FCSTD DOCUMENT  (FreeCAD 0.18.4R)
Label: voron-0
License: CreativeCommons Attribution-ShareAlike
LicenseURL: http://creativecommons.org/licenses/by-sa/4.0/
objects: Part::Feature×202, App::Part×102, Sketcher::SketchObject×45, PartDesign::Pad×42, PartDesign::Body×37, Mesh::Feature×32, App::DocumentObjectGroup×5, PartDesign::ShapeBinder×4, PartDesign::Line×4, App::DocumentObjectGroupPython×1, PartDesign::Hole×1, PartDesign::Pocket×1
note: 380 computed .brp shape members not serialized (recipe doc carries the construction recipe); baked Part::Feature solids carry a one-line shape summary decoded from their .brp

FEATURE [App::DocumentObjectGroupPython] ExplodedAssembly  # scripted group (container) (typed FeaturePython)
  AnimationStep = 0
  CurrentTrajectory = 0
  InAnimation = false
  RemoveAllTrajectories = false
  ResetAnimation = false
FEATURE [Sketcher::SketchObject] Sketch
  MapMode = 5
  Support = -> [XY_Plane001]
  sketch-geometry (4):
    g0: LineSegment StartX=-115 StartY=115 StartZ=0 EndX=115 EndY=115 EndZ=0
    g1: LineSegment StartX=115 StartY=115 StartZ=0 EndX=115 EndY=-115 EndZ=0
    g2: LineSegment StartX=115 StartY=-115 StartZ=0 EndX=-115 EndY=-115 EndZ=0
    g3: LineSegment StartX=-115 StartY=-115 StartZ=0 EndX=-115 EndY=115 EndZ=0
  constraints (11):
    c: Coincident(g0,g1)
    c: Coincident(g1,g2)
    c: Coincident(g2,g3)
    c: Coincident(g3,g0)
    c: Horizontal(g0)
    c: Horizontal(g2)
    c: Vertical(g1)
    c: Vertical(g3)
    c: Symmetric(g0,g1,g-1)
    c: Equal(g3,g0)
    c: DistanceY(g3,g3) = 230
FEATURE [PartDesign::Pad] Pad
  Length = 280
  Length2 = 100
  Midplane = true
  Profile = -> Sketch
  Refine = true
  Type = 0
FEATURE [PartDesign::Body] Body
  Group = -> [Sketch,Pad]
  Origin = -> Origin001
  Tip = -> Pad
FEATURE [Sketcher::SketchObject] Sketch001
  MapMode = 5
  Placement = pos=(0,0,0) rot=(1,0,0;1.5708rad)
  Support = -> [XZ_Plane004]
  sketch-geometry (52):
    g0: LineSegment [constr] StartX=-7.5 StartY=7.5 StartZ=0 EndX=7.5 EndY=7.5 EndZ=0
    g1: LineSegment [constr] StartX=7.5 StartY=7.5 StartZ=0 EndX=7.5 EndY=-7.5 EndZ=0
    g2: LineSegment [constr] StartX=7.5 StartY=-7.5 StartZ=0 EndX=-7.5 EndY=-7.5 EndZ=0
    g3: LineSegment [constr] StartX=-7.5 StartY=-7.5 StartZ=0 EndX=-7.5 EndY=7.5 EndZ=0
    g4: LineSegment StartX=-2.09289 StartY=2.8 StartZ=0 EndX=2.09289 EndY=2.8 EndZ=0
    g5: LineSegment StartX=2.09289 StartY=2.8 StartZ=0 EndX=4.7 EndY=5.40711 EndZ=0
    g6: LineSegment StartX=4.7 StartY=5.40711 StartZ=0 EndX=4.7 EndY=6.5 EndZ=0
    g7: LineSegment StartX=4.7 StartY=6.5 StartZ=0 EndX=3.1 EndY=6.5 EndZ=0
    g8: LineSegment StartX=3.1 StartY=6.5 StartZ=0 EndX=3.1 EndY=7.5 EndZ=0
    g9: LineSegment StartX=3.1 StartY=7.5 StartZ=0 EndX=6.5 EndY=7.5 EndZ=0
    g10: LineSegment StartX=7.5 StartY=6.5 StartZ=0 EndX=7.5 EndY=3.1 EndZ=0
    g11: LineSegment StartX=7.5 StartY=3.1 StartZ=0 EndX=6.5 EndY=3.1 EndZ=0
    g12: LineSegment StartX=6.5 StartY=3.1 StartZ=0 EndX=6.5 EndY=4.7 EndZ=0
    g13: LineSegment StartX=6.5 StartY=4.7 StartZ=0 EndX=5.40711 EndY=4.7 EndZ=0
    g14: LineSegment StartX=5.40711 StartY=4.7 StartZ=0 EndX=2.8 EndY=2.09289 EndZ=0
    g15: LineSegment StartX=2.8 StartY=2.09289 StartZ=0 EndX=2.8 EndY=-2.09289 EndZ=0
    g16: LineSegment StartX=2.8 StartY=-2.09289 StartZ=0 EndX=5.40711 EndY=-4.7 EndZ=0
    g17: LineSegment StartX=5.40711 StartY=-4.7 StartZ=0 EndX=6.5 EndY=-4.7 EndZ=0
    g18: LineSegment StartX=6.5 StartY=-4.7 StartZ=0 EndX=6.5 EndY=-3.1 EndZ=0
    g19: LineSegment StartX=6.5 StartY=-3.1 StartZ=0 EndX=7.5 EndY=-3.1 EndZ=0
    g20: LineSegment StartX=7.5 StartY=-3.1 StartZ=0 EndX=7.5 EndY=-6.5 EndZ=0
    g21: LineSegment StartX=6.5 StartY=-7.5 StartZ=0 EndX=3.1 EndY=-7.5 EndZ=0
    g22: LineSegment StartX=3.1 StartY=-7.5 StartZ=0 EndX=3.1 EndY=-6.5 EndZ=0
    g23: LineSegment StartX=3.1 StartY=-6.5 StartZ=0 EndX=4.7 EndY=-6.5 EndZ=0
    g24: LineSegment StartX=4.7 StartY=-6.5 StartZ=0 EndX=4.7 EndY=-5.40711 EndZ=0
    g25: LineSegment StartX=4.7 StartY=-5.40711 StartZ=0 EndX=2.09289 EndY=-2.8 EndZ=0
    g26: LineSegment StartX=2.09289 StartY=-2.8 StartZ=0 EndX=-2.09289 EndY=-2.8 EndZ=0
    g27: LineSegment StartX=-2.09289 StartY=-2.8 StartZ=0 EndX=-4.7 EndY=-5.40711 EndZ=0
    g28: LineSegment StartX=-4.7 StartY=-5.40711 StartZ=0 EndX=-4.7 EndY=-6.5 EndZ=0
    g29: LineSegment StartX=-4.7 StartY=-6.5 StartZ=0 EndX=-3.1 EndY=-6.5 EndZ=0
    g30: LineSegment StartX=-3.1 StartY=-6.5 StartZ=0 EndX=-3.1 EndY=-7.5 EndZ=0
    g31: LineSegment StartX=-3.1 StartY=-7.5 StartZ=0 EndX=-6.5 EndY=-7.5 EndZ=0
    g32: LineSegment StartX=-7.5 StartY=-6.5 StartZ=0 EndX=-7.5 EndY=-3.1 EndZ=0
    g33: LineSegment StartX=-7.5 StartY=-3.1 StartZ=0 EndX=-6.5 EndY=-3.1 EndZ=0
    g34: LineSegment StartX=-6.5 StartY=-3.1 StartZ=0 EndX=-6.5 EndY=-4.7 EndZ=0
    g35: LineSegment StartX=-6.5 StartY=-4.7 StartZ=0 EndX=-5.40711 EndY=-4.7 EndZ=0
    g36: LineSegment StartX=-5.40711 StartY=-4.7 StartZ=0 EndX=-2.8 EndY=-2.09289 EndZ=0
    g37: LineSegment StartX=-2.8 StartY=-2.09289 StartZ=0 EndX=-2.8 EndY=2.09289 EndZ=0
    g38: LineSegment StartX=-2.8 StartY=2.09289 StartZ=0 EndX=-5.40711 EndY=4.7 EndZ=0
    g39: LineSegment StartX=-5.40711 StartY=4.7 StartZ=0 EndX=-6.5 EndY=4.7 EndZ=0
    g40: LineSegment StartX=-6.5 StartY=4.7 StartZ=0 EndX=-6.5 EndY=3.1 EndZ=0
    g41: LineSegment StartX=-6.5 StartY=3.1 StartZ=0 EndX=-7.5 EndY=3.1 EndZ=0
    g42: LineSegment StartX=-7.5 StartY=3.1 StartZ=0 EndX=-7.5 EndY=6.5 EndZ=0
    g43: LineSegment StartX=-6.5 StartY=7.5 StartZ=0 EndX=-3.1 EndY=7.5 EndZ=0
    g44: LineSegment StartX=-3.1 StartY=7.5 StartZ=0 EndX=-3.1 EndY=6.5 EndZ=0
    g45: LineSegment StartX=-3.1 StartY=6.5 StartZ=0 EndX=-4.7 EndY=6.5 EndZ=0
    g46: LineSegment StartX=-4.7 StartY=6.5 StartZ=0 EndX=-4.7 EndY=5.40711 EndZ=0
    g47: LineSegment StartX=-4.7 StartY=5.40711 StartZ=0 EndX=-2.09289 EndY=2.8 EndZ=0
    g48: ArcOfCircle CenterX=-6.5 CenterY=6.5 CenterZ=0 NormalX=0 NormalY=0 NormalZ=1 AngleXU=0 Radius=1 StartAngle=1.5708 EndAngle=3.14159
    g49: ArcOfCircle CenterX=6.5 CenterY=6.5 CenterZ=0 NormalX=0 NormalY=0 NormalZ=1 AngleXU=0 Radius=1 StartAngle=0 EndAngle=1.5708
    g50: ArcOfCircle CenterX=6.5 CenterY=-6.5 CenterZ=0 NormalX=0 NormalY=0 NormalZ=1 AngleXU=0 Radius=1 StartAngle=4.71239 EndAngle=6.28319
    g51: ArcOfCircle CenterX=-6.5 CenterY=-6.5 CenterZ=0 NormalX=0 NormalY=0 NormalZ=1 AngleXU=0 Radius=1 StartAngle=3.14159 EndAngle=4.71239
  constraints (140):
    c: Coincident(g0,g1)
    c: Coincident(g1,g2)
    c: Coincident(g2,g3)
    c: Coincident(g3,g0)
    c: Horizontal(g0)
    c: Horizontal(g2)
    c: Vertical(g1)
    c: Vertical(g3)
    c: Symmetric(g0,g1,g-1)
    c: Equal(g3,g0)
    c: DistanceY(g3,g3) = 15
    c: Coincident(g4,g5)
    c: Coincident(g5,g6)
    c: Coincident(g6,g7)
    c: Coincident(g7,g8)
    c: Vertical(g8)
    c: Coincident(g8,g9)
    c: Horizontal(g9)
    c: Vertical(g10)
    c: Coincident(g10,g11)
    c: Horizontal(g11)
    c: Coincident(g11,g12)
    c: Vertical(g12)
    c: Coincident(g12,g13)
    c: Horizontal(g13)
    c: Coincident(g13,g14)
    c: Coincident(g14,g15)
    c: Coincident(g15,g16)
    c: Coincident(g16,g17)
    c: Horizontal(g17)
    c: Coincident(g17,g18)
    c: Coincident(g18,g19)
    c: Coincident(g19,g20)
    c: Vertical(g20)
    c: Horizontal(g21)
    c: Coincident(g21,g22)
    c: Coincident(g22,g23)
    c: Horizontal(g23)
    c: Coincident(g23,g24)
    c: Coincident(g24,g25)
    c: Coincident(g25,g26)
    c: Coincident(g26,g27)
    c: Coincident(g27,g28)
    c: Vertical(g28)
    c: Coincident(g28,g29)
    c: Coincident(g29,g30)
    c: Coincident(g30,g31)
    c: Coincident(g32,g33)
    c: Coincident(g33,g34)
    c: Coincident(g34,g35)
    c: Coincident(g35,g36)
    c: Coincident(g36,g37)
    c: Coincident(g37,g38)
    c: Coincident(g38,g39)
    c: Coincident(g39,g40)
    c: Coincident(g40,g41)
    c: Coincident(g41,g42)
    c: Vertical(g42)
    c: Horizontal(g43)
    c: Coincident(g43,g44)
    c: Coincident(g44,g45)
    c: Horizontal(g45)
    c: Coincident(g45,g46)
    c: Coincident(g46,g47)
    c: Coincident(g4,g47)
    c: Tangent(g42,g48) = 1.5708
    c: Tangent(g43,g48) = 1.5708
    c: Tangent(g9,g49) = 1.5708
    c: Tangent(g10,g49) = 1.5708
    c: Tangent(g20,g50) = 1.5708
    c: Tangent(g21,g50) = 1.5708
    c: Tangent(g32,g51) = 1.5708
    c: Tangent(g31,g51) = 1.5708
    c: Horizontal(g41)
    c: Horizontal(g39)
    c: Horizontal(g19)
    c: Horizontal(g31)
    c: Horizontal(g35)
    c: Horizontal(g33)
    c: Vertical(g40)
    c: Vertical(g46)
    c: Vertical(g18)
    c: Vertical(g22)
    c: Vertical(g24)
    c: Vertical(g30)
    c: Vertical(g34)
    c: Vertical(g32)
    c: PointOnObject(g21,g2)
    c: PointOnObject(g32,g3)
    c: Vertical(g6)
    c: PointOnObject(g10,g1)
    c: Equal(g48,g49)
    c: Equal(g49,g50)
    c: Equal(g33,g41)
    c: Equal(g41,g30)
    c: Equal(g30,g22)
    c: Equal(g22,g19)
    c: Equal(g19,g11)
    c: Equal(g11,g8)
    c: Equal(g8,g44)
    c: Symmetric(g45,g6,g-2)
    c: DistanceX(g45,g6) = 9.4
    c: DistanceX(g43,g8) = 6.2
    c: Equal(g43,g42)
    c: Equal(g42,g32)
    c: DistanceY(g44,g44) = 1
    c: Equal(g31,g43)
    c: Equal(g43,g21)
    c: Equal(g21,g20)
    c: Equal(g20,g10)
    c: Radius(g49) = 1
    c: Symmetric(g37,g14,g-2)
    c: DistanceX(g37,g14) = 5.6
    c: Symmetric(g43,g8,g-2)
    c: Symmetric(g4,g26,g-1)
    c: DistanceY(g26,g4) = 5.6
    c: Symmetric(g4,g4,g-2)
    c: Equal(g45,g40)
    c: Equal(g45,g7)
    c: Equal(g7,g12)
    c: Equal(g12,g34)
    c: Equal(g34,g29)
    c: Equal(g29,g23)
    c: Equal(g23,g18)
    c: Equal(g39,g46)
    c: Equal(g46,g6)
    c: Equal(g6,g13)
    c: Equal(g13,g17)
    c: Equal(g17,g24)
    c: Equal(g24,g35)
    c: Equal(g35,g28)
    c: Parallel(g38,g47)
    c: Angle(g4,g47) = 2.35619
    c: Symmetric(g38,g35,g-1)
    c: Symmetric(g37,g36,g-1)
    c: Symmetric(g27,g46,g-1)
    c: Distance(g37,g4) = 1
    c: Symmetric(g27,g24,g-2)
    c: Symmetric(g26,g25,g-2)
    c: Symmetric(g36,g15,g-2)
FEATURE [PartDesign::Body] Body002  label="1515-extrusion"
  Group = -> [Sketch001]
  Origin = -> Origin004
FEATURE [Sketcher::SketchObject] Sketch003
  MapMode = 5
  Placement = pos=(0,0,0) rot=(1,0,0;1.5708rad)
  Support = -> [XZ_Plane005]
  sketch-geometry (52):
    g0: LineSegment [constr] StartX=-7.5 StartY=7.5 StartZ=0 EndX=7.5 EndY=7.5 EndZ=0
    g1: LineSegment [constr] StartX=7.5 StartY=7.5 StartZ=0 EndX=7.5 EndY=-7.5 EndZ=0
    g2: LineSegment [constr] StartX=7.5 StartY=-7.5 StartZ=0 EndX=-7.5 EndY=-7.5 EndZ=0
    g3: LineSegment [constr] StartX=-7.5 StartY=-7.5 StartZ=0 EndX=-7.5 EndY=7.5 EndZ=0
    g4: LineSegment StartX=-2.09289 StartY=2.8 StartZ=0 EndX=2.09289 EndY=2.8 EndZ=0
    g5: LineSegment StartX=2.09289 StartY=2.8 StartZ=0 EndX=4.7 EndY=5.40711 EndZ=0
    g6: LineSegment StartX=4.7 StartY=5.40711 StartZ=0 EndX=4.7 EndY=6.5 EndZ=0
    g7: LineSegment StartX=4.7 StartY=6.5 StartZ=0 EndX=3.1 EndY=6.5 EndZ=0
    g8: LineSegment StartX=3.1 StartY=6.5 StartZ=0 EndX=3.1 EndY=7.5 EndZ=0
    g9: LineSegment StartX=3.1 StartY=7.5 StartZ=0 EndX=6.5 EndY=7.5 EndZ=0
    g10: LineSegment StartX=7.5 StartY=6.5 StartZ=0 EndX=7.5 EndY=3.1 EndZ=0
    g11: LineSegment StartX=7.5 StartY=3.1 StartZ=0 EndX=6.5 EndY=3.1 EndZ=0
    g12: LineSegment StartX=6.5 StartY=3.1 StartZ=0 EndX=6.5 EndY=4.7 EndZ=0
    g13: LineSegment StartX=6.5 StartY=4.7 StartZ=0 EndX=5.40711 EndY=4.7 EndZ=0
    g14: LineSegment StartX=5.40711 StartY=4.7 StartZ=0 EndX=2.8 EndY=2.09289 EndZ=0
    g15: LineSegment StartX=2.8 StartY=2.09289 StartZ=0 EndX=2.8 EndY=-2.09289 EndZ=0
    g16: LineSegment StartX=2.8 StartY=-2.09289 StartZ=0 EndX=5.40711 EndY=-4.7 EndZ=0
    g17: LineSegment StartX=5.40711 StartY=-4.7 StartZ=0 EndX=6.5 EndY=-4.7 EndZ=0
    g18: LineSegment StartX=6.5 StartY=-4.7 StartZ=0 EndX=6.5 EndY=-3.1 EndZ=0
    g19: LineSegment StartX=6.5 StartY=-3.1 StartZ=0 EndX=7.5 EndY=-3.1 EndZ=0
    g20: LineSegment StartX=7.5 StartY=-3.1 StartZ=0 EndX=7.5 EndY=-6.5 EndZ=0
    g21: LineSegment StartX=6.5 StartY=-7.5 StartZ=0 EndX=3.1 EndY=-7.5 EndZ=0
    g22: LineSegment StartX=3.1 StartY=-7.5 StartZ=0 EndX=3.1 EndY=-6.5 EndZ=0
    g23: LineSegment StartX=3.1 StartY=-6.5 StartZ=0 EndX=4.7 EndY=-6.5 EndZ=0
    g24: LineSegment StartX=4.7 StartY=-6.5 StartZ=0 EndX=4.7 EndY=-5.40711 EndZ=0
    g25: LineSegment StartX=4.7 StartY=-5.40711 StartZ=0 EndX=2.09289 EndY=-2.8 EndZ=0
    g26: LineSegment StartX=2.09289 StartY=-2.8 StartZ=0 EndX=-2.09289 EndY=-2.8 EndZ=0
    g27: LineSegment StartX=-2.09289 StartY=-2.8 StartZ=0 EndX=-4.7 EndY=-5.40711 EndZ=0
    g28: LineSegment StartX=-4.7 StartY=-5.40711 StartZ=0 EndX=-4.7 EndY=-6.5 EndZ=0
    g29: LineSegment StartX=-4.7 StartY=-6.5 StartZ=0 EndX=-3.1 EndY=-6.5 EndZ=0
    g30: LineSegment StartX=-3.1 StartY=-6.5 StartZ=0 EndX=-3.1 EndY=-7.5 EndZ=0
    g31: LineSegment StartX=-3.1 StartY=-7.5 StartZ=0 EndX=-6.5 EndY=-7.5 EndZ=0
    g32: LineSegment StartX=-7.5 StartY=-6.5 StartZ=0 EndX=-7.5 EndY=-3.1 EndZ=0
    g33: LineSegment StartX=-7.5 StartY=-3.1 StartZ=0 EndX=-6.5 EndY=-3.1 EndZ=0
    g34: LineSegment StartX=-6.5 StartY=-3.1 StartZ=0 EndX=-6.5 EndY=-4.7 EndZ=0
    g35: LineSegment StartX=-6.5 StartY=-4.7 StartZ=0 EndX=-5.40711 EndY=-4.7 EndZ=0
    g36: LineSegment StartX=-5.40711 StartY=-4.7 StartZ=0 EndX=-2.8 EndY=-2.09289 EndZ=0
    g37: LineSegment StartX=-2.8 StartY=-2.09289 StartZ=0 EndX=-2.8 EndY=2.09289 EndZ=0
    g38: LineSegment StartX=-2.8 StartY=2.09289 StartZ=0 EndX=-5.40711 EndY=4.7 EndZ=0
    g39: LineSegment StartX=-5.40711 StartY=4.7 StartZ=0 EndX=-6.5 EndY=4.7 EndZ=0
    g40: LineSegment StartX=-6.5 StartY=4.7 StartZ=0 EndX=-6.5 EndY=3.1 EndZ=0
    g41: LineSegment StartX=-6.5 StartY=3.1 StartZ=0 EndX=-7.5 EndY=3.1 EndZ=0
    g42: LineSegment StartX=-7.5 StartY=3.1 StartZ=0 EndX=-7.5 EndY=6.5 EndZ=0
    g43: LineSegment StartX=-6.5 StartY=7.5 StartZ=0 EndX=-3.1 EndY=7.5 EndZ=0
    g44: LineSegment StartX=-3.1 StartY=7.5 StartZ=0 EndX=-3.1 EndY=6.5 EndZ=0
    g45: LineSegment StartX=-3.1 StartY=6.5 StartZ=0 EndX=-4.7 EndY=6.5 EndZ=0
    g46: LineSegment StartX=-4.7 StartY=6.5 StartZ=0 EndX=-4.7 EndY=5.40711 EndZ=0
    g47: LineSegment StartX=-4.7 StartY=5.40711 StartZ=0 EndX=-2.09289 EndY=2.8 EndZ=0
    g48: ArcOfCircle CenterX=-6.5 CenterY=6.5 CenterZ=0 NormalX=0 NormalY=0 NormalZ=1 AngleXU=0 Radius=1 StartAngle=1.5708 EndAngle=3.14159
    g49: ArcOfCircle CenterX=6.5 CenterY=6.5 CenterZ=0 NormalX=0 NormalY=0 NormalZ=1 AngleXU=0 Radius=1 StartAngle=0 EndAngle=1.5708
    g50: ArcOfCircle CenterX=6.5 CenterY=-6.5 CenterZ=0 NormalX=0 NormalY=0 NormalZ=1 AngleXU=0 Radius=1 StartAngle=4.71239 EndAngle=6.28319
    g51: ArcOfCircle CenterX=-6.5 CenterY=-6.5 CenterZ=0 NormalX=0 NormalY=0 NormalZ=1 AngleXU=0 Radius=1 StartAngle=3.14159 EndAngle=4.71239
  constraints (140):
    c: Coincident(g0,g1)
    c: Coincident(g1,g2)
    c: Coincident(g2,g3)
    c: Coincident(g3,g0)
    c: Horizontal(g0)
    c: Horizontal(g2)
    c: Vertical(g1)
    c: Vertical(g3)
    c: Symmetric(g0,g1,g-1)
    c: Equal(g3,g0)
    c: DistanceY(g3,g3) = 15
    c: Coincident(g4,g5)
    c: Coincident(g5,g6)
    c: Coincident(g6,g7)
    c: Coincident(g7,g8)
    c: Vertical(g8)
    c: Coincident(g8,g9)
    c: Horizontal(g9)
    c: Vertical(g10)
    c: Coincident(g10,g11)
    c: Horizontal(g11)
    c: Coincident(g11,g12)
    c: Vertical(g12)
    c: Coincident(g12,g13)
    c: Horizontal(g13)
    c: Coincident(g13,g14)
    c: Coincident(g14,g15)
    c: Coincident(g15,g16)
    c: Coincident(g16,g17)
    c: Horizontal(g17)
    c: Coincident(g17,g18)
    c: Coincident(g18,g19)
    c: Coincident(g19,g20)
    c: Vertical(g20)
    c: Horizontal(g21)
    c: Coincident(g21,g22)
    c: Coincident(g22,g23)
    c: Horizontal(g23)
    c: Coincident(g23,g24)
    c: Coincident(g24,g25)
    c: Coincident(g25,g26)
    c: Coincident(g26,g27)
    c: Coincident(g27,g28)
    c: Vertical(g28)
    c: Coincident(g28,g29)
    c: Coincident(g29,g30)
    c: Coincident(g30,g31)
    c: Coincident(g32,g33)
    c: Coincident(g33,g34)
    c: Coincident(g34,g35)
    c: Coincident(g35,g36)
    c: Coincident(g36,g37)
    c: Coincident(g37,g38)
    c: Coincident(g38,g39)
    c: Coincident(g39,g40)
    c: Coincident(g40,g41)
    c: Coincident(g41,g42)
    c: Vertical(g42)
    c: Horizontal(g43)
    c: Coincident(g43,g44)
    c: Coincident(g44,g45)
    c: Horizontal(g45)
    c: Coincident(g45,g46)
    c: Coincident(g46,g47)
    c: Coincident(g4,g47)
    c: Tangent(g42,g48) = 1.5708
    c: Tangent(g43,g48) = 1.5708
    c: Tangent(g9,g49) = 1.5708
    c: Tangent(g10,g49) = 1.5708
    c: Tangent(g20,g50) = 1.5708
    c: Tangent(g21,g50) = 1.5708
    c: Tangent(g32,g51) = 1.5708
    c: Tangent(g31,g51) = 1.5708
    c: Horizontal(g41)
    c: Horizontal(g39)
    c: Horizontal(g19)
    c: Horizontal(g31)
    c: Horizontal(g35)
    c: Horizontal(g33)
    c: Vertical(g40)
    c: Vertical(g46)
    c: Vertical(g18)
    c: Vertical(g22)
    c: Vertical(g24)
    c: Vertical(g30)
    c: Vertical(g34)
    c: Vertical(g32)
    c: PointOnObject(g21,g2)
    c: PointOnObject(g32,g3)
    c: Vertical(g6)
    c: PointOnObject(g10,g1)
    c: Equal(g48,g49)
    c: Equal(g49,g50)
    c: Equal(g33,g41)
    c: Equal(g41,g30)
    c: Equal(g30,g22)
    c: Equal(g22,g19)
    c: Equal(g19,g11)
    c: Equal(g11,g8)
    c: Equal(g8,g44)
    c: Symmetric(g45,g6,g-2)
    c: DistanceX(g45,g6) = 9.4
    c: DistanceX(g43,g8) = 6.2
    c: Equal(g43,g42)
    c: Equal(g42,g32)
    c: DistanceY(g44,g44) = 1
    c: Equal(g31,g43)
    c: Equal(g43,g21)
    c: Equal(g21,g20)
    c: Equal(g20,g10)
    c: Radius(g49) = 1
    c: Symmetric(g37,g14,g-2)
    c: DistanceX(g37,g14) = 5.6
    c: Symmetric(g43,g8,g-2)
    c: Symmetric(g4,g26,g-1)
    c: DistanceY(g26,g4) = 5.6
    c: Symmetric(g4,g4,g-2)
    c: Equal(g45,g40)
    c: Equal(g45,g7)
    c: Equal(g7,g12)
    c: Equal(g12,g34)
    c: Equal(g34,g29)
    c: Equal(g29,g23)
    c: Equal(g23,g18)
    c: Equal(g39,g46)
    c: Equal(g46,g6)
    c: Equal(g6,g13)
    c: Equal(g13,g17)
    c: Equal(g17,g24)
    c: Equal(g24,g35)
    c: Equal(g35,g28)
    c: Parallel(g38,g47)
    c: Angle(g4,g47) = 2.35619
    c: Symmetric(g38,g35,g-1)
    c: Symmetric(g37,g36,g-1)
    c: Symmetric(g27,g46,g-1)
    c: Distance(g37,g4) = 1
    c: Symmetric(g27,g24,g-2)
    c: Symmetric(g26,g25,g-2)
    c: Symmetric(g36,g15,g-2)
FEATURE [PartDesign::Pad] Pad002
  Length = 270
  Length2 = 100
  Placement = pos=(0,0,0) rot=(1,0,0;1.5708rad)
  Profile = -> Sketch003
  Refine = true
  Type = 0
FEATURE [PartDesign::Body] Body003  label="extrusion-009"
  Group = -> [Sketch003,Pad002]
  Origin = -> Origin005
  Placement = pos=(-152.5,-99.4,0) rot=(0,0,1;3.14159rad)
  Tip = -> Pad002
FEATURE [Sketcher::SketchObject] Sketch006
  MapMode = 5
  Placement = pos=(0,0,0) rot=(1,0,0;1.5708rad)
  Support = -> [XZ_Plane009]
  sketch-geometry (52):
    g0: LineSegment [constr] StartX=-7.5 StartY=7.5 StartZ=0 EndX=7.5 EndY=7.5 EndZ=0
    g1: LineSegment [constr] StartX=7.5 StartY=7.5 StartZ=0 EndX=7.5 EndY=-7.5 EndZ=0
    g2: LineSegment [constr] StartX=7.5 StartY=-7.5 StartZ=0 EndX=-7.5 EndY=-7.5 EndZ=0
    g3: LineSegment [constr] StartX=-7.5 StartY=-7.5 StartZ=0 EndX=-7.5 EndY=7.5 EndZ=0
    g4: LineSegment StartX=-2.09289 StartY=2.8 StartZ=0 EndX=2.09289 EndY=2.8 EndZ=0
    g5: LineSegment StartX=2.09289 StartY=2.8 StartZ=0 EndX=4.7 EndY=5.40711 EndZ=0
    g6: LineSegment StartX=4.7 StartY=5.40711 StartZ=0 EndX=4.7 EndY=6.5 EndZ=0
    g7: LineSegment StartX=4.7 StartY=6.5 StartZ=0 EndX=3.1 EndY=6.5 EndZ=0
    g8: LineSegment StartX=3.1 StartY=6.5 StartZ=0 EndX=3.1 EndY=7.5 EndZ=0
    g9: LineSegment StartX=3.1 StartY=7.5 StartZ=0 EndX=6.5 EndY=7.5 EndZ=0
    g10: LineSegment StartX=7.5 StartY=6.5 StartZ=0 EndX=7.5 EndY=3.1 EndZ=0
    g11: LineSegment StartX=7.5 StartY=3.1 StartZ=0 EndX=6.5 EndY=3.1 EndZ=0
    g12: LineSegment StartX=6.5 StartY=3.1 StartZ=0 EndX=6.5 EndY=4.7 EndZ=0
    g13: LineSegment StartX=6.5 StartY=4.7 StartZ=0 EndX=5.40711 EndY=4.7 EndZ=0
    g14: LineSegment StartX=5.40711 StartY=4.7 StartZ=0 EndX=2.8 EndY=2.09289 EndZ=0
    g15: LineSegment StartX=2.8 StartY=2.09289 StartZ=0 EndX=2.8 EndY=-2.09289 EndZ=0
    g16: LineSegment StartX=2.8 StartY=-2.09289 StartZ=0 EndX=5.40711 EndY=-4.7 EndZ=0
    g17: LineSegment StartX=5.40711 StartY=-4.7 StartZ=0 EndX=6.5 EndY=-4.7 EndZ=0
    g18: LineSegment StartX=6.5 StartY=-4.7 StartZ=0 EndX=6.5 EndY=-3.1 EndZ=0
    g19: LineSegment StartX=6.5 StartY=-3.1 StartZ=0 EndX=7.5 EndY=-3.1 EndZ=0
    g20: LineSegment StartX=7.5 StartY=-3.1 StartZ=0 EndX=7.5 EndY=-6.5 EndZ=0
    g21: LineSegment StartX=6.5 StartY=-7.5 StartZ=0 EndX=3.1 EndY=-7.5 EndZ=0
    g22: LineSegment StartX=3.1 StartY=-7.5 StartZ=0 EndX=3.1 EndY=-6.5 EndZ=0
    g23: LineSegment StartX=3.1 StartY=-6.5 StartZ=0 EndX=4.7 EndY=-6.5 EndZ=0
    g24: LineSegment StartX=4.7 StartY=-6.5 StartZ=0 EndX=4.7 EndY=-5.40711 EndZ=0
    g25: LineSegment StartX=4.7 StartY=-5.40711 StartZ=0 EndX=2.09289 EndY=-2.8 EndZ=0
    g26: LineSegment StartX=2.09289 StartY=-2.8 StartZ=0 EndX=-2.09289 EndY=-2.8 EndZ=0
    g27: LineSegment StartX=-2.09289 StartY=-2.8 StartZ=0 EndX=-4.7 EndY=-5.40711 EndZ=0
    g28: LineSegment StartX=-4.7 StartY=-5.40711 StartZ=0 EndX=-4.7 EndY=-6.5 EndZ=0
    g29: LineSegment StartX=-4.7 StartY=-6.5 StartZ=0 EndX=-3.1 EndY=-6.5 EndZ=0
    g30: LineSegment StartX=-3.1 StartY=-6.5 StartZ=0 EndX=-3.1 EndY=-7.5 EndZ=0
    g31: LineSegment StartX=-3.1 StartY=-7.5 StartZ=0 EndX=-6.5 EndY=-7.5 EndZ=0
    g32: LineSegment StartX=-7.5 StartY=-6.5 StartZ=0 EndX=-7.5 EndY=-3.1 EndZ=0
    g33: LineSegment StartX=-7.5 StartY=-3.1 StartZ=0 EndX=-6.5 EndY=-3.1 EndZ=0
    g34: LineSegment StartX=-6.5 StartY=-3.1 StartZ=0 EndX=-6.5 EndY=-4.7 EndZ=0
    g35: LineSegment StartX=-6.5 StartY=-4.7 StartZ=0 EndX=-5.40711 EndY=-4.7 EndZ=0
    g36: LineSegment StartX=-5.40711 StartY=-4.7 StartZ=0 EndX=-2.8 EndY=-2.09289 EndZ=0
    g37: LineSegment StartX=-2.8 StartY=-2.09289 StartZ=0 EndX=-2.8 EndY=2.09289 EndZ=0
    g38: LineSegment StartX=-2.8 StartY=2.09289 StartZ=0 EndX=-5.40711 EndY=4.7 EndZ=0
    g39: LineSegment StartX=-5.40711 StartY=4.7 StartZ=0 EndX=-6.5 EndY=4.7 EndZ=0
    g40: LineSegment StartX=-6.5 StartY=4.7 StartZ=0 EndX=-6.5 EndY=3.1 EndZ=0
    g41: LineSegment StartX=-6.5 StartY=3.1 StartZ=0 EndX=-7.5 EndY=3.1 EndZ=0
    g42: LineSegment StartX=-7.5 StartY=3.1 StartZ=0 EndX=-7.5 EndY=6.5 EndZ=0
    g43: LineSegment StartX=-6.5 StartY=7.5 StartZ=0 EndX=-3.1 EndY=7.5 EndZ=0
    g44: LineSegment StartX=-3.1 StartY=7.5 StartZ=0 EndX=-3.1 EndY=6.5 EndZ=0
    g45: LineSegment StartX=-3.1 StartY=6.5 StartZ=0 EndX=-4.7 EndY=6.5 EndZ=0
    g46: LineSegment StartX=-4.7 StartY=6.5 StartZ=0 EndX=-4.7 EndY=5.40711 EndZ=0
    g47: LineSegment StartX=-4.7 StartY=5.40711 StartZ=0 EndX=-2.09289 EndY=2.8 EndZ=0
    g48: ArcOfCircle CenterX=-6.5 CenterY=6.5 CenterZ=0 NormalX=0 NormalY=0 NormalZ=1 AngleXU=0 Radius=1 StartAngle=1.5708 EndAngle=3.14159
    g49: ArcOfCircle CenterX=6.5 CenterY=6.5 CenterZ=0 NormalX=0 NormalY=0 NormalZ=1 AngleXU=0 Radius=1 StartAngle=0 EndAngle=1.5708
    g50: ArcOfCircle CenterX=6.5 CenterY=-6.5 CenterZ=0 NormalX=0 NormalY=0 NormalZ=1 AngleXU=0 Radius=1 StartAngle=4.71239 EndAngle=6.28319
    g51: ArcOfCircle CenterX=-6.5 CenterY=-6.5 CenterZ=0 NormalX=0 NormalY=0 NormalZ=1 AngleXU=0 Radius=1 StartAngle=3.14159 EndAngle=4.71239
  constraints (140):
    c: Coincident(g0,g1)
    c: Coincident(g1,g2)
    c: Coincident(g2,g3)
    c: Coincident(g3,g0)
    c: Horizontal(g0)
    c: Horizontal(g2)
    c: Vertical(g1)
    c: Vertical(g3)
    c: Symmetric(g0,g1,g-1)
    c: Equal(g3,g0)
    c: DistanceY(g3,g3) = 15
    c: Coincident(g4,g5)
    c: Coincident(g5,g6)
    c: Coincident(g6,g7)
    c: Coincident(g7,g8)
    c: Vertical(g8)
    c: Coincident(g8,g9)
    c: Horizontal(g9)
    c: Vertical(g10)
    c: Coincident(g10,g11)
    c: Horizontal(g11)
    c: Coincident(g11,g12)
    c: Vertical(g12)
    c: Coincident(g12,g13)
    c: Horizontal(g13)
    c: Coincident(g13,g14)
    c: Coincident(g14,g15)
    c: Coincident(g15,g16)
    c: Coincident(g16,g17)
    c: Horizontal(g17)
    c: Coincident(g17,g18)
    c: Coincident(g18,g19)
    c: Coincident(g19,g20)
    c: Vertical(g20)
    c: Horizontal(g21)
    c: Coincident(g21,g22)
    c: Coincident(g22,g23)
    c: Horizontal(g23)
    c: Coincident(g23,g24)
    c: Coincident(g24,g25)
    c: Coincident(g25,g26)
    c: Coincident(g26,g27)
    c: Coincident(g27,g28)
    c: Vertical(g28)
    c: Coincident(g28,g29)
    c: Coincident(g29,g30)
    c: Coincident(g30,g31)
    c: Coincident(g32,g33)
    c: Coincident(g33,g34)
    c: Coincident(g34,g35)
    c: Coincident(g35,g36)
    c: Coincident(g36,g37)
    c: Coincident(g37,g38)
    c: Coincident(g38,g39)
    c: Coincident(g39,g40)
    c: Coincident(g40,g41)
    c: Coincident(g41,g42)
    c: Vertical(g42)
    c: Horizontal(g43)
    c: Coincident(g43,g44)
    c: Coincident(g44,g45)
    c: Horizontal(g45)
    c: Coincident(g45,g46)
    c: Coincident(g46,g47)
    c: Coincident(g4,g47)
    c: Tangent(g42,g48) = 1.5708
    c: Tangent(g43,g48) = 1.5708
    c: Tangent(g9,g49) = 1.5708
    c: Tangent(g10,g49) = 1.5708
    c: Tangent(g20,g50) = 1.5708
    c: Tangent(g21,g50) = 1.5708
    c: Tangent(g32,g51) = 1.5708
    c: Tangent(g31,g51) = 1.5708
    c: Horizontal(g41)
    c: Horizontal(g39)
    c: Horizontal(g19)
    c: Horizontal(g31)
    c: Horizontal(g35)
    c: Horizontal(g33)
    c: Vertical(g40)
    c: Vertical(g46)
    c: Vertical(g18)
    c: Vertical(g22)
    c: Vertical(g24)
    c: Vertical(g30)
    c: Vertical(g34)
    c: Vertical(g32)
    c: PointOnObject(g21,g2)
    c: PointOnObject(g32,g3)
    c: Vertical(g6)
    c: PointOnObject(g10,g1)
    c: Equal(g48,g49)
    c: Equal(g49,g50)
    c: Equal(g33,g41)
    c: Equal(g41,g30)
    c: Equal(g30,g22)
    c: Equal(g22,g19)
    c: Equal(g19,g11)
    c: Equal(g11,g8)
    c: Equal(g8,g44)
    c: Symmetric(g45,g6,g-2)
    c: DistanceX(g45,g6) = 9.4
    c: DistanceX(g43,g8) = 6.2
    c: Equal(g43,g42)
    c: Equal(g42,g32)
    c: DistanceY(g44,g44) = 1
    c: Equal(g31,g43)
    c: Equal(g43,g21)
    c: Equal(g21,g20)
    c: Equal(g20,g10)
    c: Radius(g49) = 1
    c: Symmetric(g37,g14,g-2)
    c: DistanceX(g37,g14) = 5.6
    c: Symmetric(g43,g8,g-2)
    c: Symmetric(g4,g26,g-1)
    c: DistanceY(g26,g4) = 5.6
    c: Symmetric(g4,g4,g-2)
    c: Equal(g45,g40)
    c: Equal(g45,g7)
    c: Equal(g7,g12)
    c: Equal(g12,g34)
    c: Equal(g34,g29)
    c: Equal(g29,g23)
    c: Equal(g23,g18)
    c: Equal(g39,g46)
    c: Equal(g46,g6)
    c: Equal(g6,g13)
    c: Equal(g13,g17)
    c: Equal(g17,g24)
    c: Equal(g24,g35)
    c: Equal(g35,g28)
    c: Parallel(g38,g47)
    c: Angle(g4,g47) = 2.35619
    c: Symmetric(g38,g35,g-1)
    c: Symmetric(g37,g36,g-1)
    c: Symmetric(g27,g46,g-1)
    c: Distance(g37,g4) = 1
    c: Symmetric(g27,g24,g-2)
    c: Symmetric(g26,g25,g-2)
    c: Symmetric(g36,g15,g-2)
FEATURE [PartDesign::Pad] Pad004
  Length = 270
  Length2 = 100
  Placement = pos=(0,0,0) rot=(1,0,0;1.5708rad)
  Profile = -> Sketch006
  Refine = true
  Type = 0
FEATURE [PartDesign::Body] Body005  label="extrusion-010"
  Group = -> [Sketch006,Pad004]
  Origin = -> Origin009
  Placement = pos=(152.5,-99.5,0) rot=(0,0,1;3.14159rad)
  Tip = -> Pad004
FEATURE [Sketcher::SketchObject] Sketch007
  MapMode = 5
  Placement = pos=(0,0,0) rot=(1,0,0;1.5708rad)
  Support = -> [XZ_Plane010]
  sketch-geometry (52):
    g0: LineSegment [constr] StartX=-7.5 StartY=7.5 StartZ=0 EndX=7.5 EndY=7.5 EndZ=0
    g1: LineSegment [constr] StartX=7.5 StartY=7.5 StartZ=0 EndX=7.5 EndY=-7.5 EndZ=0
    g2: LineSegment [constr] StartX=7.5 StartY=-7.5 StartZ=0 EndX=-7.5 EndY=-7.5 EndZ=0
    g3: LineSegment [constr] StartX=-7.5 StartY=-7.5 StartZ=0 EndX=-7.5 EndY=7.5 EndZ=0
    g4: LineSegment StartX=-2.09289 StartY=2.8 StartZ=0 EndX=2.09289 EndY=2.8 EndZ=0
    g5: LineSegment StartX=2.09289 StartY=2.8 StartZ=0 EndX=4.7 EndY=5.40711 EndZ=0
    g6: LineSegment StartX=4.7 StartY=5.40711 StartZ=0 EndX=4.7 EndY=6.5 EndZ=0
    g7: LineSegment StartX=4.7 StartY=6.5 StartZ=0 EndX=3.1 EndY=6.5 EndZ=0
    g8: LineSegment StartX=3.1 StartY=6.5 StartZ=0 EndX=3.1 EndY=7.5 EndZ=0
    g9: LineSegment StartX=3.1 StartY=7.5 StartZ=0 EndX=6.5 EndY=7.5 EndZ=0
    g10: LineSegment StartX=7.5 StartY=6.5 StartZ=0 EndX=7.5 EndY=3.1 EndZ=0
    g11: LineSegment StartX=7.5 StartY=3.1 StartZ=0 EndX=6.5 EndY=3.1 EndZ=0
    g12: LineSegment StartX=6.5 StartY=3.1 StartZ=0 EndX=6.5 EndY=4.7 EndZ=0
    g13: LineSegment StartX=6.5 StartY=4.7 StartZ=0 EndX=5.40711 EndY=4.7 EndZ=0
    g14: LineSegment StartX=5.40711 StartY=4.7 StartZ=0 EndX=2.8 EndY=2.09289 EndZ=0
    g15: LineSegment StartX=2.8 StartY=2.09289 StartZ=0 EndX=2.8 EndY=-2.09289 EndZ=0
    g16: LineSegment StartX=2.8 StartY=-2.09289 StartZ=0 EndX=5.40711 EndY=-4.7 EndZ=0
    g17: LineSegment StartX=5.40711 StartY=-4.7 StartZ=0 EndX=6.5 EndY=-4.7 EndZ=0
    g18: LineSegment StartX=6.5 StartY=-4.7 StartZ=0 EndX=6.5 EndY=-3.1 EndZ=0
    g19: LineSegment StartX=6.5 StartY=-3.1 StartZ=0 EndX=7.5 EndY=-3.1 EndZ=0
    g20: LineSegment StartX=7.5 StartY=-3.1 StartZ=0 EndX=7.5 EndY=-6.5 EndZ=0
    g21: LineSegment StartX=6.5 StartY=-7.5 StartZ=0 EndX=3.1 EndY=-7.5 EndZ=0
    g22: LineSegment StartX=3.1 StartY=-7.5 StartZ=0 EndX=3.1 EndY=-6.5 EndZ=0
    g23: LineSegment StartX=3.1 StartY=-6.5 StartZ=0 EndX=4.7 EndY=-6.5 EndZ=0
    g24: LineSegment StartX=4.7 StartY=-6.5 StartZ=0 EndX=4.7 EndY=-5.40711 EndZ=0
    g25: LineSegment StartX=4.7 StartY=-5.40711 StartZ=0 EndX=2.09289 EndY=-2.8 EndZ=0
    g26: LineSegment StartX=2.09289 StartY=-2.8 StartZ=0 EndX=-2.09289 EndY=-2.8 EndZ=0
    g27: LineSegment StartX=-2.09289 StartY=-2.8 StartZ=0 EndX=-4.7 EndY=-5.40711 EndZ=0
    g28: LineSegment StartX=-4.7 StartY=-5.40711 StartZ=0 EndX=-4.7 EndY=-6.5 EndZ=0
    g29: LineSegment StartX=-4.7 StartY=-6.5 StartZ=0 EndX=-3.1 EndY=-6.5 EndZ=0
    g30: LineSegment StartX=-3.1 StartY=-6.5 StartZ=0 EndX=-3.1 EndY=-7.5 EndZ=0
    g31: LineSegment StartX=-3.1 StartY=-7.5 StartZ=0 EndX=-6.5 EndY=-7.5 EndZ=0
    g32: LineSegment StartX=-7.5 StartY=-6.5 StartZ=0 EndX=-7.5 EndY=-3.1 EndZ=0
    g33: LineSegment StartX=-7.5 StartY=-3.1 StartZ=0 EndX=-6.5 EndY=-3.1 EndZ=0
    g34: LineSegment StartX=-6.5 StartY=-3.1 StartZ=0 EndX=-6.5 EndY=-4.7 EndZ=0
    g35: LineSegment StartX=-6.5 StartY=-4.7 StartZ=0 EndX=-5.40711 EndY=-4.7 EndZ=0
    g36: LineSegment StartX=-5.40711 StartY=-4.7 StartZ=0 EndX=-2.8 EndY=-2.09289 EndZ=0
    g37: LineSegment StartX=-2.8 StartY=-2.09289 StartZ=0 EndX=-2.8 EndY=2.09289 EndZ=0
    g38: LineSegment StartX=-2.8 StartY=2.09289 StartZ=0 EndX=-5.40711 EndY=4.7 EndZ=0
    g39: LineSegment StartX=-5.40711 StartY=4.7 StartZ=0 EndX=-6.5 EndY=4.7 EndZ=0
    g40: LineSegment StartX=-6.5 StartY=4.7 StartZ=0 EndX=-6.5 EndY=3.1 EndZ=0
    g41: LineSegment StartX=-6.5 StartY=3.1 StartZ=0 EndX=-7.5 EndY=3.1 EndZ=0
    g42: LineSegment StartX=-7.5 StartY=3.1 StartZ=0 EndX=-7.5 EndY=6.5 EndZ=0
    g43: LineSegment StartX=-6.5 StartY=7.5 StartZ=0 EndX=-3.1 EndY=7.5 EndZ=0
    g44: LineSegment StartX=-3.1 StartY=7.5 StartZ=0 EndX=-3.1 EndY=6.5 EndZ=0
    g45: LineSegment StartX=-3.1 StartY=6.5 StartZ=0 EndX=-4.7 EndY=6.5 EndZ=0
    g46: LineSegment StartX=-4.7 StartY=6.5 StartZ=0 EndX=-4.7 EndY=5.40711 EndZ=0
    g47: LineSegment StartX=-4.7 StartY=5.40711 StartZ=0 EndX=-2.09289 EndY=2.8 EndZ=0
    g48: ArcOfCircle CenterX=-6.5 CenterY=6.5 CenterZ=0 NormalX=0 NormalY=0 NormalZ=1 AngleXU=0 Radius=1 StartAngle=1.5708 EndAngle=3.14159
    g49: ArcOfCircle CenterX=6.5 CenterY=6.5 CenterZ=0 NormalX=0 NormalY=0 NormalZ=1 AngleXU=0 Radius=1 StartAngle=0 EndAngle=1.5708
    g50: ArcOfCircle CenterX=6.5 CenterY=-6.5 CenterZ=0 NormalX=0 NormalY=0 NormalZ=1 AngleXU=0 Radius=1 StartAngle=4.71239 EndAngle=6.28319
    g51: ArcOfCircle CenterX=-6.5 CenterY=-6.5 CenterZ=0 NormalX=0 NormalY=0 NormalZ=1 AngleXU=0 Radius=1 StartAngle=3.14159 EndAngle=4.71239
  constraints (140):
    c: Coincident(g0,g1)
    c: Coincident(g1,g2)
    c: Coincident(g2,g3)
    c: Coincident(g3,g0)
    c: Horizontal(g0)
    c: Horizontal(g2)
    c: Vertical(g1)
    c: Vertical(g3)
    c: Symmetric(g0,g1,g-1)
    c: Equal(g3,g0)
    c: DistanceY(g3,g3) = 15
    c: Coincident(g4,g5)
    c: Coincident(g5,g6)
    c: Coincident(g6,g7)
    c: Coincident(g7,g8)
    c: Vertical(g8)
    c: Coincident(g8,g9)
    c: Horizontal(g9)
    c: Vertical(g10)
    c: Coincident(g10,g11)
    c: Horizontal(g11)
    c: Coincident(g11,g12)
    c: Vertical(g12)
    c: Coincident(g12,g13)
    c: Horizontal(g13)
    c: Coincident(g13,g14)
    c: Coincident(g14,g15)
    c: Coincident(g15,g16)
    c: Coincident(g16,g17)
    c: Horizontal(g17)
    c: Coincident(g17,g18)
    c: Coincident(g18,g19)
    c: Coincident(g19,g20)
    c: Vertical(g20)
    c: Horizontal(g21)
    c: Coincident(g21,g22)
    c: Coincident(g22,g23)
    c: Horizontal(g23)
    c: Coincident(g23,g24)
    c: Coincident(g24,g25)
    c: Coincident(g25,g26)
    c: Coincident(g26,g27)
    c: Coincident(g27,g28)
    c: Vertical(g28)
    c: Coincident(g28,g29)
    c: Coincident(g29,g30)
    c: Coincident(g30,g31)
    c: Coincident(g32,g33)
    c: Coincident(g33,g34)
    c: Coincident(g34,g35)
    c: Coincident(g35,g36)
    c: Coincident(g36,g37)
    c: Coincident(g37,g38)
    c: Coincident(g38,g39)
    c: Coincident(g39,g40)
    c: Coincident(g40,g41)
    c: Coincident(g41,g42)
    c: Vertical(g42)
    c: Horizontal(g43)
    c: Coincident(g43,g44)
    c: Coincident(g44,g45)
    c: Horizontal(g45)
    c: Coincident(g45,g46)
    c: Coincident(g46,g47)
    c: Coincident(g4,g47)
    c: Tangent(g42,g48) = 1.5708
    c: Tangent(g43,g48) = 1.5708
    c: Tangent(g9,g49) = 1.5708
    c: Tangent(g10,g49) = 1.5708
    c: Tangent(g20,g50) = 1.5708
    c: Tangent(g21,g50) = 1.5708
    c: Tangent(g32,g51) = 1.5708
    c: Tangent(g31,g51) = 1.5708
    c: Horizontal(g41)
    c: Horizontal(g39)
    c: Horizontal(g19)
    c: Horizontal(g31)
    c: Horizontal(g35)
    c: Horizontal(g33)
    c: Vertical(g40)
    c: Vertical(g46)
    c: Vertical(g18)
    c: Vertical(g22)
    c: Vertical(g24)
    c: Vertical(g30)
    c: Vertical(g34)
    c: Vertical(g32)
    c: PointOnObject(g21,g2)
    c: PointOnObject(g32,g3)
    c: Vertical(g6)
    c: PointOnObject(g10,g1)
    c: Equal(g48,g49)
    c: Equal(g49,g50)
    c: Equal(g33,g41)
    c: Equal(g41,g30)
    c: Equal(g30,g22)
    c: Equal(g22,g19)
    c: Equal(g19,g11)
    c: Equal(g11,g8)
    c: Equal(g8,g44)
    c: Symmetric(g45,g6,g-2)
    c: DistanceX(g45,g6) = 9.4
    c: DistanceX(g43,g8) = 6.2
    c: Equal(g43,g42)
    c: Equal(g42,g32)
    c: DistanceY(g44,g44) = 1
    c: Equal(g31,g43)
    c: Equal(g43,g21)
    c: Equal(g21,g20)
    c: Equal(g20,g10)
    c: Radius(g49) = 1
    c: Symmetric(g37,g14,g-2)
    c: DistanceX(g37,g14) = 5.6
    c: Symmetric(g43,g8,g-2)
    c: Symmetric(g4,g26,g-1)
    c: DistanceY(g26,g4) = 5.6
    c: Symmetric(g4,g4,g-2)
    c: Equal(g45,g40)
    c: Equal(g45,g7)
    c: Equal(g7,g12)
    c: Equal(g12,g34)
    c: Equal(g34,g29)
    c: Equal(g29,g23)
    c: Equal(g23,g18)
    c: Equal(g39,g46)
    c: Equal(g46,g6)
    c: Equal(g6,g13)
    c: Equal(g13,g17)
    c: Equal(g17,g24)
    c: Equal(g24,g35)
    c: Equal(g35,g28)
    c: Parallel(g38,g47)
    c: Angle(g4,g47) = 2.35619
    c: Symmetric(g38,g35,g-1)
    c: Symmetric(g37,g36,g-1)
    c: Symmetric(g27,g46,g-1)
    c: Distance(g37,g4) = 1
    c: Symmetric(g27,g24,g-2)
    c: Symmetric(g26,g25,g-2)
    c: Symmetric(g36,g15,g-2)
FEATURE [PartDesign::Pad] Pad005
  Length = 290
  Length2 = 100
  Midplane = true
  Placement = pos=(0,0,0) rot=(1,0,0;1.5708rad)
  Profile = -> Sketch007
  Refine = true
  Type = 0
FEATURE [PartDesign::Body] Body006  label="extrusion-011"
  Group = -> [Sketch007,Pad005]
  Origin = -> Origin010
  Placement = pos=(0,-107,0) rot=(0,0,1;1.5708rad)
  Tip = -> Pad005
FEATURE [Sketcher::SketchObject] Sketch008
  MapMode = 5
  Placement = pos=(0,0,0) rot=(1,0,0;1.5708rad)
  Support = -> [XZ_Plane011]
  sketch-geometry (52):
    g0: LineSegment [constr] StartX=-7.5 StartY=7.5 StartZ=0 EndX=7.5 EndY=7.5 EndZ=0
    g1: LineSegment [constr] StartX=7.5 StartY=7.5 StartZ=0 EndX=7.5 EndY=-7.5 EndZ=0
    g2: LineSegment [constr] StartX=7.5 StartY=-7.5 StartZ=0 EndX=-7.5 EndY=-7.5 EndZ=0
    g3: LineSegment [constr] StartX=-7.5 StartY=-7.5 StartZ=0 EndX=-7.5 EndY=7.5 EndZ=0
    g4: LineSegment StartX=-2.09289 StartY=2.8 StartZ=0 EndX=2.09289 EndY=2.8 EndZ=0
    g5: LineSegment StartX=2.09289 StartY=2.8 StartZ=0 EndX=4.7 EndY=5.40711 EndZ=0
    g6: LineSegment StartX=4.7 StartY=5.40711 StartZ=0 EndX=4.7 EndY=6.5 EndZ=0
    g7: LineSegment StartX=4.7 StartY=6.5 StartZ=0 EndX=3.1 EndY=6.5 EndZ=0
    g8: LineSegment StartX=3.1 StartY=6.5 StartZ=0 EndX=3.1 EndY=7.5 EndZ=0
    g9: LineSegment StartX=3.1 StartY=7.5 StartZ=0 EndX=6.5 EndY=7.5 EndZ=0
    g10: LineSegment StartX=7.5 StartY=6.5 StartZ=0 EndX=7.5 EndY=3.1 EndZ=0
    g11: LineSegment StartX=7.5 StartY=3.1 StartZ=0 EndX=6.5 EndY=3.1 EndZ=0
    g12: LineSegment StartX=6.5 StartY=3.1 StartZ=0 EndX=6.5 EndY=4.7 EndZ=0
    g13: LineSegment StartX=6.5 StartY=4.7 StartZ=0 EndX=5.40711 EndY=4.7 EndZ=0
    g14: LineSegment StartX=5.40711 StartY=4.7 StartZ=0 EndX=2.8 EndY=2.09289 EndZ=0
    g15: LineSegment StartX=2.8 StartY=2.09289 StartZ=0 EndX=2.8 EndY=-2.09289 EndZ=0
    g16: LineSegment StartX=2.8 StartY=-2.09289 StartZ=0 EndX=5.40711 EndY=-4.7 EndZ=0
    g17: LineSegment StartX=5.40711 StartY=-4.7 StartZ=0 EndX=6.5 EndY=-4.7 EndZ=0
    g18: LineSegment StartX=6.5 StartY=-4.7 StartZ=0 EndX=6.5 EndY=-3.1 EndZ=0
    g19: LineSegment StartX=6.5 StartY=-3.1 StartZ=0 EndX=7.5 EndY=-3.1 EndZ=0
    g20: LineSegment StartX=7.5 StartY=-3.1 StartZ=0 EndX=7.5 EndY=-6.5 EndZ=0
    g21: LineSegment StartX=6.5 StartY=-7.5 StartZ=0 EndX=3.1 EndY=-7.5 EndZ=0
    g22: LineSegment StartX=3.1 StartY=-7.5 StartZ=0 EndX=3.1 EndY=-6.5 EndZ=0
    g23: LineSegment StartX=3.1 StartY=-6.5 StartZ=0 EndX=4.7 EndY=-6.5 EndZ=0
    g24: LineSegment StartX=4.7 StartY=-6.5 StartZ=0 EndX=4.7 EndY=-5.40711 EndZ=0
    g25: LineSegment StartX=4.7 StartY=-5.40711 StartZ=0 EndX=2.09289 EndY=-2.8 EndZ=0
    g26: LineSegment StartX=2.09289 StartY=-2.8 StartZ=0 EndX=-2.09289 EndY=-2.8 EndZ=0
    g27: LineSegment StartX=-2.09289 StartY=-2.8 StartZ=0 EndX=-4.7 EndY=-5.40711 EndZ=0
    g28: LineSegment StartX=-4.7 StartY=-5.40711 StartZ=0 EndX=-4.7 EndY=-6.5 EndZ=0
    g29: LineSegment StartX=-4.7 StartY=-6.5 StartZ=0 EndX=-3.1 EndY=-6.5 EndZ=0
    g30: LineSegment StartX=-3.1 StartY=-6.5 StartZ=0 EndX=-3.1 EndY=-7.5 EndZ=0
    g31: LineSegment StartX=-3.1 StartY=-7.5 StartZ=0 EndX=-6.5 EndY=-7.5 EndZ=0
    g32: LineSegment StartX=-7.5 StartY=-6.5 StartZ=0 EndX=-7.5 EndY=-3.1 EndZ=0
    g33: LineSegment StartX=-7.5 StartY=-3.1 StartZ=0 EndX=-6.5 EndY=-3.1 EndZ=0
    g34: LineSegment StartX=-6.5 StartY=-3.1 StartZ=0 EndX=-6.5 EndY=-4.7 EndZ=0
    g35: LineSegment StartX=-6.5 StartY=-4.7 StartZ=0 EndX=-5.40711 EndY=-4.7 EndZ=0
    g36: LineSegment StartX=-5.40711 StartY=-4.7 StartZ=0 EndX=-2.8 EndY=-2.09289 EndZ=0
    g37: LineSegment StartX=-2.8 StartY=-2.09289 StartZ=0 EndX=-2.8 EndY=2.09289 EndZ=0
    g38: LineSegment StartX=-2.8 StartY=2.09289 StartZ=0 EndX=-5.40711 EndY=4.7 EndZ=0
    g39: LineSegment StartX=-5.40711 StartY=4.7 StartZ=0 EndX=-6.5 EndY=4.7 EndZ=0
    g40: LineSegment StartX=-6.5 StartY=4.7 StartZ=0 EndX=-6.5 EndY=3.1 EndZ=0
    g41: LineSegment StartX=-6.5 StartY=3.1 StartZ=0 EndX=-7.5 EndY=3.1 EndZ=0
    g42: LineSegment StartX=-7.5 StartY=3.1 StartZ=0 EndX=-7.5 EndY=6.5 EndZ=0
    g43: LineSegment StartX=-6.5 StartY=7.5 StartZ=0 EndX=-3.1 EndY=7.5 EndZ=0
    g44: LineSegment StartX=-3.1 StartY=7.5 StartZ=0 EndX=-3.1 EndY=6.5 EndZ=0
    g45: LineSegment StartX=-3.1 StartY=6.5 StartZ=0 EndX=-4.7 EndY=6.5 EndZ=0
    g46: LineSegment StartX=-4.7 StartY=6.5 StartZ=0 EndX=-4.7 EndY=5.40711 EndZ=0
    g47: LineSegment StartX=-4.7 StartY=5.40711 StartZ=0 EndX=-2.09289 EndY=2.8 EndZ=0
    g48: ArcOfCircle CenterX=-6.5 CenterY=6.5 CenterZ=0 NormalX=0 NormalY=0 NormalZ=1 AngleXU=0 Radius=1 StartAngle=1.5708 EndAngle=3.14159
    g49: ArcOfCircle CenterX=6.5 CenterY=6.5 CenterZ=0 NormalX=0 NormalY=0 NormalZ=1 AngleXU=0 Radius=1 StartAngle=0 EndAngle=1.5708
    g50: ArcOfCircle CenterX=6.5 CenterY=-6.5 CenterZ=0 NormalX=0 NormalY=0 NormalZ=1 AngleXU=0 Radius=1 StartAngle=4.71239 EndAngle=6.28319
    g51: ArcOfCircle CenterX=-6.5 CenterY=-6.5 CenterZ=0 NormalX=0 NormalY=0 NormalZ=1 AngleXU=0 Radius=1 StartAngle=3.14159 EndAngle=4.71239
  constraints (140):
    c: Coincident(g0,g1)
    c: Coincident(g1,g2)
    c: Coincident(g2,g3)
    c: Coincident(g3,g0)
    c: Horizontal(g0)
    c: Horizontal(g2)
    c: Vertical(g1)
    c: Vertical(g3)
    c: Symmetric(g0,g1,g-1)
    c: Equal(g3,g0)
    c: DistanceY(g3,g3) = 15
    c: Coincident(g4,g5)
    c: Coincident(g5,g6)
    c: Coincident(g6,g7)
    c: Coincident(g7,g8)
    c: Vertical(g8)
    c: Coincident(g8,g9)
    c: Horizontal(g9)
    c: Vertical(g10)
    c: Coincident(g10,g11)
    c: Horizontal(g11)
    c: Coincident(g11,g12)
    c: Vertical(g12)
    c: Coincident(g12,g13)
    c: Horizontal(g13)
    c: Coincident(g13,g14)
    c: Coincident(g14,g15)
    c: Coincident(g15,g16)
    c: Coincident(g16,g17)
    c: Horizontal(g17)
    c: Coincident(g17,g18)
    c: Coincident(g18,g19)
    c: Coincident(g19,g20)
    c: Vertical(g20)
    c: Horizontal(g21)
    c: Coincident(g21,g22)
    c: Coincident(g22,g23)
    c: Horizontal(g23)
    c: Coincident(g23,g24)
    c: Coincident(g24,g25)
    c: Coincident(g25,g26)
    c: Coincident(g26,g27)
    c: Coincident(g27,g28)
    c: Vertical(g28)
    c: Coincident(g28,g29)
    c: Coincident(g29,g30)
    c: Coincident(g30,g31)
    c: Coincident(g32,g33)
    c: Coincident(g33,g34)
    c: Coincident(g34,g35)
    c: Coincident(g35,g36)
    c: Coincident(g36,g37)
    c: Coincident(g37,g38)
    c: Coincident(g38,g39)
    c: Coincident(g39,g40)
    c: Coincident(g40,g41)
    c: Coincident(g41,g42)
    c: Vertical(g42)
    c: Horizontal(g43)
    c: Coincident(g43,g44)
    c: Coincident(g44,g45)
    c: Horizontal(g45)
    c: Coincident(g45,g46)
    c: Coincident(g46,g47)
    c: Coincident(g4,g47)
    c: Tangent(g42,g48) = 1.5708
    c: Tangent(g43,g48) = 1.5708
    c: Tangent(g9,g49) = 1.5708
    c: Tangent(g10,g49) = 1.5708
    c: Tangent(g20,g50) = 1.5708
    c: Tangent(g21,g50) = 1.5708
    c: Tangent(g32,g51) = 1.5708
    c: Tangent(g31,g51) = 1.5708
    c: Horizontal(g41)
    c: Horizontal(g39)
    c: Horizontal(g19)
    c: Horizontal(g31)
    c: Horizontal(g35)
    c: Horizontal(g33)
    c: Vertical(g40)
    c: Vertical(g46)
    c: Vertical(g18)
    c: Vertical(g22)
    c: Vertical(g24)
    c: Vertical(g30)
    c: Vertical(g34)
    c: Vertical(g32)
    c: PointOnObject(g21,g2)
    c: PointOnObject(g32,g3)
    c: Vertical(g6)
    c: PointOnObject(g10,g1)
    c: Equal(g48,g49)
    c: Equal(g49,g50)
    c: Equal(g33,g41)
    c: Equal(g41,g30)
    c: Equal(g30,g22)
    c: Equal(g22,g19)
    c: Equal(g19,g11)
    c: Equal(g11,g8)
    c: Equal(g8,g44)
    c: Symmetric(g45,g6,g-2)
    c: DistanceX(g45,g6) = 9.4
    c: DistanceX(g43,g8) = 6.2
    c: Equal(g43,g42)
    c: Equal(g42,g32)
    c: DistanceY(g44,g44) = 1
    c: Equal(g31,g43)
    c: Equal(g43,g21)
    c: Equal(g21,g20)
    c: Equal(g20,g10)
    c: Radius(g49) = 1
    c: Symmetric(g37,g14,g-2)
    c: DistanceX(g37,g14) = 5.6
    c: Symmetric(g43,g8,g-2)
    c: Symmetric(g4,g26,g-1)
    c: DistanceY(g26,g4) = 5.6
    c: Symmetric(g4,g4,g-2)
    c: Equal(g45,g40)
    c: Equal(g45,g7)
    c: Equal(g7,g12)
    c: Equal(g12,g34)
    c: Equal(g34,g29)
    c: Equal(g29,g23)
    c: Equal(g23,g18)
    c: Equal(g39,g46)
    c: Equal(g46,g6)
    c: Equal(g6,g13)
    c: Equal(g13,g17)
    c: Equal(g17,g24)
    c: Equal(g24,g35)
    c: Equal(g35,g28)
    c: Parallel(g38,g47)
    c: Angle(g4,g47) = 2.35619
    c: Symmetric(g38,g35,g-1)
    c: Symmetric(g37,g36,g-1)
    c: Symmetric(g27,g46,g-1)
    c: Distance(g37,g4) = 1
    c: Symmetric(g27,g24,g-2)
    c: Symmetric(g26,g25,g-2)
    c: Symmetric(g36,g15,g-2)
FEATURE [PartDesign::Pad] Pad006
  Length = 260
  Length2 = 100
  Placement = pos=(0,0,0) rot=(1,0,0;1.5708rad)
  Profile = -> Sketch008
  Refine = true
  Type = 0
FEATURE [PartDesign::Body] Body007  label="extrusion-005"
  Group = -> [Sketch008,Pad006]
  Origin = -> Origin011
  Placement = pos=(-152.5,-107.1,130) rot=(1,0,0;1.5708rad)
  Tip = -> Pad006
FEATURE [Sketcher::SketchObject] Sketch009
  MapMode = 5
  Placement = pos=(0,0,0) rot=(1,0,0;1.5708rad)
  Support = -> [XZ_Plane012]
  sketch-geometry (52):
    g0: LineSegment [constr] StartX=-7.5 StartY=7.5 StartZ=0 EndX=7.5 EndY=7.5 EndZ=0
    g1: LineSegment [constr] StartX=7.5 StartY=7.5 StartZ=0 EndX=7.5 EndY=-7.5 EndZ=0
    g2: LineSegment [constr] StartX=7.5 StartY=-7.5 StartZ=0 EndX=-7.5 EndY=-7.5 EndZ=0
    g3: LineSegment [constr] StartX=-7.5 StartY=-7.5 StartZ=0 EndX=-7.5 EndY=7.5 EndZ=0
    g4: LineSegment StartX=-2.09289 StartY=2.8 StartZ=0 EndX=2.09289 EndY=2.8 EndZ=0
    g5: LineSegment StartX=2.09289 StartY=2.8 StartZ=0 EndX=4.7 EndY=5.40711 EndZ=0
    g6: LineSegment StartX=4.7 StartY=5.40711 StartZ=0 EndX=4.7 EndY=6.5 EndZ=0
    g7: LineSegment StartX=4.7 StartY=6.5 StartZ=0 EndX=3.1 EndY=6.5 EndZ=0
    g8: LineSegment StartX=3.1 StartY=6.5 StartZ=0 EndX=3.1 EndY=7.5 EndZ=0
    g9: LineSegment StartX=3.1 StartY=7.5 StartZ=0 EndX=6.5 EndY=7.5 EndZ=0
    g10: LineSegment StartX=7.5 StartY=6.5 StartZ=0 EndX=7.5 EndY=3.1 EndZ=0
    g11: LineSegment StartX=7.5 StartY=3.1 StartZ=0 EndX=6.5 EndY=3.1 EndZ=0
    g12: LineSegment StartX=6.5 StartY=3.1 StartZ=0 EndX=6.5 EndY=4.7 EndZ=0
    g13: LineSegment StartX=6.5 StartY=4.7 StartZ=0 EndX=5.40711 EndY=4.7 EndZ=0
    g14: LineSegment StartX=5.40711 StartY=4.7 StartZ=0 EndX=2.8 EndY=2.09289 EndZ=0
    g15: LineSegment StartX=2.8 StartY=2.09289 StartZ=0 EndX=2.8 EndY=-2.09289 EndZ=0
    g16: LineSegment StartX=2.8 StartY=-2.09289 StartZ=0 EndX=5.40711 EndY=-4.7 EndZ=0
    g17: LineSegment StartX=5.40711 StartY=-4.7 StartZ=0 EndX=6.5 EndY=-4.7 EndZ=0
    g18: LineSegment StartX=6.5 StartY=-4.7 StartZ=0 EndX=6.5 EndY=-3.1 EndZ=0
    g19: LineSegment StartX=6.5 StartY=-3.1 StartZ=0 EndX=7.5 EndY=-3.1 EndZ=0
    g20: LineSegment StartX=7.5 StartY=-3.1 StartZ=0 EndX=7.5 EndY=-6.5 EndZ=0
    g21: LineSegment StartX=6.5 StartY=-7.5 StartZ=0 EndX=3.1 EndY=-7.5 EndZ=0
    g22: LineSegment StartX=3.1 StartY=-7.5 StartZ=0 EndX=3.1 EndY=-6.5 EndZ=0
    g23: LineSegment StartX=3.1 StartY=-6.5 StartZ=0 EndX=4.7 EndY=-6.5 EndZ=0
    g24: LineSegment StartX=4.7 StartY=-6.5 StartZ=0 EndX=4.7 EndY=-5.40711 EndZ=0
    g25: LineSegment StartX=4.7 StartY=-5.40711 StartZ=0 EndX=2.09289 EndY=-2.8 EndZ=0
    g26: LineSegment StartX=2.09289 StartY=-2.8 StartZ=0 EndX=-2.09289 EndY=-2.8 EndZ=0
    g27: LineSegment StartX=-2.09289 StartY=-2.8 StartZ=0 EndX=-4.7 EndY=-5.40711 EndZ=0
    g28: LineSegment StartX=-4.7 StartY=-5.40711 StartZ=0 EndX=-4.7 EndY=-6.5 EndZ=0
    g29: LineSegment StartX=-4.7 StartY=-6.5 StartZ=0 EndX=-3.1 EndY=-6.5 EndZ=0
    g30: LineSegment StartX=-3.1 StartY=-6.5 StartZ=0 EndX=-3.1 EndY=-7.5 EndZ=0
    g31: LineSegment StartX=-3.1 StartY=-7.5 StartZ=0 EndX=-6.5 EndY=-7.5 EndZ=0
    g32: LineSegment StartX=-7.5 StartY=-6.5 StartZ=0 EndX=-7.5 EndY=-3.1 EndZ=0
    g33: LineSegment StartX=-7.5 StartY=-3.1 StartZ=0 EndX=-6.5 EndY=-3.1 EndZ=0
    g34: LineSegment StartX=-6.5 StartY=-3.1 StartZ=0 EndX=-6.5 EndY=-4.7 EndZ=0
    g35: LineSegment StartX=-6.5 StartY=-4.7 StartZ=0 EndX=-5.40711 EndY=-4.7 EndZ=0
    g36: LineSegment StartX=-5.40711 StartY=-4.7 StartZ=0 EndX=-2.8 EndY=-2.09289 EndZ=0
    g37: LineSegment StartX=-2.8 StartY=-2.09289 StartZ=0 EndX=-2.8 EndY=2.09289 EndZ=0
    g38: LineSegment StartX=-2.8 StartY=2.09289 StartZ=0 EndX=-5.40711 EndY=4.7 EndZ=0
    g39: LineSegment StartX=-5.40711 StartY=4.7 StartZ=0 EndX=-6.5 EndY=4.7 EndZ=0
    g40: LineSegment StartX=-6.5 StartY=4.7 StartZ=0 EndX=-6.5 EndY=3.1 EndZ=0
    g41: LineSegment StartX=-6.5 StartY=3.1 StartZ=0 EndX=-7.5 EndY=3.1 EndZ=0
    g42: LineSegment StartX=-7.5 StartY=3.1 StartZ=0 EndX=-7.5 EndY=6.5 EndZ=0
    g43: LineSegment StartX=-6.5 StartY=7.5 StartZ=0 EndX=-3.1 EndY=7.5 EndZ=0
    g44: LineSegment StartX=-3.1 StartY=7.5 StartZ=0 EndX=-3.1 EndY=6.5 EndZ=0
    g45: LineSegment StartX=-3.1 StartY=6.5 StartZ=0 EndX=-4.7 EndY=6.5 EndZ=0
    g46: LineSegment StartX=-4.7 StartY=6.5 StartZ=0 EndX=-4.7 EndY=5.40711 EndZ=0
    g47: LineSegment StartX=-4.7 StartY=5.40711 StartZ=0 EndX=-2.09289 EndY=2.8 EndZ=0
    g48: ArcOfCircle CenterX=-6.5 CenterY=6.5 CenterZ=0 NormalX=0 NormalY=0 NormalZ=1 AngleXU=0 Radius=1 StartAngle=1.5708 EndAngle=3.14159
    g49: ArcOfCircle CenterX=6.5 CenterY=6.5 CenterZ=0 NormalX=0 NormalY=0 NormalZ=1 AngleXU=0 Radius=1 StartAngle=0 EndAngle=1.5708
    g50: ArcOfCircle CenterX=6.5 CenterY=-6.5 CenterZ=0 NormalX=0 NormalY=0 NormalZ=1 AngleXU=0 Radius=1 StartAngle=4.71239 EndAngle=6.28319
    g51: ArcOfCircle CenterX=-6.5 CenterY=-6.5 CenterZ=0 NormalX=0 NormalY=0 NormalZ=1 AngleXU=0 Radius=1 StartAngle=3.14159 EndAngle=4.71239
  constraints (140):
    c: Coincident(g0,g1)
    c: Coincident(g1,g2)
    c: Coincident(g2,g3)
    c: Coincident(g3,g0)
    c: Horizontal(g0)
    c: Horizontal(g2)
    c: Vertical(g1)
    c: Vertical(g3)
    c: Symmetric(g0,g1,g-1)
    c: Equal(g3,g0)
    c: DistanceY(g3,g3) = 15
    c: Coincident(g4,g5)
    c: Coincident(g5,g6)
    c: Coincident(g6,g7)
    c: Coincident(g7,g8)
    c: Vertical(g8)
    c: Coincident(g8,g9)
    c: Horizontal(g9)
    c: Vertical(g10)
    c: Coincident(g10,g11)
    c: Horizontal(g11)
    c: Coincident(g11,g12)
    c: Vertical(g12)
    c: Coincident(g12,g13)
    c: Horizontal(g13)
    c: Coincident(g13,g14)
    c: Coincident(g14,g15)
    c: Coincident(g15,g16)
    c: Coincident(g16,g17)
    c: Horizontal(g17)
    c: Coincident(g17,g18)
    c: Coincident(g18,g19)
    c: Coincident(g19,g20)
    c: Vertical(g20)
    c: Horizontal(g21)
    c: Coincident(g21,g22)
    c: Coincident(g22,g23)
    c: Horizontal(g23)
    c: Coincident(g23,g24)
    c: Coincident(g24,g25)
    c: Coincident(g25,g26)
    c: Coincident(g26,g27)
    c: Coincident(g27,g28)
    c: Vertical(g28)
    c: Coincident(g28,g29)
    c: Coincident(g29,g30)
    c: Coincident(g30,g31)
    c: Coincident(g32,g33)
    c: Coincident(g33,g34)
    c: Coincident(g34,g35)
    c: Coincident(g35,g36)
    c: Coincident(g36,g37)
    c: Coincident(g37,g38)
    c: Coincident(g38,g39)
    c: Coincident(g39,g40)
    c: Coincident(g40,g41)
    c: Coincident(g41,g42)
    c: Vertical(g42)
    c: Horizontal(g43)
    c: Coincident(g43,g44)
    c: Coincident(g44,g45)
    c: Horizontal(g45)
    c: Coincident(g45,g46)
    c: Coincident(g46,g47)
    c: Coincident(g4,g47)
    c: Tangent(g42,g48) = 1.5708
    c: Tangent(g43,g48) = 1.5708
    c: Tangent(g9,g49) = 1.5708
    c: Tangent(g10,g49) = 1.5708
    c: Tangent(g20,g50) = 1.5708
    c: Tangent(g21,g50) = 1.5708
    c: Tangent(g32,g51) = 1.5708
    c: Tangent(g31,g51) = 1.5708
    c: Horizontal(g41)
    c: Horizontal(g39)
    c: Horizontal(g19)
    c: Horizontal(g31)
    c: Horizontal(g35)
    c: Horizontal(g33)
    c: Vertical(g40)
    c: Vertical(g46)
    c: Vertical(g18)
    c: Vertical(g22)
    c: Vertical(g24)
    c: Vertical(g30)
    c: Vertical(g34)
    c: Vertical(g32)
    c: PointOnObject(g21,g2)
    c: PointOnObject(g32,g3)
    c: Vertical(g6)
    c: PointOnObject(g10,g1)
    c: Equal(g48,g49)
    c: Equal(g49,g50)
    c: Equal(g33,g41)
    c: Equal(g41,g30)
    c: Equal(g30,g22)
    c: Equal(g22,g19)
    c: Equal(g19,g11)
    c: Equal(g11,g8)
    c: Equal(g8,g44)
    c: Symmetric(g45,g6,g-2)
    c: DistanceX(g45,g6) = 9.4
    c: DistanceX(g43,g8) = 6.2
    c: Equal(g43,g42)
    c: Equal(g42,g32)
    c: DistanceY(g44,g44) = 1
    c: Equal(g31,g43)
    c: Equal(g43,g21)
    c: Equal(g21,g20)
    c: Equal(g20,g10)
    c: Radius(g49) = 1
    c: Symmetric(g37,g14,g-2)
    c: DistanceX(g37,g14) = 5.6
    c: Symmetric(g43,g8,g-2)
    c: Symmetric(g4,g26,g-1)
    c: DistanceY(g26,g4) = 5.6
    c: Symmetric(g4,g4,g-2)
    c: Equal(g45,g40)
    c: Equal(g45,g7)
    c: Equal(g7,g12)
    c: Equal(g12,g34)
    c: Equal(g34,g29)
    c: Equal(g29,g23)
    c: Equal(g23,g18)
    c: Equal(g39,g46)
    c: Equal(g46,g6)
    c: Equal(g6,g13)
    c: Equal(g13,g17)
    c: Equal(g17,g24)
    c: Equal(g24,g35)
    c: Equal(g35,g28)
    c: Parallel(g38,g47)
    c: Angle(g4,g47) = 2.35619
    c: Symmetric(g38,g35,g-1)
    c: Symmetric(g37,g36,g-1)
    c: Symmetric(g27,g46,g-1)
    c: Distance(g37,g4) = 1
    c: Symmetric(g27,g24,g-2)
    c: Symmetric(g26,g25,g-2)
    c: Symmetric(g36,g15,g-2)
FEATURE [PartDesign::Pad] Pad007
  Length = 260
  Length2 = 100
  Placement = pos=(0,0,0) rot=(1,0,0;1.5708rad)
  Profile = -> Sketch009
  Refine = true
  Type = 0
FEATURE [PartDesign::Body] Body008  label="extrusion-006"
  Group = -> [Sketch009,Pad007]
  Origin = -> Origin012
  Placement = pos=(152.5,177.9,130) rot=(1,0,0;1.5708rad)
  Tip = -> Pad007
FEATURE [Sketcher::SketchObject] Sketch010
  MapMode = 5
  Placement = pos=(0,0,0) rot=(1,0,0;1.5708rad)
  Support = -> [XZ_Plane013]
  sketch-geometry (52):
    g0: LineSegment [constr] StartX=-7.5 StartY=7.5 StartZ=0 EndX=7.5 EndY=7.5 EndZ=0
    g1: LineSegment [constr] StartX=7.5 StartY=7.5 StartZ=0 EndX=7.5 EndY=-7.5 EndZ=0
    g2: LineSegment [constr] StartX=7.5 StartY=-7.5 StartZ=0 EndX=-7.5 EndY=-7.5 EndZ=0
    g3: LineSegment [constr] StartX=-7.5 StartY=-7.5 StartZ=0 EndX=-7.5 EndY=7.5 EndZ=0
    g4: LineSegment StartX=-2.09289 StartY=2.8 StartZ=0 EndX=2.09289 EndY=2.8 EndZ=0
    g5: LineSegment StartX=2.09289 StartY=2.8 StartZ=0 EndX=4.7 EndY=5.40711 EndZ=0
    g6: LineSegment StartX=4.7 StartY=5.40711 StartZ=0 EndX=4.7 EndY=6.5 EndZ=0
    g7: LineSegment StartX=4.7 StartY=6.5 StartZ=0 EndX=3.1 EndY=6.5 EndZ=0
    g8: LineSegment StartX=3.1 StartY=6.5 StartZ=0 EndX=3.1 EndY=7.5 EndZ=0
    g9: LineSegment StartX=3.1 StartY=7.5 StartZ=0 EndX=6.5 EndY=7.5 EndZ=0
    g10: LineSegment StartX=7.5 StartY=6.5 StartZ=0 EndX=7.5 EndY=3.1 EndZ=0
    g11: LineSegment StartX=7.5 StartY=3.1 StartZ=0 EndX=6.5 EndY=3.1 EndZ=0
    g12: LineSegment StartX=6.5 StartY=3.1 StartZ=0 EndX=6.5 EndY=4.7 EndZ=0
    g13: LineSegment StartX=6.5 StartY=4.7 StartZ=0 EndX=5.40711 EndY=4.7 EndZ=0
    g14: LineSegment StartX=5.40711 StartY=4.7 StartZ=0 EndX=2.8 EndY=2.09289 EndZ=0
    g15: LineSegment StartX=2.8 StartY=2.09289 StartZ=0 EndX=2.8 EndY=-2.09289 EndZ=0
    g16: LineSegment StartX=2.8 StartY=-2.09289 StartZ=0 EndX=5.40711 EndY=-4.7 EndZ=0
    g17: LineSegment StartX=5.40711 StartY=-4.7 StartZ=0 EndX=6.5 EndY=-4.7 EndZ=0
    g18: LineSegment StartX=6.5 StartY=-4.7 StartZ=0 EndX=6.5 EndY=-3.1 EndZ=0
    g19: LineSegment StartX=6.5 StartY=-3.1 StartZ=0 EndX=7.5 EndY=-3.1 EndZ=0
    g20: LineSegment StartX=7.5 StartY=-3.1 StartZ=0 EndX=7.5 EndY=-6.5 EndZ=0
    g21: LineSegment StartX=6.5 StartY=-7.5 StartZ=0 EndX=3.1 EndY=-7.5 EndZ=0
    g22: LineSegment StartX=3.1 StartY=-7.5 StartZ=0 EndX=3.1 EndY=-6.5 EndZ=0
    g23: LineSegment StartX=3.1 StartY=-6.5 StartZ=0 EndX=4.7 EndY=-6.5 EndZ=0
    g24: LineSegment StartX=4.7 StartY=-6.5 StartZ=0 EndX=4.7 EndY=-5.40711 EndZ=0
    g25: LineSegment StartX=4.7 StartY=-5.40711 StartZ=0 EndX=2.09289 EndY=-2.8 EndZ=0
    g26: LineSegment StartX=2.09289 StartY=-2.8 StartZ=0 EndX=-2.09289 EndY=-2.8 EndZ=0
    g27: LineSegment StartX=-2.09289 StartY=-2.8 StartZ=0 EndX=-4.7 EndY=-5.40711 EndZ=0
    g28: LineSegment StartX=-4.7 StartY=-5.40711 StartZ=0 EndX=-4.7 EndY=-6.5 EndZ=0
    g29: LineSegment StartX=-4.7 StartY=-6.5 StartZ=0 EndX=-3.1 EndY=-6.5 EndZ=0
    g30: LineSegment StartX=-3.1 StartY=-6.5 StartZ=0 EndX=-3.1 EndY=-7.5 EndZ=0
    g31: LineSegment StartX=-3.1 StartY=-7.5 StartZ=0 EndX=-6.5 EndY=-7.5 EndZ=0
    g32: LineSegment StartX=-7.5 StartY=-6.5 StartZ=0 EndX=-7.5 EndY=-3.1 EndZ=0
    g33: LineSegment StartX=-7.5 StartY=-3.1 StartZ=0 EndX=-6.5 EndY=-3.1 EndZ=0
    g34: LineSegment StartX=-6.5 StartY=-3.1 StartZ=0 EndX=-6.5 EndY=-4.7 EndZ=0
    g35: LineSegment StartX=-6.5 StartY=-4.7 StartZ=0 EndX=-5.40711 EndY=-4.7 EndZ=0
    g36: LineSegment StartX=-5.40711 StartY=-4.7 StartZ=0 EndX=-2.8 EndY=-2.09289 EndZ=0
    g37: LineSegment StartX=-2.8 StartY=-2.09289 StartZ=0 EndX=-2.8 EndY=2.09289 EndZ=0
    g38: LineSegment StartX=-2.8 StartY=2.09289 StartZ=0 EndX=-5.40711 EndY=4.7 EndZ=0
    g39: LineSegment StartX=-5.40711 StartY=4.7 StartZ=0 EndX=-6.5 EndY=4.7 EndZ=0
    g40: LineSegment StartX=-6.5 StartY=4.7 StartZ=0 EndX=-6.5 EndY=3.1 EndZ=0
    g41: LineSegment StartX=-6.5 StartY=3.1 StartZ=0 EndX=-7.5 EndY=3.1 EndZ=0
    g42: LineSegment StartX=-7.5 StartY=3.1 StartZ=0 EndX=-7.5 EndY=6.5 EndZ=0
    g43: LineSegment StartX=-6.5 StartY=7.5 StartZ=0 EndX=-3.1 EndY=7.5 EndZ=0
    g44: LineSegment StartX=-3.1 StartY=7.5 StartZ=0 EndX=-3.1 EndY=6.5 EndZ=0
    g45: LineSegment StartX=-3.1 StartY=6.5 StartZ=0 EndX=-4.7 EndY=6.5 EndZ=0
    g46: LineSegment StartX=-4.7 StartY=6.5 StartZ=0 EndX=-4.7 EndY=5.40711 EndZ=0
    g47: LineSegment StartX=-4.7 StartY=5.40711 StartZ=0 EndX=-2.09289 EndY=2.8 EndZ=0
    g48: ArcOfCircle CenterX=-6.5 CenterY=6.5 CenterZ=0 NormalX=0 NormalY=0 NormalZ=1 AngleXU=0 Radius=1 StartAngle=1.5708 EndAngle=3.14159
    g49: ArcOfCircle CenterX=6.5 CenterY=6.5 CenterZ=0 NormalX=0 NormalY=0 NormalZ=1 AngleXU=0 Radius=1 StartAngle=0 EndAngle=1.5708
    g50: ArcOfCircle CenterX=6.5 CenterY=-6.5 CenterZ=0 NormalX=0 NormalY=0 NormalZ=1 AngleXU=0 Radius=1 StartAngle=4.71239 EndAngle=6.28319
    g51: ArcOfCircle CenterX=-6.5 CenterY=-6.5 CenterZ=0 NormalX=0 NormalY=0 NormalZ=1 AngleXU=0 Radius=1 StartAngle=3.14159 EndAngle=4.71239
  constraints (140):
    c: Coincident(g0,g1)
    c: Coincident(g1,g2)
    c: Coincident(g2,g3)
    c: Coincident(g3,g0)
    c: Horizontal(g0)
    c: Horizontal(g2)
    c: Vertical(g1)
    c: Vertical(g3)
    c: Symmetric(g0,g1,g-1)
    c: Equal(g3,g0)
    c: DistanceY(g3,g3) = 15
    c: Coincident(g4,g5)
    c: Coincident(g5,g6)
    c: Coincident(g6,g7)
    c: Coincident(g7,g8)
    c: Vertical(g8)
    c: Coincident(g8,g9)
    c: Horizontal(g9)
    c: Vertical(g10)
    c: Coincident(g10,g11)
    c: Horizontal(g11)
    c: Coincident(g11,g12)
    c: Vertical(g12)
    c: Coincident(g12,g13)
    c: Horizontal(g13)
    c: Coincident(g13,g14)
    c: Coincident(g14,g15)
    c: Coincident(g15,g16)
    c: Coincident(g16,g17)
    c: Horizontal(g17)
    c: Coincident(g17,g18)
    c: Coincident(g18,g19)
    c: Coincident(g19,g20)
    c: Vertical(g20)
    c: Horizontal(g21)
    c: Coincident(g21,g22)
    c: Coincident(g22,g23)
    c: Horizontal(g23)
    c: Coincident(g23,g24)
    c: Coincident(g24,g25)
    c: Coincident(g25,g26)
    c: Coincident(g26,g27)
    c: Coincident(g27,g28)
    c: Vertical(g28)
    c: Coincident(g28,g29)
    c: Coincident(g29,g30)
    c: Coincident(g30,g31)
    c: Coincident(g32,g33)
    c: Coincident(g33,g34)
    c: Coincident(g34,g35)
    c: Coincident(g35,g36)
    c: Coincident(g36,g37)
    c: Coincident(g37,g38)
    c: Coincident(g38,g39)
    c: Coincident(g39,g40)
    c: Coincident(g40,g41)
    c: Coincident(g41,g42)
    c: Vertical(g42)
    c: Horizontal(g43)
    c: Coincident(g43,g44)
    c: Coincident(g44,g45)
    c: Horizontal(g45)
    c: Coincident(g45,g46)
    c: Coincident(g46,g47)
    c: Coincident(g4,g47)
    c: Tangent(g42,g48) = 1.5708
    c: Tangent(g43,g48) = 1.5708
    c: Tangent(g9,g49) = 1.5708
    c: Tangent(g10,g49) = 1.5708
    c: Tangent(g20,g50) = 1.5708
    c: Tangent(g21,g50) = 1.5708
    c: Tangent(g32,g51) = 1.5708
    c: Tangent(g31,g51) = 1.5708
    c: Horizontal(g41)
    c: Horizontal(g39)
    c: Horizontal(g19)
    c: Horizontal(g31)
    c: Horizontal(g35)
    c: Horizontal(g33)
    c: Vertical(g40)
    c: Vertical(g46)
    c: Vertical(g18)
    c: Vertical(g22)
    c: Vertical(g24)
    c: Vertical(g30)
    c: Vertical(g34)
    c: Vertical(g32)
    c: PointOnObject(g21,g2)
    c: PointOnObject(g32,g3)
    c: Vertical(g6)
    c: PointOnObject(g10,g1)
    c: Equal(g48,g49)
    c: Equal(g49,g50)
    c: Equal(g33,g41)
    c: Equal(g41,g30)
    c: Equal(g30,g22)
    c: Equal(g22,g19)
    c: Equal(g19,g11)
    c: Equal(g11,g8)
    c: Equal(g8,g44)
    c: Symmetric(g45,g6,g-2)
    c: DistanceX(g45,g6) = 9.4
    c: DistanceX(g43,g8) = 6.2
    c: Equal(g43,g42)
    c: Equal(g42,g32)
    c: DistanceY(g44,g44) = 1
    c: Equal(g31,g43)
    c: Equal(g43,g21)
    c: Equal(g21,g20)
    c: Equal(g20,g10)
    c: Radius(g49) = 1
    c: Symmetric(g37,g14,g-2)
    c: DistanceX(g37,g14) = 5.6
    c: Symmetric(g43,g8,g-2)
    c: Symmetric(g4,g26,g-1)
    c: DistanceY(g26,g4) = 5.6
    c: Symmetric(g4,g4,g-2)
    c: Equal(g45,g40)
    c: Equal(g45,g7)
    c: Equal(g7,g12)
    c: Equal(g12,g34)
    c: Equal(g34,g29)
    c: Equal(g29,g23)
    c: Equal(g23,g18)
    c: Equal(g39,g46)
    c: Equal(g46,g6)
    c: Equal(g6,g13)
    c: Equal(g13,g17)
    c: Equal(g17,g24)
    c: Equal(g24,g35)
    c: Equal(g35,g28)
    c: Parallel(g38,g47)
    c: Angle(g4,g47) = 2.35619
    c: Symmetric(g38,g35,g-1)
    c: Symmetric(g37,g36,g-1)
    c: Symmetric(g27,g46,g-1)
    c: Distance(g37,g4) = 1
    c: Symmetric(g27,g24,g-2)
    c: Symmetric(g26,g25,g-2)
    c: Symmetric(g36,g15,g-2)
FEATURE [PartDesign::Pad] Pad008
  Length = 260
  Length2 = 100
  Placement = pos=(0,0,0) rot=(1,0,0;1.5708rad)
  Profile = -> Sketch010
  Refine = true
  Type = 0
FEATURE [PartDesign::Body] Body009  label="extrusion-007"
  Group = -> [Sketch010,Pad008]
  Origin = -> Origin013
  Placement = pos=(-152.5,177.9,130) rot=(1,0,0;1.5708rad)
  Tip = -> Pad008
FEATURE [Sketcher::SketchObject] Sketch011
  MapMode = 5
  Placement = pos=(0,0,0) rot=(1,0,0;1.5708rad)
  Support = -> [XZ_Plane014]
  sketch-geometry (52):
    g0: LineSegment [constr] StartX=-7.5 StartY=7.5 StartZ=0 EndX=7.5 EndY=7.5 EndZ=0
    g1: LineSegment [constr] StartX=7.5 StartY=7.5 StartZ=0 EndX=7.5 EndY=-7.5 EndZ=0
    g2: LineSegment [constr] StartX=7.5 StartY=-7.5 StartZ=0 EndX=-7.5 EndY=-7.5 EndZ=0
    g3: LineSegment [constr] StartX=-7.5 StartY=-7.5 StartZ=0 EndX=-7.5 EndY=7.5 EndZ=0
    g4: LineSegment StartX=-2.09289 StartY=2.8 StartZ=0 EndX=2.09289 EndY=2.8 EndZ=0
    g5: LineSegment StartX=2.09289 StartY=2.8 StartZ=0 EndX=4.7 EndY=5.40711 EndZ=0
    g6: LineSegment StartX=4.7 StartY=5.40711 StartZ=0 EndX=4.7 EndY=6.5 EndZ=0
    g7: LineSegment StartX=4.7 StartY=6.5 StartZ=0 EndX=3.1 EndY=6.5 EndZ=0
    g8: LineSegment StartX=3.1 StartY=6.5 StartZ=0 EndX=3.1 EndY=7.5 EndZ=0
    g9: LineSegment StartX=3.1 StartY=7.5 StartZ=0 EndX=6.5 EndY=7.5 EndZ=0
    g10: LineSegment StartX=7.5 StartY=6.5 StartZ=0 EndX=7.5 EndY=3.1 EndZ=0
    g11: LineSegment StartX=7.5 StartY=3.1 StartZ=0 EndX=6.5 EndY=3.1 EndZ=0
    g12: LineSegment StartX=6.5 StartY=3.1 StartZ=0 EndX=6.5 EndY=4.7 EndZ=0
    g13: LineSegment StartX=6.5 StartY=4.7 StartZ=0 EndX=5.40711 EndY=4.7 EndZ=0
    g14: LineSegment StartX=5.40711 StartY=4.7 StartZ=0 EndX=2.8 EndY=2.09289 EndZ=0
    g15: LineSegment StartX=2.8 StartY=2.09289 StartZ=0 EndX=2.8 EndY=-2.09289 EndZ=0
    g16: LineSegment StartX=2.8 StartY=-2.09289 StartZ=0 EndX=5.40711 EndY=-4.7 EndZ=0
    g17: LineSegment StartX=5.40711 StartY=-4.7 StartZ=0 EndX=6.5 EndY=-4.7 EndZ=0
    g18: LineSegment StartX=6.5 StartY=-4.7 StartZ=0 EndX=6.5 EndY=-3.1 EndZ=0
    g19: LineSegment StartX=6.5 StartY=-3.1 StartZ=0 EndX=7.5 EndY=-3.1 EndZ=0
    g20: LineSegment StartX=7.5 StartY=-3.1 StartZ=0 EndX=7.5 EndY=-6.5 EndZ=0
    g21: LineSegment StartX=6.5 StartY=-7.5 StartZ=0 EndX=3.1 EndY=-7.5 EndZ=0
    g22: LineSegment StartX=3.1 StartY=-7.5 StartZ=0 EndX=3.1 EndY=-6.5 EndZ=0
    g23: LineSegment StartX=3.1 StartY=-6.5 StartZ=0 EndX=4.7 EndY=-6.5 EndZ=0
    g24: LineSegment StartX=4.7 StartY=-6.5 StartZ=0 EndX=4.7 EndY=-5.40711 EndZ=0
    g25: LineSegment StartX=4.7 StartY=-5.40711 StartZ=0 EndX=2.09289 EndY=-2.8 EndZ=0
    g26: LineSegment StartX=2.09289 StartY=-2.8 StartZ=0 EndX=-2.09289 EndY=-2.8 EndZ=0
    g27: LineSegment StartX=-2.09289 StartY=-2.8 StartZ=0 EndX=-4.7 EndY=-5.40711 EndZ=0
    g28: LineSegment StartX=-4.7 StartY=-5.40711 StartZ=0 EndX=-4.7 EndY=-6.5 EndZ=0
    g29: LineSegment StartX=-4.7 StartY=-6.5 StartZ=0 EndX=-3.1 EndY=-6.5 EndZ=0
    g30: LineSegment StartX=-3.1 StartY=-6.5 StartZ=0 EndX=-3.1 EndY=-7.5 EndZ=0
    g31: LineSegment StartX=-3.1 StartY=-7.5 StartZ=0 EndX=-6.5 EndY=-7.5 EndZ=0
    g32: LineSegment StartX=-7.5 StartY=-6.5 StartZ=0 EndX=-7.5 EndY=-3.1 EndZ=0
    g33: LineSegment StartX=-7.5 StartY=-3.1 StartZ=0 EndX=-6.5 EndY=-3.1 EndZ=0
    g34: LineSegment StartX=-6.5 StartY=-3.1 StartZ=0 EndX=-6.5 EndY=-4.7 EndZ=0
    g35: LineSegment StartX=-6.5 StartY=-4.7 StartZ=0 EndX=-5.40711 EndY=-4.7 EndZ=0
    g36: LineSegment StartX=-5.40711 StartY=-4.7 StartZ=0 EndX=-2.8 EndY=-2.09289 EndZ=0
    g37: LineSegment StartX=-2.8 StartY=-2.09289 StartZ=0 EndX=-2.8 EndY=2.09289 EndZ=0
    g38: LineSegment StartX=-2.8 StartY=2.09289 StartZ=0 EndX=-5.40711 EndY=4.7 EndZ=0
    g39: LineSegment StartX=-5.40711 StartY=4.7 StartZ=0 EndX=-6.5 EndY=4.7 EndZ=0
    g40: LineSegment StartX=-6.5 StartY=4.7 StartZ=0 EndX=-6.5 EndY=3.1 EndZ=0
    g41: LineSegment StartX=-6.5 StartY=3.1 StartZ=0 EndX=-7.5 EndY=3.1 EndZ=0
    g42: LineSegment StartX=-7.5 StartY=3.1 StartZ=0 EndX=-7.5 EndY=6.5 EndZ=0
    g43: LineSegment StartX=-6.5 StartY=7.5 StartZ=0 EndX=-3.1 EndY=7.5 EndZ=0
    g44: LineSegment StartX=-3.1 StartY=7.5 StartZ=0 EndX=-3.1 EndY=6.5 EndZ=0
    g45: LineSegment StartX=-3.1 StartY=6.5 StartZ=0 EndX=-4.7 EndY=6.5 EndZ=0
    g46: LineSegment StartX=-4.7 StartY=6.5 StartZ=0 EndX=-4.7 EndY=5.40711 EndZ=0
    g47: LineSegment StartX=-4.7 StartY=5.40711 StartZ=0 EndX=-2.09289 EndY=2.8 EndZ=0
    g48: ArcOfCircle CenterX=-6.5 CenterY=6.5 CenterZ=0 NormalX=0 NormalY=0 NormalZ=1 AngleXU=0 Radius=1 StartAngle=1.5708 EndAngle=3.14159
    g49: ArcOfCircle CenterX=6.5 CenterY=6.5 CenterZ=0 NormalX=0 NormalY=0 NormalZ=1 AngleXU=0 Radius=1 StartAngle=0 EndAngle=1.5708
    g50: ArcOfCircle CenterX=6.5 CenterY=-6.5 CenterZ=0 NormalX=0 NormalY=0 NormalZ=1 AngleXU=0 Radius=1 StartAngle=4.71239 EndAngle=6.28319
    g51: ArcOfCircle CenterX=-6.5 CenterY=-6.5 CenterZ=0 NormalX=0 NormalY=0 NormalZ=1 AngleXU=0 Radius=1 StartAngle=3.14159 EndAngle=4.71239
  constraints (140):
    c: Coincident(g0,g1)
    c: Coincident(g1,g2)
    c: Coincident(g2,g3)
    c: Coincident(g3,g0)
    c: Horizontal(g0)
    c: Horizontal(g2)
    c: Vertical(g1)
    c: Vertical(g3)
    c: Symmetric(g0,g1,g-1)
    c: Equal(g3,g0)
    c: DistanceY(g3,g3) = 15
    c: Coincident(g4,g5)
    c: Coincident(g5,g6)
    c: Coincident(g6,g7)
    c: Coincident(g7,g8)
    c: Vertical(g8)
    c: Coincident(g8,g9)
    c: Horizontal(g9)
    c: Vertical(g10)
    c: Coincident(g10,g11)
    c: Horizontal(g11)
    c: Coincident(g11,g12)
    c: Vertical(g12)
    c: Coincident(g12,g13)
    c: Horizontal(g13)
    c: Coincident(g13,g14)
    c: Coincident(g14,g15)
    c: Coincident(g15,g16)
    c: Coincident(g16,g17)
    c: Horizontal(g17)
    c: Coincident(g17,g18)
    c: Coincident(g18,g19)
    c: Coincident(g19,g20)
    c: Vertical(g20)
    c: Horizontal(g21)
    c: Coincident(g21,g22)
    c: Coincident(g22,g23)
    c: Horizontal(g23)
    c: Coincident(g23,g24)
    c: Coincident(g24,g25)
    c: Coincident(g25,g26)
    c: Coincident(g26,g27)
    c: Coincident(g27,g28)
    c: Vertical(g28)
    c: Coincident(g28,g29)
    c: Coincident(g29,g30)
    c: Coincident(g30,g31)
    c: Coincident(g32,g33)
    c: Coincident(g33,g34)
    c: Coincident(g34,g35)
    c: Coincident(g35,g36)
    c: Coincident(g36,g37)
    c: Coincident(g37,g38)
    c: Coincident(g38,g39)
    c: Coincident(g39,g40)
    c: Coincident(g40,g41)
    c: Coincident(g41,g42)
    c: Vertical(g42)
    c: Horizontal(g43)
    c: Coincident(g43,g44)
    c: Coincident(g44,g45)
    c: Horizontal(g45)
    c: Coincident(g45,g46)
    c: Coincident(g46,g47)
    c: Coincident(g4,g47)
    c: Tangent(g42,g48) = 1.5708
    c: Tangent(g43,g48) = 1.5708
    c: Tangent(g9,g49) = 1.5708
    c: Tangent(g10,g49) = 1.5708
    c: Tangent(g20,g50) = 1.5708
    c: Tangent(g21,g50) = 1.5708
    c: Tangent(g32,g51) = 1.5708
    c: Tangent(g31,g51) = 1.5708
    c: Horizontal(g41)
    c: Horizontal(g39)
    c: Horizontal(g19)
    c: Horizontal(g31)
    c: Horizontal(g35)
    c: Horizontal(g33)
    c: Vertical(g40)
    c: Vertical(g46)
    c: Vertical(g18)
    c: Vertical(g22)
    c: Vertical(g24)
    c: Vertical(g30)
    c: Vertical(g34)
    c: Vertical(g32)
    c: PointOnObject(g21,g2)
    c: PointOnObject(g32,g3)
    c: Vertical(g6)
    c: PointOnObject(g10,g1)
    c: Equal(g48,g49)
    c: Equal(g49,g50)
    c: Equal(g33,g41)
    c: Equal(g41,g30)
    c: Equal(g30,g22)
    c: Equal(g22,g19)
    c: Equal(g19,g11)
    c: Equal(g11,g8)
    c: Equal(g8,g44)
    c: Symmetric(g45,g6,g-2)
    c: DistanceX(g45,g6) = 9.4
    c: DistanceX(g43,g8) = 6.2
    c: Equal(g43,g42)
    c: Equal(g42,g32)
    c: DistanceY(g44,g44) = 1
    c: Equal(g31,g43)
    c: Equal(g43,g21)
    c: Equal(g21,g20)
    c: Equal(g20,g10)
    c: Radius(g49) = 1
    c: Symmetric(g37,g14,g-2)
    c: DistanceX(g37,g14) = 5.6
    c: Symmetric(g43,g8,g-2)
    c: Symmetric(g4,g26,g-1)
    c: DistanceY(g26,g4) = 5.6
    c: Symmetric(g4,g4,g-2)
    c: Equal(g45,g40)
    c: Equal(g45,g7)
    c: Equal(g7,g12)
    c: Equal(g12,g34)
    c: Equal(g34,g29)
    c: Equal(g29,g23)
    c: Equal(g23,g18)
    c: Equal(g39,g46)
    c: Equal(g46,g6)
    c: Equal(g6,g13)
    c: Equal(g13,g17)
    c: Equal(g17,g24)
    c: Equal(g24,g35)
    c: Equal(g35,g28)
    c: Parallel(g38,g47)
    c: Angle(g4,g47) = 2.35619
    c: Symmetric(g38,g35,g-1)
    c: Symmetric(g37,g36,g-1)
    c: Symmetric(g27,g46,g-1)
    c: Distance(g37,g4) = 1
    c: Symmetric(g27,g24,g-2)
    c: Symmetric(g26,g25,g-2)
    c: Symmetric(g36,g15,g-2)
FEATURE [PartDesign::Pad] Pad009
  Length = 260
  Length2 = 100
  Midplane = true
  Placement = pos=(0,0,0) rot=(1,0,0;1.5708rad)
  Profile = -> Sketch011
  Refine = true
  Type = 0
FEATURE [PartDesign::Body] Body010  label="extrusion-008"
  Group = -> [Sketch011,Pad009]
  Origin = -> Origin014
  Placement = pos=(152.5,-107,2.42e-14) rot=(1,0,0;1.5708rad)
  Tip = -> Pad009
FEATURE [App::Part] Part003  label="frame-middle"
  Group = -> [Body007,Body008,Body009,Body010]
  Origin = -> Origin008
FEATURE [Sketcher::SketchObject] Sketch012
  MapMode = 5
  Placement = pos=(0,0,0) rot=(1,0,0;1.5708rad)
  Support = -> [XZ_Plane015]
  sketch-geometry (52):
    g0: LineSegment [constr] StartX=-7.5 StartY=7.5 StartZ=0 EndX=7.5 EndY=7.5 EndZ=0
    g1: LineSegment [constr] StartX=7.5 StartY=7.5 StartZ=0 EndX=7.5 EndY=-7.5 EndZ=0
    g2: LineSegment [constr] StartX=7.5 StartY=-7.5 StartZ=0 EndX=-7.5 EndY=-7.5 EndZ=0
    g3: LineSegment [constr] StartX=-7.5 StartY=-7.5 StartZ=0 EndX=-7.5 EndY=7.5 EndZ=0
    g4: LineSegment StartX=-2.09289 StartY=2.8 StartZ=0 EndX=2.09289 EndY=2.8 EndZ=0
    g5: LineSegment StartX=2.09289 StartY=2.8 StartZ=0 EndX=4.7 EndY=5.40711 EndZ=0
    g6: LineSegment StartX=4.7 StartY=5.40711 StartZ=0 EndX=4.7 EndY=6.5 EndZ=0
    g7: LineSegment StartX=4.7 StartY=6.5 StartZ=0 EndX=3.1 EndY=6.5 EndZ=0
    g8: LineSegment StartX=3.1 StartY=6.5 StartZ=0 EndX=3.1 EndY=7.5 EndZ=0
    g9: LineSegment StartX=3.1 StartY=7.5 StartZ=0 EndX=6.5 EndY=7.5 EndZ=0
    g10: LineSegment StartX=7.5 StartY=6.5 StartZ=0 EndX=7.5 EndY=3.1 EndZ=0
    g11: LineSegment StartX=7.5 StartY=3.1 StartZ=0 EndX=6.5 EndY=3.1 EndZ=0
    g12: LineSegment StartX=6.5 StartY=3.1 StartZ=0 EndX=6.5 EndY=4.7 EndZ=0
    g13: LineSegment StartX=6.5 StartY=4.7 StartZ=0 EndX=5.40711 EndY=4.7 EndZ=0
    g14: LineSegment StartX=5.40711 StartY=4.7 StartZ=0 EndX=2.8 EndY=2.09289 EndZ=0
    g15: LineSegment StartX=2.8 StartY=2.09289 StartZ=0 EndX=2.8 EndY=-2.09289 EndZ=0
    g16: LineSegment StartX=2.8 StartY=-2.09289 StartZ=0 EndX=5.40711 EndY=-4.7 EndZ=0
    g17: LineSegment StartX=5.40711 StartY=-4.7 StartZ=0 EndX=6.5 EndY=-4.7 EndZ=0
    g18: LineSegment StartX=6.5 StartY=-4.7 StartZ=0 EndX=6.5 EndY=-3.1 EndZ=0
    g19: LineSegment StartX=6.5 StartY=-3.1 StartZ=0 EndX=7.5 EndY=-3.1 EndZ=0
    g20: LineSegment StartX=7.5 StartY=-3.1 StartZ=0 EndX=7.5 EndY=-6.5 EndZ=0
    g21: LineSegment StartX=6.5 StartY=-7.5 StartZ=0 EndX=3.1 EndY=-7.5 EndZ=0
    g22: LineSegment StartX=3.1 StartY=-7.5 StartZ=0 EndX=3.1 EndY=-6.5 EndZ=0
    g23: LineSegment StartX=3.1 StartY=-6.5 StartZ=0 EndX=4.7 EndY=-6.5 EndZ=0
    g24: LineSegment StartX=4.7 StartY=-6.5 StartZ=0 EndX=4.7 EndY=-5.40711 EndZ=0
    g25: LineSegment StartX=4.7 StartY=-5.40711 StartZ=0 EndX=2.09289 EndY=-2.8 EndZ=0
    g26: LineSegment StartX=2.09289 StartY=-2.8 StartZ=0 EndX=-2.09289 EndY=-2.8 EndZ=0
    g27: LineSegment StartX=-2.09289 StartY=-2.8 StartZ=0 EndX=-4.7 EndY=-5.40711 EndZ=0
    g28: LineSegment StartX=-4.7 StartY=-5.40711 StartZ=0 EndX=-4.7 EndY=-6.5 EndZ=0
    g29: LineSegment StartX=-4.7 StartY=-6.5 StartZ=0 EndX=-3.1 EndY=-6.5 EndZ=0
    g30: LineSegment StartX=-3.1 StartY=-6.5 StartZ=0 EndX=-3.1 EndY=-7.5 EndZ=0
    g31: LineSegment StartX=-3.1 StartY=-7.5 StartZ=0 EndX=-6.5 EndY=-7.5 EndZ=0
    g32: LineSegment StartX=-7.5 StartY=-6.5 StartZ=0 EndX=-7.5 EndY=-3.1 EndZ=0
    g33: LineSegment StartX=-7.5 StartY=-3.1 StartZ=0 EndX=-6.5 EndY=-3.1 EndZ=0
    g34: LineSegment StartX=-6.5 StartY=-3.1 StartZ=0 EndX=-6.5 EndY=-4.7 EndZ=0
    g35: LineSegment StartX=-6.5 StartY=-4.7 StartZ=0 EndX=-5.40711 EndY=-4.7 EndZ=0
    g36: LineSegment StartX=-5.40711 StartY=-4.7 StartZ=0 EndX=-2.8 EndY=-2.09289 EndZ=0
    g37: LineSegment StartX=-2.8 StartY=-2.09289 StartZ=0 EndX=-2.8 EndY=2.09289 EndZ=0
    g38: LineSegment StartX=-2.8 StartY=2.09289 StartZ=0 EndX=-5.40711 EndY=4.7 EndZ=0
    g39: LineSegment StartX=-5.40711 StartY=4.7 StartZ=0 EndX=-6.5 EndY=4.7 EndZ=0
    g40: LineSegment StartX=-6.5 StartY=4.7 StartZ=0 EndX=-6.5 EndY=3.1 EndZ=0
    g41: LineSegment StartX=-6.5 StartY=3.1 StartZ=0 EndX=-7.5 EndY=3.1 EndZ=0
    g42: LineSegment StartX=-7.5 StartY=3.1 StartZ=0 EndX=-7.5 EndY=6.5 EndZ=0
    g43: LineSegment StartX=-6.5 StartY=7.5 StartZ=0 EndX=-3.1 EndY=7.5 EndZ=0
    g44: LineSegment StartX=-3.1 StartY=7.5 StartZ=0 EndX=-3.1 EndY=6.5 EndZ=0
    g45: LineSegment StartX=-3.1 StartY=6.5 StartZ=0 EndX=-4.7 EndY=6.5 EndZ=0
    g46: LineSegment StartX=-4.7 StartY=6.5 StartZ=0 EndX=-4.7 EndY=5.40711 EndZ=0
    g47: LineSegment StartX=-4.7 StartY=5.40711 StartZ=0 EndX=-2.09289 EndY=2.8 EndZ=0
    g48: ArcOfCircle CenterX=-6.5 CenterY=6.5 CenterZ=0 NormalX=0 NormalY=0 NormalZ=1 AngleXU=0 Radius=1 StartAngle=1.5708 EndAngle=3.14159
    g49: ArcOfCircle CenterX=6.5 CenterY=6.5 CenterZ=0 NormalX=0 NormalY=0 NormalZ=1 AngleXU=0 Radius=1 StartAngle=0 EndAngle=1.5708
    g50: ArcOfCircle CenterX=6.5 CenterY=-6.5 CenterZ=0 NormalX=0 NormalY=0 NormalZ=1 AngleXU=0 Radius=1 StartAngle=4.71239 EndAngle=6.28319
    g51: ArcOfCircle CenterX=-6.5 CenterY=-6.5 CenterZ=0 NormalX=0 NormalY=0 NormalZ=1 AngleXU=0 Radius=1 StartAngle=3.14159 EndAngle=4.71239
  constraints (140):
    c: Coincident(g0,g1)
    c: Coincident(g1,g2)
    c: Coincident(g2,g3)
    c: Coincident(g3,g0)
    c: Horizontal(g0)
    c: Horizontal(g2)
    c: Vertical(g1)
    c: Vertical(g3)
    c: Symmetric(g0,g1,g-1)
    c: Equal(g3,g0)
    c: DistanceY(g3,g3) = 15
    c: Coincident(g4,g5)
    c: Coincident(g5,g6)
    c: Coincident(g6,g7)
    c: Coincident(g7,g8)
    c: Vertical(g8)
    c: Coincident(g8,g9)
    c: Horizontal(g9)
    c: Vertical(g10)
    c: Coincident(g10,g11)
    c: Horizontal(g11)
    c: Coincident(g11,g12)
    c: Vertical(g12)
    c: Coincident(g12,g13)
    c: Horizontal(g13)
    c: Coincident(g13,g14)
    c: Coincident(g14,g15)
    c: Coincident(g15,g16)
    c: Coincident(g16,g17)
    c: Horizontal(g17)
    c: Coincident(g17,g18)
    c: Coincident(g18,g19)
    c: Coincident(g19,g20)
    c: Vertical(g20)
    c: Horizontal(g21)
    c: Coincident(g21,g22)
    c: Coincident(g22,g23)
    c: Horizontal(g23)
    c: Coincident(g23,g24)
    c: Coincident(g24,g25)
    c: Coincident(g25,g26)
    c: Coincident(g26,g27)
    c: Coincident(g27,g28)
    c: Vertical(g28)
    c: Coincident(g28,g29)
    c: Coincident(g29,g30)
    c: Coincident(g30,g31)
    c: Coincident(g32,g33)
    c: Coincident(g33,g34)
    c: Coincident(g34,g35)
    c: Coincident(g35,g36)
    c: Coincident(g36,g37)
    c: Coincident(g37,g38)
    c: Coincident(g38,g39)
    c: Coincident(g39,g40)
    c: Coincident(g40,g41)
    c: Coincident(g41,g42)
    c: Vertical(g42)
    c: Horizontal(g43)
    c: Coincident(g43,g44)
    c: Coincident(g44,g45)
    c: Horizontal(g45)
    c: Coincident(g45,g46)
    c: Coincident(g46,g47)
    c: Coincident(g4,g47)
    c: Tangent(g42,g48) = 1.5708
    c: Tangent(g43,g48) = 1.5708
    c: Tangent(g9,g49) = 1.5708
    c: Tangent(g10,g49) = 1.5708
    c: Tangent(g20,g50) = 1.5708
    c: Tangent(g21,g50) = 1.5708
    c: Tangent(g32,g51) = 1.5708
    c: Tangent(g31,g51) = 1.5708
    c: Horizontal(g41)
    c: Horizontal(g39)
    c: Horizontal(g19)
    c: Horizontal(g31)
    c: Horizontal(g35)
    c: Horizontal(g33)
    c: Vertical(g40)
    c: Vertical(g46)
    c: Vertical(g18)
    c: Vertical(g22)
    c: Vertical(g24)
    c: Vertical(g30)
    c: Vertical(g34)
    c: Vertical(g32)
    c: PointOnObject(g21,g2)
    c: PointOnObject(g32,g3)
    c: Vertical(g6)
    c: PointOnObject(g10,g1)
    c: Equal(g48,g49)
    c: Equal(g49,g50)
    c: Equal(g33,g41)
    c: Equal(g41,g30)
    c: Equal(g30,g22)
    c: Equal(g22,g19)
    c: Equal(g19,g11)
    c: Equal(g11,g8)
    c: Equal(g8,g44)
    c: Symmetric(g45,g6,g-2)
    c: DistanceX(g45,g6) = 9.4
    c: DistanceX(g43,g8) = 6.2
    c: Equal(g43,g42)
    c: Equal(g42,g32)
    c: DistanceY(g44,g44) = 1
    c: Equal(g31,g43)
    c: Equal(g43,g21)
    c: Equal(g21,g20)
    c: Equal(g20,g10)
    c: Radius(g49) = 1
    c: Symmetric(g37,g14,g-2)
    c: DistanceX(g37,g14) = 5.6
    c: Symmetric(g43,g8,g-2)
    c: Symmetric(g4,g26,g-1)
    c: DistanceY(g26,g4) = 5.6
    c: Symmetric(g4,g4,g-2)
    c: Equal(g45,g40)
    c: Equal(g45,g7)
    c: Equal(g7,g12)
    c: Equal(g12,g34)
    c: Equal(g34,g29)
    c: Equal(g29,g23)
    c: Equal(g23,g18)
    c: Equal(g39,g46)
    c: Equal(g46,g6)
    c: Equal(g6,g13)
    c: Equal(g13,g17)
    c: Equal(g17,g24)
    c: Equal(g24,g35)
    c: Equal(g35,g28)
    c: Parallel(g38,g47)
    c: Angle(g4,g47) = 2.35619
    c: Symmetric(g38,g35,g-1)
    c: Symmetric(g37,g36,g-1)
    c: Symmetric(g27,g46,g-1)
    c: Distance(g37,g4) = 1
    c: Symmetric(g27,g24,g-2)
    c: Symmetric(g26,g25,g-2)
    c: Symmetric(g36,g15,g-2)
FEATURE [PartDesign::Pad] Pad010
  Length = 270
  Length2 = 100
  Placement = pos=(0,0,0) rot=(1,0,0;1.5708rad)
  Profile = -> Sketch012
  Refine = true
  Type = 0
FEATURE [PartDesign::Body] Body011  label="extrusion-001"
  Group = -> [Sketch012,Pad010]
  Origin = -> Origin016
  Placement = pos=(-152.4,-99.4,-0.6) rot=(0,0,1;3.14159rad)
  Tip = -> Pad010
FEATURE [Sketcher::SketchObject] Sketch013
  MapMode = 5
  Placement = pos=(0,0,0) rot=(1,0,0;1.5708rad)
  Support = -> [XZ_Plane017]
  sketch-geometry (52):
    g0: LineSegment [constr] StartX=-7.5 StartY=7.5 StartZ=0 EndX=7.5 EndY=7.5 EndZ=0
    g1: LineSegment [constr] StartX=7.5 StartY=7.5 StartZ=0 EndX=7.5 EndY=-7.5 EndZ=0
    g2: LineSegment [constr] StartX=7.5 StartY=-7.5 StartZ=0 EndX=-7.5 EndY=-7.5 EndZ=0
    g3: LineSegment [constr] StartX=-7.5 StartY=-7.5 StartZ=0 EndX=-7.5 EndY=7.5 EndZ=0
    g4: LineSegment StartX=-2.09289 StartY=2.8 StartZ=0 EndX=2.09289 EndY=2.8 EndZ=0
    g5: LineSegment StartX=2.09289 StartY=2.8 StartZ=0 EndX=4.7 EndY=5.40711 EndZ=0
    g6: LineSegment StartX=4.7 StartY=5.40711 StartZ=0 EndX=4.7 EndY=6.5 EndZ=0
    g7: LineSegment StartX=4.7 StartY=6.5 StartZ=0 EndX=3.1 EndY=6.5 EndZ=0
    g8: LineSegment StartX=3.1 StartY=6.5 StartZ=0 EndX=3.1 EndY=7.5 EndZ=0
    g9: LineSegment StartX=3.1 StartY=7.5 StartZ=0 EndX=6.5 EndY=7.5 EndZ=0
    g10: LineSegment StartX=7.5 StartY=6.5 StartZ=0 EndX=7.5 EndY=3.1 EndZ=0
    g11: LineSegment StartX=7.5 StartY=3.1 StartZ=0 EndX=6.5 EndY=3.1 EndZ=0
    g12: LineSegment StartX=6.5 StartY=3.1 StartZ=0 EndX=6.5 EndY=4.7 EndZ=0
    g13: LineSegment StartX=6.5 StartY=4.7 StartZ=0 EndX=5.40711 EndY=4.7 EndZ=0
    g14: LineSegment StartX=5.40711 StartY=4.7 StartZ=0 EndX=2.8 EndY=2.09289 EndZ=0
    g15: LineSegment StartX=2.8 StartY=2.09289 StartZ=0 EndX=2.8 EndY=-2.09289 EndZ=0
    g16: LineSegment StartX=2.8 StartY=-2.09289 StartZ=0 EndX=5.40711 EndY=-4.7 EndZ=0
    g17: LineSegment StartX=5.40711 StartY=-4.7 StartZ=0 EndX=6.5 EndY=-4.7 EndZ=0
    g18: LineSegment StartX=6.5 StartY=-4.7 StartZ=0 EndX=6.5 EndY=-3.1 EndZ=0
    g19: LineSegment StartX=6.5 StartY=-3.1 StartZ=0 EndX=7.5 EndY=-3.1 EndZ=0
    g20: LineSegment StartX=7.5 StartY=-3.1 StartZ=0 EndX=7.5 EndY=-6.5 EndZ=0
    g21: LineSegment StartX=6.5 StartY=-7.5 StartZ=0 EndX=3.1 EndY=-7.5 EndZ=0
    g22: LineSegment StartX=3.1 StartY=-7.5 StartZ=0 EndX=3.1 EndY=-6.5 EndZ=0
    g23: LineSegment StartX=3.1 StartY=-6.5 StartZ=0 EndX=4.7 EndY=-6.5 EndZ=0
    g24: LineSegment StartX=4.7 StartY=-6.5 StartZ=0 EndX=4.7 EndY=-5.40711 EndZ=0
    g25: LineSegment StartX=4.7 StartY=-5.40711 StartZ=0 EndX=2.09289 EndY=-2.8 EndZ=0
    g26: LineSegment StartX=2.09289 StartY=-2.8 StartZ=0 EndX=-2.09289 EndY=-2.8 EndZ=0
    g27: LineSegment StartX=-2.09289 StartY=-2.8 StartZ=0 EndX=-4.7 EndY=-5.40711 EndZ=0
    g28: LineSegment StartX=-4.7 StartY=-5.40711 StartZ=0 EndX=-4.7 EndY=-6.5 EndZ=0
    g29: LineSegment StartX=-4.7 StartY=-6.5 StartZ=0 EndX=-3.1 EndY=-6.5 EndZ=0
    g30: LineSegment StartX=-3.1 StartY=-6.5 StartZ=0 EndX=-3.1 EndY=-7.5 EndZ=0
    g31: LineSegment StartX=-3.1 StartY=-7.5 StartZ=0 EndX=-6.5 EndY=-7.5 EndZ=0
    g32: LineSegment StartX=-7.5 StartY=-6.5 StartZ=0 EndX=-7.5 EndY=-3.1 EndZ=0
    g33: LineSegment StartX=-7.5 StartY=-3.1 StartZ=0 EndX=-6.5 EndY=-3.1 EndZ=0
    g34: LineSegment StartX=-6.5 StartY=-3.1 StartZ=0 EndX=-6.5 EndY=-4.7 EndZ=0
    g35: LineSegment StartX=-6.5 StartY=-4.7 StartZ=0 EndX=-5.40711 EndY=-4.7 EndZ=0
    g36: LineSegment StartX=-5.40711 StartY=-4.7 StartZ=0 EndX=-2.8 EndY=-2.09289 EndZ=0
    g37: LineSegment StartX=-2.8 StartY=-2.09289 StartZ=0 EndX=-2.8 EndY=2.09289 EndZ=0
    g38: LineSegment StartX=-2.8 StartY=2.09289 StartZ=0 EndX=-5.40711 EndY=4.7 EndZ=0
    g39: LineSegment StartX=-5.40711 StartY=4.7 StartZ=0 EndX=-6.5 EndY=4.7 EndZ=0
    g40: LineSegment StartX=-6.5 StartY=4.7 StartZ=0 EndX=-6.5 EndY=3.1 EndZ=0
    g41: LineSegment StartX=-6.5 StartY=3.1 StartZ=0 EndX=-7.5 EndY=3.1 EndZ=0
    g42: LineSegment StartX=-7.5 StartY=3.1 StartZ=0 EndX=-7.5 EndY=6.5 EndZ=0
    g43: LineSegment StartX=-6.5 StartY=7.5 StartZ=0 EndX=-3.1 EndY=7.5 EndZ=0
    g44: LineSegment StartX=-3.1 StartY=7.5 StartZ=0 EndX=-3.1 EndY=6.5 EndZ=0
    g45: LineSegment StartX=-3.1 StartY=6.5 StartZ=0 EndX=-4.7 EndY=6.5 EndZ=0
    g46: LineSegment StartX=-4.7 StartY=6.5 StartZ=0 EndX=-4.7 EndY=5.40711 EndZ=0
    g47: LineSegment StartX=-4.7 StartY=5.40711 StartZ=0 EndX=-2.09289 EndY=2.8 EndZ=0
    g48: ArcOfCircle CenterX=-6.5 CenterY=6.5 CenterZ=0 NormalX=0 NormalY=0 NormalZ=1 AngleXU=0 Radius=1 StartAngle=1.5708 EndAngle=3.14159
    g49: ArcOfCircle CenterX=6.5 CenterY=6.5 CenterZ=0 NormalX=0 NormalY=0 NormalZ=1 AngleXU=0 Radius=1 StartAngle=0 EndAngle=1.5708
    g50: ArcOfCircle CenterX=6.5 CenterY=-6.5 CenterZ=0 NormalX=0 NormalY=0 NormalZ=1 AngleXU=0 Radius=1 StartAngle=4.71239 EndAngle=6.28319
    g51: ArcOfCircle CenterX=-6.5 CenterY=-6.5 CenterZ=0 NormalX=0 NormalY=0 NormalZ=1 AngleXU=0 Radius=1 StartAngle=3.14159 EndAngle=4.71239
  constraints (140):
    c: Coincident(g0,g1)
    c: Coincident(g1,g2)
    c: Coincident(g2,g3)
    c: Coincident(g3,g0)
    c: Horizontal(g0)
    c: Horizontal(g2)
    c: Vertical(g1)
    c: Vertical(g3)
    c: Symmetric(g0,g1,g-1)
    c: Equal(g3,g0)
    c: DistanceY(g3,g3) = 15
    c: Coincident(g4,g5)
    c: Coincident(g5,g6)
    c: Coincident(g6,g7)
    c: Coincident(g7,g8)
    c: Vertical(g8)
    c: Coincident(g8,g9)
    c: Horizontal(g9)
    c: Vertical(g10)
    c: Coincident(g10,g11)
    c: Horizontal(g11)
    c: Coincident(g11,g12)
    c: Vertical(g12)
    c: Coincident(g12,g13)
    c: Horizontal(g13)
    c: Coincident(g13,g14)
    c: Coincident(g14,g15)
    c: Coincident(g15,g16)
    c: Coincident(g16,g17)
    c: Horizontal(g17)
    c: Coincident(g17,g18)
    c: Coincident(g18,g19)
    c: Coincident(g19,g20)
    c: Vertical(g20)
    c: Horizontal(g21)
    c: Coincident(g21,g22)
    c: Coincident(g22,g23)
    c: Horizontal(g23)
    c: Coincident(g23,g24)
    c: Coincident(g24,g25)
    c: Coincident(g25,g26)
    c: Coincident(g26,g27)
    c: Coincident(g27,g28)
    c: Vertical(g28)
    c: Coincident(g28,g29)
    c: Coincident(g29,g30)
    c: Coincident(g30,g31)
    c: Coincident(g32,g33)
    c: Coincident(g33,g34)
    c: Coincident(g34,g35)
    c: Coincident(g35,g36)
    c: Coincident(g36,g37)
    c: Coincident(g37,g38)
    c: Coincident(g38,g39)
    c: Coincident(g39,g40)
    c: Coincident(g40,g41)
    c: Coincident(g41,g42)
    c: Vertical(g42)
    c: Horizontal(g43)
    c: Coincident(g43,g44)
    c: Coincident(g44,g45)
    c: Horizontal(g45)
    c: Coincident(g45,g46)
    c: Coincident(g46,g47)
    c: Coincident(g4,g47)
    c: Tangent(g42,g48) = 1.5708
    c: Tangent(g43,g48) = 1.5708
    c: Tangent(g9,g49) = 1.5708
    c: Tangent(g10,g49) = 1.5708
    c: Tangent(g20,g50) = 1.5708
    c: Tangent(g21,g50) = 1.5708
    c: Tangent(g32,g51) = 1.5708
    c: Tangent(g31,g51) = 1.5708
    c: Horizontal(g41)
    c: Horizontal(g39)
    c: Horizontal(g19)
    c: Horizontal(g31)
    c: Horizontal(g35)
    c: Horizontal(g33)
    c: Vertical(g40)
    c: Vertical(g46)
    c: Vertical(g18)
    c: Vertical(g22)
    c: Vertical(g24)
    c: Vertical(g30)
    c: Vertical(g34)
    c: Vertical(g32)
    c: PointOnObject(g21,g2)
    c: PointOnObject(g32,g3)
    c: Vertical(g6)
    c: PointOnObject(g10,g1)
    c: Equal(g48,g49)
    c: Equal(g49,g50)
    c: Equal(g33,g41)
    c: Equal(g41,g30)
    c: Equal(g30,g22)
    c: Equal(g22,g19)
    c: Equal(g19,g11)
    c: Equal(g11,g8)
    c: Equal(g8,g44)
    c: Symmetric(g45,g6,g-2)
    c: DistanceX(g45,g6) = 9.4
    c: DistanceX(g43,g8) = 6.2
    c: Equal(g43,g42)
    c: Equal(g42,g32)
    c: DistanceY(g44,g44) = 1
    c: Equal(g31,g43)
    c: Equal(g43,g21)
    c: Equal(g21,g20)
    c: Equal(g20,g10)
    c: Radius(g49) = 1
    c: Symmetric(g37,g14,g-2)
    c: DistanceX(g37,g14) = 5.6
    c: Symmetric(g43,g8,g-2)
    c: Symmetric(g4,g26,g-1)
    c: DistanceY(g26,g4) = 5.6
    c: Symmetric(g4,g4,g-2)
    c: Equal(g45,g40)
    c: Equal(g45,g7)
    c: Equal(g7,g12)
    c: Equal(g12,g34)
    c: Equal(g34,g29)
    c: Equal(g29,g23)
    c: Equal(g23,g18)
    c: Equal(g39,g46)
    c: Equal(g46,g6)
    c: Equal(g6,g13)
    c: Equal(g13,g17)
    c: Equal(g17,g24)
    c: Equal(g24,g35)
    c: Equal(g35,g28)
    c: Parallel(g38,g47)
    c: Angle(g4,g47) = 2.35619
    c: Symmetric(g38,g35,g-1)
    c: Symmetric(g37,g36,g-1)
    c: Symmetric(g27,g46,g-1)
    c: Distance(g37,g4) = 1
    c: Symmetric(g27,g24,g-2)
    c: Symmetric(g26,g25,g-2)
    c: Symmetric(g36,g15,g-2)
FEATURE [PartDesign::Pad] Pad011
  Length = 290
  Length2 = 100
  Placement = pos=(0,0,0) rot=(1,0,0;1.5708rad)
  Profile = -> Sketch013
  Refine = true
  Type = 0
FEATURE [PartDesign::Body] Body012  label="extrusion-002"
  Group = -> [Sketch013,Pad011]
  Origin = -> Origin018
  Placement = pos=(146.4,140.2,-0.4) rot=(0,0,1;4.71239rad)
  Tip = -> Pad011
FEATURE [Sketcher::SketchObject] Sketch014
  MapMode = 5
  Placement = pos=(0,0,0) rot=(1,0,0;1.5708rad)
  Support = -> [XZ_Plane019]
  sketch-geometry (52):
    g0: LineSegment [constr] StartX=-7.5 StartY=7.5 StartZ=0 EndX=7.5 EndY=7.5 EndZ=0
    g1: LineSegment [constr] StartX=7.5 StartY=7.5 StartZ=0 EndX=7.5 EndY=-7.5 EndZ=0
    g2: LineSegment [constr] StartX=7.5 StartY=-7.5 StartZ=0 EndX=-7.5 EndY=-7.5 EndZ=0
    g3: LineSegment [constr] StartX=-7.5 StartY=-7.5 StartZ=0 EndX=-7.5 EndY=7.5 EndZ=0
    g4: LineSegment StartX=-2.09289 StartY=2.8 StartZ=0 EndX=2.09289 EndY=2.8 EndZ=0
    g5: LineSegment StartX=2.09289 StartY=2.8 StartZ=0 EndX=4.7 EndY=5.40711 EndZ=0
    g6: LineSegment StartX=4.7 StartY=5.40711 StartZ=0 EndX=4.7 EndY=6.5 EndZ=0
    g7: LineSegment StartX=4.7 StartY=6.5 StartZ=0 EndX=3.1 EndY=6.5 EndZ=0
    g8: LineSegment StartX=3.1 StartY=6.5 StartZ=0 EndX=3.1 EndY=7.5 EndZ=0
    g9: LineSegment StartX=3.1 StartY=7.5 StartZ=0 EndX=6.5 EndY=7.5 EndZ=0
    g10: LineSegment StartX=7.5 StartY=6.5 StartZ=0 EndX=7.5 EndY=3.1 EndZ=0
    g11: LineSegment StartX=7.5 StartY=3.1 StartZ=0 EndX=6.5 EndY=3.1 EndZ=0
    g12: LineSegment StartX=6.5 StartY=3.1 StartZ=0 EndX=6.5 EndY=4.7 EndZ=0
    g13: LineSegment StartX=6.5 StartY=4.7 StartZ=0 EndX=5.40711 EndY=4.7 EndZ=0
    g14: LineSegment StartX=5.40711 StartY=4.7 StartZ=0 EndX=2.8 EndY=2.09289 EndZ=0
    g15: LineSegment StartX=2.8 StartY=2.09289 StartZ=0 EndX=2.8 EndY=-2.09289 EndZ=0
    g16: LineSegment StartX=2.8 StartY=-2.09289 StartZ=0 EndX=5.40711 EndY=-4.7 EndZ=0
    g17: LineSegment StartX=5.40711 StartY=-4.7 StartZ=0 EndX=6.5 EndY=-4.7 EndZ=0
    g18: LineSegment StartX=6.5 StartY=-4.7 StartZ=0 EndX=6.5 EndY=-3.1 EndZ=0
    g19: LineSegment StartX=6.5 StartY=-3.1 StartZ=0 EndX=7.5 EndY=-3.1 EndZ=0
    g20: LineSegment StartX=7.5 StartY=-3.1 StartZ=0 EndX=7.5 EndY=-6.5 EndZ=0
    g21: LineSegment StartX=6.5 StartY=-7.5 StartZ=0 EndX=3.1 EndY=-7.5 EndZ=0
    g22: LineSegment StartX=3.1 StartY=-7.5 StartZ=0 EndX=3.1 EndY=-6.5 EndZ=0
    g23: LineSegment StartX=3.1 StartY=-6.5 StartZ=0 EndX=4.7 EndY=-6.5 EndZ=0
    g24: LineSegment StartX=4.7 StartY=-6.5 StartZ=0 EndX=4.7 EndY=-5.40711 EndZ=0
    g25: LineSegment StartX=4.7 StartY=-5.40711 StartZ=0 EndX=2.09289 EndY=-2.8 EndZ=0
    g26: LineSegment StartX=2.09289 StartY=-2.8 StartZ=0 EndX=-2.09289 EndY=-2.8 EndZ=0
    g27: LineSegment StartX=-2.09289 StartY=-2.8 StartZ=0 EndX=-4.7 EndY=-5.40711 EndZ=0
    g28: LineSegment StartX=-4.7 StartY=-5.40711 StartZ=0 EndX=-4.7 EndY=-6.5 EndZ=0
    g29: LineSegment StartX=-4.7 StartY=-6.5 StartZ=0 EndX=-3.1 EndY=-6.5 EndZ=0
    g30: LineSegment StartX=-3.1 StartY=-6.5 StartZ=0 EndX=-3.1 EndY=-7.5 EndZ=0
    g31: LineSegment StartX=-3.1 StartY=-7.5 StartZ=0 EndX=-6.5 EndY=-7.5 EndZ=0
    g32: LineSegment StartX=-7.5 StartY=-6.5 StartZ=0 EndX=-7.5 EndY=-3.1 EndZ=0
    g33: LineSegment StartX=-7.5 StartY=-3.1 StartZ=0 EndX=-6.5 EndY=-3.1 EndZ=0
    g34: LineSegment StartX=-6.5 StartY=-3.1 StartZ=0 EndX=-6.5 EndY=-4.7 EndZ=0
    g35: LineSegment StartX=-6.5 StartY=-4.7 StartZ=0 EndX=-5.40711 EndY=-4.7 EndZ=0
    g36: LineSegment StartX=-5.40711 StartY=-4.7 StartZ=0 EndX=-2.8 EndY=-2.09289 EndZ=0
    g37: LineSegment StartX=-2.8 StartY=-2.09289 StartZ=0 EndX=-2.8 EndY=2.09289 EndZ=0
    g38: LineSegment StartX=-2.8 StartY=2.09289 StartZ=0 EndX=-5.40711 EndY=4.7 EndZ=0
    g39: LineSegment StartX=-5.40711 StartY=4.7 StartZ=0 EndX=-6.5 EndY=4.7 EndZ=0
    g40: LineSegment StartX=-6.5 StartY=4.7 StartZ=0 EndX=-6.5 EndY=3.1 EndZ=0
    g41: LineSegment StartX=-6.5 StartY=3.1 StartZ=0 EndX=-7.5 EndY=3.1 EndZ=0
    g42: LineSegment StartX=-7.5 StartY=3.1 StartZ=0 EndX=-7.5 EndY=6.5 EndZ=0
    g43: LineSegment StartX=-6.5 StartY=7.5 StartZ=0 EndX=-3.1 EndY=7.5 EndZ=0
    g44: LineSegment StartX=-3.1 StartY=7.5 StartZ=0 EndX=-3.1 EndY=6.5 EndZ=0
    g45: LineSegment StartX=-3.1 StartY=6.5 StartZ=0 EndX=-4.7 EndY=6.5 EndZ=0
    g46: LineSegment StartX=-4.7 StartY=6.5 StartZ=0 EndX=-4.7 EndY=5.40711 EndZ=0
    g47: LineSegment StartX=-4.7 StartY=5.40711 StartZ=0 EndX=-2.09289 EndY=2.8 EndZ=0
    g48: ArcOfCircle CenterX=-6.5 CenterY=6.5 CenterZ=0 NormalX=0 NormalY=0 NormalZ=1 AngleXU=0 Radius=1 StartAngle=1.5708 EndAngle=3.14159
    g49: ArcOfCircle CenterX=6.5 CenterY=6.5 CenterZ=0 NormalX=0 NormalY=0 NormalZ=1 AngleXU=0 Radius=1 StartAngle=0 EndAngle=1.5708
    g50: ArcOfCircle CenterX=6.5 CenterY=-6.5 CenterZ=0 NormalX=0 NormalY=0 NormalZ=1 AngleXU=0 Radius=1 StartAngle=4.71239 EndAngle=6.28319
    g51: ArcOfCircle CenterX=-6.5 CenterY=-6.5 CenterZ=0 NormalX=0 NormalY=0 NormalZ=1 AngleXU=0 Radius=1 StartAngle=3.14159 EndAngle=4.71239
  constraints (140):
    c: Coincident(g0,g1)
    c: Coincident(g1,g2)
    c: Coincident(g2,g3)
    c: Coincident(g3,g0)
    c: Horizontal(g0)
    c: Horizontal(g2)
    c: Vertical(g1)
    c: Vertical(g3)
    c: Symmetric(g0,g1,g-1)
    c: Equal(g3,g0)
    c: DistanceY(g3,g3) = 15
    c: Coincident(g4,g5)
    c: Coincident(g5,g6)
    c: Coincident(g6,g7)
    c: Coincident(g7,g8)
    c: Vertical(g8)
    c: Coincident(g8,g9)
    c: Horizontal(g9)
    c: Vertical(g10)
    c: Coincident(g10,g11)
    c: Horizontal(g11)
    c: Coincident(g11,g12)
    c: Vertical(g12)
    c: Coincident(g12,g13)
    c: Horizontal(g13)
    c: Coincident(g13,g14)
    c: Coincident(g14,g15)
    c: Coincident(g15,g16)
    c: Coincident(g16,g17)
    c: Horizontal(g17)
    c: Coincident(g17,g18)
    c: Coincident(g18,g19)
    c: Coincident(g19,g20)
    c: Vertical(g20)
    c: Horizontal(g21)
    c: Coincident(g21,g22)
    c: Coincident(g22,g23)
    c: Horizontal(g23)
    c: Coincident(g23,g24)
    c: Coincident(g24,g25)
    c: Coincident(g25,g26)
    c: Coincident(g26,g27)
    c: Coincident(g27,g28)
    c: Vertical(g28)
    c: Coincident(g28,g29)
    c: Coincident(g29,g30)
    c: Coincident(g30,g31)
    c: Coincident(g32,g33)
    c: Coincident(g33,g34)
    c: Coincident(g34,g35)
    c: Coincident(g35,g36)
    c: Coincident(g36,g37)
    c: Coincident(g37,g38)
    c: Coincident(g38,g39)
    c: Coincident(g39,g40)
    c: Coincident(g40,g41)
    c: Coincident(g41,g42)
    c: Vertical(g42)
    c: Horizontal(g43)
    c: Coincident(g43,g44)
    c: Coincident(g44,g45)
    c: Horizontal(g45)
    c: Coincident(g45,g46)
    c: Coincident(g46,g47)
    c: Coincident(g4,g47)
    c: Tangent(g42,g48) = 1.5708
    c: Tangent(g43,g48) = 1.5708
    c: Tangent(g9,g49) = 1.5708
    c: Tangent(g10,g49) = 1.5708
    c: Tangent(g20,g50) = 1.5708
    c: Tangent(g21,g50) = 1.5708
    c: Tangent(g32,g51) = 1.5708
    c: Tangent(g31,g51) = 1.5708
    c: Horizontal(g41)
    c: Horizontal(g39)
    c: Horizontal(g19)
    c: Horizontal(g31)
    c: Horizontal(g35)
    c: Horizontal(g33)
    c: Vertical(g40)
    c: Vertical(g46)
    c: Vertical(g18)
    c: Vertical(g22)
    c: Vertical(g24)
    c: Vertical(g30)
    c: Vertical(g34)
    c: Vertical(g32)
    c: PointOnObject(g21,g2)
    c: PointOnObject(g32,g3)
    c: Vertical(g6)
    c: PointOnObject(g10,g1)
    c: Equal(g48,g49)
    c: Equal(g49,g50)
    c: Equal(g33,g41)
    c: Equal(g41,g30)
    c: Equal(g30,g22)
    c: Equal(g22,g19)
    c: Equal(g19,g11)
    c: Equal(g11,g8)
    c: Equal(g8,g44)
    c: Symmetric(g45,g6,g-2)
    c: DistanceX(g45,g6) = 9.4
    c: DistanceX(g43,g8) = 6.2
    c: Equal(g43,g42)
    c: Equal(g42,g32)
    c: DistanceY(g44,g44) = 1
    c: Equal(g31,g43)
    c: Equal(g43,g21)
    c: Equal(g21,g20)
    c: Equal(g20,g10)
    c: Radius(g49) = 1
    c: Symmetric(g37,g14,g-2)
    c: DistanceX(g37,g14) = 5.6
    c: Symmetric(g43,g8,g-2)
    c: Symmetric(g4,g26,g-1)
    c: DistanceY(g26,g4) = 5.6
    c: Symmetric(g4,g4,g-2)
    c: Equal(g45,g40)
    c: Equal(g45,g7)
    c: Equal(g7,g12)
    c: Equal(g12,g34)
    c: Equal(g34,g29)
    c: Equal(g29,g23)
    c: Equal(g23,g18)
    c: Equal(g39,g46)
    c: Equal(g46,g6)
    c: Equal(g6,g13)
    c: Equal(g13,g17)
    c: Equal(g17,g24)
    c: Equal(g24,g35)
    c: Equal(g35,g28)
    c: Parallel(g38,g47)
    c: Angle(g4,g47) = 2.35619
    c: Symmetric(g38,g35,g-1)
    c: Symmetric(g37,g36,g-1)
    c: Symmetric(g27,g46,g-1)
    c: Distance(g37,g4) = 1
    c: Symmetric(g27,g24,g-2)
    c: Symmetric(g26,g25,g-2)
    c: Symmetric(g36,g15,g-2)
FEATURE [Sketcher::SketchObject] Sketch015
  MapMode = 5
  Placement = pos=(0,0,0) rot=(1,0,0;1.5708rad)
  Support = -> [XZ_Plane018]
  sketch-geometry (52):
    g0: LineSegment [constr] StartX=-7.5 StartY=7.5 StartZ=0 EndX=7.5 EndY=7.5 EndZ=0
    g1: LineSegment [constr] StartX=7.5 StartY=7.5 StartZ=0 EndX=7.5 EndY=-7.5 EndZ=0
    g2: LineSegment [constr] StartX=7.5 StartY=-7.5 StartZ=0 EndX=-7.5 EndY=-7.5 EndZ=0
    g3: LineSegment [constr] StartX=-7.5 StartY=-7.5 StartZ=0 EndX=-7.5 EndY=7.5 EndZ=0
    g4: LineSegment StartX=-2.09289 StartY=2.8 StartZ=0 EndX=2.09289 EndY=2.8 EndZ=0
    g5: LineSegment StartX=2.09289 StartY=2.8 StartZ=0 EndX=4.7 EndY=5.40711 EndZ=0
    g6: LineSegment StartX=4.7 StartY=5.40711 StartZ=0 EndX=4.7 EndY=6.5 EndZ=0
    g7: LineSegment StartX=4.7 StartY=6.5 StartZ=0 EndX=3.1 EndY=6.5 EndZ=0
    g8: LineSegment StartX=3.1 StartY=6.5 StartZ=0 EndX=3.1 EndY=7.5 EndZ=0
    g9: LineSegment StartX=3.1 StartY=7.5 StartZ=0 EndX=6.5 EndY=7.5 EndZ=0
    g10: LineSegment StartX=7.5 StartY=6.5 StartZ=0 EndX=7.5 EndY=3.1 EndZ=0
    g11: LineSegment StartX=7.5 StartY=3.1 StartZ=0 EndX=6.5 EndY=3.1 EndZ=0
    g12: LineSegment StartX=6.5 StartY=3.1 StartZ=0 EndX=6.5 EndY=4.7 EndZ=0
    g13: LineSegment StartX=6.5 StartY=4.7 StartZ=0 EndX=5.40711 EndY=4.7 EndZ=0
    g14: LineSegment StartX=5.40711 StartY=4.7 StartZ=0 EndX=2.8 EndY=2.09289 EndZ=0
    g15: LineSegment StartX=2.8 StartY=2.09289 StartZ=0 EndX=2.8 EndY=-2.09289 EndZ=0
    g16: LineSegment StartX=2.8 StartY=-2.09289 StartZ=0 EndX=5.40711 EndY=-4.7 EndZ=0
    g17: LineSegment StartX=5.40711 StartY=-4.7 StartZ=0 EndX=6.5 EndY=-4.7 EndZ=0
    g18: LineSegment StartX=6.5 StartY=-4.7 StartZ=0 EndX=6.5 EndY=-3.1 EndZ=0
    g19: LineSegment StartX=6.5 StartY=-3.1 StartZ=0 EndX=7.5 EndY=-3.1 EndZ=0
    g20: LineSegment StartX=7.5 StartY=-3.1 StartZ=0 EndX=7.5 EndY=-6.5 EndZ=0
    g21: LineSegment StartX=6.5 StartY=-7.5 StartZ=0 EndX=3.1 EndY=-7.5 EndZ=0
    g22: LineSegment StartX=3.1 StartY=-7.5 StartZ=0 EndX=3.1 EndY=-6.5 EndZ=0
    g23: LineSegment StartX=3.1 StartY=-6.5 StartZ=0 EndX=4.7 EndY=-6.5 EndZ=0
    g24: LineSegment StartX=4.7 StartY=-6.5 StartZ=0 EndX=4.7 EndY=-5.40711 EndZ=0
    g25: LineSegment StartX=4.7 StartY=-5.40711 StartZ=0 EndX=2.09289 EndY=-2.8 EndZ=0
    g26: LineSegment StartX=2.09289 StartY=-2.8 StartZ=0 EndX=-2.09289 EndY=-2.8 EndZ=0
    g27: LineSegment StartX=-2.09289 StartY=-2.8 StartZ=0 EndX=-4.7 EndY=-5.40711 EndZ=0
    g28: LineSegment StartX=-4.7 StartY=-5.40711 StartZ=0 EndX=-4.7 EndY=-6.5 EndZ=0
    g29: LineSegment StartX=-4.7 StartY=-6.5 StartZ=0 EndX=-3.1 EndY=-6.5 EndZ=0
    g30: LineSegment StartX=-3.1 StartY=-6.5 StartZ=0 EndX=-3.1 EndY=-7.5 EndZ=0
    g31: LineSegment StartX=-3.1 StartY=-7.5 StartZ=0 EndX=-6.5 EndY=-7.5 EndZ=0
    g32: LineSegment StartX=-7.5 StartY=-6.5 StartZ=0 EndX=-7.5 EndY=-3.1 EndZ=0
    g33: LineSegment StartX=-7.5 StartY=-3.1 StartZ=0 EndX=-6.5 EndY=-3.1 EndZ=0
    g34: LineSegment StartX=-6.5 StartY=-3.1 StartZ=0 EndX=-6.5 EndY=-4.7 EndZ=0
    g35: LineSegment StartX=-6.5 StartY=-4.7 StartZ=0 EndX=-5.40711 EndY=-4.7 EndZ=0
    g36: LineSegment StartX=-5.40711 StartY=-4.7 StartZ=0 EndX=-2.8 EndY=-2.09289 EndZ=0
    g37: LineSegment StartX=-2.8 StartY=-2.09289 StartZ=0 EndX=-2.8 EndY=2.09289 EndZ=0
    g38: LineSegment StartX=-2.8 StartY=2.09289 StartZ=0 EndX=-5.40711 EndY=4.7 EndZ=0
    g39: LineSegment StartX=-5.40711 StartY=4.7 StartZ=0 EndX=-6.5 EndY=4.7 EndZ=0
    g40: LineSegment StartX=-6.5 StartY=4.7 StartZ=0 EndX=-6.5 EndY=3.1 EndZ=0
    g41: LineSegment StartX=-6.5 StartY=3.1 StartZ=0 EndX=-7.5 EndY=3.1 EndZ=0
    g42: LineSegment StartX=-7.5 StartY=3.1 StartZ=0 EndX=-7.5 EndY=6.5 EndZ=0
    g43: LineSegment StartX=-6.5 StartY=7.5 StartZ=0 EndX=-3.1 EndY=7.5 EndZ=0
    g44: LineSegment StartX=-3.1 StartY=7.5 StartZ=0 EndX=-3.1 EndY=6.5 EndZ=0
    g45: LineSegment StartX=-3.1 StartY=6.5 StartZ=0 EndX=-4.7 EndY=6.5 EndZ=0
    g46: LineSegment StartX=-4.7 StartY=6.5 StartZ=0 EndX=-4.7 EndY=5.40711 EndZ=0
    g47: LineSegment StartX=-4.7 StartY=5.40711 StartZ=0 EndX=-2.09289 EndY=2.8 EndZ=0
    g48: ArcOfCircle CenterX=-6.5 CenterY=6.5 CenterZ=0 NormalX=0 NormalY=0 NormalZ=1 AngleXU=0 Radius=1 StartAngle=1.5708 EndAngle=3.14159
    g49: ArcOfCircle CenterX=6.5 CenterY=6.5 CenterZ=0 NormalX=0 NormalY=0 NormalZ=1 AngleXU=0 Radius=1 StartAngle=0 EndAngle=1.5708
    g50: ArcOfCircle CenterX=6.5 CenterY=-6.5 CenterZ=0 NormalX=0 NormalY=0 NormalZ=1 AngleXU=0 Radius=1 StartAngle=4.71239 EndAngle=6.28319
    g51: ArcOfCircle CenterX=-6.5 CenterY=-6.5 CenterZ=0 NormalX=0 NormalY=0 NormalZ=1 AngleXU=0 Radius=1 StartAngle=3.14159 EndAngle=4.71239
  constraints (140):
    c: Coincident(g0,g1)
    c: Coincident(g1,g2)
    c: Coincident(g2,g3)
    c: Coincident(g3,g0)
    c: Horizontal(g0)
    c: Horizontal(g2)
    c: Vertical(g1)
    c: Vertical(g3)
    c: Symmetric(g0,g1,g-1)
    c: Equal(g3,g0)
    c: DistanceY(g3,g3) = 15
    c: Coincident(g4,g5)
    c: Coincident(g5,g6)
    c: Coincident(g6,g7)
    c: Coincident(g7,g8)
    c: Vertical(g8)
    c: Coincident(g8,g9)
    c: Horizontal(g9)
    c: Vertical(g10)
    c: Coincident(g10,g11)
    c: Horizontal(g11)
    c: Coincident(g11,g12)
    c: Vertical(g12)
    c: Coincident(g12,g13)
    c: Horizontal(g13)
    c: Coincident(g13,g14)
    c: Coincident(g14,g15)
    c: Coincident(g15,g16)
    c: Coincident(g16,g17)
    c: Horizontal(g17)
    c: Coincident(g17,g18)
    c: Coincident(g18,g19)
    c: Coincident(g19,g20)
    c: Vertical(g20)
    c: Horizontal(g21)
    c: Coincident(g21,g22)
    c: Coincident(g22,g23)
    c: Horizontal(g23)
    c: Coincident(g23,g24)
    c: Coincident(g24,g25)
    c: Coincident(g25,g26)
    c: Coincident(g26,g27)
    c: Coincident(g27,g28)
    c: Vertical(g28)
    c: Coincident(g28,g29)
    c: Coincident(g29,g30)
    c: Coincident(g30,g31)
    c: Coincident(g32,g33)
    c: Coincident(g33,g34)
    c: Coincident(g34,g35)
    c: Coincident(g35,g36)
    c: Coincident(g36,g37)
    c: Coincident(g37,g38)
    c: Coincident(g38,g39)
    c: Coincident(g39,g40)
    c: Coincident(g40,g41)
    c: Coincident(g41,g42)
    c: Vertical(g42)
    c: Horizontal(g43)
    c: Coincident(g43,g44)
    c: Coincident(g44,g45)
    c: Horizontal(g45)
    c: Coincident(g45,g46)
    c: Coincident(g46,g47)
    c: Coincident(g4,g47)
    c: Tangent(g42,g48) = 1.5708
    c: Tangent(g43,g48) = 1.5708
    c: Tangent(g9,g49) = 1.5708
    c: Tangent(g10,g49) = 1.5708
    c: Tangent(g20,g50) = 1.5708
    c: Tangent(g21,g50) = 1.5708
    c: Tangent(g32,g51) = 1.5708
    c: Tangent(g31,g51) = 1.5708
    c: Horizontal(g41)
    c: Horizontal(g39)
    c: Horizontal(g19)
    c: Horizontal(g31)
    c: Horizontal(g35)
    c: Horizontal(g33)
    c: Vertical(g40)
    c: Vertical(g46)
    c: Vertical(g18)
    c: Vertical(g22)
    c: Vertical(g24)
    c: Vertical(g30)
    c: Vertical(g34)
    c: Vertical(g32)
    c: PointOnObject(g21,g2)
    c: PointOnObject(g32,g3)
    c: Vertical(g6)
    c: PointOnObject(g10,g1)
    c: Equal(g48,g49)
    c: Equal(g49,g50)
    c: Equal(g33,g41)
    c: Equal(g41,g30)
    c: Equal(g30,g22)
    c: Equal(g22,g19)
    c: Equal(g19,g11)
    c: Equal(g11,g8)
    c: Equal(g8,g44)
    c: Symmetric(g45,g6,g-2)
    c: DistanceX(g45,g6) = 9.4
    c: DistanceX(g43,g8) = 6.2
    c: Equal(g43,g42)
    c: Equal(g42,g32)
    c: DistanceY(g44,g44) = 1
    c: Equal(g31,g43)
    c: Equal(g43,g21)
    c: Equal(g21,g20)
    c: Equal(g20,g10)
    c: Radius(g49) = 1
    c: Symmetric(g37,g14,g-2)
    c: DistanceX(g37,g14) = 5.6
    c: Symmetric(g43,g8,g-2)
    c: Symmetric(g4,g26,g-1)
    c: DistanceY(g26,g4) = 5.6
    c: Symmetric(g4,g4,g-2)
    c: Equal(g45,g40)
    c: Equal(g45,g7)
    c: Equal(g7,g12)
    c: Equal(g12,g34)
    c: Equal(g34,g29)
    c: Equal(g29,g23)
    c: Equal(g23,g18)
    c: Equal(g39,g46)
    c: Equal(g46,g6)
    c: Equal(g6,g13)
    c: Equal(g13,g17)
    c: Equal(g17,g24)
    c: Equal(g24,g35)
    c: Equal(g35,g28)
    c: Parallel(g38,g47)
    c: Angle(g4,g47) = 2.35619
    c: Symmetric(g38,g35,g-1)
    c: Symmetric(g37,g36,g-1)
    c: Symmetric(g27,g46,g-1)
    c: Distance(g37,g4) = 1
    c: Symmetric(g27,g24,g-2)
    c: Symmetric(g26,g25,g-2)
    c: Symmetric(g36,g15,g-2)
FEATURE [PartDesign::Pad] Pad012
  Length = 230
  Length2 = 100
  Midplane = true
  Placement = pos=(0,0,0) rot=(1,0,0;1.5708rad)
  Profile = -> Sketch014
  Refine = true
  Type = 0
FEATURE [PartDesign::Body] Body013  label="extrusion-004-unused"
  Group = -> [Sketch014,Pad012]
  Origin = -> Origin019
  Placement = pos=(1,-107,0) rot=(0,0,1;1.5708rad)
  Tip = -> Pad012
FEATURE [PartDesign::Pad] Pad013
  Length = 270
  Length2 = 100
  Placement = pos=(0,0,0) rot=(1,0,0;1.5708rad)
  Profile = -> Sketch015
  Refine = true
  Type = 0
FEATURE [PartDesign::Body] Body014  label="extrusion-003"
  Group = -> [Sketch015,Pad013]
  Origin = -> Origin017
  Placement = pos=(152.5,-99.6,-0.5) rot=(0,0,1;3.14159rad)
  Tip = -> Pad013
FEATURE [App::Part] Part004  label="frame-top"
  Group = -> [Body011,Body012,Body014,Body013]
  Origin = -> Origin015
  Placement = pos=(0,0,122) rot=(0,0,1;0rad)
FEATURE [Sketcher::SketchObject] Sketch017
  MapMode = 5
  Placement = pos=(0,0,0) rot=(1,0,0;1.5708rad)
  Support = -> [XZ_Plane023]
  sketch-geometry (52):
    g0: LineSegment [constr] StartX=-7.5 StartY=7.5 StartZ=0 EndX=7.5 EndY=7.5 EndZ=0
    g1: LineSegment [constr] StartX=7.5 StartY=7.5 StartZ=0 EndX=7.5 EndY=-7.5 EndZ=0
    g2: LineSegment [constr] StartX=7.5 StartY=-7.5 StartZ=0 EndX=-7.5 EndY=-7.5 EndZ=0
    g3: LineSegment [constr] StartX=-7.5 StartY=-7.5 StartZ=0 EndX=-7.5 EndY=7.5 EndZ=0
    g4: LineSegment StartX=-2.09289 StartY=2.8 StartZ=0 EndX=2.09289 EndY=2.8 EndZ=0
    g5: LineSegment StartX=2.09289 StartY=2.8 StartZ=0 EndX=4.7 EndY=5.40711 EndZ=0
    g6: LineSegment StartX=4.7 StartY=5.40711 StartZ=0 EndX=4.7 EndY=6.5 EndZ=0
    g7: LineSegment StartX=4.7 StartY=6.5 StartZ=0 EndX=3.1 EndY=6.5 EndZ=0
    g8: LineSegment StartX=3.1 StartY=6.5 StartZ=0 EndX=3.1 EndY=7.5 EndZ=0
    g9: LineSegment StartX=3.1 StartY=7.5 StartZ=0 EndX=6.5 EndY=7.5 EndZ=0
    g10: LineSegment StartX=7.5 StartY=6.5 StartZ=0 EndX=7.5 EndY=3.1 EndZ=0
    g11: LineSegment StartX=7.5 StartY=3.1 StartZ=0 EndX=6.5 EndY=3.1 EndZ=0
    g12: LineSegment StartX=6.5 StartY=3.1 StartZ=0 EndX=6.5 EndY=4.7 EndZ=0
    g13: LineSegment StartX=6.5 StartY=4.7 StartZ=0 EndX=5.40711 EndY=4.7 EndZ=0
    g14: LineSegment StartX=5.40711 StartY=4.7 StartZ=0 EndX=2.8 EndY=2.09289 EndZ=0
    g15: LineSegment StartX=2.8 StartY=2.09289 StartZ=0 EndX=2.8 EndY=-2.09289 EndZ=0
    g16: LineSegment StartX=2.8 StartY=-2.09289 StartZ=0 EndX=5.40711 EndY=-4.7 EndZ=0
    g17: LineSegment StartX=5.40711 StartY=-4.7 StartZ=0 EndX=6.5 EndY=-4.7 EndZ=0
    g18: LineSegment StartX=6.5 StartY=-4.7 StartZ=0 EndX=6.5 EndY=-3.1 EndZ=0
    g19: LineSegment StartX=6.5 StartY=-3.1 StartZ=0 EndX=7.5 EndY=-3.1 EndZ=0
    g20: LineSegment StartX=7.5 StartY=-3.1 StartZ=0 EndX=7.5 EndY=-6.5 EndZ=0
    g21: LineSegment StartX=6.5 StartY=-7.5 StartZ=0 EndX=3.1 EndY=-7.5 EndZ=0
    g22: LineSegment StartX=3.1 StartY=-7.5 StartZ=0 EndX=3.1 EndY=-6.5 EndZ=0
    g23: LineSegment StartX=3.1 StartY=-6.5 StartZ=0 EndX=4.7 EndY=-6.5 EndZ=0
    g24: LineSegment StartX=4.7 StartY=-6.5 StartZ=0 EndX=4.7 EndY=-5.40711 EndZ=0
    g25: LineSegment StartX=4.7 StartY=-5.40711 StartZ=0 EndX=2.09289 EndY=-2.8 EndZ=0
    g26: LineSegment StartX=2.09289 StartY=-2.8 StartZ=0 EndX=-2.09289 EndY=-2.8 EndZ=0
    g27: LineSegment StartX=-2.09289 StartY=-2.8 StartZ=0 EndX=-4.7 EndY=-5.40711 EndZ=0
    g28: LineSegment StartX=-4.7 StartY=-5.40711 StartZ=0 EndX=-4.7 EndY=-6.5 EndZ=0
    g29: LineSegment StartX=-4.7 StartY=-6.5 StartZ=0 EndX=-3.1 EndY=-6.5 EndZ=0
    g30: LineSegment StartX=-3.1 StartY=-6.5 StartZ=0 EndX=-3.1 EndY=-7.5 EndZ=0
    g31: LineSegment StartX=-3.1 StartY=-7.5 StartZ=0 EndX=-6.5 EndY=-7.5 EndZ=0
    g32: LineSegment StartX=-7.5 StartY=-6.5 StartZ=0 EndX=-7.5 EndY=-3.1 EndZ=0
    g33: LineSegment StartX=-7.5 StartY=-3.1 StartZ=0 EndX=-6.5 EndY=-3.1 EndZ=0
    g34: LineSegment StartX=-6.5 StartY=-3.1 StartZ=0 EndX=-6.5 EndY=-4.7 EndZ=0
    g35: LineSegment StartX=-6.5 StartY=-4.7 StartZ=0 EndX=-5.40711 EndY=-4.7 EndZ=0
    g36: LineSegment StartX=-5.40711 StartY=-4.7 StartZ=0 EndX=-2.8 EndY=-2.09289 EndZ=0
    g37: LineSegment StartX=-2.8 StartY=-2.09289 StartZ=0 EndX=-2.8 EndY=2.09289 EndZ=0
    g38: LineSegment StartX=-2.8 StartY=2.09289 StartZ=0 EndX=-5.40711 EndY=4.7 EndZ=0
    g39: LineSegment StartX=-5.40711 StartY=4.7 StartZ=0 EndX=-6.5 EndY=4.7 EndZ=0
    g40: LineSegment StartX=-6.5 StartY=4.7 StartZ=0 EndX=-6.5 EndY=3.1 EndZ=0
    g41: LineSegment StartX=-6.5 StartY=3.1 StartZ=0 EndX=-7.5 EndY=3.1 EndZ=0
    g42: LineSegment StartX=-7.5 StartY=3.1 StartZ=0 EndX=-7.5 EndY=6.5 EndZ=0
    g43: LineSegment StartX=-6.5 StartY=7.5 StartZ=0 EndX=-3.1 EndY=7.5 EndZ=0
    g44: LineSegment StartX=-3.1 StartY=7.5 StartZ=0 EndX=-3.1 EndY=6.5 EndZ=0
    g45: LineSegment StartX=-3.1 StartY=6.5 StartZ=0 EndX=-4.7 EndY=6.5 EndZ=0
    g46: LineSegment StartX=-4.7 StartY=6.5 StartZ=0 EndX=-4.7 EndY=5.40711 EndZ=0
    g47: LineSegment StartX=-4.7 StartY=5.40711 StartZ=0 EndX=-2.09289 EndY=2.8 EndZ=0
    g48: ArcOfCircle CenterX=-6.5 CenterY=6.5 CenterZ=0 NormalX=0 NormalY=0 NormalZ=1 AngleXU=0 Radius=1 StartAngle=1.5708 EndAngle=3.14159
    g49: ArcOfCircle CenterX=6.5 CenterY=6.5 CenterZ=0 NormalX=0 NormalY=0 NormalZ=1 AngleXU=0 Radius=1 StartAngle=0 EndAngle=1.5708
    g50: ArcOfCircle CenterX=6.5 CenterY=-6.5 CenterZ=0 NormalX=0 NormalY=0 NormalZ=1 AngleXU=0 Radius=1 StartAngle=4.71239 EndAngle=6.28319
    g51: ArcOfCircle CenterX=-6.5 CenterY=-6.5 CenterZ=0 NormalX=0 NormalY=0 NormalZ=1 AngleXU=0 Radius=1 StartAngle=3.14159 EndAngle=4.71239
  constraints (140):
    c: Coincident(g0,g1)
    c: Coincident(g1,g2)
    c: Coincident(g2,g3)
    c: Coincident(g3,g0)
    c: Horizontal(g0)
    c: Horizontal(g2)
    c: Vertical(g1)
    c: Vertical(g3)
    c: Symmetric(g0,g1,g-1)
    c: Equal(g3,g0)
    c: DistanceY(g3,g3) = 15
    c: Coincident(g4,g5)
    c: Coincident(g5,g6)
    c: Coincident(g6,g7)
    c: Coincident(g7,g8)
    c: Vertical(g8)
    c: Coincident(g8,g9)
    c: Horizontal(g9)
    c: Vertical(g10)
    c: Coincident(g10,g11)
    c: Horizontal(g11)
    c: Coincident(g11,g12)
    c: Vertical(g12)
    c: Coincident(g12,g13)
    c: Horizontal(g13)
    c: Coincident(g13,g14)
    c: Coincident(g14,g15)
    c: Coincident(g15,g16)
    c: Coincident(g16,g17)
    c: Horizontal(g17)
    c: Coincident(g17,g18)
    c: Coincident(g18,g19)
    c: Coincident(g19,g20)
    c: Vertical(g20)
    c: Horizontal(g21)
    c: Coincident(g21,g22)
    c: Coincident(g22,g23)
    c: Horizontal(g23)
    c: Coincident(g23,g24)
    c: Coincident(g24,g25)
    c: Coincident(g25,g26)
    c: Coincident(g26,g27)
    c: Coincident(g27,g28)
    c: Vertical(g28)
    c: Coincident(g28,g29)
    c: Coincident(g29,g30)
    c: Coincident(g30,g31)
    c: Coincident(g32,g33)
    c: Coincident(g33,g34)
    c: Coincident(g34,g35)
    c: Coincident(g35,g36)
    c: Coincident(g36,g37)
    c: Coincident(g37,g38)
    c: Coincident(g38,g39)
    c: Coincident(g39,g40)
    c: Coincident(g40,g41)
    c: Coincident(g41,g42)
    c: Vertical(g42)
    c: Horizontal(g43)
    c: Coincident(g43,g44)
    c: Coincident(g44,g45)
    c: Horizontal(g45)
    c: Coincident(g45,g46)
    c: Coincident(g46,g47)
    c: Coincident(g4,g47)
    c: Tangent(g42,g48) = 1.5708
    c: Tangent(g43,g48) = 1.5708
    c: Tangent(g9,g49) = 1.5708
    c: Tangent(g10,g49) = 1.5708
    c: Tangent(g20,g50) = 1.5708
    c: Tangent(g21,g50) = 1.5708
    c: Tangent(g32,g51) = 1.5708
    c: Tangent(g31,g51) = 1.5708
    c: Horizontal(g41)
    c: Horizontal(g39)
    c: Horizontal(g19)
    c: Horizontal(g31)
    c: Horizontal(g35)
    c: Horizontal(g33)
    c: Vertical(g40)
    c: Vertical(g46)
    c: Vertical(g18)
    c: Vertical(g22)
    c: Vertical(g24)
    c: Vertical(g30)
    c: Vertical(g34)
    c: Vertical(g32)
    c: PointOnObject(g21,g2)
    c: PointOnObject(g32,g3)
    c: Vertical(g6)
    c: PointOnObject(g10,g1)
    c: Equal(g48,g49)
    c: Equal(g49,g50)
    c: Equal(g33,g41)
    c: Equal(g41,g30)
    c: Equal(g30,g22)
    c: Equal(g22,g19)
    c: Equal(g19,g11)
    c: Equal(g11,g8)
    c: Equal(g8,g44)
    c: Symmetric(g45,g6,g-2)
    c: DistanceX(g45,g6) = 9.4
    c: DistanceX(g43,g8) = 6.2
    c: Equal(g43,g42)
    c: Equal(g42,g32)
    c: DistanceY(g44,g44) = 1
    c: Equal(g31,g43)
    c: Equal(g43,g21)
    c: Equal(g21,g20)
    c: Equal(g20,g10)
    c: Radius(g49) = 1
    c: Symmetric(g37,g14,g-2)
    c: DistanceX(g37,g14) = 5.6
    c: Symmetric(g43,g8,g-2)
    c: Symmetric(g4,g26,g-1)
    c: DistanceY(g26,g4) = 5.6
    c: Symmetric(g4,g4,g-2)
    c: Equal(g45,g40)
    c: Equal(g45,g7)
    c: Equal(g7,g12)
    c: Equal(g12,g34)
    c: Equal(g34,g29)
    c: Equal(g29,g23)
    c: Equal(g23,g18)
    c: Equal(g39,g46)
    c: Equal(g46,g6)
    c: Equal(g6,g13)
    c: Equal(g13,g17)
    c: Equal(g17,g24)
    c: Equal(g24,g35)
    c: Equal(g35,g28)
    c: Parallel(g38,g47)
    c: Angle(g4,g47) = 2.35619
    c: Symmetric(g38,g35,g-1)
    c: Symmetric(g37,g36,g-1)
    c: Symmetric(g27,g46,g-1)
    c: Distance(g37,g4) = 1
    c: Symmetric(g27,g24,g-2)
    c: Symmetric(g26,g25,g-2)
    c: Symmetric(g36,g15,g-2)
FEATURE [PartDesign::Pad] Pad015
  Length = 270
  Length2 = 100
  Placement = pos=(0,0,0) rot=(1,0,0;1.5708rad)
  Profile = -> Sketch017
  Refine = true
  Type = 0
FEATURE [PartDesign::Body] Body015  label="extrusion-012"
  Group = -> [Sketch017,Pad015]
  Origin = -> Origin021
  Placement = pos=(-152.5,-100.2,0) rot=(0,0,1;3.14159rad)
  Tip = -> Pad015
FEATURE [Sketcher::SketchObject] Sketch019
  MapMode = 5
  Placement = pos=(0,0,0) rot=(1,0,0;1.5708rad)
  Support = -> [XZ_Plane024]
  sketch-geometry (52):
    g0: LineSegment [constr] StartX=-7.5 StartY=7.5 StartZ=0 EndX=7.5 EndY=7.5 EndZ=0
    g1: LineSegment [constr] StartX=7.5 StartY=7.5 StartZ=0 EndX=7.5 EndY=-7.5 EndZ=0
    g2: LineSegment [constr] StartX=7.5 StartY=-7.5 StartZ=0 EndX=-7.5 EndY=-7.5 EndZ=0
    g3: LineSegment [constr] StartX=-7.5 StartY=-7.5 StartZ=0 EndX=-7.5 EndY=7.5 EndZ=0
    g4: LineSegment StartX=-2.09289 StartY=2.8 StartZ=0 EndX=2.09289 EndY=2.8 EndZ=0
    g5: LineSegment StartX=2.09289 StartY=2.8 StartZ=0 EndX=4.7 EndY=5.40711 EndZ=0
    g6: LineSegment StartX=4.7 StartY=5.40711 StartZ=0 EndX=4.7 EndY=6.5 EndZ=0
    g7: LineSegment StartX=4.7 StartY=6.5 StartZ=0 EndX=3.1 EndY=6.5 EndZ=0
    g8: LineSegment StartX=3.1 StartY=6.5 StartZ=0 EndX=3.1 EndY=7.5 EndZ=0
    g9: LineSegment StartX=3.1 StartY=7.5 StartZ=0 EndX=6.5 EndY=7.5 EndZ=0
    g10: LineSegment StartX=7.5 StartY=6.5 StartZ=0 EndX=7.5 EndY=3.1 EndZ=0
    g11: LineSegment StartX=7.5 StartY=3.1 StartZ=0 EndX=6.5 EndY=3.1 EndZ=0
    g12: LineSegment StartX=6.5 StartY=3.1 StartZ=0 EndX=6.5 EndY=4.7 EndZ=0
    g13: LineSegment StartX=6.5 StartY=4.7 StartZ=0 EndX=5.40711 EndY=4.7 EndZ=0
    g14: LineSegment StartX=5.40711 StartY=4.7 StartZ=0 EndX=2.8 EndY=2.09289 EndZ=0
    g15: LineSegment StartX=2.8 StartY=2.09289 StartZ=0 EndX=2.8 EndY=-2.09289 EndZ=0
    g16: LineSegment StartX=2.8 StartY=-2.09289 StartZ=0 EndX=5.40711 EndY=-4.7 EndZ=0
    g17: LineSegment StartX=5.40711 StartY=-4.7 StartZ=0 EndX=6.5 EndY=-4.7 EndZ=0
    g18: LineSegment StartX=6.5 StartY=-4.7 StartZ=0 EndX=6.5 EndY=-3.1 EndZ=0
    g19: LineSegment StartX=6.5 StartY=-3.1 StartZ=0 EndX=7.5 EndY=-3.1 EndZ=0
    g20: LineSegment StartX=7.5 StartY=-3.1 StartZ=0 EndX=7.5 EndY=-6.5 EndZ=0
    g21: LineSegment StartX=6.5 StartY=-7.5 StartZ=0 EndX=3.1 EndY=-7.5 EndZ=0
    g22: LineSegment StartX=3.1 StartY=-7.5 StartZ=0 EndX=3.1 EndY=-6.5 EndZ=0
    g23: LineSegment StartX=3.1 StartY=-6.5 StartZ=0 EndX=4.7 EndY=-6.5 EndZ=0
    g24: LineSegment StartX=4.7 StartY=-6.5 StartZ=0 EndX=4.7 EndY=-5.40711 EndZ=0
    g25: LineSegment StartX=4.7 StartY=-5.40711 StartZ=0 EndX=2.09289 EndY=-2.8 EndZ=0
    g26: LineSegment StartX=2.09289 StartY=-2.8 StartZ=0 EndX=-2.09289 EndY=-2.8 EndZ=0
    g27: LineSegment StartX=-2.09289 StartY=-2.8 StartZ=0 EndX=-4.7 EndY=-5.40711 EndZ=0
    g28: LineSegment StartX=-4.7 StartY=-5.40711 StartZ=0 EndX=-4.7 EndY=-6.5 EndZ=0
    g29: LineSegment StartX=-4.7 StartY=-6.5 StartZ=0 EndX=-3.1 EndY=-6.5 EndZ=0
    g30: LineSegment StartX=-3.1 StartY=-6.5 StartZ=0 EndX=-3.1 EndY=-7.5 EndZ=0
    g31: LineSegment StartX=-3.1 StartY=-7.5 StartZ=0 EndX=-6.5 EndY=-7.5 EndZ=0
    g32: LineSegment StartX=-7.5 StartY=-6.5 StartZ=0 EndX=-7.5 EndY=-3.1 EndZ=0
    g33: LineSegment StartX=-7.5 StartY=-3.1 StartZ=0 EndX=-6.5 EndY=-3.1 EndZ=0
    g34: LineSegment StartX=-6.5 StartY=-3.1 StartZ=0 EndX=-6.5 EndY=-4.7 EndZ=0
    g35: LineSegment StartX=-6.5 StartY=-4.7 StartZ=0 EndX=-5.40711 EndY=-4.7 EndZ=0
    g36: LineSegment StartX=-5.40711 StartY=-4.7 StartZ=0 EndX=-2.8 EndY=-2.09289 EndZ=0
    g37: LineSegment StartX=-2.8 StartY=-2.09289 StartZ=0 EndX=-2.8 EndY=2.09289 EndZ=0
    g38: LineSegment StartX=-2.8 StartY=2.09289 StartZ=0 EndX=-5.40711 EndY=4.7 EndZ=0
    g39: LineSegment StartX=-5.40711 StartY=4.7 StartZ=0 EndX=-6.5 EndY=4.7 EndZ=0
    g40: LineSegment StartX=-6.5 StartY=4.7 StartZ=0 EndX=-6.5 EndY=3.1 EndZ=0
    g41: LineSegment StartX=-6.5 StartY=3.1 StartZ=0 EndX=-7.5 EndY=3.1 EndZ=0
    g42: LineSegment StartX=-7.5 StartY=3.1 StartZ=0 EndX=-7.5 EndY=6.5 EndZ=0
    g43: LineSegment StartX=-6.5 StartY=7.5 StartZ=0 EndX=-3.1 EndY=7.5 EndZ=0
    g44: LineSegment StartX=-3.1 StartY=7.5 StartZ=0 EndX=-3.1 EndY=6.5 EndZ=0
    g45: LineSegment StartX=-3.1 StartY=6.5 StartZ=0 EndX=-4.7 EndY=6.5 EndZ=0
    g46: LineSegment StartX=-4.7 StartY=6.5 StartZ=0 EndX=-4.7 EndY=5.40711 EndZ=0
    g47: LineSegment StartX=-4.7 StartY=5.40711 StartZ=0 EndX=-2.09289 EndY=2.8 EndZ=0
    g48: ArcOfCircle CenterX=-6.5 CenterY=6.5 CenterZ=0 NormalX=0 NormalY=0 NormalZ=1 AngleXU=0 Radius=1 StartAngle=1.5708 EndAngle=3.14159
    g49: ArcOfCircle CenterX=6.5 CenterY=6.5 CenterZ=0 NormalX=0 NormalY=0 NormalZ=1 AngleXU=0 Radius=1 StartAngle=0 EndAngle=1.5708
    g50: ArcOfCircle CenterX=6.5 CenterY=-6.5 CenterZ=0 NormalX=0 NormalY=0 NormalZ=1 AngleXU=0 Radius=1 StartAngle=4.71239 EndAngle=6.28319
    g51: ArcOfCircle CenterX=-6.5 CenterY=-6.5 CenterZ=0 NormalX=0 NormalY=0 NormalZ=1 AngleXU=0 Radius=1 StartAngle=3.14159 EndAngle=4.71239
  constraints (140):
    c: Coincident(g0,g1)
    c: Coincident(g1,g2)
    c: Coincident(g2,g3)
    c: Coincident(g3,g0)
    c: Horizontal(g0)
    c: Horizontal(g2)
    c: Vertical(g1)
    c: Vertical(g3)
    c: Symmetric(g0,g1,g-1)
    c: Equal(g3,g0)
    c: DistanceY(g3,g3) = 15
    c: Coincident(g4,g5)
    c: Coincident(g5,g6)
    c: Coincident(g6,g7)
    c: Coincident(g7,g8)
    c: Vertical(g8)
    c: Coincident(g8,g9)
    c: Horizontal(g9)
    c: Vertical(g10)
    c: Coincident(g10,g11)
    c: Horizontal(g11)
    c: Coincident(g11,g12)
    c: Vertical(g12)
    c: Coincident(g12,g13)
    c: Horizontal(g13)
    c: Coincident(g13,g14)
    c: Coincident(g14,g15)
    c: Coincident(g15,g16)
    c: Coincident(g16,g17)
    c: Horizontal(g17)
    c: Coincident(g17,g18)
    c: Coincident(g18,g19)
    c: Coincident(g19,g20)
    c: Vertical(g20)
    c: Horizontal(g21)
    c: Coincident(g21,g22)
    c: Coincident(g22,g23)
    c: Horizontal(g23)
    c: Coincident(g23,g24)
    c: Coincident(g24,g25)
    c: Coincident(g25,g26)
    c: Coincident(g26,g27)
    c: Coincident(g27,g28)
    c: Vertical(g28)
    c: Coincident(g28,g29)
    c: Coincident(g29,g30)
    c: Coincident(g30,g31)
    c: Coincident(g32,g33)
    c: Coincident(g33,g34)
    c: Coincident(g34,g35)
    c: Coincident(g35,g36)
    c: Coincident(g36,g37)
    c: Coincident(g37,g38)
    c: Coincident(g38,g39)
    c: Coincident(g39,g40)
    c: Coincident(g40,g41)
    c: Coincident(g41,g42)
    c: Vertical(g42)
    c: Horizontal(g43)
    c: Coincident(g43,g44)
    c: Coincident(g44,g45)
    c: Horizontal(g45)
    c: Coincident(g45,g46)
    c: Coincident(g46,g47)
    c: Coincident(g4,g47)
    c: Tangent(g42,g48) = 1.5708
    c: Tangent(g43,g48) = 1.5708
    c: Tangent(g9,g49) = 1.5708
    c: Tangent(g10,g49) = 1.5708
    c: Tangent(g20,g50) = 1.5708
    c: Tangent(g21,g50) = 1.5708
    c: Tangent(g32,g51) = 1.5708
    c: Tangent(g31,g51) = 1.5708
    c: Horizontal(g41)
    c: Horizontal(g39)
    c: Horizontal(g19)
    c: Horizontal(g31)
    c: Horizontal(g35)
    c: Horizontal(g33)
    c: Vertical(g40)
    c: Vertical(g46)
    c: Vertical(g18)
    c: Vertical(g22)
    c: Vertical(g24)
    c: Vertical(g30)
    c: Vertical(g34)
    c: Vertical(g32)
    c: PointOnObject(g21,g2)
    c: PointOnObject(g32,g3)
    c: Vertical(g6)
    c: PointOnObject(g10,g1)
    c: Equal(g48,g49)
    c: Equal(g49,g50)
    c: Equal(g33,g41)
    c: Equal(g41,g30)
    c: Equal(g30,g22)
    c: Equal(g22,g19)
    c: Equal(g19,g11)
    c: Equal(g11,g8)
    c: Equal(g8,g44)
    c: Symmetric(g45,g6,g-2)
    c: DistanceX(g45,g6) = 9.4
    c: DistanceX(g43,g8) = 6.2
    c: Equal(g43,g42)
    c: Equal(g42,g32)
    c: DistanceY(g44,g44) = 1
    c: Equal(g31,g43)
    c: Equal(g43,g21)
    c: Equal(g21,g20)
    c: Equal(g20,g10)
    c: Radius(g49) = 1
    c: Symmetric(g37,g14,g-2)
    c: DistanceX(g37,g14) = 5.6
    c: Symmetric(g43,g8,g-2)
    c: Symmetric(g4,g26,g-1)
    c: DistanceY(g26,g4) = 5.6
    c: Symmetric(g4,g4,g-2)
    c: Equal(g45,g40)
    c: Equal(g45,g7)
    c: Equal(g7,g12)
    c: Equal(g12,g34)
    c: Equal(g34,g29)
    c: Equal(g29,g23)
    c: Equal(g23,g18)
    c: Equal(g39,g46)
    c: Equal(g46,g6)
    c: Equal(g6,g13)
    c: Equal(g13,g17)
    c: Equal(g17,g24)
    c: Equal(g24,g35)
    c: Equal(g35,g28)
    c: Parallel(g38,g47)
    c: Angle(g4,g47) = 2.35619
    c: Symmetric(g38,g35,g-1)
    c: Symmetric(g37,g36,g-1)
    c: Symmetric(g27,g46,g-1)
    c: Distance(g37,g4) = 1
    c: Symmetric(g27,g24,g-2)
    c: Symmetric(g26,g25,g-2)
    c: Symmetric(g36,g15,g-2)
FEATURE [PartDesign::Pad] Pad017
  Length = 270
  Length2 = 100
  Placement = pos=(0,0,0) rot=(1,0,0;1.5708rad)
  Profile = -> Sketch019
  Refine = true
  Type = 0
FEATURE [PartDesign::Body] Body018  label="extrusion-013"
  Group = -> [Sketch019,Pad017]
  Origin = -> Origin024
  Placement = pos=(152.5,-100,-0.3) rot=(0,0,1;3.14159rad)
  Tip = -> Pad017
FEATURE [App::Part] Part006  label="frame-top001"
  Group = -> [Body015,Body018]
  Origin = -> Origin025
  Placement = pos=(0,0,170) rot=(0,0,1;0rad)
FEATURE [Mesh::Feature] Z_Motor_Mount_x1
  Placement = pos=(-40,33,-111.4) rot=(1,0,0;3.14159rad)
FEATURE [Mesh::Feature] Rear_Bed_Mount_Left_x1
  Placement = pos=(-45,34,-3.5) rot=(0,0,-1;3.14159rad)
FEATURE [Mesh::Feature] Rear_Bed_Mount_Right_x1
  Placement = pos=(16.8,34.2,-3.5) rot=(0,0,1;3.14159rad)
FEATURE [Mesh::Feature] _a__Foot_Front_x2  label="[a]_Foot_Front_x2"
  Placement = pos=(-43,-260,-142) rot=(-0.707107,-0.707107,0;3.14159rad)
FEATURE [Mesh::Feature] _a__Foot_Front_x2001  label="[a]_Foot_Front_x003"
  Placement = pos=(-247,37,-153) rot=(-1,0,0;3.14159rad)
FEATURE [Mesh::Feature] _a__Foot_Rear_x2  label="[a]_Foot_Rear_x2"
  Placement = pos=(41,-41,-144) rot=(0,-1,0;3.14159rad)
FEATURE [Mesh::Feature] _a__Foot_Rear_x2001  label="[a]_Foot_Rear_x003"
  Placement = pos=(257,-44,-145) rot=(0,1,0;3.14159rad)
FEATURE [App::Part] Part014  label="foot"
  Group = -> [_a__Foot_Front_x2,_a__Foot_Front_x2001,_a__Foot_Rear_x2,_a__Foot_Rear_x2001]
  Origin = -> Origin033
FEATURE [Mesh::Feature] _a__Z_Endstop_Mount_x1  label="[a]_Z_Endstop_Mount_x1"
  Placement = pos=(-149.8,-5,150.8) rot=(-1,0,0;1.5708rad)
FEATURE [Sketcher::SketchObject] Sketch020
  MapMode = 5
  Placement = pos=(0,0,0) rot=(1,0,0;1.5708rad)
  Support = -> [XZ_Plane035]
  sketch-geometry (52):
    g0: LineSegment [constr] StartX=-7.5 StartY=7.5 StartZ=0 EndX=7.5 EndY=7.5 EndZ=0
    g1: LineSegment [constr] StartX=7.5 StartY=7.5 StartZ=0 EndX=7.5 EndY=-7.5 EndZ=0
    g2: LineSegment [constr] StartX=7.5 StartY=-7.5 StartZ=0 EndX=-7.5 EndY=-7.5 EndZ=0
    g3: LineSegment [constr] StartX=-7.5 StartY=-7.5 StartZ=0 EndX=-7.5 EndY=7.5 EndZ=0
    g4: LineSegment StartX=-2.09289 StartY=2.8 StartZ=0 EndX=2.09289 EndY=2.8 EndZ=0
    g5: LineSegment StartX=2.09289 StartY=2.8 StartZ=0 EndX=4.7 EndY=5.40711 EndZ=0
    g6: LineSegment StartX=4.7 StartY=5.40711 StartZ=0 EndX=4.7 EndY=6.5 EndZ=0
    g7: LineSegment StartX=4.7 StartY=6.5 StartZ=0 EndX=3.1 EndY=6.5 EndZ=0
    g8: LineSegment StartX=3.1 StartY=6.5 StartZ=0 EndX=3.1 EndY=7.5 EndZ=0
    g9: LineSegment StartX=3.1 StartY=7.5 StartZ=0 EndX=6.5 EndY=7.5 EndZ=0
    g10: LineSegment StartX=7.5 StartY=6.5 StartZ=0 EndX=7.5 EndY=3.1 EndZ=0
    g11: LineSegment StartX=7.5 StartY=3.1 StartZ=0 EndX=6.5 EndY=3.1 EndZ=0
    g12: LineSegment StartX=6.5 StartY=3.1 StartZ=0 EndX=6.5 EndY=4.7 EndZ=0
    g13: LineSegment StartX=6.5 StartY=4.7 StartZ=0 EndX=5.40711 EndY=4.7 EndZ=0
    g14: LineSegment StartX=5.40711 StartY=4.7 StartZ=0 EndX=2.8 EndY=2.09289 EndZ=0
    g15: LineSegment StartX=2.8 StartY=2.09289 StartZ=0 EndX=2.8 EndY=-2.09289 EndZ=0
    g16: LineSegment StartX=2.8 StartY=-2.09289 StartZ=0 EndX=5.40711 EndY=-4.7 EndZ=0
    g17: LineSegment StartX=5.40711 StartY=-4.7 StartZ=0 EndX=6.5 EndY=-4.7 EndZ=0
    g18: LineSegment StartX=6.5 StartY=-4.7 StartZ=0 EndX=6.5 EndY=-3.1 EndZ=0
    g19: LineSegment StartX=6.5 StartY=-3.1 StartZ=0 EndX=7.5 EndY=-3.1 EndZ=0
    g20: LineSegment StartX=7.5 StartY=-3.1 StartZ=0 EndX=7.5 EndY=-6.5 EndZ=0
    g21: LineSegment StartX=6.5 StartY=-7.5 StartZ=0 EndX=3.1 EndY=-7.5 EndZ=0
    g22: LineSegment StartX=3.1 StartY=-7.5 StartZ=0 EndX=3.1 EndY=-6.5 EndZ=0
    g23: LineSegment StartX=3.1 StartY=-6.5 StartZ=0 EndX=4.7 EndY=-6.5 EndZ=0
    g24: LineSegment StartX=4.7 StartY=-6.5 StartZ=0 EndX=4.7 EndY=-5.40711 EndZ=0
    g25: LineSegment StartX=4.7 StartY=-5.40711 StartZ=0 EndX=2.09289 EndY=-2.8 EndZ=0
    g26: LineSegment StartX=2.09289 StartY=-2.8 StartZ=0 EndX=-2.09289 EndY=-2.8 EndZ=0
    g27: LineSegment StartX=-2.09289 StartY=-2.8 StartZ=0 EndX=-4.7 EndY=-5.40711 EndZ=0
    g28: LineSegment StartX=-4.7 StartY=-5.40711 StartZ=0 EndX=-4.7 EndY=-6.5 EndZ=0
    g29: LineSegment StartX=-4.7 StartY=-6.5 StartZ=0 EndX=-3.1 EndY=-6.5 EndZ=0
    g30: LineSegment StartX=-3.1 StartY=-6.5 StartZ=0 EndX=-3.1 EndY=-7.5 EndZ=0
    g31: LineSegment StartX=-3.1 StartY=-7.5 StartZ=0 EndX=-6.5 EndY=-7.5 EndZ=0
    g32: LineSegment StartX=-7.5 StartY=-6.5 StartZ=0 EndX=-7.5 EndY=-3.1 EndZ=0
    g33: LineSegment StartX=-7.5 StartY=-3.1 StartZ=0 EndX=-6.5 EndY=-3.1 EndZ=0
    g34: LineSegment StartX=-6.5 StartY=-3.1 StartZ=0 EndX=-6.5 EndY=-4.7 EndZ=0
    g35: LineSegment StartX=-6.5 StartY=-4.7 StartZ=0 EndX=-5.40711 EndY=-4.7 EndZ=0
    g36: LineSegment StartX=-5.40711 StartY=-4.7 StartZ=0 EndX=-2.8 EndY=-2.09289 EndZ=0
    g37: LineSegment StartX=-2.8 StartY=-2.09289 StartZ=0 EndX=-2.8 EndY=2.09289 EndZ=0
    g38: LineSegment StartX=-2.8 StartY=2.09289 StartZ=0 EndX=-5.40711 EndY=4.7 EndZ=0
    g39: LineSegment StartX=-5.40711 StartY=4.7 StartZ=0 EndX=-6.5 EndY=4.7 EndZ=0
    g40: LineSegment StartX=-6.5 StartY=4.7 StartZ=0 EndX=-6.5 EndY=3.1 EndZ=0
    g41: LineSegment StartX=-6.5 StartY=3.1 StartZ=0 EndX=-7.5 EndY=3.1 EndZ=0
    g42: LineSegment StartX=-7.5 StartY=3.1 StartZ=0 EndX=-7.5 EndY=6.5 EndZ=0
    g43: LineSegment StartX=-6.5 StartY=7.5 StartZ=0 EndX=-3.1 EndY=7.5 EndZ=0
    g44: LineSegment StartX=-3.1 StartY=7.5 StartZ=0 EndX=-3.1 EndY=6.5 EndZ=0
    g45: LineSegment StartX=-3.1 StartY=6.5 StartZ=0 EndX=-4.7 EndY=6.5 EndZ=0
    g46: LineSegment StartX=-4.7 StartY=6.5 StartZ=0 EndX=-4.7 EndY=5.40711 EndZ=0
    g47: LineSegment StartX=-4.7 StartY=5.40711 StartZ=0 EndX=-2.09289 EndY=2.8 EndZ=0
    g48: ArcOfCircle CenterX=-6.5 CenterY=6.5 CenterZ=0 NormalX=0 NormalY=0 NormalZ=1 AngleXU=0 Radius=1 StartAngle=1.5708 EndAngle=3.14159
    g49: ArcOfCircle CenterX=6.5 CenterY=6.5 CenterZ=0 NormalX=0 NormalY=0 NormalZ=1 AngleXU=0 Radius=1 StartAngle=0 EndAngle=1.5708
    g50: ArcOfCircle CenterX=6.5 CenterY=-6.5 CenterZ=0 NormalX=0 NormalY=0 NormalZ=1 AngleXU=0 Radius=1 StartAngle=4.71239 EndAngle=6.28319
    g51: ArcOfCircle CenterX=-6.5 CenterY=-6.5 CenterZ=0 NormalX=0 NormalY=0 NormalZ=1 AngleXU=0 Radius=1 StartAngle=3.14159 EndAngle=4.71239
  constraints (140):
    c: Coincident(g0,g1)
    c: Coincident(g1,g2)
    c: Coincident(g2,g3)
    c: Coincident(g3,g0)
    c: Horizontal(g0)
    c: Horizontal(g2)
    c: Vertical(g1)
    c: Vertical(g3)
    c: Symmetric(g0,g1,g-1)
    c: Equal(g3,g0)
    c: DistanceY(g3,g3) = 15
    c: Coincident(g4,g5)
    c: Coincident(g5,g6)
    c: Coincident(g6,g7)
    c: Coincident(g7,g8)
    c: Vertical(g8)
    c: Coincident(g8,g9)
    c: Horizontal(g9)
    c: Vertical(g10)
    c: Coincident(g10,g11)
    c: Horizontal(g11)
    c: Coincident(g11,g12)
    c: Vertical(g12)
    c: Coincident(g12,g13)
    c: Horizontal(g13)
    c: Coincident(g13,g14)
    c: Coincident(g14,g15)
    c: Coincident(g15,g16)
    c: Coincident(g16,g17)
    c: Horizontal(g17)
    c: Coincident(g17,g18)
    c: Coincident(g18,g19)
    c: Coincident(g19,g20)
    c: Vertical(g20)
    c: Horizontal(g21)
    c: Coincident(g21,g22)
    c: Coincident(g22,g23)
    c: Horizontal(g23)
    c: Coincident(g23,g24)
    c: Coincident(g24,g25)
    c: Coincident(g25,g26)
    c: Coincident(g26,g27)
    c: Coincident(g27,g28)
    c: Vertical(g28)
    c: Coincident(g28,g29)
    c: Coincident(g29,g30)
    c: Coincident(g30,g31)
    c: Coincident(g32,g33)
    c: Coincident(g33,g34)
    c: Coincident(g34,g35)
    c: Coincident(g35,g36)
    c: Coincident(g36,g37)
    c: Coincident(g37,g38)
    c: Coincident(g38,g39)
    c: Coincident(g39,g40)
    c: Coincident(g40,g41)
    c: Coincident(g41,g42)
    c: Vertical(g42)
    c: Horizontal(g43)
    c: Coincident(g43,g44)
    c: Coincident(g44,g45)
    c: Horizontal(g45)
    c: Coincident(g45,g46)
    c: Coincident(g46,g47)
    c: Coincident(g4,g47)
    c: Tangent(g42,g48) = 1.5708
    c: Tangent(g43,g48) = 1.5708
    c: Tangent(g9,g49) = 1.5708
    c: Tangent(g10,g49) = 1.5708
    c: Tangent(g20,g50) = 1.5708
    c: Tangent(g21,g50) = 1.5708
    c: Tangent(g32,g51) = 1.5708
    c: Tangent(g31,g51) = 1.5708
    c: Horizontal(g41)
    c: Horizontal(g39)
    c: Horizontal(g19)
    c: Horizontal(g31)
    c: Horizontal(g35)
    c: Horizontal(g33)
    c: Vertical(g40)
    c: Vertical(g46)
    c: Vertical(g18)
    c: Vertical(g22)
    c: Vertical(g24)
    c: Vertical(g30)
    c: Vertical(g34)
    c: Vertical(g32)
    c: PointOnObject(g21,g2)
    c: PointOnObject(g32,g3)
    c: Vertical(g6)
    c: PointOnObject(g10,g1)
    c: Equal(g48,g49)
    c: Equal(g49,g50)
    c: Equal(g33,g41)
    c: Equal(g41,g30)
    c: Equal(g30,g22)
    c: Equal(g22,g19)
    c: Equal(g19,g11)
    c: Equal(g11,g8)
    c: Equal(g8,g44)
    c: Symmetric(g45,g6,g-2)
    c: DistanceX(g45,g6) = 9.4
    c: DistanceX(g43,g8) = 6.2
    c: Equal(g43,g42)
    c: Equal(g42,g32)
    c: DistanceY(g44,g44) = 1
    c: Equal(g31,g43)
    c: Equal(g43,g21)
    c: Equal(g21,g20)
    c: Equal(g20,g10)
    c: Radius(g49) = 1
    c: Symmetric(g37,g14,g-2)
    c: DistanceX(g37,g14) = 5.6
    c: Symmetric(g43,g8,g-2)
    c: Symmetric(g4,g26,g-1)
    c: DistanceY(g26,g4) = 5.6
    c: Symmetric(g4,g4,g-2)
    c: Equal(g45,g40)
    c: Equal(g45,g7)
    c: Equal(g7,g12)
    c: Equal(g12,g34)
    c: Equal(g34,g29)
    c: Equal(g29,g23)
    c: Equal(g23,g18)
    c: Equal(g39,g46)
    c: Equal(g46,g6)
    c: Equal(g6,g13)
    c: Equal(g13,g17)
    c: Equal(g17,g24)
    c: Equal(g24,g35)
    c: Equal(g35,g28)
    c: Parallel(g38,g47)
    c: Angle(g4,g47) = 2.35619
    c: Symmetric(g38,g35,g-1)
    c: Symmetric(g37,g36,g-1)
    c: Symmetric(g27,g46,g-1)
    c: Distance(g37,g4) = 1
    c: Symmetric(g27,g24,g-2)
    c: Symmetric(g26,g25,g-2)
    c: Symmetric(g36,g15,g-2)
FEATURE [PartDesign::Pad] Pad018
  Length = 230
  Length2 = 100
  Midplane = true
  Placement = pos=(0,0,0) rot=(1,0,0;1.5708rad)
  Profile = -> Sketch020
  Refine = true
  Type = 0
FEATURE [PartDesign::Body] Body019  label="extrusion-016"
  Group = -> [Sketch020,Pad018]
  Origin = -> Origin036
  Placement = pos=(-35.5,-23.4,-3.5) rot=(0.57735,-0.57735,-0.57735;2.0944rad)
  Tip = -> Pad018
FEATURE [Sketcher::SketchObject] Sketch021
  MapMode = 5
  Placement = pos=(0,0,0) rot=(1,0,0;1.5708rad)
  Support = -> [XZ_Plane036]
  sketch-geometry (52):
    g0: LineSegment [constr] StartX=-7.5 StartY=7.5 StartZ=0 EndX=7.5 EndY=7.5 EndZ=0
    g1: LineSegment [constr] StartX=7.5 StartY=7.5 StartZ=0 EndX=7.5 EndY=-7.5 EndZ=0
    g2: LineSegment [constr] StartX=7.5 StartY=-7.5 StartZ=0 EndX=-7.5 EndY=-7.5 EndZ=0
    g3: LineSegment [constr] StartX=-7.5 StartY=-7.5 StartZ=0 EndX=-7.5 EndY=7.5 EndZ=0
    g4: LineSegment StartX=-2.09289 StartY=2.8 StartZ=0 EndX=2.09289 EndY=2.8 EndZ=0
    g5: LineSegment StartX=2.09289 StartY=2.8 StartZ=0 EndX=4.7 EndY=5.40711 EndZ=0
    g6: LineSegment StartX=4.7 StartY=5.40711 StartZ=0 EndX=4.7 EndY=6.5 EndZ=0
    g7: LineSegment StartX=4.7 StartY=6.5 StartZ=0 EndX=3.1 EndY=6.5 EndZ=0
    g8: LineSegment StartX=3.1 StartY=6.5 StartZ=0 EndX=3.1 EndY=7.5 EndZ=0
    g9: LineSegment StartX=3.1 StartY=7.5 StartZ=0 EndX=6.5 EndY=7.5 EndZ=0
    g10: LineSegment StartX=7.5 StartY=6.5 StartZ=0 EndX=7.5 EndY=3.1 EndZ=0
    g11: LineSegment StartX=7.5 StartY=3.1 StartZ=0 EndX=6.5 EndY=3.1 EndZ=0
    g12: LineSegment StartX=6.5 StartY=3.1 StartZ=0 EndX=6.5 EndY=4.7 EndZ=0
    g13: LineSegment StartX=6.5 StartY=4.7 StartZ=0 EndX=5.40711 EndY=4.7 EndZ=0
    g14: LineSegment StartX=5.40711 StartY=4.7 StartZ=0 EndX=2.8 EndY=2.09289 EndZ=0
    g15: LineSegment StartX=2.8 StartY=2.09289 StartZ=0 EndX=2.8 EndY=-2.09289 EndZ=0
    g16: LineSegment StartX=2.8 StartY=-2.09289 StartZ=0 EndX=5.40711 EndY=-4.7 EndZ=0
    g17: LineSegment StartX=5.40711 StartY=-4.7 StartZ=0 EndX=6.5 EndY=-4.7 EndZ=0
    g18: LineSegment StartX=6.5 StartY=-4.7 StartZ=0 EndX=6.5 EndY=-3.1 EndZ=0
    g19: LineSegment StartX=6.5 StartY=-3.1 StartZ=0 EndX=7.5 EndY=-3.1 EndZ=0
    g20: LineSegment StartX=7.5 StartY=-3.1 StartZ=0 EndX=7.5 EndY=-6.5 EndZ=0
    g21: LineSegment StartX=6.5 StartY=-7.5 StartZ=0 EndX=3.1 EndY=-7.5 EndZ=0
    g22: LineSegment StartX=3.1 StartY=-7.5 StartZ=0 EndX=3.1 EndY=-6.5 EndZ=0
    g23: LineSegment StartX=3.1 StartY=-6.5 StartZ=0 EndX=4.7 EndY=-6.5 EndZ=0
    g24: LineSegment StartX=4.7 StartY=-6.5 StartZ=0 EndX=4.7 EndY=-5.40711 EndZ=0
    g25: LineSegment StartX=4.7 StartY=-5.40711 StartZ=0 EndX=2.09289 EndY=-2.8 EndZ=0
    g26: LineSegment StartX=2.09289 StartY=-2.8 StartZ=0 EndX=-2.09289 EndY=-2.8 EndZ=0
    g27: LineSegment StartX=-2.09289 StartY=-2.8 StartZ=0 EndX=-4.7 EndY=-5.40711 EndZ=0
    g28: LineSegment StartX=-4.7 StartY=-5.40711 StartZ=0 EndX=-4.7 EndY=-6.5 EndZ=0
    g29: LineSegment StartX=-4.7 StartY=-6.5 StartZ=0 EndX=-3.1 EndY=-6.5 EndZ=0
    g30: LineSegment StartX=-3.1 StartY=-6.5 StartZ=0 EndX=-3.1 EndY=-7.5 EndZ=0
    g31: LineSegment StartX=-3.1 StartY=-7.5 StartZ=0 EndX=-6.5 EndY=-7.5 EndZ=0
    g32: LineSegment StartX=-7.5 StartY=-6.5 StartZ=0 EndX=-7.5 EndY=-3.1 EndZ=0
    g33: LineSegment StartX=-7.5 StartY=-3.1 StartZ=0 EndX=-6.5 EndY=-3.1 EndZ=0
    g34: LineSegment StartX=-6.5 StartY=-3.1 StartZ=0 EndX=-6.5 EndY=-4.7 EndZ=0
    g35: LineSegment StartX=-6.5 StartY=-4.7 StartZ=0 EndX=-5.40711 EndY=-4.7 EndZ=0
    g36: LineSegment StartX=-5.40711 StartY=-4.7 StartZ=0 EndX=-2.8 EndY=-2.09289 EndZ=0
    g37: LineSegment StartX=-2.8 StartY=-2.09289 StartZ=0 EndX=-2.8 EndY=2.09289 EndZ=0
    g38: LineSegment StartX=-2.8 StartY=2.09289 StartZ=0 EndX=-5.40711 EndY=4.7 EndZ=0
    g39: LineSegment StartX=-5.40711 StartY=4.7 StartZ=0 EndX=-6.5 EndY=4.7 EndZ=0
    g40: LineSegment StartX=-6.5 StartY=4.7 StartZ=0 EndX=-6.5 EndY=3.1 EndZ=0
    g41: LineSegment StartX=-6.5 StartY=3.1 StartZ=0 EndX=-7.5 EndY=3.1 EndZ=0
    g42: LineSegment StartX=-7.5 StartY=3.1 StartZ=0 EndX=-7.5 EndY=6.5 EndZ=0
    g43: LineSegment StartX=-6.5 StartY=7.5 StartZ=0 EndX=-3.1 EndY=7.5 EndZ=0
    g44: LineSegment StartX=-3.1 StartY=7.5 StartZ=0 EndX=-3.1 EndY=6.5 EndZ=0
    g45: LineSegment StartX=-3.1 StartY=6.5 StartZ=0 EndX=-4.7 EndY=6.5 EndZ=0
    g46: LineSegment StartX=-4.7 StartY=6.5 StartZ=0 EndX=-4.7 EndY=5.40711 EndZ=0
    g47: LineSegment StartX=-4.7 StartY=5.40711 StartZ=0 EndX=-2.09289 EndY=2.8 EndZ=0
    g48: ArcOfCircle CenterX=-6.5 CenterY=6.5 CenterZ=0 NormalX=0 NormalY=0 NormalZ=1 AngleXU=0 Radius=1 StartAngle=1.5708 EndAngle=3.14159
    g49: ArcOfCircle CenterX=6.5 CenterY=6.5 CenterZ=0 NormalX=0 NormalY=0 NormalZ=1 AngleXU=0 Radius=1 StartAngle=0 EndAngle=1.5708
    g50: ArcOfCircle CenterX=6.5 CenterY=-6.5 CenterZ=0 NormalX=0 NormalY=0 NormalZ=1 AngleXU=0 Radius=1 StartAngle=4.71239 EndAngle=6.28319
    g51: ArcOfCircle CenterX=-6.5 CenterY=-6.5 CenterZ=0 NormalX=0 NormalY=0 NormalZ=1 AngleXU=0 Radius=1 StartAngle=3.14159 EndAngle=4.71239
  constraints (140):
    c: Coincident(g0,g1)
    c: Coincident(g1,g2)
    c: Coincident(g2,g3)
    c: Coincident(g3,g0)
    c: Horizontal(g0)
    c: Horizontal(g2)
    c: Vertical(g1)
    c: Vertical(g3)
    c: Symmetric(g0,g1,g-1)
    c: Equal(g3,g0)
    c: DistanceY(g3,g3) = 15
    c: Coincident(g4,g5)
    c: Coincident(g5,g6)
    c: Coincident(g6,g7)
    c: Coincident(g7,g8)
    c: Vertical(g8)
    c: Coincident(g8,g9)
    c: Horizontal(g9)
    c: Vertical(g10)
    c: Coincident(g10,g11)
    c: Horizontal(g11)
    c: Coincident(g11,g12)
    c: Vertical(g12)
    c: Coincident(g12,g13)
    c: Horizontal(g13)
    c: Coincident(g13,g14)
    c: Coincident(g14,g15)
    c: Coincident(g15,g16)
    c: Coincident(g16,g17)
    c: Horizontal(g17)
    c: Coincident(g17,g18)
    c: Coincident(g18,g19)
    c: Coincident(g19,g20)
    c: Vertical(g20)
    c: Horizontal(g21)
    c: Coincident(g21,g22)
    c: Coincident(g22,g23)
    c: Horizontal(g23)
    c: Coincident(g23,g24)
    c: Coincident(g24,g25)
    c: Coincident(g25,g26)
    c: Coincident(g26,g27)
    c: Coincident(g27,g28)
    c: Vertical(g28)
    c: Coincident(g28,g29)
    c: Coincident(g29,g30)
    c: Coincident(g30,g31)
    c: Coincident(g32,g33)
    c: Coincident(g33,g34)
    c: Coincident(g34,g35)
    c: Coincident(g35,g36)
    c: Coincident(g36,g37)
    c: Coincident(g37,g38)
    c: Coincident(g38,g39)
    c: Coincident(g39,g40)
    c: Coincident(g40,g41)
    c: Coincident(g41,g42)
    c: Vertical(g42)
    c: Horizontal(g43)
    c: Coincident(g43,g44)
    c: Coincident(g44,g45)
    c: Horizontal(g45)
    c: Coincident(g45,g46)
    c: Coincident(g46,g47)
    c: Coincident(g4,g47)
    c: Tangent(g42,g48) = 1.5708
    c: Tangent(g43,g48) = 1.5708
    c: Tangent(g9,g49) = 1.5708
    c: Tangent(g10,g49) = 1.5708
    c: Tangent(g20,g50) = 1.5708
    c: Tangent(g21,g50) = 1.5708
    c: Tangent(g32,g51) = 1.5708
    c: Tangent(g31,g51) = 1.5708
    c: Horizontal(g41)
    c: Horizontal(g39)
    c: Horizontal(g19)
    c: Horizontal(g31)
    c: Horizontal(g35)
    c: Horizontal(g33)
    c: Vertical(g40)
    c: Vertical(g46)
    c: Vertical(g18)
    c: Vertical(g22)
    c: Vertical(g24)
    c: Vertical(g30)
    c: Vertical(g34)
    c: Vertical(g32)
    c: PointOnObject(g21,g2)
    c: PointOnObject(g32,g3)
    c: Vertical(g6)
    c: PointOnObject(g10,g1)
    c: Equal(g48,g49)
    c: Equal(g49,g50)
    c: Equal(g33,g41)
    c: Equal(g41,g30)
    c: Equal(g30,g22)
    c: Equal(g22,g19)
    c: Equal(g19,g11)
    c: Equal(g11,g8)
    c: Equal(g8,g44)
    c: Symmetric(g45,g6,g-2)
    c: DistanceX(g45,g6) = 9.4
    c: DistanceX(g43,g8) = 6.2
    c: Equal(g43,g42)
    c: Equal(g42,g32)
    c: DistanceY(g44,g44) = 1
    c: Equal(g31,g43)
    c: Equal(g43,g21)
    c: Equal(g21,g20)
    c: Equal(g20,g10)
    c: Radius(g49) = 1
    c: Symmetric(g37,g14,g-2)
    c: DistanceX(g37,g14) = 5.6
    c: Symmetric(g43,g8,g-2)
    c: Symmetric(g4,g26,g-1)
    c: DistanceY(g26,g4) = 5.6
    c: Symmetric(g4,g4,g-2)
    c: Equal(g45,g40)
    c: Equal(g45,g7)
    c: Equal(g7,g12)
    c: Equal(g12,g34)
    c: Equal(g34,g29)
    c: Equal(g29,g23)
    c: Equal(g23,g18)
    c: Equal(g39,g46)
    c: Equal(g46,g6)
    c: Equal(g6,g13)
    c: Equal(g13,g17)
    c: Equal(g17,g24)
    c: Equal(g24,g35)
    c: Equal(g35,g28)
    c: Parallel(g38,g47)
    c: Angle(g4,g47) = 2.35619
    c: Symmetric(g38,g35,g-1)
    c: Symmetric(g37,g36,g-1)
    c: Symmetric(g27,g46,g-1)
    c: Distance(g37,g4) = 1
    c: Symmetric(g27,g24,g-2)
    c: Symmetric(g26,g25,g-2)
    c: Symmetric(g36,g15,g-2)
FEATURE [PartDesign::Pad] Pad019
  Length = 230
  Length2 = 100
  Midplane = true
  Placement = pos=(0,0,0) rot=(1,0,0;1.5708rad)
  Profile = -> Sketch021
  Refine = true
  Type = 0
FEATURE [PartDesign::Body] Body020  label="extrusion-017"
  Group = -> [Sketch021,Pad019]
  Origin = -> Origin037
  Placement = pos=(34.5,-23.3,-3.5) rot=(1,0,0;1.5708rad)
  Tip = -> Pad019
FEATURE [Mesh::Feature] T8_Nut_Block_x1
  Placement = pos=(150,169,27) rot=(0.707107,-0.707107,0;3.14159rad)
FEATURE [Mesh::Feature] A_Idler_Bottom_x1
  Placement = pos=(0,0,-16) rot=(0,0,1;0rad)
FEATURE [Mesh::Feature] A_Idler_Top_x1
FEATURE [Mesh::Feature] A_Drive_Frame_Bottom_x1
  Placement = pos=(152,144,-26) rot=(0,0,1;3.14159rad)
FEATURE [Mesh::Feature] A_Drive_Frame_Top_x1
  Placement = pos=(127,119.9,0) rot=(0,0,1;3.14159rad)
FEATURE [Mesh::Feature] _a__A_Drive_Tensioner_x1  label="[a]_A_Drive_Tensioner_x1"
  Placement = pos=(90,124.9,3.18e-14) rot=(-0.707107,0.707107,0;3.14159rad)
FEATURE [Mesh::Feature] B_Drive_Frame_Bottom_x1
  Placement = pos=(119,119,-25) rot=(0,0,1;3.14159rad)
FEATURE [Mesh::Feature] B_Drive_Frame_Top_x1
  Placement = pos=(118.8,119.8,0) rot=(0,0,1;3.14159rad)
FEATURE [Mesh::Feature] _a__B_Drive_Tensioner_x1  label="[a]_B_Drive_Tensioner_x1"
  Placement = pos=(-94.1,-125.2,2.79e-14) rot=(-0.707107,-0.707107,0;3.14159rad)
FEATURE [Sketcher::SketchObject] Sketch022
  MapMode = 5
  Support = -> [XY_Plane038]
  sketch-geometry (19):
    g0: LineSegment [constr] StartX=-65 StartY=69.4513 StartZ=0 EndX=65 EndY=69.4513 EndZ=0
    g1: LineSegment [constr] StartX=65 StartY=69.4513 StartZ=0 EndX=65 EndY=-60.5487 EndZ=0
    g2: LineSegment [constr] StartX=65 StartY=-60.5487 StartZ=0 EndX=-65 EndY=-60.5487 EndZ=0
    g3: LineSegment [constr] StartX=-65 StartY=-60.5487 StartZ=0 EndX=-65 EndY=69.4513 EndZ=0
    g4: LineSegment StartX=-60 StartY=69.4513 StartZ=0 EndX=60 EndY=69.4513 EndZ=0
    g5: LineSegment StartX=65 StartY=64.4513 StartZ=0 EndX=65 EndY=-55.5487 EndZ=0
    g6: LineSegment StartX=60 StartY=-60.5487 StartZ=0 EndX=-60 EndY=-60.5487 EndZ=0
    g7: LineSegment StartX=-65 StartY=-55.5487 StartZ=0 EndX=-65 EndY=64.4513 EndZ=0
    g8: ArcOfCircle CenterX=-60 CenterY=64.4513 CenterZ=0 NormalX=0 NormalY=0 NormalZ=1 AngleXU=0 Radius=5 StartAngle=1.5708 EndAngle=3.14159
    g9: ArcOfCircle CenterX=60 CenterY=64.4513 CenterZ=0 NormalX=0 NormalY=0 NormalZ=1 AngleXU=0 Radius=5 StartAngle=4e-16 EndAngle=1.5708
    g10: ArcOfCircle CenterX=60 CenterY=-55.5487 CenterZ=0 NormalX=0 NormalY=0 NormalZ=1 AngleXU=0 Radius=5 StartAngle=4.71239 EndAngle=6.28319
    g11: ArcOfCircle CenterX=-60 CenterY=-55.5487 CenterZ=0 NormalX=0 NormalY=0 NormalZ=1 AngleXU=0 Radius=5 StartAngle=3.14159 EndAngle=4.71239
    g12: Circle CenterX=-60 CenterY=64.4513 CenterZ=0 NormalX=0 NormalY=0 NormalZ=1 AngleXU=0 Radius=1.6
    g13: Circle CenterX=60 CenterY=64.4513 CenterZ=0 NormalX=0 NormalY=0 NormalZ=1 AngleXU=0 Radius=1.6
    g14: Circle CenterX=60 CenterY=-55.5487 CenterZ=0 NormalX=0 NormalY=0 NormalZ=1 AngleXU=0 Radius=1.6
    g15: Circle CenterX=-60 CenterY=-55.5487 CenterZ=0 NormalX=0 NormalY=0 NormalZ=1 AngleXU=0 Radius=1.6
    g16: GeomPoint X=0 Y=-55.5487 Z=0
    g17: Circle CenterX=0 CenterY=-55.5487 CenterZ=0 NormalX=0 NormalY=0 NormalZ=1 AngleXU=0 Radius=1.5
    g18: LineSegment [constr] StartX=-60 StartY=-55.5487 StartZ=0 EndX=60 EndY=-55.5487 EndZ=0
  constraints (44):
    c: Coincident(g0,g1)
    c: Coincident(g1,g2)
    c: Coincident(g2,g3)
    c: Coincident(g3,g0)
    c: Horizontal(g2)
    c: Vertical(g1)
    c: Vertical(g3)
    c: DistanceX(g0,g0) = 130
    c: Horizontal(g4)
    c: Horizontal(g6)
    c: Vertical(g5)
    c: Vertical(g7)
    c: Tangent(g7,g8) = 1.5708
    c: Tangent(g4,g8) = 1.5708
    c: Tangent(g4,g9) = 1.5708
    c: Tangent(g5,g9) = 1.5708
    c: Tangent(g5,g10) = 1.5708
    c: Tangent(g6,g10) = 1.5708
    c: Tangent(g7,g11) = 1.5708
    c: Tangent(g6,g11) = 1.5708
    c: PointOnObject(g6,g2)
    c: PointOnObject(g7,g3)
    c: PointOnObject(g4,g0)
    c: PointOnObject(g5,g1)
    c: Equal(g8,g9)
    c: Equal(g9,g10)
    c: Equal(g10,g11)
    c: Radius(g11) = 5
    c: Equal(g13,g12)
    c: Equal(g12,g15)
    c: Equal(g15,g14)
    c: Coincident(g12,g8)
    c: Coincident(g13,g9)
    c: Coincident(g14,g10)
    c: Coincident(g15,g11)
    c: Diameter(g15) = 3.2
    c: PointOnObject(g16,g-2)
    c: Diameter(g17) = 3
    c: Coincident(g17,g16)
    c: Symmetric(g0,g0,g-2)
    c: Coincident(g18,g10)
    c: Coincident(g11,g18)
    c: PointOnObject(g16,g18)
    c: DistanceY(g2,g0) = 130
FEATURE [PartDesign::Pad] Pad020
  Length = 3
  Length2 = 100
  Midplane = true
  Profile = -> Sketch022
  Refine = true
  Type = 0
FEATURE [PartDesign::Body] Body021  label="heat-bed-130-130"
  Group = -> [Sketch022,Pad020]
  Origin = -> Origin039
  Tip = -> Pad020
FEATURE [Sketcher::SketchObject] Sketch025
  MapMode = 5
  Placement = pos=(0,0,0) rot=(1,0,0;1.5708rad)
  Support = -> [XZ_Plane042]
  sketch-geometry (52):
    g0: LineSegment [constr] StartX=-7.5 StartY=7.5 StartZ=0 EndX=7.5 EndY=7.5 EndZ=0
    g1: LineSegment [constr] StartX=7.5 StartY=7.5 StartZ=0 EndX=7.5 EndY=-7.5 EndZ=0
    g2: LineSegment [constr] StartX=7.5 StartY=-7.5 StartZ=0 EndX=-7.5 EndY=-7.5 EndZ=0
    g3: LineSegment [constr] StartX=-7.5 StartY=-7.5 StartZ=0 EndX=-7.5 EndY=7.5 EndZ=0
    g4: LineSegment StartX=-2.09289 StartY=2.8 StartZ=0 EndX=2.09289 EndY=2.8 EndZ=0
    g5: LineSegment StartX=2.09289 StartY=2.8 StartZ=0 EndX=4.7 EndY=5.40711 EndZ=0
    g6: LineSegment StartX=4.7 StartY=5.40711 StartZ=0 EndX=4.7 EndY=6.5 EndZ=0
    g7: LineSegment StartX=4.7 StartY=6.5 StartZ=0 EndX=3.1 EndY=6.5 EndZ=0
    g8: LineSegment StartX=3.1 StartY=6.5 StartZ=0 EndX=3.1 EndY=7.5 EndZ=0
    g9: LineSegment StartX=3.1 StartY=7.5 StartZ=0 EndX=6.5 EndY=7.5 EndZ=0
    g10: LineSegment StartX=7.5 StartY=6.5 StartZ=0 EndX=7.5 EndY=3.1 EndZ=0
    g11: LineSegment StartX=7.5 StartY=3.1 StartZ=0 EndX=6.5 EndY=3.1 EndZ=0
    g12: LineSegment StartX=6.5 StartY=3.1 StartZ=0 EndX=6.5 EndY=4.7 EndZ=0
    g13: LineSegment StartX=6.5 StartY=4.7 StartZ=0 EndX=5.40711 EndY=4.7 EndZ=0
    g14: LineSegment StartX=5.40711 StartY=4.7 StartZ=0 EndX=2.8 EndY=2.09289 EndZ=0
    g15: LineSegment StartX=2.8 StartY=2.09289 StartZ=0 EndX=2.8 EndY=-2.09289 EndZ=0
    g16: LineSegment StartX=2.8 StartY=-2.09289 StartZ=0 EndX=5.40711 EndY=-4.7 EndZ=0
    g17: LineSegment StartX=5.40711 StartY=-4.7 StartZ=0 EndX=6.5 EndY=-4.7 EndZ=0
    g18: LineSegment StartX=6.5 StartY=-4.7 StartZ=0 EndX=6.5 EndY=-3.1 EndZ=0
    g19: LineSegment StartX=6.5 StartY=-3.1 StartZ=0 EndX=7.5 EndY=-3.1 EndZ=0
    g20: LineSegment StartX=7.5 StartY=-3.1 StartZ=0 EndX=7.5 EndY=-6.5 EndZ=0
    g21: LineSegment StartX=6.5 StartY=-7.5 StartZ=0 EndX=3.1 EndY=-7.5 EndZ=0
    g22: LineSegment StartX=3.1 StartY=-7.5 StartZ=0 EndX=3.1 EndY=-6.5 EndZ=0
    g23: LineSegment StartX=3.1 StartY=-6.5 StartZ=0 EndX=4.7 EndY=-6.5 EndZ=0
    g24: LineSegment StartX=4.7 StartY=-6.5 StartZ=0 EndX=4.7 EndY=-5.40711 EndZ=0
    g25: LineSegment StartX=4.7 StartY=-5.40711 StartZ=0 EndX=2.09289 EndY=-2.8 EndZ=0
    g26: LineSegment StartX=2.09289 StartY=-2.8 StartZ=0 EndX=-2.09289 EndY=-2.8 EndZ=0
    g27: LineSegment StartX=-2.09289 StartY=-2.8 StartZ=0 EndX=-4.7 EndY=-5.40711 EndZ=0
    g28: LineSegment StartX=-4.7 StartY=-5.40711 StartZ=0 EndX=-4.7 EndY=-6.5 EndZ=0
    g29: LineSegment StartX=-4.7 StartY=-6.5 StartZ=0 EndX=-3.1 EndY=-6.5 EndZ=0
    g30: LineSegment StartX=-3.1 StartY=-6.5 StartZ=0 EndX=-3.1 EndY=-7.5 EndZ=0
    g31: LineSegment StartX=-3.1 StartY=-7.5 StartZ=0 EndX=-6.5 EndY=-7.5 EndZ=0
    g32: LineSegment StartX=-7.5 StartY=-6.5 StartZ=0 EndX=-7.5 EndY=-3.1 EndZ=0
    g33: LineSegment StartX=-7.5 StartY=-3.1 StartZ=0 EndX=-6.5 EndY=-3.1 EndZ=0
    g34: LineSegment StartX=-6.5 StartY=-3.1 StartZ=0 EndX=-6.5 EndY=-4.7 EndZ=0
    g35: LineSegment StartX=-6.5 StartY=-4.7 StartZ=0 EndX=-5.40711 EndY=-4.7 EndZ=0
    g36: LineSegment StartX=-5.40711 StartY=-4.7 StartZ=0 EndX=-2.8 EndY=-2.09289 EndZ=0
    g37: LineSegment StartX=-2.8 StartY=-2.09289 StartZ=0 EndX=-2.8 EndY=2.09289 EndZ=0
    g38: LineSegment StartX=-2.8 StartY=2.09289 StartZ=0 EndX=-5.40711 EndY=4.7 EndZ=0
    g39: LineSegment StartX=-5.40711 StartY=4.7 StartZ=0 EndX=-6.5 EndY=4.7 EndZ=0
    g40: LineSegment StartX=-6.5 StartY=4.7 StartZ=0 EndX=-6.5 EndY=3.1 EndZ=0
    g41: LineSegment StartX=-6.5 StartY=3.1 StartZ=0 EndX=-7.5 EndY=3.1 EndZ=0
    g42: LineSegment StartX=-7.5 StartY=3.1 StartZ=0 EndX=-7.5 EndY=6.5 EndZ=0
    g43: LineSegment StartX=-6.5 StartY=7.5 StartZ=0 EndX=-3.1 EndY=7.5 EndZ=0
    g44: LineSegment StartX=-3.1 StartY=7.5 StartZ=0 EndX=-3.1 EndY=6.5 EndZ=0
    g45: LineSegment StartX=-3.1 StartY=6.5 StartZ=0 EndX=-4.7 EndY=6.5 EndZ=0
    g46: LineSegment StartX=-4.7 StartY=6.5 StartZ=0 EndX=-4.7 EndY=5.40711 EndZ=0
    g47: LineSegment StartX=-4.7 StartY=5.40711 StartZ=0 EndX=-2.09289 EndY=2.8 EndZ=0
    g48: ArcOfCircle CenterX=-6.5 CenterY=6.5 CenterZ=0 NormalX=0 NormalY=0 NormalZ=1 AngleXU=0 Radius=1 StartAngle=1.5708 EndAngle=3.14159
    g49: ArcOfCircle CenterX=6.5 CenterY=6.5 CenterZ=0 NormalX=0 NormalY=0 NormalZ=1 AngleXU=0 Radius=1 StartAngle=0 EndAngle=1.5708
    g50: ArcOfCircle CenterX=6.5 CenterY=-6.5 CenterZ=0 NormalX=0 NormalY=0 NormalZ=1 AngleXU=0 Radius=1 StartAngle=4.71239 EndAngle=6.28319
    g51: ArcOfCircle CenterX=-6.5 CenterY=-6.5 CenterZ=0 NormalX=0 NormalY=0 NormalZ=1 AngleXU=0 Radius=1 StartAngle=3.14159 EndAngle=4.71239
  constraints (140):
    c: Coincident(g0,g1)
    c: Coincident(g1,g2)
    c: Coincident(g2,g3)
    c: Coincident(g3,g0)
    c: Horizontal(g0)
    c: Horizontal(g2)
    c: Vertical(g1)
    c: Vertical(g3)
    c: Symmetric(g0,g1,g-1)
    c: Equal(g3,g0)
    c: DistanceY(g3,g3) = 15
    c: Coincident(g4,g5)
    c: Coincident(g5,g6)
    c: Coincident(g6,g7)
    c: Coincident(g7,g8)
    c: Vertical(g8)
    c: Coincident(g8,g9)
    c: Horizontal(g9)
    c: Vertical(g10)
    c: Coincident(g10,g11)
    c: Horizontal(g11)
    c: Coincident(g11,g12)
    c: Vertical(g12)
    c: Coincident(g12,g13)
    c: Horizontal(g13)
    c: Coincident(g13,g14)
    c: Coincident(g14,g15)
    c: Coincident(g15,g16)
    c: Coincident(g16,g17)
    c: Horizontal(g17)
    c: Coincident(g17,g18)
    c: Coincident(g18,g19)
    c: Coincident(g19,g20)
    c: Vertical(g20)
    c: Horizontal(g21)
    c: Coincident(g21,g22)
    c: Coincident(g22,g23)
    c: Horizontal(g23)
    c: Coincident(g23,g24)
    c: Coincident(g24,g25)
    c: Coincident(g25,g26)
    c: Coincident(g26,g27)
    c: Coincident(g27,g28)
    c: Vertical(g28)
    c: Coincident(g28,g29)
    c: Coincident(g29,g30)
    c: Coincident(g30,g31)
    c: Coincident(g32,g33)
    c: Coincident(g33,g34)
    c: Coincident(g34,g35)
    c: Coincident(g35,g36)
    c: Coincident(g36,g37)
    c: Coincident(g37,g38)
    c: Coincident(g38,g39)
    c: Coincident(g39,g40)
    c: Coincident(g40,g41)
    c: Coincident(g41,g42)
    c: Vertical(g42)
    c: Horizontal(g43)
    c: Coincident(g43,g44)
    c: Coincident(g44,g45)
    c: Horizontal(g45)
    c: Coincident(g45,g46)
    c: Coincident(g46,g47)
    c: Coincident(g4,g47)
    c: Tangent(g42,g48) = 1.5708
    c: Tangent(g43,g48) = 1.5708
    c: Tangent(g9,g49) = 1.5708
    c: Tangent(g10,g49) = 1.5708
    c: Tangent(g20,g50) = 1.5708
    c: Tangent(g21,g50) = 1.5708
    c: Tangent(g32,g51) = 1.5708
    c: Tangent(g31,g51) = 1.5708
    c: Horizontal(g41)
    c: Horizontal(g39)
    c: Horizontal(g19)
    c: Horizontal(g31)
    c: Horizontal(g35)
    c: Horizontal(g33)
    c: Vertical(g40)
    c: Vertical(g46)
    c: Vertical(g18)
    c: Vertical(g22)
    c: Vertical(g24)
    c: Vertical(g30)
    c: Vertical(g34)
    c: Vertical(g32)
    c: PointOnObject(g21,g2)
    c: PointOnObject(g32,g3)
    c: Vertical(g6)
    c: PointOnObject(g10,g1)
    c: Equal(g48,g49)
    c: Equal(g49,g50)
    c: Equal(g33,g41)
    c: Equal(g41,g30)
    c: Equal(g30,g22)
    c: Equal(g22,g19)
    c: Equal(g19,g11)
    c: Equal(g11,g8)
    c: Equal(g8,g44)
    c: Symmetric(g45,g6,g-2)
    c: DistanceX(g45,g6) = 9.4
    c: DistanceX(g43,g8) = 6.2
    c: Equal(g43,g42)
    c: Equal(g42,g32)
    c: DistanceY(g44,g44) = 1
    c: Equal(g31,g43)
    c: Equal(g43,g21)
    c: Equal(g21,g20)
    c: Equal(g20,g10)
    c: Radius(g49) = 1
    c: Symmetric(g37,g14,g-2)
    c: DistanceX(g37,g14) = 5.6
    c: Symmetric(g43,g8,g-2)
    c: Symmetric(g4,g26,g-1)
    c: DistanceY(g26,g4) = 5.6
    c: Symmetric(g4,g4,g-2)
    c: Equal(g45,g40)
    c: Equal(g45,g7)
    c: Equal(g7,g12)
    c: Equal(g12,g34)
    c: Equal(g34,g29)
    c: Equal(g29,g23)
    c: Equal(g23,g18)
    c: Equal(g39,g46)
    c: Equal(g46,g6)
    c: Equal(g6,g13)
    c: Equal(g13,g17)
    c: Equal(g17,g24)
    c: Equal(g24,g35)
    c: Equal(g35,g28)
    c: Parallel(g38,g47)
    c: Angle(g4,g47) = 2.35619
    c: Symmetric(g38,g35,g-1)
    c: Symmetric(g37,g36,g-1)
    c: Symmetric(g27,g46,g-1)
    c: Distance(g37,g4) = 1
    c: Symmetric(g27,g24,g-2)
    c: Symmetric(g26,g25,g-2)
    c: Symmetric(g36,g15,g-2)
FEATURE [PartDesign::Pad] Pad023
  Length = 130
  Length2 = 100
  Placement = pos=(0,0,0) rot=(1,0,0;1.5708rad)
  Profile = -> Sketch025
  Refine = true
  Type = 0
FEATURE [PartDesign::Body] Body024  label="heatbed-extrusion-001"
  Group = -> [Sketch025,Pad023]
  Origin = -> Origin043
  Placement = pos=(-25,31.8,13) rot=(0,0,1;0rad)
  Tip = -> Pad023
FEATURE [Sketcher::SketchObject] Sketch026
  MapMode = 5
  Placement = pos=(0,0,0) rot=(1,0,0;1.5708rad)
  Support = -> [XZ_Plane043]
  sketch-geometry (52):
    g0: LineSegment [constr] StartX=-7.5 StartY=7.5 StartZ=0 EndX=7.5 EndY=7.5 EndZ=0
    g1: LineSegment [constr] StartX=7.5 StartY=7.5 StartZ=0 EndX=7.5 EndY=-7.5 EndZ=0
    g2: LineSegment [constr] StartX=7.5 StartY=-7.5 StartZ=0 EndX=-7.5 EndY=-7.5 EndZ=0
    g3: LineSegment [constr] StartX=-7.5 StartY=-7.5 StartZ=0 EndX=-7.5 EndY=7.5 EndZ=0
    g4: LineSegment StartX=-2.09289 StartY=2.8 StartZ=0 EndX=2.09289 EndY=2.8 EndZ=0
    g5: LineSegment StartX=2.09289 StartY=2.8 StartZ=0 EndX=4.7 EndY=5.40711 EndZ=0
    g6: LineSegment StartX=4.7 StartY=5.40711 StartZ=0 EndX=4.7 EndY=6.5 EndZ=0
    g7: LineSegment StartX=4.7 StartY=6.5 StartZ=0 EndX=3.1 EndY=6.5 EndZ=0
    g8: LineSegment StartX=3.1 StartY=6.5 StartZ=0 EndX=3.1 EndY=7.5 EndZ=0
    g9: LineSegment StartX=3.1 StartY=7.5 StartZ=0 EndX=6.5 EndY=7.5 EndZ=0
    g10: LineSegment StartX=7.5 StartY=6.5 StartZ=0 EndX=7.5 EndY=3.1 EndZ=0
    g11: LineSegment StartX=7.5 StartY=3.1 StartZ=0 EndX=6.5 EndY=3.1 EndZ=0
    g12: LineSegment StartX=6.5 StartY=3.1 StartZ=0 EndX=6.5 EndY=4.7 EndZ=0
    g13: LineSegment StartX=6.5 StartY=4.7 StartZ=0 EndX=5.40711 EndY=4.7 EndZ=0
    g14: LineSegment StartX=5.40711 StartY=4.7 StartZ=0 EndX=2.8 EndY=2.09289 EndZ=0
    g15: LineSegment StartX=2.8 StartY=2.09289 StartZ=0 EndX=2.8 EndY=-2.09289 EndZ=0
    g16: LineSegment StartX=2.8 StartY=-2.09289 StartZ=0 EndX=5.40711 EndY=-4.7 EndZ=0
    g17: LineSegment StartX=5.40711 StartY=-4.7 StartZ=0 EndX=6.5 EndY=-4.7 EndZ=0
    g18: LineSegment StartX=6.5 StartY=-4.7 StartZ=0 EndX=6.5 EndY=-3.1 EndZ=0
    g19: LineSegment StartX=6.5 StartY=-3.1 StartZ=0 EndX=7.5 EndY=-3.1 EndZ=0
    g20: LineSegment StartX=7.5 StartY=-3.1 StartZ=0 EndX=7.5 EndY=-6.5 EndZ=0
    g21: LineSegment StartX=6.5 StartY=-7.5 StartZ=0 EndX=3.1 EndY=-7.5 EndZ=0
    g22: LineSegment StartX=3.1 StartY=-7.5 StartZ=0 EndX=3.1 EndY=-6.5 EndZ=0
    g23: LineSegment StartX=3.1 StartY=-6.5 StartZ=0 EndX=4.7 EndY=-6.5 EndZ=0
    g24: LineSegment StartX=4.7 StartY=-6.5 StartZ=0 EndX=4.7 EndY=-5.40711 EndZ=0
    g25: LineSegment StartX=4.7 StartY=-5.40711 StartZ=0 EndX=2.09289 EndY=-2.8 EndZ=0
    g26: LineSegment StartX=2.09289 StartY=-2.8 StartZ=0 EndX=-2.09289 EndY=-2.8 EndZ=0
    g27: LineSegment StartX=-2.09289 StartY=-2.8 StartZ=0 EndX=-4.7 EndY=-5.40711 EndZ=0
    g28: LineSegment StartX=-4.7 StartY=-5.40711 StartZ=0 EndX=-4.7 EndY=-6.5 EndZ=0
    g29: LineSegment StartX=-4.7 StartY=-6.5 StartZ=0 EndX=-3.1 EndY=-6.5 EndZ=0
    g30: LineSegment StartX=-3.1 StartY=-6.5 StartZ=0 EndX=-3.1 EndY=-7.5 EndZ=0
    g31: LineSegment StartX=-3.1 StartY=-7.5 StartZ=0 EndX=-6.5 EndY=-7.5 EndZ=0
    g32: LineSegment StartX=-7.5 StartY=-6.5 StartZ=0 EndX=-7.5 EndY=-3.1 EndZ=0
    g33: LineSegment StartX=-7.5 StartY=-3.1 StartZ=0 EndX=-6.5 EndY=-3.1 EndZ=0
    g34: LineSegment StartX=-6.5 StartY=-3.1 StartZ=0 EndX=-6.5 EndY=-4.7 EndZ=0
    g35: LineSegment StartX=-6.5 StartY=-4.7 StartZ=0 EndX=-5.40711 EndY=-4.7 EndZ=0
    g36: LineSegment StartX=-5.40711 StartY=-4.7 StartZ=0 EndX=-2.8 EndY=-2.09289 EndZ=0
    g37: LineSegment StartX=-2.8 StartY=-2.09289 StartZ=0 EndX=-2.8 EndY=2.09289 EndZ=0
    g38: LineSegment StartX=-2.8 StartY=2.09289 StartZ=0 EndX=-5.40711 EndY=4.7 EndZ=0
    g39: LineSegment StartX=-5.40711 StartY=4.7 StartZ=0 EndX=-6.5 EndY=4.7 EndZ=0
    g40: LineSegment StartX=-6.5 StartY=4.7 StartZ=0 EndX=-6.5 EndY=3.1 EndZ=0
    g41: LineSegment StartX=-6.5 StartY=3.1 StartZ=0 EndX=-7.5 EndY=3.1 EndZ=0
    g42: LineSegment StartX=-7.5 StartY=3.1 StartZ=0 EndX=-7.5 EndY=6.5 EndZ=0
    g43: LineSegment StartX=-6.5 StartY=7.5 StartZ=0 EndX=-3.1 EndY=7.5 EndZ=0
    g44: LineSegment StartX=-3.1 StartY=7.5 StartZ=0 EndX=-3.1 EndY=6.5 EndZ=0
    g45: LineSegment StartX=-3.1 StartY=6.5 StartZ=0 EndX=-4.7 EndY=6.5 EndZ=0
    g46: LineSegment StartX=-4.7 StartY=6.5 StartZ=0 EndX=-4.7 EndY=5.40711 EndZ=0
    g47: LineSegment StartX=-4.7 StartY=5.40711 StartZ=0 EndX=-2.09289 EndY=2.8 EndZ=0
    g48: ArcOfCircle CenterX=-6.5 CenterY=6.5 CenterZ=0 NormalX=0 NormalY=0 NormalZ=1 AngleXU=0 Radius=1 StartAngle=1.5708 EndAngle=3.14159
    g49: ArcOfCircle CenterX=6.5 CenterY=6.5 CenterZ=0 NormalX=0 NormalY=0 NormalZ=1 AngleXU=0 Radius=1 StartAngle=0 EndAngle=1.5708
    g50: ArcOfCircle CenterX=6.5 CenterY=-6.5 CenterZ=0 NormalX=0 NormalY=0 NormalZ=1 AngleXU=0 Radius=1 StartAngle=4.71239 EndAngle=6.28319
    g51: ArcOfCircle CenterX=-6.5 CenterY=-6.5 CenterZ=0 NormalX=0 NormalY=0 NormalZ=1 AngleXU=0 Radius=1 StartAngle=3.14159 EndAngle=4.71239
  constraints (140):
    c: Coincident(g0,g1)
    c: Coincident(g1,g2)
    c: Coincident(g2,g3)
    c: Coincident(g3,g0)
    c: Horizontal(g0)
    c: Horizontal(g2)
    c: Vertical(g1)
    c: Vertical(g3)
    c: Symmetric(g0,g1,g-1)
    c: Equal(g3,g0)
    c: DistanceY(g3,g3) = 15
    c: Coincident(g4,g5)
    c: Coincident(g5,g6)
    c: Coincident(g6,g7)
    c: Coincident(g7,g8)
    c: Vertical(g8)
    c: Coincident(g8,g9)
    c: Horizontal(g9)
    c: Vertical(g10)
    c: Coincident(g10,g11)
    c: Horizontal(g11)
    c: Coincident(g11,g12)
    c: Vertical(g12)
    c: Coincident(g12,g13)
    c: Horizontal(g13)
    c: Coincident(g13,g14)
    c: Coincident(g14,g15)
    c: Coincident(g15,g16)
    c: Coincident(g16,g17)
    c: Horizontal(g17)
    c: Coincident(g17,g18)
    c: Coincident(g18,g19)
    c: Coincident(g19,g20)
    c: Vertical(g20)
    c: Horizontal(g21)
    c: Coincident(g21,g22)
    c: Coincident(g22,g23)
    c: Horizontal(g23)
    c: Coincident(g23,g24)
    c: Coincident(g24,g25)
    c: Coincident(g25,g26)
    c: Coincident(g26,g27)
    c: Coincident(g27,g28)
    c: Vertical(g28)
    c: Coincident(g28,g29)
    c: Coincident(g29,g30)
    c: Coincident(g30,g31)
    c: Coincident(g32,g33)
    c: Coincident(g33,g34)
    c: Coincident(g34,g35)
    c: Coincident(g35,g36)
    c: Coincident(g36,g37)
    c: Coincident(g37,g38)
    c: Coincident(g38,g39)
    c: Coincident(g39,g40)
    c: Coincident(g40,g41)
    c: Coincident(g41,g42)
    c: Vertical(g42)
    c: Horizontal(g43)
    c: Coincident(g43,g44)
    c: Coincident(g44,g45)
    c: Horizontal(g45)
    c: Coincident(g45,g46)
    c: Coincident(g46,g47)
    c: Coincident(g4,g47)
    c: Tangent(g42,g48) = 1.5708
    c: Tangent(g43,g48) = 1.5708
    c: Tangent(g9,g49) = 1.5708
    c: Tangent(g10,g49) = 1.5708
    c: Tangent(g20,g50) = 1.5708
    c: Tangent(g21,g50) = 1.5708
    c: Tangent(g32,g51) = 1.5708
    c: Tangent(g31,g51) = 1.5708
    c: Horizontal(g41)
    c: Horizontal(g39)
    c: Horizontal(g19)
    c: Horizontal(g31)
    c: Horizontal(g35)
    c: Horizontal(g33)
    c: Vertical(g40)
    c: Vertical(g46)
    c: Vertical(g18)
    c: Vertical(g22)
    c: Vertical(g24)
    c: Vertical(g30)
    c: Vertical(g34)
    c: Vertical(g32)
    c: PointOnObject(g21,g2)
    c: PointOnObject(g32,g3)
    c: Vertical(g6)
    c: PointOnObject(g10,g1)
    c: Equal(g48,g49)
    c: Equal(g49,g50)
    c: Equal(g33,g41)
    c: Equal(g41,g30)
    c: Equal(g30,g22)
    c: Equal(g22,g19)
    c: Equal(g19,g11)
    c: Equal(g11,g8)
    c: Equal(g8,g44)
    c: Symmetric(g45,g6,g-2)
    c: DistanceX(g45,g6) = 9.4
    c: DistanceX(g43,g8) = 6.2
    c: Equal(g43,g42)
    c: Equal(g42,g32)
    c: DistanceY(g44,g44) = 1
    c: Equal(g31,g43)
    c: Equal(g43,g21)
    c: Equal(g21,g20)
    c: Equal(g20,g10)
    c: Radius(g49) = 1
    c: Symmetric(g37,g14,g-2)
    c: DistanceX(g37,g14) = 5.6
    c: Symmetric(g43,g8,g-2)
    c: Symmetric(g4,g26,g-1)
    c: DistanceY(g26,g4) = 5.6
    c: Symmetric(g4,g4,g-2)
    c: Equal(g45,g40)
    c: Equal(g45,g7)
    c: Equal(g7,g12)
    c: Equal(g12,g34)
    c: Equal(g34,g29)
    c: Equal(g29,g23)
    c: Equal(g23,g18)
    c: Equal(g39,g46)
    c: Equal(g46,g6)
    c: Equal(g6,g13)
    c: Equal(g13,g17)
    c: Equal(g17,g24)
    c: Equal(g24,g35)
    c: Equal(g35,g28)
    c: Parallel(g38,g47)
    c: Angle(g4,g47) = 2.35619
    c: Symmetric(g38,g35,g-1)
    c: Symmetric(g37,g36,g-1)
    c: Symmetric(g27,g46,g-1)
    c: Distance(g37,g4) = 1
    c: Symmetric(g27,g24,g-2)
    c: Symmetric(g26,g25,g-2)
    c: Symmetric(g36,g15,g-2)
FEATURE [PartDesign::Pad] Pad024
  Length = 135
  Length2 = 100
  Placement = pos=(0,0,0) rot=(1,0,0;1.5708rad)
  Profile = -> Sketch026
  Refine = true
  Type = 0
FEATURE [PartDesign::Body] Body025  label="heatbed-extrusion-002"
  Group = -> [Sketch026,Pad024]
  Origin = -> Origin044
  Placement = pos=(21.8,31.8,9) rot=(0,0,1;0rad)
  Tip = -> Pad024
FEATURE [Mesh::Feature] Front_Bed_Mount_x1
  Placement = pos=(-151.5,47,0) rot=(0,0,1;4.71239rad)
FEATURE [Part::Feature] Part__Feature  label="sheild base"
  shape: bbox 81.5 x 39.6 x 150.2 mm, 669 faces (baked)
FEATURE [Part::Feature] Part__Feature001  label="sheild top part"
  Placement = pos=(0,39.6,-75) rot=(0,0,1;0rad)
  shape: bbox 81.5 x 35.76 x 150 mm, 422 faces (baked)
FEATURE [Part::Feature] Part__Feature002  label="4020 Fan Blades"
  Placement = pos=(0,5,0) rot=(0.203927,0,0.978986;3.14159rad)
  shape: bbox 37.2 x 15 x 37.03 mm, 50 faces (baked)
FEATURE [Part::Feature] Part__Feature003  label="4020 Fan Body"
  shape: bbox 43 x 20 x 42.3 mm, 193 faces (baked)
FEATURE [Part::Feature] Part__Feature004  label="4020 Fan PCB"
  Placement = pos=(0,5.45,0) rot=(0,0,1;0rad)
  shape: bbox 22 x 0.9 x 22 mm, 16 faces, 3 solids (baked)
FEATURE [App::Part] _020_Fan  label="4020 Fan"
  Group = -> [Part__Feature002,Part__Feature003,Part__Feature004]
  Origin = -> Origin047
  Placement = pos=(-19.25,19.3,-64.3) rot=(0,-0.707107,0.707107;3.14159rad)
FEATURE [Part::Feature] Part__Feature005  label="AC Power Socket_킔O_O"
  Placement = pos=(26,16.5,-78) rot=(0,0,-1;1.5708rad)
  shape: bbox 24 x 31 x 26.5 mm, 706 faces, 4 solids (baked)
FEATURE [Part::Feature] Part__Feature006  label="inside"
  Placement = pos=(0,2.8,0) rot=(0,0,1;0rad)
  shape: bbox 77.25 x 1.4 x 148.6 mm, 10 faces (baked)
FEATURE [Part::Feature] Part__Feature007  label="M3 Screw"
  Placement = pos=(-40.75,29.1,-50.5) rot=(0,0,1;1.5708rad)
  shape: bbox 6.198 x 5.647 x 5.647 mm, 54 faces (baked)
FEATURE [Part::Feature] Part__Feature008  label="M3 Screw001"
  Placement = pos=(-40.75,29.1,70.5) rot=(0,0,1;1.5708rad)
  shape: bbox 6.198 x 5.647 x 5.647 mm, 54 faces (baked)
FEATURE [Part::Feature] Part__Feature009  label="M3 Screw002"
  Placement = pos=(40.75,29.1,70.5) rot=(0,0,-1;1.5708rad)
  shape: bbox 6.198 x 5.647 x 5.647 mm, 54 faces (baked)
FEATURE [Part::Feature] Part__Feature010  label="M3 Screw003"
  Placement = pos=(40.75,29.1,-70.5) rot=(0,0,-1;1.5708rad)
  shape: bbox 6.198 x 5.647 x 5.647 mm, 54 faces (baked)
FEATURE [App::Part] Enhance_250W  label="Enhance 250W"
  Group = -> [Part__Feature,Part__Feature001,_020_Fan,Part__Feature005,Part__Feature006,Part__Feature007,Part__Feature008,Part__Feature009,Part__Feature010]
  Origin = -> Origin048
  Placement = pos=(-0.5,22.2,0) rot=(0,0,1;3.14159rad)
FEATURE [App::Part] Part019  label="power-supply"
  Group = -> [Enhance_250W]
  Origin = -> Origin045
  Placement = pos=(0,-3.49e-14,-157.1) rot=(1,0,0;4.71239rad)
FEATURE [Sketcher::SketchObject] Sketch027
  MapMode = 5
  Placement = pos=(0,0,0) rot=(1,0,0;1.5708rad)
  Support = -> [XZ_Plane048]
  sketch-geometry (52):
    g0: LineSegment [constr] StartX=-7.5 StartY=7.5 StartZ=0 EndX=7.5 EndY=7.5 EndZ=0
    g1: LineSegment [constr] StartX=7.5 StartY=7.5 StartZ=0 EndX=7.5 EndY=-7.5 EndZ=0
    g2: LineSegment [constr] StartX=7.5 StartY=-7.5 StartZ=0 EndX=-7.5 EndY=-7.5 EndZ=0
    g3: LineSegment [constr] StartX=-7.5 StartY=-7.5 StartZ=0 EndX=-7.5 EndY=7.5 EndZ=0
    g4: LineSegment StartX=-2.09289 StartY=2.8 StartZ=0 EndX=2.09289 EndY=2.8 EndZ=0
    g5: LineSegment StartX=2.09289 StartY=2.8 StartZ=0 EndX=4.7 EndY=5.40711 EndZ=0
    g6: LineSegment StartX=4.7 StartY=5.40711 StartZ=0 EndX=4.7 EndY=6.5 EndZ=0
    g7: LineSegment StartX=4.7 StartY=6.5 StartZ=0 EndX=3.1 EndY=6.5 EndZ=0
    g8: LineSegment StartX=3.1 StartY=6.5 StartZ=0 EndX=3.1 EndY=7.5 EndZ=0
    g9: LineSegment StartX=3.1 StartY=7.5 StartZ=0 EndX=6.5 EndY=7.5 EndZ=0
    g10: LineSegment StartX=7.5 StartY=6.5 StartZ=0 EndX=7.5 EndY=3.1 EndZ=0
    g11: LineSegment StartX=7.5 StartY=3.1 StartZ=0 EndX=6.5 EndY=3.1 EndZ=0
    g12: LineSegment StartX=6.5 StartY=3.1 StartZ=0 EndX=6.5 EndY=4.7 EndZ=0
    g13: LineSegment StartX=6.5 StartY=4.7 StartZ=0 EndX=5.40711 EndY=4.7 EndZ=0
    g14: LineSegment StartX=5.40711 StartY=4.7 StartZ=0 EndX=2.8 EndY=2.09289 EndZ=0
    g15: LineSegment StartX=2.8 StartY=2.09289 StartZ=0 EndX=2.8 EndY=-2.09289 EndZ=0
    g16: LineSegment StartX=2.8 StartY=-2.09289 StartZ=0 EndX=5.40711 EndY=-4.7 EndZ=0
    g17: LineSegment StartX=5.40711 StartY=-4.7 StartZ=0 EndX=6.5 EndY=-4.7 EndZ=0
    g18: LineSegment StartX=6.5 StartY=-4.7 StartZ=0 EndX=6.5 EndY=-3.1 EndZ=0
    g19: LineSegment StartX=6.5 StartY=-3.1 StartZ=0 EndX=7.5 EndY=-3.1 EndZ=0
    g20: LineSegment StartX=7.5 StartY=-3.1 StartZ=0 EndX=7.5 EndY=-6.5 EndZ=0
    g21: LineSegment StartX=6.5 StartY=-7.5 StartZ=0 EndX=3.1 EndY=-7.5 EndZ=0
    g22: LineSegment StartX=3.1 StartY=-7.5 StartZ=0 EndX=3.1 EndY=-6.5 EndZ=0
    g23: LineSegment StartX=3.1 StartY=-6.5 StartZ=0 EndX=4.7 EndY=-6.5 EndZ=0
    g24: LineSegment StartX=4.7 StartY=-6.5 StartZ=0 EndX=4.7 EndY=-5.40711 EndZ=0
    g25: LineSegment StartX=4.7 StartY=-5.40711 StartZ=0 EndX=2.09289 EndY=-2.8 EndZ=0
    g26: LineSegment StartX=2.09289 StartY=-2.8 StartZ=0 EndX=-2.09289 EndY=-2.8 EndZ=0
    g27: LineSegment StartX=-2.09289 StartY=-2.8 StartZ=0 EndX=-4.7 EndY=-5.40711 EndZ=0
    g28: LineSegment StartX=-4.7 StartY=-5.40711 StartZ=0 EndX=-4.7 EndY=-6.5 EndZ=0
    g29: LineSegment StartX=-4.7 StartY=-6.5 StartZ=0 EndX=-3.1 EndY=-6.5 EndZ=0
    g30: LineSegment StartX=-3.1 StartY=-6.5 StartZ=0 EndX=-3.1 EndY=-7.5 EndZ=0
    g31: LineSegment StartX=-3.1 StartY=-7.5 StartZ=0 EndX=-6.5 EndY=-7.5 EndZ=0
    g32: LineSegment StartX=-7.5 StartY=-6.5 StartZ=0 EndX=-7.5 EndY=-3.1 EndZ=0
    g33: LineSegment StartX=-7.5 StartY=-3.1 StartZ=0 EndX=-6.5 EndY=-3.1 EndZ=0
    g34: LineSegment StartX=-6.5 StartY=-3.1 StartZ=0 EndX=-6.5 EndY=-4.7 EndZ=0
    g35: LineSegment StartX=-6.5 StartY=-4.7 StartZ=0 EndX=-5.40711 EndY=-4.7 EndZ=0
    g36: LineSegment StartX=-5.40711 StartY=-4.7 StartZ=0 EndX=-2.8 EndY=-2.09289 EndZ=0
    g37: LineSegment StartX=-2.8 StartY=-2.09289 StartZ=0 EndX=-2.8 EndY=2.09289 EndZ=0
    g38: LineSegment StartX=-2.8 StartY=2.09289 StartZ=0 EndX=-5.40711 EndY=4.7 EndZ=0
    g39: LineSegment StartX=-5.40711 StartY=4.7 StartZ=0 EndX=-6.5 EndY=4.7 EndZ=0
    g40: LineSegment StartX=-6.5 StartY=4.7 StartZ=0 EndX=-6.5 EndY=3.1 EndZ=0
    g41: LineSegment StartX=-6.5 StartY=3.1 StartZ=0 EndX=-7.5 EndY=3.1 EndZ=0
    g42: LineSegment StartX=-7.5 StartY=3.1 StartZ=0 EndX=-7.5 EndY=6.5 EndZ=0
    g43: LineSegment StartX=-6.5 StartY=7.5 StartZ=0 EndX=-3.1 EndY=7.5 EndZ=0
    g44: LineSegment StartX=-3.1 StartY=7.5 StartZ=0 EndX=-3.1 EndY=6.5 EndZ=0
    g45: LineSegment StartX=-3.1 StartY=6.5 StartZ=0 EndX=-4.7 EndY=6.5 EndZ=0
    g46: LineSegment StartX=-4.7 StartY=6.5 StartZ=0 EndX=-4.7 EndY=5.40711 EndZ=0
    g47: LineSegment StartX=-4.7 StartY=5.40711 StartZ=0 EndX=-2.09289 EndY=2.8 EndZ=0
    g48: ArcOfCircle CenterX=-6.5 CenterY=6.5 CenterZ=0 NormalX=0 NormalY=0 NormalZ=1 AngleXU=0 Radius=1 StartAngle=1.5708 EndAngle=3.14159
    g49: ArcOfCircle CenterX=6.5 CenterY=6.5 CenterZ=0 NormalX=0 NormalY=0 NormalZ=1 AngleXU=0 Radius=1 StartAngle=0 EndAngle=1.5708
    g50: ArcOfCircle CenterX=6.5 CenterY=-6.5 CenterZ=0 NormalX=0 NormalY=0 NormalZ=1 AngleXU=0 Radius=1 StartAngle=4.71239 EndAngle=6.28319
    g51: ArcOfCircle CenterX=-6.5 CenterY=-6.5 CenterZ=0 NormalX=0 NormalY=0 NormalZ=1 AngleXU=0 Radius=1 StartAngle=3.14159 EndAngle=4.71239
  constraints (140):
    c: Coincident(g0,g1)
    c: Coincident(g1,g2)
    c: Coincident(g2,g3)
    c: Coincident(g3,g0)
    c: Horizontal(g0)
    c: Horizontal(g2)
    c: Vertical(g1)
    c: Vertical(g3)
    c: Symmetric(g0,g1,g-1)
    c: Equal(g3,g0)
    c: DistanceY(g3,g3) = 15
    c: Coincident(g4,g5)
    c: Coincident(g5,g6)
    c: Coincident(g6,g7)
    c: Coincident(g7,g8)
    c: Vertical(g8)
    c: Coincident(g8,g9)
    c: Horizontal(g9)
    c: Vertical(g10)
    c: Coincident(g10,g11)
    c: Horizontal(g11)
    c: Coincident(g11,g12)
    c: Vertical(g12)
    c: Coincident(g12,g13)
    c: Horizontal(g13)
    c: Coincident(g13,g14)
    c: Coincident(g14,g15)
    c: Coincident(g15,g16)
    c: Coincident(g16,g17)
    c: Horizontal(g17)
    c: Coincident(g17,g18)
    c: Coincident(g18,g19)
    c: Coincident(g19,g20)
    c: Vertical(g20)
    c: Horizontal(g21)
    c: Coincident(g21,g22)
    c: Coincident(g22,g23)
    c: Horizontal(g23)
    c: Coincident(g23,g24)
    c: Coincident(g24,g25)
    c: Coincident(g25,g26)
    c: Coincident(g26,g27)
    c: Coincident(g27,g28)
    c: Vertical(g28)
    c: Coincident(g28,g29)
    c: Coincident(g29,g30)
    c: Coincident(g30,g31)
    c: Coincident(g32,g33)
    c: Coincident(g33,g34)
    c: Coincident(g34,g35)
    c: Coincident(g35,g36)
    c: Coincident(g36,g37)
    c: Coincident(g37,g38)
    c: Coincident(g38,g39)
    c: Coincident(g39,g40)
    c: Coincident(g40,g41)
    c: Coincident(g41,g42)
    c: Vertical(g42)
    c: Horizontal(g43)
    c: Coincident(g43,g44)
    c: Coincident(g44,g45)
    c: Horizontal(g45)
    c: Coincident(g45,g46)
    c: Coincident(g46,g47)
    c: Coincident(g4,g47)
    c: Tangent(g42,g48) = 1.5708
    c: Tangent(g43,g48) = 1.5708
    c: Tangent(g9,g49) = 1.5708
    c: Tangent(g10,g49) = 1.5708
    c: Tangent(g20,g50) = 1.5708
    c: Tangent(g21,g50) = 1.5708
    c: Tangent(g32,g51) = 1.5708
    c: Tangent(g31,g51) = 1.5708
    c: Horizontal(g41)
    c: Horizontal(g39)
    c: Horizontal(g19)
    c: Horizontal(g31)
    c: Horizontal(g35)
    c: Horizontal(g33)
    c: Vertical(g40)
    c: Vertical(g46)
    c: Vertical(g18)
    c: Vertical(g22)
    c: Vertical(g24)
    c: Vertical(g30)
    c: Vertical(g34)
    c: Vertical(g32)
    c: PointOnObject(g21,g2)
    c: PointOnObject(g32,g3)
    c: Vertical(g6)
    c: PointOnObject(g10,g1)
    c: Equal(g48,g49)
    c: Equal(g49,g50)
    c: Equal(g33,g41)
    c: Equal(g41,g30)
    c: Equal(g30,g22)
    c: Equal(g22,g19)
    c: Equal(g19,g11)
    c: Equal(g11,g8)
    c: Equal(g8,g44)
    c: Symmetric(g45,g6,g-2)
    c: DistanceX(g45,g6) = 9.4
    c: DistanceX(g43,g8) = 6.2
    c: Equal(g43,g42)
    c: Equal(g42,g32)
    c: DistanceY(g44,g44) = 1
    c: Equal(g31,g43)
    c: Equal(g43,g21)
    c: Equal(g21,g20)
    c: Equal(g20,g10)
    c: Radius(g49) = 1
    c: Symmetric(g37,g14,g-2)
    c: DistanceX(g37,g14) = 5.6
    c: Symmetric(g43,g8,g-2)
    c: Symmetric(g4,g26,g-1)
    c: DistanceY(g26,g4) = 5.6
    c: Symmetric(g4,g4,g-2)
    c: Equal(g45,g40)
    c: Equal(g45,g7)
    c: Equal(g7,g12)
    c: Equal(g12,g34)
    c: Equal(g34,g29)
    c: Equal(g29,g23)
    c: Equal(g23,g18)
    c: Equal(g39,g46)
    c: Equal(g46,g6)
    c: Equal(g6,g13)
    c: Equal(g13,g17)
    c: Equal(g17,g24)
    c: Equal(g24,g35)
    c: Equal(g35,g28)
    c: Parallel(g38,g47)
    c: Angle(g4,g47) = 2.35619
    c: Symmetric(g38,g35,g-1)
    c: Symmetric(g37,g36,g-1)
    c: Symmetric(g27,g46,g-1)
    c: Distance(g37,g4) = 1
    c: Symmetric(g27,g24,g-2)
    c: Symmetric(g26,g25,g-2)
    c: Symmetric(g36,g15,g-2)
FEATURE [PartDesign::Pad] Pad025
  Length = 100
  Length2 = 100
  Midplane = true
  Placement = pos=(0,0,0) rot=(1,0,0;1.5708rad)
  Profile = -> Sketch027
  Refine = true
  Type = 0
FEATURE [PartDesign::Body] Body027
  Group = -> [Sketch027,Pad025]
  Origin = -> Origin049
  Placement = pos=(-1,-6,9) rot=(0,0,1;1.5708rad)
  Tip = -> Pad025
FEATURE [App::Part] Part020
  Group = -> [T8_Nut_Block_x1,Body027]
  Origin = -> Origin050
  Placement = pos=(0,45.3,0) rot=(0,0,1;0rad)
FEATURE [App::Part] Part012  label="Rear_Bed_Mount"
  Group = -> [Rear_Bed_Mount_Left_x1,Rear_Bed_Mount_Right_x1,Body024,Body025,Front_Bed_Mount_x1,Part020]
  Origin = -> Origin031
  Placement = pos=(1.6,48.4,-22) rot=(0,0,1;0rad)
FEATURE [Sketcher::SketchObject] Sketch029
  MapMode = 5
  Support = -> [XY_Plane051]
  sketch-geometry (4):
    g0: LineSegment StartX=-65 StartY=32.9951 StartZ=0 EndX=65 EndY=32.9951 EndZ=0
    g1: LineSegment StartX=65 StartY=32.9951 StartZ=0 EndX=65 EndY=-87.0049 EndZ=0
    g2: LineSegment StartX=65 StartY=-87.0049 StartZ=0 EndX=-65 EndY=-87.0049 EndZ=0
    g3: LineSegment StartX=-65 StartY=-87.0049 StartZ=0 EndX=-65 EndY=32.9951 EndZ=0
  constraints (11):
    c: Coincident(g0,g1)
    c: Coincident(g1,g2)
    c: Coincident(g2,g3)
    c: Coincident(g3,g0)
    c: Horizontal(g0)
    c: Vertical(g1)
    c: Vertical(g3)
    c: Symmetric(g2,g1,g-2)
    c: DistanceX(g2,g2) = 130
    c: DistanceY(g3,g3) = 120
    c: DistanceY(g2,g-1) = 87.0049
FEATURE [PartDesign::Body] Body029
  Origin = -> Origin053
FEATURE [PartDesign::Pad] Pad028
  Length = 1
  Length2 = 100
  Profile = -> Sketch029
  Refine = true
  Type = 0
FEATURE [PartDesign::Body] Body028
  Group = -> [Sketch029,Pad028]
  Origin = -> Origin052
  Placement = pos=(0,4,0) rot=(0,0,1;0rad)
  Tip = -> Pad028
FEATURE [App::Part] Part021  label="head-move-area"
  Group = -> [Body028,Body029]
  Origin = -> Origin051
  Placement = pos=(0,-3,0) rot=(0,0,1;0rad)
FEATURE [Sketcher::SketchObject] Sketch035
  MapMode = 5
  Support = -> [XY_Plane065]
  sketch-geometry (4):
    g0: LineSegment StartX=-65 StartY=65 StartZ=0 EndX=65 EndY=65 EndZ=0
    g1: LineSegment StartX=65 StartY=65 StartZ=0 EndX=65 EndY=-65 EndZ=0
    g2: LineSegment StartX=65 StartY=-65 StartZ=0 EndX=-65 EndY=-65 EndZ=0
    g3: LineSegment StartX=-65 StartY=-65 StartZ=0 EndX=-65 EndY=65 EndZ=0
  constraints (11):
    c: Coincident(g0,g1)
    c: Coincident(g1,g2)
    c: Coincident(g2,g3)
    c: Coincident(g3,g0)
    c: Horizontal(g0)
    c: Horizontal(g2)
    c: Vertical(g1)
    c: Vertical(g3)
    c: Symmetric(g0,g1,g-1)
    c: Equal(g0,g3)
    c: DistanceX(g0,g0) = 130
FEATURE [PartDesign::Pad] Pad033
  Length = 130
  Length2 = 100
  Midplane = true
  Profile = -> Sketch035
  Refine = true
  Type = 0
FEATURE [PartDesign::Body] Body034  label="target-print-volume"
  Group = -> [Sketch035,Pad033]
  Origin = -> Origin066
  Tip = -> Pad033
FEATURE [Mesh::Feature] Toolhead_Left_Threaded_V6_x002
  Placement = pos=(-13,-103,-174) rot=(0.57735,0.57735,0.57735;2.0944rad)
FEATURE [Mesh::Feature] _a__Toolhead_Blower_Duct_Right_TV6_x002  label="[a]_Toolhead_Blower_Duct_Right_TV6_x002"
  Placement = pos=(30.5,-152,145) rot=(0.57735,0.57735,-0.57735;4.18879rad)
FEATURE [Sketcher::SketchObject] Sketch038
  MapMode = 5
  Placement = pos=(0,0,0) rot=(1,0,0;1.5708rad)
  Support = -> [XZ_Plane070]
  sketch-geometry (52):
    g0: LineSegment [constr] StartX=-7.5 StartY=7.5 StartZ=0 EndX=7.5 EndY=7.5 EndZ=0
    g1: LineSegment [constr] StartX=7.5 StartY=7.5 StartZ=0 EndX=7.5 EndY=-7.5 EndZ=0
    g2: LineSegment [constr] StartX=7.5 StartY=-7.5 StartZ=0 EndX=-7.5 EndY=-7.5 EndZ=0
    g3: LineSegment [constr] StartX=-7.5 StartY=-7.5 StartZ=0 EndX=-7.5 EndY=7.5 EndZ=0
    g4: LineSegment StartX=-2.09289 StartY=2.8 StartZ=0 EndX=2.09289 EndY=2.8 EndZ=0
    g5: LineSegment StartX=2.09289 StartY=2.8 StartZ=0 EndX=4.7 EndY=5.40711 EndZ=0
    g6: LineSegment StartX=4.7 StartY=5.40711 StartZ=0 EndX=4.7 EndY=6.5 EndZ=0
    g7: LineSegment StartX=4.7 StartY=6.5 StartZ=0 EndX=3.1 EndY=6.5 EndZ=0
    g8: LineSegment StartX=3.1 StartY=6.5 StartZ=0 EndX=3.1 EndY=7.5 EndZ=0
    g9: LineSegment StartX=3.1 StartY=7.5 StartZ=0 EndX=6.5 EndY=7.5 EndZ=0
    g10: LineSegment StartX=7.5 StartY=6.5 StartZ=0 EndX=7.5 EndY=3.1 EndZ=0
    g11: LineSegment StartX=7.5 StartY=3.1 StartZ=0 EndX=6.5 EndY=3.1 EndZ=0
    g12: LineSegment StartX=6.5 StartY=3.1 StartZ=0 EndX=6.5 EndY=4.7 EndZ=0
    g13: LineSegment StartX=6.5 StartY=4.7 StartZ=0 EndX=5.40711 EndY=4.7 EndZ=0
    g14: LineSegment StartX=5.40711 StartY=4.7 StartZ=0 EndX=2.8 EndY=2.09289 EndZ=0
    g15: LineSegment StartX=2.8 StartY=2.09289 StartZ=0 EndX=2.8 EndY=-2.09289 EndZ=0
    g16: LineSegment StartX=2.8 StartY=-2.09289 StartZ=0 EndX=5.40711 EndY=-4.7 EndZ=0
    g17: LineSegment StartX=5.40711 StartY=-4.7 StartZ=0 EndX=6.5 EndY=-4.7 EndZ=0
    g18: LineSegment StartX=6.5 StartY=-4.7 StartZ=0 EndX=6.5 EndY=-3.1 EndZ=0
    g19: LineSegment StartX=6.5 StartY=-3.1 StartZ=0 EndX=7.5 EndY=-3.1 EndZ=0
    g20: LineSegment StartX=7.5 StartY=-3.1 StartZ=0 EndX=7.5 EndY=-6.5 EndZ=0
    g21: LineSegment StartX=6.5 StartY=-7.5 StartZ=0 EndX=3.1 EndY=-7.5 EndZ=0
    g22: LineSegment StartX=3.1 StartY=-7.5 StartZ=0 EndX=3.1 EndY=-6.5 EndZ=0
    g23: LineSegment StartX=3.1 StartY=-6.5 StartZ=0 EndX=4.7 EndY=-6.5 EndZ=0
    g24: LineSegment StartX=4.7 StartY=-6.5 StartZ=0 EndX=4.7 EndY=-5.40711 EndZ=0
    g25: LineSegment StartX=4.7 StartY=-5.40711 StartZ=0 EndX=2.09289 EndY=-2.8 EndZ=0
    g26: LineSegment StartX=2.09289 StartY=-2.8 StartZ=0 EndX=-2.09289 EndY=-2.8 EndZ=0
    g27: LineSegment StartX=-2.09289 StartY=-2.8 StartZ=0 EndX=-4.7 EndY=-5.40711 EndZ=0
    g28: LineSegment StartX=-4.7 StartY=-5.40711 StartZ=0 EndX=-4.7 EndY=-6.5 EndZ=0
    g29: LineSegment StartX=-4.7 StartY=-6.5 StartZ=0 EndX=-3.1 EndY=-6.5 EndZ=0
    g30: LineSegment StartX=-3.1 StartY=-6.5 StartZ=0 EndX=-3.1 EndY=-7.5 EndZ=0
    g31: LineSegment StartX=-3.1 StartY=-7.5 StartZ=0 EndX=-6.5 EndY=-7.5 EndZ=0
    g32: LineSegment StartX=-7.5 StartY=-6.5 StartZ=0 EndX=-7.5 EndY=-3.1 EndZ=0
    g33: LineSegment StartX=-7.5 StartY=-3.1 StartZ=0 EndX=-6.5 EndY=-3.1 EndZ=0
    g34: LineSegment StartX=-6.5 StartY=-3.1 StartZ=0 EndX=-6.5 EndY=-4.7 EndZ=0
    g35: LineSegment StartX=-6.5 StartY=-4.7 StartZ=0 EndX=-5.40711 EndY=-4.7 EndZ=0
    g36: LineSegment StartX=-5.40711 StartY=-4.7 StartZ=0 EndX=-2.8 EndY=-2.09289 EndZ=0
    g37: LineSegment StartX=-2.8 StartY=-2.09289 StartZ=0 EndX=-2.8 EndY=2.09289 EndZ=0
    g38: LineSegment StartX=-2.8 StartY=2.09289 StartZ=0 EndX=-5.40711 EndY=4.7 EndZ=0
    g39: LineSegment StartX=-5.40711 StartY=4.7 StartZ=0 EndX=-6.5 EndY=4.7 EndZ=0
    g40: LineSegment StartX=-6.5 StartY=4.7 StartZ=0 EndX=-6.5 EndY=3.1 EndZ=0
    g41: LineSegment StartX=-6.5 StartY=3.1 StartZ=0 EndX=-7.5 EndY=3.1 EndZ=0
    g42: LineSegment StartX=-7.5 StartY=3.1 StartZ=0 EndX=-7.5 EndY=6.5 EndZ=0
    g43: LineSegment StartX=-6.5 StartY=7.5 StartZ=0 EndX=-3.1 EndY=7.5 EndZ=0
    g44: LineSegment StartX=-3.1 StartY=7.5 StartZ=0 EndX=-3.1 EndY=6.5 EndZ=0
    g45: LineSegment StartX=-3.1 StartY=6.5 StartZ=0 EndX=-4.7 EndY=6.5 EndZ=0
    g46: LineSegment StartX=-4.7 StartY=6.5 StartZ=0 EndX=-4.7 EndY=5.40711 EndZ=0
    g47: LineSegment StartX=-4.7 StartY=5.40711 StartZ=0 EndX=-2.09289 EndY=2.8 EndZ=0
    g48: ArcOfCircle CenterX=-6.5 CenterY=6.5 CenterZ=0 NormalX=0 NormalY=0 NormalZ=1 AngleXU=0 Radius=1 StartAngle=1.5708 EndAngle=3.14159
    g49: ArcOfCircle CenterX=6.5 CenterY=6.5 CenterZ=0 NormalX=0 NormalY=0 NormalZ=1 AngleXU=0 Radius=1 StartAngle=0 EndAngle=1.5708
    g50: ArcOfCircle CenterX=6.5 CenterY=-6.5 CenterZ=0 NormalX=0 NormalY=0 NormalZ=1 AngleXU=0 Radius=1 StartAngle=4.71239 EndAngle=6.28319
    g51: ArcOfCircle CenterX=-6.5 CenterY=-6.5 CenterZ=0 NormalX=0 NormalY=0 NormalZ=1 AngleXU=0 Radius=1 StartAngle=3.14159 EndAngle=4.71239
  constraints (140):
    c: Coincident(g0,g1)
    c: Coincident(g1,g2)
    c: Coincident(g2,g3)
    c: Coincident(g3,g0)
    c: Horizontal(g0)
    c: Horizontal(g2)
    c: Vertical(g1)
    c: Vertical(g3)
    c: Symmetric(g0,g1,g-1)
    c: Equal(g3,g0)
    c: DistanceY(g3,g3) = 15
    c: Coincident(g4,g5)
    c: Coincident(g5,g6)
    c: Coincident(g6,g7)
    c: Coincident(g7,g8)
    c: Vertical(g8)
    c: Coincident(g8,g9)
    c: Horizontal(g9)
    c: Vertical(g10)
    c: Coincident(g10,g11)
    c: Horizontal(g11)
    c: Coincident(g11,g12)
    c: Vertical(g12)
    c: Coincident(g12,g13)
    c: Horizontal(g13)
    c: Coincident(g13,g14)
    c: Coincident(g14,g15)
    c: Coincident(g15,g16)
    c: Coincident(g16,g17)
    c: Horizontal(g17)
    c: Coincident(g17,g18)
    c: Coincident(g18,g19)
    c: Coincident(g19,g20)
    c: Vertical(g20)
    c: Horizontal(g21)
    c: Coincident(g21,g22)
    c: Coincident(g22,g23)
    c: Horizontal(g23)
    c: Coincident(g23,g24)
    c: Coincident(g24,g25)
    c: Coincident(g25,g26)
    c: Coincident(g26,g27)
    c: Coincident(g27,g28)
    c: Vertical(g28)
    c: Coincident(g28,g29)
    c: Coincident(g29,g30)
    c: Coincident(g30,g31)
    c: Coincident(g32,g33)
    c: Coincident(g33,g34)
    c: Coincident(g34,g35)
    c: Coincident(g35,g36)
    c: Coincident(g36,g37)
    c: Coincident(g37,g38)
    c: Coincident(g38,g39)
    c: Coincident(g39,g40)
    c: Coincident(g40,g41)
    c: Coincident(g41,g42)
    c: Vertical(g42)
    c: Horizontal(g43)
    c: Coincident(g43,g44)
    c: Coincident(g44,g45)
    c: Horizontal(g45)
    c: Coincident(g45,g46)
    c: Coincident(g46,g47)
    c: Coincident(g4,g47)
    c: Tangent(g42,g48) = 1.5708
    c: Tangent(g43,g48) = 1.5708
    c: Tangent(g9,g49) = 1.5708
    c: Tangent(g10,g49) = 1.5708
    c: Tangent(g20,g50) = 1.5708
    c: Tangent(g21,g50) = 1.5708
    c: Tangent(g32,g51) = 1.5708
    c: Tangent(g31,g51) = 1.5708
    c: Horizontal(g41)
    c: Horizontal(g39)
    c: Horizontal(g19)
    c: Horizontal(g31)
    c: Horizontal(g35)
    c: Horizontal(g33)
    c: Vertical(g40)
    c: Vertical(g46)
    c: Vertical(g18)
    c: Vertical(g22)
    c: Vertical(g24)
    c: Vertical(g30)
    c: Vertical(g34)
    c: Vertical(g32)
    c: PointOnObject(g21,g2)
    c: PointOnObject(g32,g3)
    c: Vertical(g6)
    c: PointOnObject(g10,g1)
    c: Equal(g48,g49)
    c: Equal(g49,g50)
    c: Equal(g33,g41)
    c: Equal(g41,g30)
    c: Equal(g30,g22)
    c: Equal(g22,g19)
    c: Equal(g19,g11)
    c: Equal(g11,g8)
    c: Equal(g8,g44)
    c: Symmetric(g45,g6,g-2)
    c: DistanceX(g45,g6) = 9.4
    c: DistanceX(g43,g8) = 6.2
    c: Equal(g43,g42)
    c: Equal(g42,g32)
    c: DistanceY(g44,g44) = 1
    c: Equal(g31,g43)
    c: Equal(g43,g21)
    c: Equal(g21,g20)
    c: Equal(g20,g10)
    c: Radius(g49) = 1
    c: Symmetric(g37,g14,g-2)
    c: DistanceX(g37,g14) = 5.6
    c: Symmetric(g43,g8,g-2)
    c: Symmetric(g4,g26,g-1)
    c: DistanceY(g26,g4) = 5.6
    c: Symmetric(g4,g4,g-2)
    c: Equal(g45,g40)
    c: Equal(g45,g7)
    c: Equal(g7,g12)
    c: Equal(g12,g34)
    c: Equal(g34,g29)
    c: Equal(g29,g23)
    c: Equal(g23,g18)
    c: Equal(g39,g46)
    c: Equal(g46,g6)
    c: Equal(g6,g13)
    c: Equal(g13,g17)
    c: Equal(g17,g24)
    c: Equal(g24,g35)
    c: Equal(g35,g28)
    c: Parallel(g38,g47)
    c: Angle(g4,g47) = 2.35619
    c: Symmetric(g38,g35,g-1)
    c: Symmetric(g37,g36,g-1)
    c: Symmetric(g27,g46,g-1)
    c: Distance(g37,g4) = 1
    c: Symmetric(g27,g24,g-2)
    c: Symmetric(g26,g25,g-2)
    c: Symmetric(g36,g15,g-2)
FEATURE [Mesh::Feature] Toolhead_Right_Threaded_V6_x002
  Placement = pos=(18,-143,169.9) rot=(0.57735,0.57735,-0.57735;4.18879rad)
FEATURE [Part::Feature] Part__Feature014  label="30mm Fan Mockup 3010 v007"
  Placement = pos=(-15.5,-3.5,-6) rot=(0.707107,0,-0.707107;3.14159rad)
  shape: bbox 10 x 30 x 30 mm, 196 faces (baked)
FEATURE [Mesh::Feature] _a__Toolhead_Blower_Duct_Left_TV6_x002  label="[a]_Toolhead_Blower_Duct_Left_TV6_x002"
  Placement = pos=(2.4e-15,-3,-11) rot=(0.57735,0.57735,0.57735;2.0944rad)
FEATURE [App::Part] Part031
  Group = -> [Part__Feature014,_a__Toolhead_Blower_Duct_Left_TV6_x002]
  Origin = -> Origin069
  Placement = pos=(2.5,0,0) rot=(0,0,1;0rad)
FEATURE [Part::Feature] Part__Feature015  label="30mm Fan Mockup 3010 v008"
  Placement = pos=(19.5,-1.5,-7.5) rot=(0,1,0;1.5708rad)
  shape: bbox 10 x 30 x 30 mm, 196 faces (baked)
FEATURE [App::Part] Part030
  Group = -> [Part__Feature015,_a__Toolhead_Blower_Duct_Right_TV6_x002]
  Origin = -> Origin074
  Placement = pos=(-1.5,0,0) rot=(0,0,1;0rad)
FEATURE [App::Part] Part033  label="dummy-toolhead001"
  Group = -> [Toolhead_Left_Threaded_V6_x002,Toolhead_Right_Threaded_V6_x002,Part031,Part030]
  Origin = -> Origin073
  Placement = pos=(-77.8,96.3,121.1) rot=(0,0,1;0rad)
FEATURE [PartDesign::Pad] Pad035
  Length = 290
  Length2 = 100
  Midplane = true
  Placement = pos=(0,0,0) rot=(1,0,0;1.5708rad)
  Profile = -> Sketch038
  Refine = true
  Type = 0
FEATURE [PartDesign::Body] Body036  label="extrusion-014"
  Group = -> [Sketch038,Pad035]
  Origin = -> Origin068
  Placement = pos=(0,8.9,1.5) rot=(0,0,1;1.5708rad)
  Tip = -> Pad035
FEATURE [Mesh::Feature] XY_Joint_Left_Top_x002
  Placement = pos=(-131.3,123.2,24.2) rot=(-1,0,0;3.14159rad)
FEATURE [Mesh::Feature] XY_Joint_Left_Bottom_x002
  Placement = pos=(-131,123.3,-0.6) rot=(-1,0,0;3.14159rad)
FEATURE [App::Part] Part036  label="XY_Joint_Left001"
  Group = -> [XY_Joint_Left_Bottom_x002,XY_Joint_Left_Top_x002]
  Origin = -> Origin076
  Placement = pos=(-135.1,2.8,-5.4) rot=(0,0,1;0rad)
FEATURE [Sketcher::SketchObject] Sketch040
  MapMode = 5
  Support = -> [XY_Plane076]
  sketch-geometry (4):
    g0: LineSegment StartX=-66.5 StartY=66.5 StartZ=0 EndX=66.5 EndY=66.5 EndZ=0
    g1: LineSegment StartX=66.5 StartY=66.5 StartZ=0 EndX=66.5 EndY=-66.5 EndZ=0
    g2: LineSegment StartX=66.5 StartY=-66.5 StartZ=0 EndX=-66.5 EndY=-66.5 EndZ=0
    g3: LineSegment StartX=-66.5 StartY=-66.5 StartZ=0 EndX=-66.5 EndY=66.5 EndZ=0
  constraints (11):
    c: Coincident(g0,g1)
    c: Coincident(g1,g2)
    c: Coincident(g2,g3)
    c: Coincident(g3,g0)
    c: Horizontal(g0)
    c: Horizontal(g2)
    c: Vertical(g1)
    c: Vertical(g3)
    c: Symmetric(g0,g1,g-1)
    c: Equal(g0,g3)
    c: DistanceX(g0,g0) = 133
FEATURE [PartDesign::Pad] Pad038
  Length = 133
  Length2 = 100
  Midplane = true
  Profile = -> Sketch040
  Refine = true
  Type = 0
FEATURE [Sketcher::SketchObject] Sketch041
  ExternalGeometry = -> [Pad038]
  MapMode = 5
  Placement = pos=(0,0,66.5) rot=(0,0,1;0rad)
  Support = -> [Pad038]
  sketch-geometry (7):
    g0: LineSegment StartX=-88.5 StartY=88.5 StartZ=0 EndX=-66.5 EndY=88.5 EndZ=0
    g1: LineSegment [constr] StartX=-66.5 StartY=88.5 StartZ=0 EndX=-66.5 EndY=66.5 EndZ=0
    g2: LineSegment [constr] StartX=-66.5 StartY=66.5 StartZ=0 EndX=-88.5 EndY=66.5 EndZ=0
    g3: LineSegment StartX=-88.5 StartY=66.5 StartZ=0 EndX=-88.5 EndY=88.5 EndZ=0
    g4: ArcOfCircle CenterX=-66.5 CenterY=66.5 CenterZ=0 NormalX=0 NormalY=0 NormalZ=1 AngleXU=0 Radius=1 StartAngle=3.14159 EndAngle=7.85398
    g5: LineSegment StartX=-88.5 StartY=66.5 StartZ=0 EndX=-67.5 EndY=66.5 EndZ=0
    g6: LineSegment StartX=-66.5 StartY=88.5 StartZ=0 EndX=-66.5 EndY=67.5 EndZ=0
  constraints (19):
    c: Coincident(g0,g1)
    c: Coincident(g1,g2)
    c: Coincident(g2,g3)
    c: Coincident(g3,g0)
    c: Horizontal(g0)
    c: Horizontal(g2)
    c: Vertical(g1)
    c: Vertical(g3)
    c: Coincident(g1,g-4)
    c: Equal(g3,g0)
    c: DistanceX(g0,g0) = 22
    c: Coincident(g4,g1)
    c: PointOnObject(g4,g2)
    c: PointOnObject(g4,g1)
    c: Diameter(g4) = 2
    c: Coincident(g5,g4)
    c: Coincident(g5,g3)
    c: Coincident(g6,g4)
    c: Coincident(g6,g0)
FEATURE [PartDesign::Pad] Pad039
  BaseFeature = -> Pad038
  Length = 5
  Length2 = 100
  Profile = -> Sketch041
  Refine = true
  Type = 0
FEATURE [Sketcher::SketchObject] Sketch043
  ExternalGeometry = -> [Pad039]
  MapMode = 5
  Placement = pos=(0,0,71.5) rot=(0,0,1;0rad)
  Support = -> [Pad039]
  sketch-geometry (10):
    g0: LineSegment [constr] StartX=-117.5 StartY=112.5 StartZ=0 EndX=-37.5 EndY=112.5 EndZ=0
    g1: LineSegment [constr] StartX=-37.5 StartY=112.5 StartZ=0 EndX=-37.5 EndY=52.5 EndZ=0
    g2: LineSegment [constr] StartX=-37.5 StartY=52.5 StartZ=0 EndX=-117.5 EndY=52.5 EndZ=0
    g3: LineSegment [constr] StartX=-117.5 StartY=52.5 StartZ=0 EndX=-117.5 EndY=112.5 EndZ=0
    g4: LineSegment StartX=-117.5 StartY=112.5 StartZ=0 EndX=-37.5 EndY=112.5 EndZ=0
    g5: LineSegment StartX=-37.5 StartY=112.5 StartZ=0 EndX=-37.5 EndY=52.5 EndZ=0
    g6: LineSegment StartX=-37.5 StartY=52.5 StartZ=0 EndX=-117.5 EndY=52.5 EndZ=0
    g7: LineSegment StartX=-117.5 StartY=52.5 StartZ=0 EndX=-117.5 EndY=112.5 EndZ=0
    g8: GeomPoint X=-77.5 Y=77.5 Z=0
    g9: LineSegment [constr] StartX=-77.5 StartY=102.005 StartZ=0 EndX=-77.5 EndY=58.8093 EndZ=0
  constraints (24):
    c: Coincident(g0,g1)
    c: Coincident(g1,g2)
    c: Coincident(g2,g3)
    c: Coincident(g3,g0)
    c: Horizontal(g0)
    c: Horizontal(g2)
    c: Vertical(g1)
    c: Vertical(g3)
    c: DistanceX(g0,g0) = 80
    c: Coincident(g4,g5)
    c: Coincident(g6,g7)
    c: Coincident(g7,g4)
    c: Horizontal(g4)
    c: Vertical(g5)
    c: Vertical(g7)
    c: Coincident(g1,g5)
    c: Coincident(g0,g4)
    c: DistanceY(g7,g7) = 60
    c: Symmetric(g-3,g-4,g8)
    c: Vertical(g9)
    c: PointOnObject(g8,g9)
    c: Symmetric(g6,g6,g9)
    c: Coincident(g5,g6)
    c: DistanceY(g6,g8) = 25
FEATURE [PartDesign::Pad] Pad040
  BaseFeature = -> Pad039
  Length = 90
  Length2 = 100
  Profile = -> Sketch043
  Refine = true
  Type = 0
FEATURE [Part::Feature] Part__Feature166  label="cartridge heater001"
  Placement = pos=(3,7,-2e-15) rot=(0.545905,-0.635591,0.545905;2.00923rad)
  shape: bbox 6.634 x 6.634 x 22 mm, 6 faces (baked)
FEATURE [Part::Feature] Part__Feature167  label="E3D Nozzle001"
  Placement = pos=(-4,-3.5,0) rot=(0,1,0;1.66806rad)
  shape: bbox 8.411 x 12.5 x 9.194 mm, 21 faces (baked)
FEATURE [Part::Feature] Part__Feature168  label="E3D Heatsink_1.75 Bowden001"
  Placement = pos=(-4,39.15,0) rot=(0,1,0;0.165944rad)
  shape: bbox 25 x 50.1 x 25 mm, 90 faces (baked)
FEATURE [Part::Feature] Part__Feature169  label="E3D Heat Block001"
  shape: bbox 16 x 12 x 16 mm, 43 faces (baked)
FEATURE [Part::Feature] Part__Feature170  label="E3D Heatbreak001"
  Placement = pos=(-4,19.55,2e-15) rot=(-0.183494,0,0.983021;3.14159rad)
  shape: bbox 6 x 25.1 x 6 mm, 23 faces (baked)
FEATURE [App::Part] E3D001
  Group = -> [Part__Feature169,Part__Feature170,Part__Feature167,Part__Feature168,Part__Feature166]
  Origin = -> Origin134
  Placement = pos=(3.8,-15,3.3e-15) rot=(1,0,0;1.5708rad)
FEATURE [Part::Feature] Part__Feature173  label="SOLID012"
  shape: bbox 23.01 x 12.65 x 16.01 mm, 141 faces (baked)
FEATURE [Part::Feature] Part__Feature174  label="Bowden Clip 1,75 v007"
  Placement = pos=(11.5472,40.5,-15.4604) rot=(-1,0,0;1.5708rad)
  shape: bbox 7.75 x 2.1 x 8.132 mm, 16 faces (baked)
FEATURE [Part::Feature] Part__Feature175  label="Bowden Clip 1,75 v008"
  Placement = pos=(-8.4528,40.5,-15.4604) rot=(-1,0,0;1.5708rad)
  shape: bbox 7.75 x 2.1 x 8.132 mm, 16 faces (baked)
FEATURE [Part::Feature] Part__Feature176  label="Bowden Coupler 007"
  Placement = pos=(11.5472,42.5,-15.4604) rot=(1,0,0;1.5708rad)
  shape: bbox 6.917 x 6.567 x 6.917 mm, 87 faces, 5 solids (baked)
FEATURE [Part::Feature] Part__Feature177  label="Component3 (1)006"
  Placement = pos=(-1.5,0,1.3e-14) rot=(0,0,1;0rad)
  shape: bbox 1.5 x 15.06 x 7.059 mm, 5 faces (baked)
FEATURE [Part::Feature] Part__Feature178  label="E3D Cyclop-Chimera+ Air v007"
  Placement = pos=(17.5472,10.5,-9.46039) rot=(0,1,0;3.14159rad)
  shape: bbox 32.33 x 30.17 x 18.17 mm, 324 faces (baked)
FEATURE [Part::Feature] Part__Feature179  label="Nozzle006"
  shape: bbox 9.238 x 12 x 9.238 mm, 40 faces (baked)
FEATURE [Part::Feature] Part__Feature180  label="Bowden Coupler 008"
  Placement = pos=(-8.4528,42.5,-15.4604) rot=(1,0,0;1.5708rad)
  shape: bbox 6.917 x 6.567 x 6.917 mm, 87 faces, 5 solids (baked)
FEATURE [Part::Feature] Part__Feature181  label="m3x3mm Set Screw003"
  Placement = pos=(2.81273,0.292105,-11.147) rot=(0,0,1;0rad)
  shape: bbox 3.468 x 3.004 x 3.274 mm, 36 faces (baked)
FEATURE [Part::Feature] Part__Feature182  label="m3x10mm Hex Socket Cap (1)003"
  Placement = pos=(6.14822,-0.731826,-8.30035) rot=(0,0,1;0rad)
  shape: bbox 5.715 x 5.703 x 12.21 mm, 62 faces (baked)
FEATURE [Part::Feature] Part__Feature183  label="SOLID013"
  shape: bbox 23.01 x 12.65 x 16.01 mm, 141 faces (baked)
FEATURE [Part::Feature] Part__Feature184  label="SOLID014"
  shape: bbox 6 x 6 x 16.5 mm, 4 faces (baked)
FEATURE [Part::Feature] Part__Feature185  label="m3 set screw012"
  Placement = pos=(0,1e-16,0) rot=(0,0,1;0rad)
  shape: bbox 3.468 x 3.004 x 3.274 mm, 36 faces (baked)
FEATURE [Part::Feature] Part__Feature186  label="Cyclop Plus Heatbreak v008"
  Placement = pos=(11.5472,24,-15.4604) rot=(0.57735,0.57735,-0.57735;2.0944rad)
  shape: bbox 6.908 x 20.51 x 6.911 mm, 28 faces (baked)
FEATURE [App::Part] m3x3mm_Set_Screw_v004  label="m3x3mm Set Screw v004"
  Group = -> [Part__Feature181]
  Origin = -> Origin146
  Placement = pos=(-8.81273,-14.347,-0.292105) rot=(1,0,0;1.5708rad)
FEATURE [Part::Feature] Part__Feature187  label="Isolation006"
  Placement = pos=(1.5,-3.9e-15,0) rot=(0,0,1;0rad)
  shape: bbox 3 x 13.37 x 6.871 mm, 5 faces (baked)
FEATURE [App::Part] m3x10mm_Hex_Socket_Cap_v2__1_003  label="m3x10mm Hex Socket Cap v2 (1)003"
  Group = -> [Part__Feature182]
  Origin = -> Origin137
  Placement = pos=(6.35178,-15.9503,0.731826) rot=(1,0,0;1.5708rad)
FEATURE [Part::Feature] Part__Feature188  label="SOLID015"
  shape: bbox 6 x 6 x 16.5 mm, 4 faces (baked)
FEATURE [Part::Feature] Part__Feature189  label="Sensor Cartridge v1 (1)003"
  Placement = pos=(-6,-0.25,7.2) rot=(0,1,0;3.14159rad)
  shape: bbox 3 x 19.5 x 21.85 mm, 27 faces, 6 solids (baked)
FEATURE [Part::Feature] Part__Feature190  label="Component009"
  Placement = pos=(-1.5,1.1e-15,0) rot=(0,0,1;0rad)
  shape: bbox 1.5 x 15.06 x 7.059 mm, 5 faces (baked)
FEATURE [Part::Feature] Part__Feature191  label="Nozzle007"
  shape: bbox 9.238 x 12 x 9.238 mm, 40 faces (baked)
FEATURE [App::Part] Nozzle_v2006  label="Nozzle v008"
  Group = -> [Part__Feature191]
  Origin = -> Origin143
  Placement = pos=(-7.8e-15,-5.65,2.89e-14) rot=(0,1,0;1.5708rad)
FEATURE [Part::Feature] Part__Feature192  label="Cyclop Plus Heatbreak v009"
  Placement = pos=(-8.4528,24,-15.4604) rot=(0.57735,0.57735,-0.57735;2.0944rad)
  shape: bbox 6.908 x 20.51 x 6.911 mm, 28 faces (baked)
FEATURE [Part::Feature] Part__Feature193  label="Brass Coupler Insert v007"
  Placement = pos=(11.5472,38.5,-15.4604) rot=(-1,0,0;1.5708rad)
  shape: bbox 10.34 x 2.336 x 10.3 mm, 13 faces (baked)
FEATURE [App::Part] _mm_grub_v1__2_003  label="3mm grub v1 (2)003"
  Group = -> [Part__Feature185]
  Origin = -> Origin142
  Placement = pos=(16.2972,21.5,-15.4604) rot=(-0.57735,0.57735,-0.57735;2.0944rad)
FEATURE [Part::Feature] Part__Feature194  label="m3 set screw013"
  shape: bbox 3.468 x 3.004 x 3.274 mm, 36 faces (baked)
FEATURE [App::Part] _mm_grub_v1__3_003  label="3mm grub v1 (3)003"
  Group = -> [Part__Feature194]
  Origin = -> Origin138
  Placement = pos=(16.2972,13.5,-15.4604) rot=(-0.57735,0.57735,-0.57735;2.0944rad)
FEATURE [Part::Feature] Part__Feature195  label="m3 set screw014"
  Placement = pos=(0,1e-16,0) rot=(0,0,1;0rad)
  shape: bbox 3.468 x 3.004 x 3.274 mm, 36 faces (baked)
FEATURE [App::Part] _mm_grub_v1__4_003  label="3mm grub v1 (4)003"
  Group = -> [Part__Feature195]
  Origin = -> Origin150
  Placement = pos=(-13.2028,21.5,-15.4604) rot=(0.57735,0.57735,-0.57735;4.18879rad)
FEATURE [Part::Feature] Part__Feature196  label="Isolation (1)006"
  Placement = pos=(1.5,-4e-15,-1.8e-14) rot=(0,0,1;0rad)
  shape: bbox 3 x 13.37 x 6.871 mm, 5 faces (baked)
FEATURE [Part::Feature] Part__Feature197  label="Brass Coupler Insert v008"
  Placement = pos=(-8.4528,38.5,-15.4604) rot=(-1,0,0;1.5708rad)
  shape: bbox 10.34 x 2.336 x 10.3 mm, 13 faces (baked)
FEATURE [Part::Feature] Part__Feature198  label="Sensor Cartridge v004"
  Placement = pos=(-6,-0.25,-7.2) rot=(0,0,1;0rad)
  shape: bbox 3 x 19.5 x 21.85 mm, 27 faces, 6 solids (baked)
FEATURE [Part::Feature] Part__Feature199  label="Component3 (1)007"
  Placement = pos=(1.5,-4e-15,-1.8e-14) rot=(0,0,1;0rad)
  shape: bbox 1.5 x 15.06 x 7.059 mm, 5 faces (baked)
FEATURE [Part::Feature] Part__Feature200  label="m3x3mm Set Screw (1)003"
  Placement = pos=(2.81273,0.292105,-11.147) rot=(0,0,1;0rad)
  shape: bbox 3.468 x 3.004 x 3.274 mm, 36 faces (baked)
FEATURE [Part::Feature] Part__Feature201  label="Wire (1)006"
  Placement = pos=(1.5,-4e-15,-1.8e-14) rot=(0,0,1;0rad)
  shape: bbox 0.75 x 18.65 x 6.653 mm, 5 faces (baked)
FEATURE [Part::Feature] Part__Feature202  label="Wire006"
  Placement = pos=(1.5,-3.9e-15,0) rot=(0,0,1;0rad)
  shape: bbox 0.75 x 18.65 x 6.653 mm, 5 faces (baked)
FEATURE [App::Part] Nozzle_v2007  label="Nozzle v009"
  Group = -> [Part__Feature179]
  Origin = -> Origin140
  Placement = pos=(-1.06e-13,-5.65,4.44e-14) rot=(0,1,0;1.5708rad)
FEATURE [Part::Feature] Part__Feature203  label="m3 set screw015"
  shape: bbox 3.468 x 3.004 x 3.274 mm, 36 faces (baked)
FEATURE [App::Part] _mm_grub_v1__5_003  label="3mm grub v1 (5)003"
  Group = -> [Part__Feature203]
  Origin = -> Origin149
  Placement = pos=(-13.2028,13.5,-15.4604) rot=(0.57735,0.57735,-0.57735;4.18879rad)
FEATURE [Part::Feature] Part__Feature204  label="m3x10mm Hex Socket Cap003"
  Placement = pos=(6.14822,-0.731826,-8.30035) rot=(0,0,1;0rad)
  shape: bbox 5.715 x 5.703 x 12.21 mm, 62 faces (baked)
FEATURE [App::Part] m3x10mm_Hex_Socket_Cap_v005  label="m3x10mm Hex Socket Cap v005"
  Group = -> [Part__Feature204]
  Origin = -> Origin145
  Placement = pos=(6.35178,-15.9503,0.731826) rot=(1,0,0;1.5708rad)
FEATURE [Part::Feature] Part__Feature205  label="Isolation (1)007"
  Placement = pos=(-1.5,0,1.3e-14) rot=(0,0,1;0rad)
  shape: bbox 3 x 13.37 x 6.871 mm, 5 faces (baked)
FEATURE [Part::Feature] Part__Feature206  label="Wire (1)007"
  Placement = pos=(-1.5,0,1.3e-14) rot=(0,0,1;0rad)
  shape: bbox 0.75 x 18.65 x 6.653 mm, 5 faces (baked)
FEATURE [App::Part] Heater_Cartridge_v2__1_003  label="Heater Cartridge v2 (1)003"
  Group = -> [Part__Feature206,Part__Feature205,Part__Feature177,Part__Feature199,Part__Feature196,Part__Feature201,Part__Feature188]
  Origin = -> Origin136
  Placement = pos=(6.5,-2,-8.5) rot=(0,0,1;0rad)
FEATURE [App::Part] Heat_Block003  label="Heat Block003"
  Group = -> [Part__Feature180,Part__Feature175,Part__Feature193,_mm_grub_v1__5_003,_mm_grub_v1__4_003,_mm_grub_v1__3_003,_mm_grub_v1__2_003,Part__Feature178,Part__Feature192,Part__Feature176,Part__Feature174,Part__Feature197,Part__Feature186]
  Origin = -> Origin135
  Placement = pos=(1.5472,-40.5,-18.4604) rot=(0,1,0;3.14159rad)
FEATURE [Part::Feature] Part__Feature207  label="Isolation007"
  Placement = pos=(-1.5,1.1e-15,0) rot=(0,0,1;0rad)
  shape: bbox 3 x 13.37 x 6.871 mm, 5 faces (baked)
FEATURE [Part::Feature] Part__Feature208  label="Component010"
  Placement = pos=(1.5,-3.9e-15,0) rot=(0,0,1;0rad)
  shape: bbox 1.5 x 15.06 x 7.059 mm, 5 faces (baked)
FEATURE [Part::Feature] Part__Feature209  label="Wire007"
  Placement = pos=(-1.5,1.1e-15,0) rot=(0,0,1;0rad)
  shape: bbox 0.75 x 18.65 x 6.653 mm, 5 faces (baked)
FEATURE [App::Part] Heater_Cartridge_v005  label="Heater Cartridge v005"
  Group = -> [Part__Feature209,Part__Feature207,Part__Feature190,Part__Feature208,Part__Feature187,Part__Feature202,Part__Feature184]
  Origin = -> Origin141
  Placement = pos=(6.5,-2,8.5) rot=(0,1,0;3.14159rad)
FEATURE [App::Part] V6_Heat_Block_Left003  label="V6 Heat Block Left003"
  Group = -> [m3x10mm_Hex_Socket_Cap_v005,m3x3mm_Set_Screw_v004,Part__Feature198,Heater_Cartridge_v005,Nozzle_v2006,Part__Feature173]
  Origin = -> Origin147
  Placement = pos=(-10,-37.35,-3) rot=(0,-1,0;1.5708rad)
FEATURE [App::Part] m3x3mm_Set_Screw_v1__1_003  label="m3x3mm Set Screw v1 (1)003"
  Group = -> [Part__Feature200]
  Origin = -> Origin139
  Placement = pos=(-8.81273,-14.347,-0.292105) rot=(1,0,0;1.5708rad)
FEATURE [App::Part] V6_Heat_Block_Right003  label="V6 Heat Block Right003"
  Group = -> [m3x10mm_Hex_Socket_Cap_v2__1_003,m3x3mm_Set_Screw_v1__1_003,Part__Feature189,Heater_Cartridge_v2__1_003,Nozzle_v2007,Part__Feature183]
  Origin = -> Origin148
  Placement = pos=(10,-37.35,-3) rot=(0,-1,0;1.5708rad)
FEATURE [App::Part] Chimera__Assembly_MK1_v006  label="Chimera+ Assembly MK1 v006"
  Group = -> [Heat_Block003,V6_Heat_Block_Left003,V6_Heat_Block_Right003]
  Origin = -> Origin144
  Placement = pos=(0,0,0) rot=(1,0,0;1.5708rad)
FEATURE [Part::Feature] Part__Feature210  label="m3 set screw016"
  shape: bbox 3.468 x 3.004 x 3.274 mm, 36 faces (baked)
FEATURE [Part::Feature] Part__Feature211  label="m3x10mm Hex Socket Cap (1)004"
  Placement = pos=(6.14822,-0.731826,-8.30035) rot=(0,0,1;0rad)
  shape: bbox 5.715 x 5.703 x 12.21 mm, 62 faces (baked)
FEATURE [Part::Feature] Part__Feature212  label="Cyclop Plus Heatbreak v010"
  Placement = pos=(11.5472,24,-15.4604) rot=(0.57735,0.57735,-0.57735;2.0944rad)
  shape: bbox 6.908 x 20.51 x 6.911 mm, 28 faces (baked)
FEATURE [Part::Feature] Part__Feature213  label="Brass Coupler Insert v009"
  Placement = pos=(11.5472,38.5,-15.4604) rot=(-1,0,0;1.5708rad)
  shape: bbox 10.34 x 2.336 x 10.3 mm, 13 faces (baked)
FEATURE [Part::Feature] Part__Feature214  label="Wire008"
  Placement = pos=(-1.5,1.1e-15,0) rot=(0,0,1;0rad)
  shape: bbox 0.75 x 18.65 x 6.653 mm, 5 faces (baked)
FEATURE [Part::Feature] Part__Feature215  label="Component011"
  Placement = pos=(-1.5,1.1e-15,0) rot=(0,0,1;0rad)
  shape: bbox 1.5 x 15.06 x 7.059 mm, 5 faces (baked)
FEATURE [App::Part] m3x10mm_Hex_Socket_Cap_v2__1_004  label="m3x10mm Hex Socket Cap v2 (1)004"
  Group = -> [Part__Feature211]
  Origin = -> Origin171
  Placement = pos=(6.35178,-15.9503,0.731826) rot=(1,0,0;1.5708rad)
FEATURE [Part::Feature] Part__Feature216  label="Wire (1)008"
  Placement = pos=(-1.5,0,1.3e-14) rot=(0,0,1;0rad)
  shape: bbox 0.75 x 18.65 x 6.653 mm, 5 faces (baked)
FEATURE [Part::Feature] Part__Feature217  label="Isolation008"
  Placement = pos=(-1.5,1.1e-15,0) rot=(0,0,1;0rad)
  shape: bbox 3 x 13.37 x 6.871 mm, 5 faces (baked)
FEATURE [Part::Feature] Part__Feature218  label="SOLID016"
  shape: bbox 23.01 x 12.65 x 16.01 mm, 141 faces (baked)
FEATURE [Part::Feature] Part__Feature219  label="SOLID017"
  shape: bbox 23.01 x 12.65 x 16.01 mm, 141 faces (baked)
FEATURE [Part::Feature] Part__Feature220  label="Bowden Coupler 009"
  Placement = pos=(11.5472,42.5,-15.4604) rot=(1,0,0;1.5708rad)
  shape: bbox 6.917 x 6.567 x 6.917 mm, 87 faces, 5 solids (baked)
FEATURE [Part::Feature] Part__Feature221  label="m3x3mm Set Screw004"
  Placement = pos=(2.81273,0.292105,-11.147) rot=(0,0,1;0rad)
  shape: bbox 3.468 x 3.004 x 3.274 mm, 36 faces (baked)
FEATURE [Part::Feature] Part__Feature222  label="Sensor Cartridge v005"
  Placement = pos=(-6,-0.25,-7.2) rot=(0,0,1;0rad)
  shape: bbox 3 x 19.5 x 21.85 mm, 27 faces, 6 solids (baked)
FEATURE [Part::Feature] Part__Feature223  label="Component012"
  Placement = pos=(1.5,-3.9e-15,0) rot=(0,0,1;0rad)
  shape: bbox 1.5 x 15.06 x 7.059 mm, 5 faces (baked)
FEATURE [Part::Feature] Part__Feature224  label="Cyclop Plus Heatbreak v011"
  Placement = pos=(-8.4528,24,-15.4604) rot=(0.57735,0.57735,-0.57735;2.0944rad)
  shape: bbox 6.908 x 20.51 x 6.911 mm, 28 faces (baked)
FEATURE [Part::Feature] Part__Feature225  label="Bowden Clip 1,75 v009"
  Placement = pos=(11.5472,40.5,-15.4604) rot=(-1,0,0;1.5708rad)
  shape: bbox 7.75 x 2.1 x 8.132 mm, 16 faces (baked)
FEATURE [Part::Feature] Part__Feature226  label="Component3 (1)008"
  Placement = pos=(1.5,-4e-15,-1.8e-14) rot=(0,0,1;0rad)
  shape: bbox 1.5 x 15.06 x 7.059 mm, 5 faces (baked)
FEATURE [Part::Feature] Part__Feature227  label="Wire (1)009"
  Placement = pos=(1.5,-4e-15,-1.8e-14) rot=(0,0,1;0rad)
  shape: bbox 0.75 x 18.65 x 6.653 mm, 5 faces (baked)
FEATURE [App::Part] m3x3mm_Set_Screw_v005  label="m3x3mm Set Screw v005"
  Group = -> [Part__Feature221]
  Origin = -> Origin160
  Placement = pos=(-8.81273,-14.347,-0.292105) rot=(1,0,0;1.5708rad)
FEATURE [Part::Feature] Part__Feature228  label="E3D Cyclop-Chimera+ Air v008"
  Placement = pos=(17.5472,10.5,-9.46039) rot=(0,1,0;3.14159rad)
  shape: bbox 32.33 x 30.17 x 18.17 mm, 324 faces (baked)
FEATURE [Part::Feature] Part__Feature229  label="SOLID018"
  shape: bbox 23.01 x 12.65 x 16.01 mm, 141 faces (baked)
FEATURE [Part::Feature] Part__Feature230  label="Bowden Clip 1,75 v010"
  Placement = pos=(11.5472,40.5,-15.4604) rot=(-1,0,0;1.5708rad)
  shape: bbox 7.75 x 2.1 x 8.132 mm, 16 faces (baked)
FEATURE [Part::Feature] Part__Feature231  label="Isolation (1)008"
  Placement = pos=(-1.5,0,1.3e-14) rot=(0,0,1;0rad)
  shape: bbox 3 x 13.37 x 6.871 mm, 5 faces (baked)
FEATURE [Part::Feature] Part__Feature232  label="Sensor Cartridge v1 (1)004"
  Placement = pos=(-6,-0.25,7.2) rot=(0,1,0;3.14159rad)
  shape: bbox 3 x 19.5 x 21.85 mm, 27 faces, 6 solids (baked)
FEATURE [Part::Feature] Part__Feature233  label="m3x3mm Set Screw (1)004"
  Placement = pos=(2.81273,0.292105,-11.147) rot=(0,0,1;0rad)
  shape: bbox 3.468 x 3.004 x 3.274 mm, 36 faces (baked)
FEATURE [App::Part] m3x3mm_Set_Screw_v1__1_004  label="m3x3mm Set Screw v1 (1)004"
  Group = -> [Part__Feature233]
  Origin = -> Origin165
  Placement = pos=(-8.81273,-14.347,-0.292105) rot=(1,0,0;1.5708rad)
FEATURE [Part::Feature] Part__Feature234  label="Bowden Clip 1,75 v011"
  Placement = pos=(-8.4528,40.5,-15.4604) rot=(-1,0,0;1.5708rad)
  shape: bbox 7.75 x 2.1 x 8.132 mm, 16 faces (baked)
FEATURE [Part::Feature] Part__Feature235  label="Isolation009"
  Placement = pos=(1.5,-3.9e-15,0) rot=(0,0,1;0rad)
  shape: bbox 3 x 13.37 x 6.871 mm, 5 faces (baked)
FEATURE [Part::Feature] Part__Feature236  label="Bowden Coupler 010"
  Placement = pos=(-8.4528,42.5,-15.4604) rot=(1,0,0;1.5708rad)
  shape: bbox 6.917 x 6.567 x 6.917 mm, 87 faces, 5 solids (baked)
FEATURE [Part::Feature] Part__Feature237  label="Nozzle008"
  shape: bbox 9.238 x 12 x 9.238 mm, 40 faces (baked)
FEATURE [App::Part] Nozzle_v2009  label="Nozzle v011"
  Group = -> [Part__Feature237]
  Origin = -> Origin177
  Placement = pos=(-1.06e-13,-5.65,4.44e-14) rot=(0,1,0;1.5708rad)
FEATURE [Part::Feature] Part__Feature238  label="Bowden Clip 1,75 v012"
  Placement = pos=(-8.4528,40.5,-15.4604) rot=(-1,0,0;1.5708rad)
  shape: bbox 7.75 x 2.1 x 8.132 mm, 16 faces (baked)
FEATURE [Part::Feature] Part__Feature239  label="m3 set screw017"
  Placement = pos=(0,1e-16,0) rot=(0,0,1;0rad)
  shape: bbox 3.468 x 3.004 x 3.274 mm, 36 faces (baked)
FEATURE [Part::Feature] Part__Feature240  label="Isolation (1)009"
  Placement = pos=(1.5,-4e-15,-1.8e-14) rot=(0,0,1;0rad)
  shape: bbox 3 x 13.37 x 6.871 mm, 5 faces (baked)
FEATURE [Part::Feature] Part__Feature241  label="Bowden Coupler 011"
  Placement = pos=(11.5472,42.5,-15.4604) rot=(1,0,0;1.5708rad)
  shape: bbox 6.917 x 6.567 x 6.917 mm, 87 faces, 5 solids (baked)
FEATURE [Part::Feature] Part__Feature242  label="Component3 (1)009"
  Placement = pos=(-1.5,0,1.3e-14) rot=(0,0,1;0rad)
  shape: bbox 1.5 x 15.06 x 7.059 mm, 5 faces (baked)
FEATURE [Part::Feature] Part__Feature243  label="E3D Cyclop-Chimera+ Air v009"
  Placement = pos=(17.5472,10.5,-9.46039) rot=(0,1,0;3.14159rad)
  shape: bbox 32.33 x 30.17 x 18.17 mm, 324 faces (baked)
FEATURE [Part::Feature] Part__Feature244  label="Nozzle009"
  shape: bbox 9.238 x 12 x 9.238 mm, 40 faces (baked)
FEATURE [Part::Feature] Part__Feature245  label="Bowden Coupler 012"
  Placement = pos=(-8.4528,42.5,-15.4604) rot=(1,0,0;1.5708rad)
  shape: bbox 6.917 x 6.567 x 6.917 mm, 87 faces, 5 solids (baked)
FEATURE [Part::Feature] Part__Feature246  label="m3x3mm Set Screw005"
  Placement = pos=(2.81273,0.292105,-11.147) rot=(0,0,1;0rad)
  shape: bbox 3.468 x 3.004 x 3.274 mm, 36 faces (baked)
FEATURE [Part::Feature] Part__Feature247  label="m3x10mm Hex Socket Cap (1)005"
  Placement = pos=(6.14822,-0.731826,-8.30035) rot=(0,0,1;0rad)
  shape: bbox 5.715 x 5.703 x 12.21 mm, 62 faces (baked)
FEATURE [Part::Feature] Part__Feature248  label="SOLID019"
  shape: bbox 23.01 x 12.65 x 16.01 mm, 141 faces (baked)
FEATURE [Part::Feature] Part__Feature249  label="SOLID020"
  shape: bbox 6 x 6 x 16.5 mm, 4 faces (baked)
FEATURE [Part::Feature] Part__Feature250  label="m3 set screw018"
  Placement = pos=(0,1e-16,0) rot=(0,0,1;0rad)
  shape: bbox 3.468 x 3.004 x 3.274 mm, 36 faces (baked)
FEATURE [Part::Feature] Part__Feature251  label="Cyclop Plus Heatbreak v012"
  Placement = pos=(11.5472,24,-15.4604) rot=(0.57735,0.57735,-0.57735;2.0944rad)
  shape: bbox 6.908 x 20.51 x 6.911 mm, 28 faces (baked)
FEATURE [App::Part] m3x3mm_Set_Screw_v006  label="m3x3mm Set Screw v006"
  Group = -> [Part__Feature246]
  Origin = -> Origin179
  Placement = pos=(-8.81273,-14.347,-0.292105) rot=(1,0,0;1.5708rad)
FEATURE [Part::Feature] Part__Feature252  label="Isolation010"
  Placement = pos=(1.5,-3.9e-15,0) rot=(0,0,1;0rad)
  shape: bbox 3 x 13.37 x 6.871 mm, 5 faces (baked)
FEATURE [App::Part] m3x10mm_Hex_Socket_Cap_v2__1_005  label="m3x10mm Hex Socket Cap v2 (1)005"
  Group = -> [Part__Feature247]
  Origin = -> Origin167
  Placement = pos=(6.35178,-15.9503,0.731826) rot=(1,0,0;1.5708rad)
FEATURE [Part::Feature] Part__Feature253  label="m3x10mm Hex Socket Cap004"
  Placement = pos=(6.14822,-0.731826,-8.30035) rot=(0,0,1;0rad)
  shape: bbox 5.715 x 5.703 x 12.21 mm, 62 faces (baked)
FEATURE [App::Part] m3x10mm_Hex_Socket_Cap_v006  label="m3x10mm Hex Socket Cap v006"
  Group = -> [Part__Feature253]
  Origin = -> Origin161
  Placement = pos=(6.35178,-15.9503,0.731826) rot=(1,0,0;1.5708rad)
FEATURE [Part::Feature] Part__Feature254  label="SOLID021"
  shape: bbox 6 x 6 x 16.5 mm, 4 faces (baked)
FEATURE [Part::Feature] Part__Feature255  label="Brass Coupler Insert v010"
  Placement = pos=(-8.4528,38.5,-15.4604) rot=(-1,0,0;1.5708rad)
  shape: bbox 10.34 x 2.336 x 10.3 mm, 13 faces (baked)
FEATURE [Part::Feature] Part__Feature256  label="Sensor Cartridge v1 (1)005"
  Placement = pos=(-6,-0.25,7.2) rot=(0,1,0;3.14159rad)
  shape: bbox 3 x 19.5 x 21.85 mm, 27 faces, 6 solids (baked)
FEATURE [Part::Feature] Part__Feature257  label="Component013"
  Placement = pos=(-1.5,1.1e-15,0) rot=(0,0,1;0rad)
  shape: bbox 1.5 x 15.06 x 7.059 mm, 5 faces (baked)
FEATURE [Part::Feature] Part__Feature258  label="Nozzle010"
  shape: bbox 9.238 x 12 x 9.238 mm, 40 faces (baked)
FEATURE [App::Part] Nozzle_v2010  label="Nozzle v012"
  Group = -> [Part__Feature258]
  Origin = -> Origin174
  Placement = pos=(-7.8e-15,-5.65,2.89e-14) rot=(0,1,0;1.5708rad)
FEATURE [Part::Feature] Part__Feature259  label="Cyclop Plus Heatbreak v013"
  Placement = pos=(-8.4528,24,-15.4604) rot=(0.57735,0.57735,-0.57735;2.0944rad)
  shape: bbox 6.908 x 20.51 x 6.911 mm, 28 faces (baked)
FEATURE [Part::Feature] Part__Feature260  label="Brass Coupler Insert v011"
  Placement = pos=(11.5472,38.5,-15.4604) rot=(-1,0,0;1.5708rad)
  shape: bbox 10.34 x 2.336 x 10.3 mm, 13 faces (baked)
FEATURE [App::Part] _mm_grub_v1__3_005  label="3mm grub v1 (3)005"
  Group = -> [Part__Feature210]
  Origin = -> Origin152
  Placement = pos=(16.2972,13.5,-15.4604) rot=(-0.57735,0.57735,-0.57735;2.0944rad)
FEATURE [Part::Feature] Part__Feature261  label="SOLID022"
  shape: bbox 6 x 6 x 16.5 mm, 4 faces (baked)
FEATURE [Part::Feature] Part__Feature262  label="Component3 (1)010"
  Placement = pos=(-1.5,0,1.3e-14) rot=(0,0,1;0rad)
  shape: bbox 1.5 x 15.06 x 7.059 mm, 5 faces (baked)
FEATURE [App::Part] _mm_grub_v1__2_005  label="3mm grub v1 (2)005"
  Group = -> [Part__Feature250]
  Origin = -> Origin173
  Placement = pos=(16.2972,21.5,-15.4604) rot=(-0.57735,0.57735,-0.57735;2.0944rad)
FEATURE [App::Part] _mm_grub_v1__4_005  label="3mm grub v1 (4)005"
  Group = -> [Part__Feature239]
  Origin = -> Origin154
  Placement = pos=(-13.2028,21.5,-15.4604) rot=(0.57735,0.57735,-0.57735;4.18879rad)
FEATURE [Part::Feature] Part__Feature263  label="m3 set screw019"
  shape: bbox 3.468 x 3.004 x 3.274 mm, 36 faces (baked)
FEATURE [App::Part] _mm_grub_v1__3_004  label="3mm grub v1 (3)004"
  Group = -> [Part__Feature263]
  Origin = -> Origin168
  Placement = pos=(16.2972,13.5,-15.4604) rot=(-0.57735,0.57735,-0.57735;2.0944rad)
FEATURE [Part::Feature] Part__Feature264  label="m3 set screw020"
  Placement = pos=(0,1e-16,0) rot=(0,0,1;0rad)
  shape: bbox 3.468 x 3.004 x 3.274 mm, 36 faces (baked)
FEATURE [App::Part] _mm_grub_v1__4_004  label="3mm grub v1 (4)004"
  Group = -> [Part__Feature264]
  Origin = -> Origin183
  Placement = pos=(-13.2028,21.5,-15.4604) rot=(0.57735,0.57735,-0.57735;4.18879rad)
FEATURE [Part::Feature] Part__Feature265  label="Isolation (1)010"
  Placement = pos=(1.5,-4e-15,-1.8e-14) rot=(0,0,1;0rad)
  shape: bbox 3 x 13.37 x 6.871 mm, 5 faces (baked)
FEATURE [Part::Feature] Part__Feature266  label="m3 set screw021"
  Placement = pos=(0,1e-16,0) rot=(0,0,1;0rad)
  shape: bbox 3.468 x 3.004 x 3.274 mm, 36 faces (baked)
FEATURE [App::Part] _mm_grub_v1__2_004  label="3mm grub v1 (2)004"
  Group = -> [Part__Feature266]
  Origin = -> Origin153
  Placement = pos=(16.2972,21.5,-15.4604) rot=(-0.57735,0.57735,-0.57735;2.0944rad)
FEATURE [Part::Feature] Part__Feature267  label="Brass Coupler Insert v012"
  Placement = pos=(-8.4528,38.5,-15.4604) rot=(-1,0,0;1.5708rad)
  shape: bbox 10.34 x 2.336 x 10.3 mm, 13 faces (baked)
FEATURE [Part::Feature] Part__Feature268  label="Wire009"
  Placement = pos=(1.5,-3.9e-15,0) rot=(0,0,1;0rad)
  shape: bbox 0.75 x 18.65 x 6.653 mm, 5 faces (baked)
FEATURE [App::Part] Heater_Cartridge_v006  label="Heater Cartridge v006"
  Group = -> [Part__Feature214,Part__Feature217,Part__Feature215,Part__Feature223,Part__Feature235,Part__Feature268,Part__Feature261]
  Origin = -> Origin159
  Placement = pos=(6.5,-2,8.5) rot=(0,1,0;3.14159rad)
FEATURE [Part::Feature] Part__Feature269  label="Sensor Cartridge v006"
  Placement = pos=(-6,-0.25,-7.2) rot=(0,0,1;0rad)
  shape: bbox 3 x 19.5 x 21.85 mm, 27 faces, 6 solids (baked)
FEATURE [Part::Feature] Part__Feature270  label="Component3 (1)011"
  Placement = pos=(1.5,-4e-15,-1.8e-14) rot=(0,0,1;0rad)
  shape: bbox 1.5 x 15.06 x 7.059 mm, 5 faces (baked)
FEATURE [Part::Feature] Part__Feature271  label="m3x3mm Set Screw (1)005"
  Placement = pos=(2.81273,0.292105,-11.147) rot=(0,0,1;0rad)
  shape: bbox 3.468 x 3.004 x 3.274 mm, 36 faces (baked)
FEATURE [Part::Feature] Part__Feature272  label="Wire (1)010"
  Placement = pos=(1.5,-4e-15,-1.8e-14) rot=(0,0,1;0rad)
  shape: bbox 0.75 x 18.65 x 6.653 mm, 5 faces (baked)
FEATURE [Part::Feature] Part__Feature273  label="Wire010"
  Placement = pos=(1.5,-3.9e-15,0) rot=(0,0,1;0rad)
  shape: bbox 0.75 x 18.65 x 6.653 mm, 5 faces (baked)
FEATURE [Part::Feature] Part__Feature274  label="Nozzle011"
  shape: bbox 9.238 x 12 x 9.238 mm, 40 faces (baked)
FEATURE [App::Part] Nozzle_v2008  label="Nozzle v010"
  Group = -> [Part__Feature274]
  Origin = -> Origin155
  Placement = pos=(-7.8e-15,-5.65,2.89e-14) rot=(0,1,0;1.5708rad)
FEATURE [App::Part] V6_Heat_Block_Left004  label="V6 Heat Block Left004"
  Group = -> [m3x10mm_Hex_Socket_Cap_v006,m3x3mm_Set_Screw_v005,Part__Feature222,Heater_Cartridge_v006,Nozzle_v2008,Part__Feature229]
  Origin = -> Origin156
  Placement = pos=(-10,-37.35,-3) rot=(0,-1,0;1.5708rad)
FEATURE [App::Part] Nozzle_v2011  label="Nozzle v013"
  Group = -> [Part__Feature244]
  Origin = -> Origin170
  Placement = pos=(-1.06e-13,-5.65,4.44e-14) rot=(0,1,0;1.5708rad)
FEATURE [Part::Feature] Part__Feature275  label="m3 set screw022"
  shape: bbox 3.468 x 3.004 x 3.274 mm, 36 faces (baked)
FEATURE [App::Part] _mm_grub_v1__5_005  label="3mm grub v1 (5)005"
  Group = -> [Part__Feature275]
  Origin = -> Origin182
  Placement = pos=(-13.2028,13.5,-15.4604) rot=(0.57735,0.57735,-0.57735;4.18879rad)
FEATURE [Part::Feature] Part__Feature276  label="m3x10mm Hex Socket Cap005"
  Placement = pos=(6.14822,-0.731826,-8.30035) rot=(0,0,1;0rad)
  shape: bbox 5.715 x 5.703 x 12.21 mm, 62 faces (baked)
FEATURE [App::Part] m3x10mm_Hex_Socket_Cap_v007  label="m3x10mm Hex Socket Cap v007"
  Group = -> [Part__Feature276]
  Origin = -> Origin178
  Placement = pos=(6.35178,-15.9503,0.731826) rot=(1,0,0;1.5708rad)
FEATURE [Part::Feature] Part__Feature277  label="Isolation (1)011"
  Placement = pos=(-1.5,0,1.3e-14) rot=(0,0,1;0rad)
  shape: bbox 3 x 13.37 x 6.871 mm, 5 faces (baked)
FEATURE [Part::Feature] Part__Feature278  label="Wire (1)011"
  Placement = pos=(-1.5,0,1.3e-14) rot=(0,0,1;0rad)
  shape: bbox 0.75 x 18.65 x 6.653 mm, 5 faces (baked)
FEATURE [App::Part] Heater_Cartridge_v2__1_005  label="Heater Cartridge v2 (1)005"
  Group = -> [Part__Feature278,Part__Feature277,Part__Feature242,Part__Feature270,Part__Feature265,Part__Feature272,Part__Feature254]
  Origin = -> Origin166
  Placement = pos=(6.5,-2,-8.5) rot=(0,0,1;0rad)
FEATURE [App::Part] Heat_Block005  label="Heat Block005"
  Group = -> [Part__Feature245,Part__Feature238,Part__Feature260,_mm_grub_v1__5_005,_mm_grub_v1__4_004,_mm_grub_v1__3_004,_mm_grub_v1__2_005,Part__Feature243,Part__Feature259,Part__Feature241,Part__Feature225,Part__Feature267,Part__Feature251]
  Origin = -> Origin164
  Placement = pos=(1.5472,-40.5,-18.4604) rot=(0,1,0;3.14159rad)
FEATURE [Part::Feature] Part__Feature279  label="Isolation011"
  Placement = pos=(-1.5,1.1e-15,0) rot=(0,0,1;0rad)
  shape: bbox 3 x 13.37 x 6.871 mm, 5 faces (baked)
FEATURE [Part::Feature] Part__Feature280  label="Component014"
  Placement = pos=(1.5,-3.9e-15,0) rot=(0,0,1;0rad)
  shape: bbox 1.5 x 15.06 x 7.059 mm, 5 faces (baked)
FEATURE [Part::Feature] Part__Feature281  label="Wire011"
  Placement = pos=(-1.5,1.1e-15,0) rot=(0,0,1;0rad)
  shape: bbox 0.75 x 18.65 x 6.653 mm, 5 faces (baked)
FEATURE [App::Part] Heater_Cartridge_v007  label="Heater Cartridge v007"
  Group = -> [Part__Feature281,Part__Feature279,Part__Feature257,Part__Feature280,Part__Feature252,Part__Feature273,Part__Feature249]
  Origin = -> Origin172
  Placement = pos=(6.5,-2,8.5) rot=(0,1,0;3.14159rad)
FEATURE [App::Part] V6_Heat_Block_Left005  label="V6 Heat Block Left005"
  Group = -> [m3x10mm_Hex_Socket_Cap_v007,m3x3mm_Set_Screw_v006,Part__Feature269,Heater_Cartridge_v007,Nozzle_v2010,Part__Feature219]
  Origin = -> Origin180
  Placement = pos=(-10,-37.35,-3) rot=(0,-1,0;1.5708rad)
FEATURE [Part::Feature] Part__Feature282  label="SOLID023"
  shape: bbox 6 x 6 x 16.5 mm, 4 faces (baked)
FEATURE [App::Part] Heater_Cartridge_v2__1_004  label="Heater Cartridge v2 (1)004"
  Group = -> [Part__Feature216,Part__Feature231,Part__Feature262,Part__Feature226,Part__Feature240,Part__Feature227,Part__Feature282]
  Origin = -> Origin176
  Placement = pos=(6.5,-2,-8.5) rot=(0,0,1;0rad)
FEATURE [App::Part] V6_Heat_Block_Right004  label="V6 Heat Block Right004"
  Group = -> [m3x10mm_Hex_Socket_Cap_v2__1_004,m3x3mm_Set_Screw_v1__1_004,Part__Feature232,Heater_Cartridge_v2__1_004,Nozzle_v2009,Part__Feature218]
  Origin = -> Origin157
  Placement = pos=(10,-37.35,-3) rot=(0,-1,0;1.5708rad)
FEATURE [Part::Feature] Part__Feature283  label="m3 set screw023"
  shape: bbox 3.468 x 3.004 x 3.274 mm, 36 faces (baked)
FEATURE [App::Part] _mm_grub_v1__5_004  label="3mm grub v1 (5)004"
  Group = -> [Part__Feature283]
  Origin = -> Origin162
  Placement = pos=(-13.2028,13.5,-15.4604) rot=(0.57735,0.57735,-0.57735;4.18879rad)
FEATURE [App::Part] Heat_Block004  label="Heat Block004"
  Group = -> [Part__Feature236,Part__Feature234,Part__Feature213,_mm_grub_v1__5_004,_mm_grub_v1__4_005,_mm_grub_v1__3_005,_mm_grub_v1__2_004,Part__Feature228,Part__Feature224,Part__Feature220,Part__Feature230,Part__Feature255,Part__Feature212]
  Origin = -> Origin163
  Placement = pos=(1.5472,-40.5,-18.4604) rot=(0,1,0;3.14159rad)
FEATURE [App::Part] Chimera__Assembly_MK1_v007  label="Chimera+ Assembly MK1 v007"
  Group = -> [Heat_Block004,V6_Heat_Block_Left004,V6_Heat_Block_Right004]
  Origin = -> Origin158
  Placement = pos=(-13.7,-0.3,0) rot=(-0.57735,0.57735,0.57735;4.18879rad)
FEATURE [App::Part] m3x3mm_Set_Screw_v1__1_005  label="m3x3mm Set Screw v1 (1)005"
  Group = -> [Part__Feature271]
  Origin = -> Origin169
  Placement = pos=(-8.81273,-14.347,-0.292105) rot=(1,0,0;1.5708rad)
FEATURE [App::Part] V6_Heat_Block_Right005  label="V6 Heat Block Right005"
  Group = -> [m3x10mm_Hex_Socket_Cap_v2__1_005,m3x3mm_Set_Screw_v1__1_005,Part__Feature256,Heater_Cartridge_v2__1_005,Nozzle_v2011,Part__Feature248]
  Origin = -> Origin181
  Placement = pos=(10,-37.35,-3) rot=(0,-1,0;1.5708rad)
FEATURE [App::Part] Chimera__Assembly_MK1_v008  label="Chimera+ Assembly MK1 v008"
  Group = -> [Heat_Block005,V6_Heat_Block_Left005,V6_Heat_Block_Right005]
  Origin = -> Origin175
  Placement = pos=(13.7,0.1,0) rot=(0.57735,0.57735,0.57735;2.0944rad)
FEATURE [Part::Feature] Part__Feature284  label="30mm Fan Mockup 3010 v013"
  Placement = pos=(-28.7,0.5,-20) rot=(0.707107,0,-0.707107;3.14159rad)
  shape: bbox 10 x 30 x 30 mm, 196 faces (baked)
FEATURE [Part::Feature] Part__Feature285  label="30mm Fan Mockup 3010 v014"
  Placement = pos=(39.9,0.6,-21) rot=(0.707107,0,-0.707107;3.14159rad)
  shape: bbox 10 x 30 x 30 mm, 196 faces (baked)
FEATURE [App::Part] Part041  label="4-extruder-config001"
  Group = -> [Chimera__Assembly_MK1_v007,Chimera__Assembly_MK1_v008,Part__Feature285,Part__Feature284]
  Origin = -> Origin151
  Placement = pos=(-77.3,76.4,115.7) rot=(0,0,1;0rad)
FEATURE [Part::Feature] Part__Feature290  label="COMPOUND001"
  shape: bbox 14.06 x 29.09 x 86.92 mm, 120 faces, 4 solids (baked)
FEATURE [App::Part] LJ12A3_4_Z_BX_v6001  label="LJ12A3-4-Z/BX v007"
  Group = -> [Part__Feature290]
  Origin = -> Origin184
  Placement = pos=(0,7.7,0) rot=(0,1,0;3.14159rad)
FEATURE [Part::Feature] Part__Feature291  label="30mm Fan Mockup 3010 v015"
  Placement = pos=(-15.1,-1.3e-15,21.8) rot=(0.707107,0,-0.707107;3.14159rad)
  shape: bbox 10 x 30 x 30 mm, 196 faces (baked)
FEATURE [Part::Feature] Part__Feature292  label="30mm Fan Mockup 3010 v016"
  Placement = pos=(26,4.1e-15,21.8) rot=(0.707107,0,-0.707107;3.14159rad)
  shape: bbox 10 x 30 x 30 mm, 196 faces (baked)
FEATURE [App::Part] Part040  label="1-extruder-config001"
  Group = -> [E3D001,LJ12A3_4_Z_BX_v6001,Part__Feature291,Part__Feature292]
  Origin = -> Origin133
  Placement = pos=(-78.3,81.9,72) rot=(0,0,1;0rad)
FEATURE [Part::Feature] Part__Feature293  label="30mm Fan Mockup 3010 v017"
  Placement = pos=(31.9,0.8,106.8) rot=(0.707107,0,-0.707107;3.14159rad)
  shape: bbox 10 x 30 x 30 mm, 196 faces (baked)
FEATURE [Part::Feature] Part__Feature294  label="30mm Fan Mockup 3010 v018"
  Placement = pos=(-20.9,0.9,106.8) rot=(0.707107,0,-0.707107;3.14159rad)
  shape: bbox 10 x 30 x 30 mm, 196 faces (baked)
FEATURE [App::Part] Part039  label="2-extruder-config"
  Group = -> [Chimera__Assembly_MK1_v006,Part__Feature293,Part__Feature294]
  Origin = -> Origin132
  Placement = pos=(-76.4,73.9,115.4) rot=(0,0,1;0rad)
FEATURE [Sketcher::SketchObject] Sketch046
  MapMode = 5
  Support = -> [XY_Plane186]
  sketch-geometry (12):
    g0: LineSegment [constr] StartX=-21 StartY=21 StartZ=0 EndX=21 EndY=21 EndZ=0
    g1: LineSegment [constr] StartX=21 StartY=21 StartZ=0 EndX=21 EndY=-21 EndZ=0
    g2: LineSegment [constr] StartX=21 StartY=-21 StartZ=0 EndX=-21 EndY=-21 EndZ=0
    g3: LineSegment [constr] StartX=-21 StartY=-21 StartZ=0 EndX=-21 EndY=21 EndZ=0
    g4: LineSegment StartX=-15.5 StartY=21 StartZ=0 EndX=-21 EndY=15.5 EndZ=0
    g5: LineSegment StartX=-21 StartY=15.5 StartZ=0 EndX=-21 EndY=-15.5 EndZ=0
    g6: LineSegment StartX=-21 StartY=-15.5 StartZ=0 EndX=-15.5 EndY=-21 EndZ=0
    g7: LineSegment StartX=-15.5 StartY=-21 StartZ=0 EndX=15.5 EndY=-21 EndZ=0
    g8: LineSegment StartX=15.5 StartY=-21 StartZ=0 EndX=21 EndY=-15.5 EndZ=0
    g9: LineSegment StartX=21 StartY=-15.5 StartZ=0 EndX=21 EndY=15.5 EndZ=0
    g10: LineSegment StartX=21 StartY=15.5 StartZ=0 EndX=15.5 EndY=21 EndZ=0
    g11: LineSegment StartX=15.5 StartY=21 StartZ=0 EndX=-15.5 EndY=21 EndZ=0
  constraints (31):
    c: Coincident(g0,g1)
    c: Coincident(g1,g2)
    c: Coincident(g2,g3)
    c: Coincident(g3,g0)
    c: Horizontal(g0)
    c: Horizontal(g2)
    c: Vertical(g1)
    c: Vertical(g3)
    c: Coincident(g4,g5)
    c: Coincident(g5,g6)
    c: Coincident(g6,g7)
    c: PointOnObject(g7,g2)
    c: Coincident(g7,g8)
    c: Coincident(g8,g9)
    c: Coincident(g9,g10)
    c: Coincident(g10,g11)
    c: Coincident(g4,g11)
    c: Symmetric(g0,g1,g-1)
    c: Equal(g0,g3)
    c: DistanceX(g0,g0) = 42
    c: PointOnObject(g4,g0)
    c: PointOnObject(g4,g3)
    c: Symmetric(g4,g10,g-2)
    c: DistanceX(g11,g11) = 31
    c: Symmetric(g4,g5,g-1)
    c: Equal(g5,g11)
    c: Equal(g5,g7)
    c: Equal(g7,g9)
    c: PointOnObject(g8,g1)
    c: Symmetric(g7,g6,g-2)
    c: Symmetric(g8,g9,g-1)
FEATURE [PartDesign::Pad] Pad043
  Length = 23.5
  Length2 = 100
  Profile = -> Sketch046
  Refine = true
  Reversed = true
  Type = 0
FEATURE [Sketcher::SketchObject] Sketch047
  MapMode = 5
  Support = -> [Pad043]
  sketch-geometry (1):
    g0: Circle CenterX=0 CenterY=0 CenterZ=0 NormalX=0 NormalY=0 NormalZ=1 AngleXU=0 Radius=11.4
  constraints (2):
    c: Coincident(g0,g-1)
    c: Diameter(g0) = 22.8
FEATURE [PartDesign::Pad] Pad044
  BaseFeature = -> Pad043
  Length = 2
  Length2 = 100
  Profile = -> Sketch047
  Refine = true
  Type = 0
FEATURE [Sketcher::SketchObject] Sketch048
  MapMode = 5
  Placement = pos=(0,0,2) rot=(0,0,1;0rad)
  Support = -> [Pad044]
  sketch-geometry (1):
    g0: Circle CenterX=0 CenterY=0 CenterZ=0 NormalX=0 NormalY=0 NormalZ=1 AngleXU=0 Radius=2.5
  constraints (2):
    c: Coincident(g0,g-1)
    c: Diameter(g0) = 5
FEATURE [PartDesign::Pad] Pad045
  BaseFeature = -> Pad044
  Length = 20
  Length2 = 100
  Profile = -> Sketch048
  Refine = true
  Type = 0
FEATURE [PartDesign::Body] Body040
  Group = -> [Sketch046,Pad043,Sketch047,Pad044,Sketch048,Pad045]
  Origin = -> Origin187
  Tip = -> Pad045
FEATURE [App::Part] Part043  label="nema-42-thin"
  Group = -> [Body040]
  Origin = -> Origin186
  Placement = pos=(-83.6,82.3,136.4) rot=(-0.707107,0,-0.707107;3.14159rad)
FEATURE [Part::Feature] Part__Feature295  label="CR10_HotEnd002"
  Placement = pos=(-50.8,83.3,69.4) rot=(0.57735,-0.57735,-0.57735;2.0944rad)
  shape: bbox 20.41 x 21.65 x 62.4 mm, 1210 faces, 9 solids (baked)
FEATURE [Part::Feature] Part__Feature296  label="MotorGear"
  shape: bbox 15.15 x 15 x 15.15 mm, 359 faces (baked)
FEATURE [Part::Feature] Part__Feature297  label="FlyGear"
  Placement = pos=(-12.5,0,0) rot=(0,0,1;0rad)
  shape: bbox 15.15 x 22 x 15.15 mm, 368 faces (baked)
FEATURE [App::Part] _MMBondtechGears_v7  label="8MMBondtechGears v7"
  Group = -> [Part__Feature296,Part__Feature297]
  Origin = -> Origin188
  Placement = pos=(-60.2,83.1,137.2) rot=(0,0,1;1.5708rad)
FEATURE [App::Part] Part042  label="near-extruder"
  Group = -> [Part043,Part__Feature295,_MMBondtechGears_v7]
  Origin = -> Origin185
FEATURE [App::DocumentObjectGroup] Group001  label="toolhead-config"
  Group = -> [Part033,Part039,Part040,Part041,Part042]
FEATURE [App::DocumentObjectGroup] Group  label="testing"
  Group = -> [Body002,Group001]
FEATURE [Sketcher::SketchObject] Sketch049
  ExternalGeometry = -> [Pad040]
  MapMode = 5
  Placement = pos=(0,0,66.5) rot=(0,0,1;0rad)
  Support = -> [Pad040]
  sketch-geometry (7):
    g0: LineSegment [constr] StartX=66.5 StartY=-66.5 StartZ=0 EndX=91 EndY=-66.5 EndZ=0
    g1: LineSegment StartX=91 StartY=-66.5 StartZ=0 EndX=91 EndY=-91 EndZ=0
    g2: LineSegment StartX=91 StartY=-91 StartZ=0 EndX=66.5 EndY=-91 EndZ=0
    g3: LineSegment [constr] StartX=66.5 StartY=-91 StartZ=0 EndX=66.5 EndY=-66.5 EndZ=0
    g4: LineSegment StartX=66.5 StartY=-69 StartZ=0 EndX=66.5 EndY=-91 EndZ=0
    g5: LineSegment StartX=69 StartY=-66.5 StartZ=0 EndX=91 EndY=-66.5 EndZ=0
    g6: ArcOfCircle CenterX=66.5 CenterY=-66.5 CenterZ=0 NormalX=0 NormalY=0 NormalZ=1 AngleXU=0 Radius=2.5 StartAngle=7.7e-15 EndAngle=4.71239
  constraints (19):
    c: Coincident(g0,g1)
    c: Coincident(g1,g2)
    c: Coincident(g2,g3)
    c: Coincident(g3,g0)
    c: Horizontal(g0)
    c: Horizontal(g2)
    c: Vertical(g1)
    c: Vertical(g3)
    c: PointOnObject(g4,g3)
    c: PointOnObject(g5,g0)
    c: Coincident(g0,g5)
    c: Coincident(g2,g4)
    c: Coincident(g0,g-4)
    c: Coincident(g0,g6)
    c: Coincident(g4,g6)
    c: Coincident(g5,g6)
    c: Diameter(g6) = 5
    c: Equal(g4,g-7)
    c: Equal(g4,g5)
FEATURE [PartDesign::Pad] Pad046
  BaseFeature = -> Pad040
  Length = 5
  Length2 = 100
  Profile = -> Sketch049
  Refine = true
  Type = 0
FEATURE [Sketcher::SketchObject] Sketch050
  ExternalGeometry = -> [Pad046]
  MapMode = 5
  Placement = pos=(0,0,71.5) rot=(0,0,1;0rad)
  Support = -> [Pad046]
  sketch-geometry (6):
    g0: LineSegment StartX=38.75 StartY=-43.75 StartZ=0 EndX=118.75 EndY=-43.75 EndZ=0
    g1: LineSegment StartX=118.75 StartY=-43.75 StartZ=0 EndX=118.75 EndY=-103.75 EndZ=0
    g2: LineSegment StartX=118.75 StartY=-103.75 StartZ=0 EndX=38.75 EndY=-103.75 EndZ=0
    g3: LineSegment StartX=38.75 StartY=-103.75 StartZ=0 EndX=38.75 EndY=-43.75 EndZ=0
    g4: GeomPoint X=78.75 Y=-78.75 Z=0
    g5: LineSegment [constr] StartX=78.75 StartY=-77.0551 StartZ=0 EndX=78.75 EndY=-100.553 EndZ=0
  constraints (14):
    c: Coincident(g0,g1)
    c: Coincident(g1,g2)
    c: Coincident(g2,g3)
    c: Coincident(g3,g0)
    c: Horizontal(g0)
    c: Horizontal(g2)
    c: Vertical(g1)
    c: Vertical(g3)
    c: Equal(g-3,g2)
    c: Equal(g3,g-4)
    c: Symmetric(g-8,g-7,g4)
    c: PointOnObject(g4,g5)
    c: Symmetric(g2,g1,g5)
    c: DistanceY(g2,g4) = 25
FEATURE [PartDesign::Pad] Pad047
  BaseFeature = -> Pad046
  Length = 80
  Length2 = 100
  Profile = -> Sketch050
  Refine = true
  Type = 0
FEATURE [PartDesign::Body] Body038  label="test-get-print-head-extreme-point"
  Group = -> [Sketch040,Pad038,Sketch041,Pad039,Sketch043,Pad040,Sketch049,Pad046,Sketch050,Pad047]
  Origin = -> Origin077
  Tip = -> Pad047
FEATURE [PartDesign::ShapeBinder] ReferencePad047
  Placement = pos=(0,0,161.5) rot=(0,0,1;0rad)
  Support = -> [Pad047]
  TraceSupport = false
FEATURE [PartDesign::Line] DatumLine
  AttacherType = Attacher::AttachEngineLine
  MapMode = 29
  Placement = pos=(-117.5,0,161.5) rot=(0,0.707107,0.707107;3.14159rad)
  Support = -> [ReferencePad047]
FEATURE [PartDesign::ShapeBinder] ReferencePad047001
  Placement = pos=(0,0,161.5) rot=(0,0,1;0rad)
  Support = -> [Pad047]
  TraceSupport = false
FEATURE [PartDesign::Line] DatumLine001
  AttacherType = Attacher::AttachEngineLine
  MapMode = 29
  Placement = pos=(0,112.5,161.5) rot=(0.57735,0.57735,0.57735;2.0944rad)
  Support = -> [ReferencePad047001]
FEATURE [PartDesign::ShapeBinder] ReferencePad047002
  Placement = pos=(0,0,151.5) rot=(0,0,1;0rad)
  Support = -> [Pad047]
  TraceSupport = false
FEATURE [PartDesign::Line] DatumLine002
  AttacherType = Attacher::AttachEngineLine
  MapMode = 29
  Placement = pos=(0,-103.75,151.5) rot=(0.57735,-0.57735,-0.57735;2.0944rad)
  Support = -> [ReferencePad047002]
FEATURE [PartDesign::ShapeBinder] ReferencePad047003
  Placement = pos=(0,0,151.5) rot=(0,0,1;0rad)
  Support = -> [Pad047]
  TraceSupport = false
FEATURE [PartDesign::Line] DatumLine003
  AttacherType = Attacher::AttachEngineLine
  MapMode = 29
  Placement = pos=(118.75,0,151.5) rot=(1,0,0;1.5708rad)
  Support = -> [ReferencePad047003]
FEATURE [Sketcher::SketchObject] Sketch051
  ExternalGeometry = -> [DatumLine001,DatumLine003,DatumLine,DatumLine002]
  MapMode = 5
  Support = -> [XY_Plane096]
  sketch-geometry (4):
    g0: LineSegment StartX=-117.5 StartY=112.5 StartZ=0 EndX=118.75 EndY=112.5 EndZ=0
    g1: LineSegment StartX=118.75 StartY=112.5 StartZ=0 EndX=118.75 EndY=-103.75 EndZ=0
    g2: LineSegment StartX=118.75 StartY=-103.75 StartZ=0 EndX=-117.5 EndY=-103.75 EndZ=0
    g3: LineSegment StartX=-117.5 StartY=-103.75 StartZ=0 EndX=-117.5 EndY=112.5 EndZ=0
  constraints (12):
    c: Coincident(g0,g1)
    c: Coincident(g1,g2)
    c: Coincident(g2,g3)
    c: Coincident(g3,g0)
    c: Horizontal(g0)
    c: Horizontal(g2)
    c: Vertical(g1)
    c: Vertical(g3)
    c: PointOnObject(g1,g-4)
    c: PointOnObject(g1,g-6)
    c: PointOnObject(g0,g-5)
    c: PointOnObject(g0,g-3)
FEATURE [PartDesign::Pad] Pad048
  Length = 95
  Length2 = 100
  Midplane = true
  Profile = -> Sketch051
  Refine = true
  Type = 0
FEATURE [PartDesign::Body] Body039  label="test-xy-plane-hotend-movement"
  Group = -> [ReferencePad047003,DatumLine003,ReferencePad047002,DatumLine001,DatumLine002,ReferencePad047001,ReferencePad047,DatumLine,Sketch051,Pad048]
  Origin = -> Origin097
  Placement = pos=(0,0,113.6) rot=(0,0,1;0rad)
  Tip = -> Pad048
FEATURE [App::Part] Part029  label="print-volume-estimation"
  Group = -> [Body034,Body038,Body039]
  Origin = -> Origin065
FEATURE [App::DocumentObjectGroup] Group002  label="movement-test"
  Group = -> [Body038,Body039]
FEATURE [App::DocumentObjectGroup] Group003  label="origional-parts"
  Group = -> [Rear_Bed_Mount_Left_x1,Rear_Bed_Mount_Right_x1,_a__Foot_Rear_x2,_a__Foot_Rear_x2001]
FEATURE [Sketcher::SketchObject] Sketch053
  MapMode = 5
  Support = -> [XY_Plane193]
  sketch-geometry (12):
    g0: LineSegment StartX=-21.5 StartY=3.88809 StartZ=0 EndX=-21.5 EndY=-3.88809 EndZ=0
    g1: LineSegment StartX=-21.5 StartY=-3.88809 StartZ=0 EndX=-6.64474 EndY=-10.5737 EndZ=0
    g2: LineSegment StartX=6.64474 StartY=-10.5737 StartZ=0 EndX=21.5 EndY=-3.88809 EndZ=0
    g3: LineSegment StartX=21.5 StartY=-3.88809 StartZ=0 EndX=21.5 EndY=3.88809 EndZ=0
    g4: LineSegment StartX=21.5 StartY=3.88809 StartZ=0 EndX=6.64474 EndY=10.5737 EndZ=0
    g5: LineSegment StartX=-6.64474 StartY=10.5737 StartZ=0 EndX=-21.5 EndY=3.88809 EndZ=0
    g6: ArcOfCircle CenterX=-5e-16 CenterY=-4.19085 CenterZ=0 NormalX=0 NormalY=0 NormalZ=1 AngleXU=0 Radius=16.1909 StartAngle=1.1479 EndAngle=1.99369
    g7: ArcOfCircle CenterX=-1.9e-15 CenterY=4.19085 CenterZ=0 NormalX=0 NormalY=0 NormalZ=1 AngleXU=0 Radius=16.1909 StartAngle=4.2895 EndAngle=5.13528
    g8: LineSegment [constr] StartX=-21.5 StartY=12 StartZ=0 EndX=21.5 EndY=12 EndZ=0
    g9: LineSegment [constr] StartX=21.5 StartY=12 StartZ=0 EndX=21.5 EndY=-12 EndZ=0
    g10: LineSegment [constr] StartX=21.5 StartY=-12 StartZ=0 EndX=-21.5 EndY=-12 EndZ=0
    g11: LineSegment [constr] StartX=-21.5 StartY=-12 StartZ=0 EndX=-21.5 EndY=12 EndZ=0
  constraints (28):
    c: Coincident(g0,g1)
    c: Coincident(g2,g3)
    c: Coincident(g3,g4)
    c: Coincident(g0,g5)
    c: Tangent(g5,g6) = -1.5708
    c: Tangent(g4,g6) = -1.5708
    c: Tangent(g1,g7) = -1.5708
    c: Tangent(g2,g7) = -1.5708
    c: Coincident(g8,g9)
    c: Coincident(g9,g10)
    c: Coincident(g10,g11)
    c: Coincident(g11,g8)
    c: Horizontal(g8)
    c: Horizontal(g10)
    c: Vertical(g9)
    c: Vertical(g11)
    c: Symmetric(g8,g9,g-1)
    c: DistanceX(g8,g8) = 43
    c: DistanceY(g11,g11) = 24
    c: PointOnObject(g2,g9)
    c: Symmetric(g2,g3,g-1)
    c: Symmetric(g0,g0,g-1)
    c: Equal(g0,g3)
    c: Tangent(g7,g10)
    c: Tangent(g6,g8)
    c: Symmetric(g5,g4,g-2)
    c: Equal(g6,g7)
    c: Symmetric(g1,g2,g-2)
FEATURE [PartDesign::Pad] Pad050
  Length = 5
  Length2 = 100
  Profile = -> Sketch053
  Refine = true
  Type = 0
FEATURE [Sketcher::SketchObject] Sketch054
  MapMode = 5
  Placement = pos=(0,0,5) rot=(0,0,1;0rad)
  Support = -> [Pad050]
  sketch-geometry (1):
    g0: Circle CenterX=0 CenterY=0 CenterZ=0 NormalX=0 NormalY=0 NormalZ=1 AngleXU=0 Radius=10
  constraints (2):
    c: Coincident(g0,g-1)
    c: Diameter(g0) = 20
FEATURE [PartDesign::Pad] Pad051
  BaseFeature = -> Pad050
  Length = 5
  Length2 = 100
  Profile = -> Sketch054
  Refine = true
  Type = 0
FEATURE [Sketcher::SketchObject] Sketch055
  MapMode = 5
  Placement = pos=(0,0,5) rot=(0,0,1;0rad)
  Support = -> [Pad050]
  sketch-geometry (2):
    g0: Circle CenterX=-16 CenterY=0 CenterZ=0 NormalX=0 NormalY=0 NormalZ=1 AngleXU=0 Radius=1.3005
    g1: Circle CenterX=16 CenterY=0 CenterZ=0 NormalX=0 NormalY=0 NormalZ=1 AngleXU=0 Radius=1.59945
  constraints (3):
    c: Symmetric(g0,g1,g-2)
    c: PointOnObject(g0,g-1)
    c: DistanceX(g0,g1) = 32
FEATURE [PartDesign::Hole] Hole
  BaseFeature = -> Pad051
  Depth = 25
  DepthType = 0
  Diameter = 4.4
  DrillPoint = 1
  DrillPointAngle = 118
  HoleCutCountersinkAngle = 90
  HoleCutDepth = 0
  HoleCutDiameter = 4
  HoleCutType = 0
  ModelActualThread = false
  Profile = -> Sketch055
  Refine = true
  Tapered = false
  TaperedAngle = 90
  ThreadAngle = 0
  ThreadClass = 0
  ThreadCutOffInner = 0
  ThreadCutOffOuter = 0
  ThreadDirection = 0
  ThreadFit = 0
  ThreadPitch = 0
  ThreadSize = 5
  ThreadType = 1
  Threaded = false
FEATURE [Sketcher::SketchObject] Sketch056
  MapMode = 5
  Placement = pos=(0,0,10) rot=(0,0,1;0rad)
  Support = -> [Hole]
  sketch-geometry (1):
    g0: Circle CenterX=0 CenterY=0 CenterZ=0 NormalX=0 NormalY=0 NormalZ=1 AngleXU=0 Radius=3
  constraints (2):
    c: Coincident(g0,g-1)
    c: Diameter(g0) = 6
FEATURE [PartDesign::Pocket] Pocket
  BaseFeature = -> Hole
  Length = 5
  Length2 = 100
  Profile = -> Sketch056
  Refine = true
  Type = 1
FEATURE [PartDesign::Body] Body042  label="SHF6"
  Group = -> [Sketch053,Pad050,Sketch054,Pad051,Sketch055,Hole,Sketch056,Pocket]
  Origin = -> Origin194
  Tip = -> Pocket
FEATURE [App::Part] Part047  label="SHF"
  Group = -> [Body042]
  Origin = -> Origin193
  Placement = pos=(107.1,-101.4,85.6) rot=(-0.57735,0.57735,0.57735;2.0944rad)
FEATURE [Sketcher::SketchObject] Sketch057
  MapMode = 5
  Placement = pos=(0,0,0) rot=(1,0,0;1.5708rad)
  Support = -> [XZ_Plane195]
  sketch-geometry (1):
    g0: Circle CenterX=0 CenterY=0 CenterZ=0 NormalX=0 NormalY=0 NormalZ=1 AngleXU=0 Radius=3
  constraints (2):
    c: Coincident(g0,g-1)
    c: Diameter(g0) = 6
FEATURE [PartDesign::Pad] Pad052
  Length = 180
  Length2 = 100
  Placement = pos=(0,0,0) rot=(1,0,0;1.5708rad)
  Profile = -> Sketch057
  Refine = true
  Type = 0
FEATURE [PartDesign::Body] Body043
  Group = -> [Sketch057,Pad052]
  Origin = -> Origin196
  Placement = pos=(0,0,0) rot=(1,0,0;3.14159rad)
  Tip = -> Pad052
FEATURE [App::Part] Part048  label="6mm 光軸"
  Group = -> [Body043]
  Origin = -> Origin195
  Placement = pos=(154,-83.4,128.3) rot=(0,0,1;0rad)
FEATURE [Sketcher::SketchObject] Sketch059
  MapMode = 5
  Placement = pos=(0,0,0) rot=(1,0,0;1.5708rad)
  Support = -> [XZ_Plane201]
  sketch-geometry (2):
    g0: Circle CenterX=0 CenterY=0 CenterZ=0 NormalX=0 NormalY=0 NormalZ=1 AngleXU=0 Radius=3.05
    g1: Circle CenterX=0 CenterY=0 CenterZ=0 NormalX=0 NormalY=0 NormalZ=1 AngleXU=0 Radius=6
  constraints (4):
    c: Coincident(g0,g1)
    c: Coincident(g0,g-1)
    c: Diameter(g0) = 6.1
    c: Diameter(g1) = 12
FEATURE [Sketcher::SketchObject] Sketch060
  MapMode = 5
  Placement = pos=(0,0,0) rot=(1,0,0;1.5708rad)
  Support = -> [XZ_Plane200]
  sketch-geometry (1):
    g0: Circle CenterX=0 CenterY=0 CenterZ=0 NormalX=0 NormalY=0 NormalZ=1 AngleXU=0 Radius=3
  constraints (2):
    c: Coincident(g0,g-1)
    c: Diameter(g0) = 6
FEATURE [PartDesign::Pad] Pad053
  Length = 200
  Length2 = 100
  Midplane = true
  Placement = pos=(0,0,0) rot=(1,0,0;1.5708rad)
  Profile = -> Sketch060
  Refine = true
  Type = 0
FEATURE [PartDesign::Pad] Pad001
  Length = 20
  Length2 = 100
  Midplane = true
  Placement = pos=(0,0,0) rot=(1,0,0;1.5708rad)
  Profile = -> Sketch059
  Refine = true
  Type = 0
FEATURE [PartDesign::Body] Body001  label="LM6UU"
  Group = -> [Sketch059,Pad001]
  Origin = -> Origin200
  Tip = -> Pad001
FEATURE [PartDesign::Body] Body045  label="6mm 光軸001"
  Group = -> [Sketch060,Pad053]
  Origin = -> Origin201
  Tip = -> Pad053
FEATURE [App::Part] Part051  label="光軸+滑塊"
  Group = -> [Body045,Body001]
  Origin = -> Origin202
  Placement = pos=(153.9,14.4,127.7) rot=(0,0,1;0rad)
FEATURE [Mesh::Feature] XY_Joint_Right_Bottom_x002
  Placement = pos=(-127.5,120.7,-0.4) rot=(1,0,0;3.14159rad)
FEATURE [Mesh::Feature] XY_Joint_Right_Top_x002
  Placement = pos=(-127.2,120.7,24.3) rot=(1,0,0;3.14159rad)
FEATURE [App::Part] Part035  label="XY_Joint_Right001"
  Group = -> [XY_Joint_Right_Bottom_x002,XY_Joint_Right_Top_x002]
  Origin = -> Origin075
  Placement = pos=(143.1,5.4,-5.6) rot=(0,0,1;0rad)
FEATURE [App::Part] Part032  label="xy-joint-y-max"
  Group = -> [Part036,Part035,Body036]
  Origin = -> Origin070
  Placement = pos=(0,-2.9e-15,0) rot=(0,0,1;0rad)
FEATURE [Sketcher::SketchObject] Sketch061
  MapMode = 5
  Support = -> [XY_Plane203]
  sketch-geometry (12):
    g0: LineSegment StartX=-15 StartY=8.5 StartZ=0 EndX=15 EndY=8.5 EndZ=0
    g1: LineSegment StartX=15 StartY=8.5 StartZ=0 EndX=15 EndY=-8.5 EndZ=0
    g2: LineSegment StartX=15 StartY=-8.5 StartZ=0 EndX=-15 EndY=-8.5 EndZ=0
    g3: LineSegment StartX=-15 StartY=-8.5 StartZ=0 EndX=-15 EndY=8.5 EndZ=0
    g4: LineSegment [constr] StartX=-6.5 StartY=6 StartZ=0 EndX=6.5 EndY=6 EndZ=0
    g5: LineSegment [constr] StartX=6.5 StartY=6 StartZ=0 EndX=6.5 EndY=-6 EndZ=0
    g6: LineSegment [constr] StartX=6.5 StartY=-6 StartZ=0 EndX=-6.5 EndY=-6 EndZ=0
    g7: LineSegment [constr] StartX=-6.5 StartY=-6 StartZ=0 EndX=-6.5 EndY=6 EndZ=0
    g8: Circle CenterX=-6.5 CenterY=6 CenterZ=0 NormalX=0 NormalY=0 NormalZ=1 AngleXU=0 Radius=1.02308
    g9: Circle CenterX=6.5 CenterY=6 CenterZ=0 NormalX=0 NormalY=0 NormalZ=1 AngleXU=0 Radius=1.02308
    g10: Circle CenterX=-6.5 CenterY=-6 CenterZ=0 NormalX=0 NormalY=0 NormalZ=1 AngleXU=0 Radius=1.02308
    g11: Circle CenterX=6.5 CenterY=-6 CenterZ=0 NormalX=0 NormalY=0 NormalZ=1 AngleXU=0 Radius=1.02308
  constraints (29):
    c: Coincident(g0,g1)
    c: Coincident(g1,g2)
    c: Coincident(g2,g3)
    c: Coincident(g3,g0)
    c: Horizontal(g0)
    c: Horizontal(g2)
    c: Vertical(g1)
    c: Vertical(g3)
    c: Symmetric(g0,g1,g-1)
    c: DistanceX(g0,g0) = 30
    c: DistanceY(g3,g3) = 17
    c: Coincident(g4,g5)
    c: Coincident(g5,g6)
    c: Coincident(g6,g7)
    c: Coincident(g7,g4)
    c: Horizontal(g4)
    c: Horizontal(g6)
    c: Vertical(g5)
    c: Vertical(g7)
    c: Symmetric(g4,g5,g-1)
    c: DistanceY(g5,g5) = 12
    c: DistanceX(g4,g4) = 13
    c: Coincident(g11,g5)
    c: Coincident(g10,g6)
    c: Coincident(g8,g4)
    c: Coincident(g4,g9)
    c: Equal(g8,g9)
    c: Equal(g9,g10)
    c: Equal(g10,g11)
FEATURE [PartDesign::Pad] Pad054
  Length = 6.5
  Length2 = 100
  Profile = -> Sketch061
  Refine = true
  Type = 0
FEATURE [PartDesign::Body] Body046
  Group = -> [Sketch061,Pad054]
  Origin = -> Origin205
  Tip = -> Pad054
FEATURE [Sketcher::SketchObject] Sketch062
  MapMode = 5
  Placement = pos=(0,0,0) rot=(0.57735,0.57735,0.57735;2.0944rad)
  Support = -> [YZ_Plane202]
  sketch-geometry (4):
    g0: LineSegment StartX=-3.5 StartY=4.8 StartZ=0 EndX=3.5 EndY=4.8 EndZ=0
    g1: LineSegment StartX=3.5 StartY=4.8 StartZ=0 EndX=3.5 EndY=0 EndZ=0
    g2: LineSegment StartX=3.5 StartY=0 StartZ=0 EndX=-3.5 EndY=-1e-16 EndZ=0
    g3: LineSegment StartX=-3.5 StartY=-1e-16 StartZ=0 EndX=-3.5 EndY=4.8 EndZ=0
  constraints (11):
    c: Coincident(g0,g1)
    c: Coincident(g1,g2)
    c: Coincident(g2,g3)
    c: Coincident(g3,g0)
    c: Horizontal(g0)
    c: Vertical(g1)
    c: Vertical(g3)
    c: DistanceX(g0,g0) = 7
    c: DistanceY(g3,g3) = 4.8
    c: Symmetric(g2,g1,g-2)
    c: PointOnObject(g1,g-1)
FEATURE [PartDesign::Pad] Pad055
  Length = 200
  Length2 = 100
  Midplane = true
  Placement = pos=(0,0,0) rot=(0.57735,0.57735,0.57735;2.0944rad)
  Profile = -> Sketch062
  Refine = true
  Type = 0
FEATURE [PartDesign::Body] Body047
  Group = -> [Sketch062,Pad055]
  Origin = -> Origin203
  Tip = -> Pad055
FEATURE [App::Part] Part052  label="MGN7H"
  Group = -> [Body046,Body047]
  Origin = -> Origin204
  Placement = pos=(145.8,-0.1,109.7) rot=(-0.57735,0.57735,0.57735;4.18879rad)
FEATURE [App::Part] Part054
  Origin = -> Origin207
FEATURE [Mesh::Feature] _a__Toolhead_Blower_Duct_Left_TV6_x003  label="[a]_Toolhead_Blower_Duct_Left_TV6_x003"
  Placement = pos=(2.4e-15,-3,-11) rot=(0.57735,0.57735,0.57735;2.0944rad)
FEATURE [Mesh::Feature] Toolhead_Left_Threaded_V6_x003
  Placement = pos=(-13,-103,-174) rot=(0.57735,0.57735,0.57735;2.0944rad)
FEATURE [Mesh::Feature] _a__Toolhead_Blower_Duct_Right_TV6_x003  label="[a]_Toolhead_Blower_Duct_Right_TV6_x003"
  Placement = pos=(30.5,-152,145) rot=(0.57735,0.57735,-0.57735;4.18879rad)
FEATURE [Mesh::Feature] Toolhead_Right_Threaded_V6_x003
  Placement = pos=(18,-143,169.9) rot=(0.57735,0.57735,-0.57735;4.18879rad)
FEATURE [Part::Feature] Part__Feature298  label="30mm Fan Mockup 3010 v019"
  Placement = pos=(-15.5,-3.5,-6) rot=(0.707107,0,-0.707107;3.14159rad)
  shape: bbox 10 x 30 x 30 mm, 196 faces (baked)
FEATURE [App::Part] Part056
  Group = -> [Part__Feature298,_a__Toolhead_Blower_Duct_Left_TV6_x003]
  Origin = -> Origin208
  Placement = pos=(2.5,0,0) rot=(0,0,1;0rad)
FEATURE [Part::Feature] Part__Feature299  label="30mm Fan Mockup 3010 v020"
  Placement = pos=(19.5,-1.5,-7.5) rot=(0,1,0;1.5708rad)
  shape: bbox 10 x 30 x 30 mm, 196 faces (baked)
FEATURE [App::Part] Part055
  Group = -> [Part__Feature299,_a__Toolhead_Blower_Duct_Right_TV6_x003]
  Origin = -> Origin210
  Placement = pos=(-1.5,0,0) rot=(0,0,1;0rad)
FEATURE [App::Part] Part057  label="dummy-toolhead002"
  Group = -> [Toolhead_Left_Threaded_V6_x003,Toolhead_Right_Threaded_V6_x003,Part056,Part055]
  Origin = -> Origin209
  Placement = pos=(-77.8,-20.2,-4.5) rot=(0,0,1;0rad)
FEATURE [App::Part] Part053  label="xy-gantry-limit-1"
  Group = -> [Part032,Part057]
  Origin = -> Origin206
  Placement = pos=(0,115.5,130.4) rot=(0,0,1;0rad)
FEATURE [App::DocumentObjectGroup] Group004  label="1515-extrusion001"
  Group = -> [Body003,Body005,Body006,Body007,Body008,Body009,Body010,Body011,Body012,Body013,Body014,Body015,Body018,Body036]
FEATURE [Mesh::Feature] B_Idler_Bottom_x1
  Placement = pos=(-125.1,-123,-16.2) rot=(0,0,1;0rad)
FEATURE [Mesh::Feature] B_Idler_Top_x1
  Placement = pos=(-125.1,-123,9) rot=(0,0,1;0rad)
FEATURE [App::Part] Part050  label="B_Idler"
  Group = -> [B_Idler_Bottom_x1,B_Idler_Top_x1]
  Origin = -> Origin199
  Placement = pos=(-152.4,-100.2,132.4) rot=(0,0,1;0rad)
FEATURE [Sketcher::SketchObject] Sketch063
  MapMode = 5
  Placement = pos=(0,0,0) rot=(1,0,0;1.5708rad)
  Support = -> [XZ_Plane210]
  sketch-geometry (52):
    g0: LineSegment [constr] StartX=-7.5 StartY=7.5 StartZ=0 EndX=7.5 EndY=7.5 EndZ=0
    g1: LineSegment [constr] StartX=7.5 StartY=7.5 StartZ=0 EndX=7.5 EndY=-7.5 EndZ=0
    g2: LineSegment [constr] StartX=7.5 StartY=-7.5 StartZ=0 EndX=-7.5 EndY=-7.5 EndZ=0
    g3: LineSegment [constr] StartX=-7.5 StartY=-7.5 StartZ=0 EndX=-7.5 EndY=7.5 EndZ=0
    g4: LineSegment StartX=-2.09289 StartY=2.8 StartZ=0 EndX=2.09289 EndY=2.8 EndZ=0
    g5: LineSegment StartX=2.09289 StartY=2.8 StartZ=0 EndX=4.7 EndY=5.40711 EndZ=0
    g6: LineSegment StartX=4.7 StartY=5.40711 StartZ=0 EndX=4.7 EndY=6.5 EndZ=0
    g7: LineSegment StartX=4.7 StartY=6.5 StartZ=0 EndX=3.1 EndY=6.5 EndZ=0
    g8: LineSegment StartX=3.1 StartY=6.5 StartZ=0 EndX=3.1 EndY=7.5 EndZ=0
    g9: LineSegment StartX=3.1 StartY=7.5 StartZ=0 EndX=6.5 EndY=7.5 EndZ=0
    g10: LineSegment StartX=7.5 StartY=6.5 StartZ=0 EndX=7.5 EndY=3.1 EndZ=0
    g11: LineSegment StartX=7.5 StartY=3.1 StartZ=0 EndX=6.5 EndY=3.1 EndZ=0
    g12: LineSegment StartX=6.5 StartY=3.1 StartZ=0 EndX=6.5 EndY=4.7 EndZ=0
    g13: LineSegment StartX=6.5 StartY=4.7 StartZ=0 EndX=5.40711 EndY=4.7 EndZ=0
    g14: LineSegment StartX=5.40711 StartY=4.7 StartZ=0 EndX=2.8 EndY=2.09289 EndZ=0
    g15: LineSegment StartX=2.8 StartY=2.09289 StartZ=0 EndX=2.8 EndY=-2.09289 EndZ=0
    g16: LineSegment StartX=2.8 StartY=-2.09289 StartZ=0 EndX=5.40711 EndY=-4.7 EndZ=0
    g17: LineSegment StartX=5.40711 StartY=-4.7 StartZ=0 EndX=6.5 EndY=-4.7 EndZ=0
    g18: LineSegment StartX=6.5 StartY=-4.7 StartZ=0 EndX=6.5 EndY=-3.1 EndZ=0
    g19: LineSegment StartX=6.5 StartY=-3.1 StartZ=0 EndX=7.5 EndY=-3.1 EndZ=0
    g20: LineSegment StartX=7.5 StartY=-3.1 StartZ=0 EndX=7.5 EndY=-6.5 EndZ=0
    g21: LineSegment StartX=6.5 StartY=-7.5 StartZ=0 EndX=3.1 EndY=-7.5 EndZ=0
    g22: LineSegment StartX=3.1 StartY=-7.5 StartZ=0 EndX=3.1 EndY=-6.5 EndZ=0
    g23: LineSegment StartX=3.1 StartY=-6.5 StartZ=0 EndX=4.7 EndY=-6.5 EndZ=0
    g24: LineSegment StartX=4.7 StartY=-6.5 StartZ=0 EndX=4.7 EndY=-5.40711 EndZ=0
    g25: LineSegment StartX=4.7 StartY=-5.40711 StartZ=0 EndX=2.09289 EndY=-2.8 EndZ=0
    g26: LineSegment StartX=2.09289 StartY=-2.8 StartZ=0 EndX=-2.09289 EndY=-2.8 EndZ=0
    g27: LineSegment StartX=-2.09289 StartY=-2.8 StartZ=0 EndX=-4.7 EndY=-5.40711 EndZ=0
    g28: LineSegment StartX=-4.7 StartY=-5.40711 StartZ=0 EndX=-4.7 EndY=-6.5 EndZ=0
    g29: LineSegment StartX=-4.7 StartY=-6.5 StartZ=0 EndX=-3.1 EndY=-6.5 EndZ=0
    g30: LineSegment StartX=-3.1 StartY=-6.5 StartZ=0 EndX=-3.1 EndY=-7.5 EndZ=0
    g31: LineSegment StartX=-3.1 StartY=-7.5 StartZ=0 EndX=-6.5 EndY=-7.5 EndZ=0
    g32: LineSegment StartX=-7.5 StartY=-6.5 StartZ=0 EndX=-7.5 EndY=-3.1 EndZ=0
    g33: LineSegment StartX=-7.5 StartY=-3.1 StartZ=0 EndX=-6.5 EndY=-3.1 EndZ=0
    g34: LineSegment StartX=-6.5 StartY=-3.1 StartZ=0 EndX=-6.5 EndY=-4.7 EndZ=0
    g35: LineSegment StartX=-6.5 StartY=-4.7 StartZ=0 EndX=-5.40711 EndY=-4.7 EndZ=0
    g36: LineSegment StartX=-5.40711 StartY=-4.7 StartZ=0 EndX=-2.8 EndY=-2.09289 EndZ=0
    g37: LineSegment StartX=-2.8 StartY=-2.09289 StartZ=0 EndX=-2.8 EndY=2.09289 EndZ=0
    g38: LineSegment StartX=-2.8 StartY=2.09289 StartZ=0 EndX=-5.40711 EndY=4.7 EndZ=0
    g39: LineSegment StartX=-5.40711 StartY=4.7 StartZ=0 EndX=-6.5 EndY=4.7 EndZ=0
    g40: LineSegment StartX=-6.5 StartY=4.7 StartZ=0 EndX=-6.5 EndY=3.1 EndZ=0
    g41: LineSegment StartX=-6.5 StartY=3.1 StartZ=0 EndX=-7.5 EndY=3.1 EndZ=0
    g42: LineSegment StartX=-7.5 StartY=3.1 StartZ=0 EndX=-7.5 EndY=6.5 EndZ=0
    g43: LineSegment StartX=-6.5 StartY=7.5 StartZ=0 EndX=-3.1 EndY=7.5 EndZ=0
    g44: LineSegment StartX=-3.1 StartY=7.5 StartZ=0 EndX=-3.1 EndY=6.5 EndZ=0
    g45: LineSegment StartX=-3.1 StartY=6.5 StartZ=0 EndX=-4.7 EndY=6.5 EndZ=0
    g46: LineSegment StartX=-4.7 StartY=6.5 StartZ=0 EndX=-4.7 EndY=5.40711 EndZ=0
    g47: LineSegment StartX=-4.7 StartY=5.40711 StartZ=0 EndX=-2.09289 EndY=2.8 EndZ=0
    g48: ArcOfCircle CenterX=-6.5 CenterY=6.5 CenterZ=0 NormalX=0 NormalY=0 NormalZ=1 AngleXU=0 Radius=1 StartAngle=1.5708 EndAngle=3.14159
    g49: ArcOfCircle CenterX=6.5 CenterY=6.5 CenterZ=0 NormalX=0 NormalY=0 NormalZ=1 AngleXU=0 Radius=1 StartAngle=0 EndAngle=1.5708
    g50: ArcOfCircle CenterX=6.5 CenterY=-6.5 CenterZ=0 NormalX=0 NormalY=0 NormalZ=1 AngleXU=0 Radius=1 StartAngle=4.71239 EndAngle=6.28319
    g51: ArcOfCircle CenterX=-6.5 CenterY=-6.5 CenterZ=0 NormalX=0 NormalY=0 NormalZ=1 AngleXU=0 Radius=1 StartAngle=3.14159 EndAngle=4.71239
  constraints (140):
    c: Coincident(g0,g1)
    c: Coincident(g1,g2)
    c: Coincident(g2,g3)
    c: Coincident(g3,g0)
    c: Horizontal(g0)
    c: Horizontal(g2)
    c: Vertical(g1)
    c: Vertical(g3)
    c: Symmetric(g0,g1,g-1)
    c: Equal(g3,g0)
    c: DistanceY(g3,g3) = 15
    c: Coincident(g4,g5)
    c: Coincident(g5,g6)
    c: Coincident(g6,g7)
    c: Coincident(g7,g8)
    c: Vertical(g8)
    c: Coincident(g8,g9)
    c: Horizontal(g9)
    c: Vertical(g10)
    c: Coincident(g10,g11)
    c: Horizontal(g11)
    c: Coincident(g11,g12)
    c: Vertical(g12)
    c: Coincident(g12,g13)
    c: Horizontal(g13)
    c: Coincident(g13,g14)
    c: Coincident(g14,g15)
    c: Coincident(g15,g16)
    c: Coincident(g16,g17)
    c: Horizontal(g17)
    c: Coincident(g17,g18)
    c: Coincident(g18,g19)
    c: Coincident(g19,g20)
    c: Vertical(g20)
    c: Horizontal(g21)
    c: Coincident(g21,g22)
    c: Coincident(g22,g23)
    c: Horizontal(g23)
    c: Coincident(g23,g24)
    c: Coincident(g24,g25)
    c: Coincident(g25,g26)
    c: Coincident(g26,g27)
    c: Coincident(g27,g28)
    c: Vertical(g28)
    c: Coincident(g28,g29)
    c: Coincident(g29,g30)
    c: Coincident(g30,g31)
    c: Coincident(g32,g33)
    c: Coincident(g33,g34)
    c: Coincident(g34,g35)
    c: Coincident(g35,g36)
    c: Coincident(g36,g37)
    c: Coincident(g37,g38)
    c: Coincident(g38,g39)
    c: Coincident(g39,g40)
    c: Coincident(g40,g41)
    c: Coincident(g41,g42)
    c: Vertical(g42)
    c: Horizontal(g43)
    c: Coincident(g43,g44)
    c: Coincident(g44,g45)
    c: Horizontal(g45)
    c: Coincident(g45,g46)
    c: Coincident(g46,g47)
    c: Coincident(g4,g47)
    c: Tangent(g42,g48) = 1.5708
    c: Tangent(g43,g48) = 1.5708
    c: Tangent(g9,g49) = 1.5708
    c: Tangent(g10,g49) = 1.5708
    c: Tangent(g20,g50) = 1.5708
    c: Tangent(g21,g50) = 1.5708
    c: Tangent(g32,g51) = 1.5708
    c: Tangent(g31,g51) = 1.5708
    c: Horizontal(g41)
    c: Horizontal(g39)
    c: Horizontal(g19)
    c: Horizontal(g31)
    c: Horizontal(g35)
    c: Horizontal(g33)
    c: Vertical(g40)
    c: Vertical(g46)
    c: Vertical(g18)
    c: Vertical(g22)
    c: Vertical(g24)
    c: Vertical(g30)
    c: Vertical(g34)
    c: Vertical(g32)
    c: PointOnObject(g21,g2)
    c: PointOnObject(g32,g3)
    c: Vertical(g6)
    c: PointOnObject(g10,g1)
    c: Equal(g48,g49)
    c: Equal(g49,g50)
    c: Equal(g33,g41)
    c: Equal(g41,g30)
    c: Equal(g30,g22)
    c: Equal(g22,g19)
    c: Equal(g19,g11)
    c: Equal(g11,g8)
    c: Equal(g8,g44)
    c: Symmetric(g45,g6,g-2)
    c: DistanceX(g45,g6) = 9.4
    c: DistanceX(g43,g8) = 6.2
    c: Equal(g43,g42)
    c: Equal(g42,g32)
    c: DistanceY(g44,g44) = 1
    c: Equal(g31,g43)
    c: Equal(g43,g21)
    c: Equal(g21,g20)
    c: Equal(g20,g10)
    c: Radius(g49) = 1
    c: Symmetric(g37,g14,g-2)
    c: DistanceX(g37,g14) = 5.6
    c: Symmetric(g43,g8,g-2)
    c: Symmetric(g4,g26,g-1)
    c: DistanceY(g26,g4) = 5.6
    c: Symmetric(g4,g4,g-2)
    c: Equal(g45,g40)
    c: Equal(g45,g7)
    c: Equal(g7,g12)
    c: Equal(g12,g34)
    c: Equal(g34,g29)
    c: Equal(g29,g23)
    c: Equal(g23,g18)
    c: Equal(g39,g46)
    c: Equal(g46,g6)
    c: Equal(g6,g13)
    c: Equal(g13,g17)
    c: Equal(g17,g24)
    c: Equal(g24,g35)
    c: Equal(g35,g28)
    c: Parallel(g38,g47)
    c: Angle(g4,g47) = 2.35619
    c: Symmetric(g38,g35,g-1)
    c: Symmetric(g37,g36,g-1)
    c: Symmetric(g27,g46,g-1)
    c: Distance(g37,g4) = 1
    c: Symmetric(g27,g24,g-2)
    c: Symmetric(g26,g25,g-2)
    c: Symmetric(g36,g15,g-2)
FEATURE [PartDesign::Pad] Pad056
  Length = 290
  Length2 = 100
  Midplane = true
  Placement = pos=(0,0,0) rot=(1,0,0;1.5708rad)
  Profile = -> Sketch063
  Refine = true
  Type = 0
FEATURE [PartDesign::Body] Body048  label="extrusion-015"
  Group = -> [Sketch063,Pad056]
  Origin = -> Origin211
  Placement = pos=(5.48e-14,139.6,0) rot=(0,0,1;1.5708rad)
  Tip = -> Pad056
FEATURE [App::Part] Part002  label="frame-bottom"
  Group = -> [Body003,Body005,Body006,Body048]
  Origin = -> Origin006
  Placement = pos=(0,0,-122.7) rot=(0,0,1;0rad)
FEATURE [App::Part] Part005  label="extrusion"
  Group = -> [Part004,Part003,Part002,Part006]
  Origin = -> Origin020
  Placement = pos=(0,0,-13) rot=(0,0,1;0rad)
FEATURE [App::Part] Part058  label="z-end-stop"
  Group = -> [_a__Z_Endstop_Mount_x1]
  Origin = -> Origin212
  Placement = pos=(15.8,-25.9,94.9) rot=(0,0,1;0rad)
FEATURE [Sketcher::SketchObject] Sketch064
  MapMode = 5
  Support = -> [XY_Plane212]
  sketch-geometry (4):
    g0: LineSegment StartX=-65 StartY=95 StartZ=0 EndX=65 EndY=95 EndZ=0
    g1: LineSegment StartX=65 StartY=95 StartZ=0 EndX=65 EndY=-60 EndZ=0
    g2: LineSegment StartX=65 StartY=-60 StartZ=0 EndX=-65 EndY=-60 EndZ=0
    g3: LineSegment StartX=-65 StartY=-60 StartZ=0 EndX=-65 EndY=95 EndZ=0
  constraints (11):
    c: Coincident(g0,g1)
    c: Coincident(g1,g2)
    c: Coincident(g2,g3)
    c: Coincident(g3,g0)
    c: Horizontal(g2)
    c: Vertical(g1)
    c: Vertical(g3)
    c: Symmetric(g0,g0,g-2)
    c: DistanceX(g2,g-1) = 65
    c: DistanceY(g2,g-1) = 60
    c: DistanceY(g3,g3) = 155
FEATURE [PartDesign::Pad] Pad057
  Length = 3
  Length2 = 100
  Midplane = true
  Profile = -> Sketch064
  Refine = true
  Type = 0
FEATURE [PartDesign::Body] Body049  label="heat-bed-130-155"
  Group = -> [Sketch064,Pad057]
  Origin = -> Origin213
  Tip = -> Pad057
FEATURE [App::Part] Part038  label="heat-bed001"
  Group = -> [Body021,Part012,Body049]
  Origin = -> Origin096
  Placement = pos=(-1.3,1.6,64.8) rot=(0,0,1;0rad)
FEATURE [Part::Feature] Part__Feature300  label="NEMA17_a_drive"
  Placement = pos=(0.6,-21.2,-38.3) rot=(-0.707107,0,0.707107;3.14159rad)
  shape: bbox 48 x 42 x 62 mm, 423 faces, 20 solids (baked)
FEATURE [App::Part] Part008  label="A_Drive"
  Group = -> [A_Drive_Frame_Bottom_x1,_a__A_Drive_Tensioner_x1,A_Drive_Frame_Top_x1,Part__Feature300]
  Origin = -> Origin027
  Placement = pos=(127.5,165.1,141.8) rot=(0,0,1;0rad)
FEATURE [Part::Feature] Part__Feature301  label="NEMA17_b_drive"
  Placement = pos=(-2.1,24.9,-37.8) rot=(0,1,0;1.5708rad)
  shape: bbox 48 x 42 x 62 mm, 423 faces, 20 solids (baked)
FEATURE [Sketcher::SketchObject] Sketch065
  MapMode = 5
  Support = -> [XY_Plane214]
  sketch-geometry (1):
    g0: Circle CenterX=0 CenterY=0 CenterZ=0 NormalX=0 NormalY=0 NormalZ=1 AngleXU=0 Radius=2.5
  constraints (2):
    c: Coincident(g0,g-1)
    c: Diameter(g0) = 5
FEATURE [PartDesign::Pad] Pad058
  Length = 250
  Length2 = 100
  Profile = -> Sketch065
  Refine = true
  Type = 0
FEATURE [PartDesign::Body] Body050  label="梯形螺纹配铜螺母5MM "
  Group = -> [Sketch065,Pad058]
  Origin = -> Origin215
  Placement = pos=(0,111.1,0) rot=(0,0,1;0rad)
  Tip = -> Pad058
FEATURE [Part::Feature] Part__Feature303  label="Lagerschild_14"
  shape: bbox 35.89 x 42 x 11.8 mm, 72 faces (baked)
FEATURE [Part::Feature] Part__Feature304  label="Welle_14"
  shape: bbox 5 x 5 x 49 mm, 4 faces (baked)
FEATURE [Part::Feature] Part__Feature305  label="Stator_14"
  shape: bbox 35 x 35 x 10.4 mm, 660 faces (baked)
FEATURE [Part::Feature] Part__Feature306  label="Kollektorschild_14"
  shape: bbox 35 x 35 x 9.8 mm, 93 faces (baked)
FEATURE [Part::Feature] Part__Feature307  label="Schraube_M3x5"
  Placement = pos=(-14.3499,-5.33515,0) rot=(0,0,1;0.711909rad)
  shape: bbox 8.69 x 9.172 x 7 mm, 19 faces (baked)
FEATURE [Part::Feature] Part__Feature308  label="Schraube_M3x006"
  Placement = pos=(29.8697,20.3083,0) rot=(0,0,1;2.76501rad)
  shape: bbox 6.912 x 9.523 x 7 mm, 19 faces (baked)
FEATURE [Part::Feature] Part__Feature309  label="Schraube_M3x007"
  Placement = pos=(-19.5762,-30.1684,0) rot=(0,0,1;0.419596rad)
  shape: bbox 7.188 x 9.538 x 7 mm, 19 faces (baked)
FEATURE [Part::Feature] Part__Feature310  label="Schraube_M3x008"
  Placement = pos=(19.0553,-30.359,0) rot=(0,0,1;1.12103rad)
  shape: bbox 9.538 x 7.374 x 7 mm, 19 faces (baked)
FEATURE [Part::Feature] Part__Feature311  label="Connector_14"
  Placement = pos=(0,0,18.2) rot=(0,0,1;0rad)
  shape: bbox 29.4 x 39.27 x 34.94 mm, 307 faces (baked)
FEATURE [App::Part] NEMA14
  Group = -> [Part__Feature303,Part__Feature304,Part__Feature305,Part__Feature306,Part__Feature307,Part__Feature308,Part__Feature309,Part__Feature310,Part__Feature311]
  Origin = -> Origin216
  Placement = pos=(-3e-16,152.8,-2.8) rot=(0.707107,-0.707107,0;3.14159rad)
FEATURE [App::Part] Part059  label="z-driving"
  Group = -> [Body050,NEMA14]
  Origin = -> Origin214
  Placement = pos=(0,-135.5,-109.3) rot=(0,0,1;0rad)
FEATURE [App::Part] Part016  label="z-riser"
  Group = -> [Body019,Body020,Part058,Part059]
  Origin = -> Origin035
  Placement = pos=(0,0,-9) rot=(0,0,1;0rad)
FEATURE [App::Part] Part013  label="Z_Drive"
  Group = -> [Z_Motor_Mount_x1,Part016]
  Origin = -> Origin032
  Placement = pos=(0,147.4,0) rot=(0,0,1;0rad)
FEATURE [Part::Feature] Part__Feature312  label="Body, GT2 Timing Idler Pulley, Configurable_16T W6 B3 With T"
  Placement = pos=(0,0,0) rot=(0,1,0;4.1025rad)
  shape: bbox 13 x 8.5 x 13 mm, 163 faces (baked)
FEATURE [Part::Feature] Part__Feature313  label="Bearing Outer Ring, GT2 Timing Idler Pulley, Configurable_3 mm Bore, 6 mm OD"
  shape: bbox 6 x 2 x 6 mm, 10 faces (baked)
FEATURE [Part::Feature] Part__Feature314  label="Bearing Inner Ring, GT2 Timing Idler Pulley, Configurable_3 mm Bore, 6 mm OD"
  Placement = pos=(0,0,0) rot=(0,-1,0;1.53252rad)
  shape: bbox 3.829 x 2 x 3.829 mm, 12 faces (baked)
FEATURE [Part::Feature] Part__Feature315  label="Bearing Seal, GT2 Timing Idler Pulley, Configurable_3 mm Bore, 6 mm OD"
  Placement = pos=(0,0.75,0) rot=(0,0,1;0rad)
  shape: bbox 5.412 x 0.571 x 5.412 mm, 10 faces (baked)
FEATURE [Part::Feature] Part__Feature316  label="Bearing Seal, GT2 Timing Idler Pulley, Configurable_3 mm Bore, 6 mm OD001"
  Placement = pos=(0,-0.75,0) rot=(1,0,0;3.14159rad)
  shape: bbox 5.412 x 0.571 x 5.412 mm, 10 faces (baked)
FEATURE [Part::Feature] Part__Feature317  label="Bearing Ball, GT2 Timing Idler Pulley, Configurable_1 mm"
  Placement = pos=(-1.69054,0,-1.28751) rot=(0,-1,0;1.55577rad)
  shape: bbox 1 x 1 x 1 mm, 2 faces (baked)
FEATURE [Part::Feature] Part__Feature318  label="Bearing Ball, GT2 Timing Idler Pulley, Configurable_1 mm001"
  Placement = pos=(-0.284984,9e-16,-2.1058) rot=(0,1,0;3.94201rad)
  shape: bbox 1 x 1 x 1 mm, 2 faces (baked)
FEATURE [Part::Feature] Part__Feature319  label="Bearing Ball, GT2 Timing Idler Pulley, Configurable_1 mm002"
  Placement = pos=(1.28751,9e-16,-1.69054) rot=(0,1,0;3.15661rad)
  shape: bbox 1 x 1 x 1 mm, 2 faces (baked)
FEATURE [Part::Feature] Part__Feature320  label="Bearing Ball, GT2 Timing Idler Pulley, Configurable_1 mm003"
  Placement = pos=(2.1058,9e-16,-0.284984) rot=(0,1,0;2.37122rad)
  shape: bbox 1 x 1 x 1 mm, 2 faces (baked)
FEATURE [Part::Feature] Part__Feature321  label="Bearing Ball, GT2 Timing Idler Pulley, Configurable_1 mm004"
  Placement = pos=(1.69054,9e-16,1.28751) rot=(0,1,0;1.58582rad)
  shape: bbox 1 x 1 x 1 mm, 2 faces (baked)
FEATURE [Part::Feature] Part__Feature322  label="Bearing Ball, GT2 Timing Idler Pulley, Configurable_1 mm005"
  Placement = pos=(0.284984,9e-16,2.1058) rot=(0,1,0;0.80042rad)
  shape: bbox 1 x 1 x 1 mm, 2 faces (baked)
FEATURE [Part::Feature] Part__Feature323  label="Bearing Ball, GT2 Timing Idler Pulley, Configurable_1 mm006"
  Placement = pos=(-1.28751,9e-16,1.69054) rot=(0,1,0;0.015022rad)
  shape: bbox 1 x 1 x 1 mm, 2 faces (baked)
FEATURE [Part::Feature] Part__Feature324  label="Bearing Ball, GT2 Timing Idler Pulley, Configurable_1 mm007"
  Placement = pos=(-2.1058,9e-16,0.284984) rot=(0,-1,0;0.770376rad)
  shape: bbox 1 x 1 x 1 mm, 2 faces (baked)
FEATURE [App::Part] Bearing_Subassy__GT2_Timing_Idler_Pulley__Configurable_3_mm_Bore__6_mm_OD  label="Bearing Subassy, GT2 Timing Idler Pulley, Configurable_3 mm Bore, 6 mm OD"
  Group = -> [Part__Feature313,Part__Feature314,Part__Feature315,Part__Feature316,Part__Feature317,Part__Feature318,Part__Feature319,Part__Feature320,Part__Feature321,Part__Feature322,Part__Feature323,Part__Feature324]
  Origin = -> Origin217
  Placement = pos=(-1e-15,3.25,1.4e-15) rot=(0,1,0;0.960908rad)
FEATURE [Part::Feature] Part__Feature325  label="Bearing Outer Ring, GT2 Timing Idler Pulley, Configurable_3 mm Bore, 6 mm OD001"
  shape: bbox 6 x 2 x 6 mm, 10 faces (baked)
FEATURE [Part::Feature] Part__Feature326  label="Bearing Inner Ring, GT2 Timing Idler Pulley, Configurable_3 mm Bore, 6 mm OD001"
  Placement = pos=(0,0,0) rot=(0,-1,0;1.53252rad)
  shape: bbox 3.829 x 2 x 3.829 mm, 12 faces (baked)
FEATURE [Part::Feature] Part__Feature327  label="Bearing Seal, GT2 Timing Idler Pulley, Configurable_3 mm Bore, 6 mm OD002"
  Placement = pos=(0,0.75,0) rot=(0,0,1;0rad)
  shape: bbox 5.412 x 0.571 x 5.412 mm, 10 faces (baked)
FEATURE [Part::Feature] Part__Feature328  label="Bearing Seal, GT2 Timing Idler Pulley, Configurable_3 mm Bore, 6 mm OD003"
  Placement = pos=(0,-0.75,0) rot=(1,0,0;3.14159rad)
  shape: bbox 5.412 x 0.571 x 5.412 mm, 10 faces (baked)
FEATURE [Part::Feature] Part__Feature329  label="Bearing Ball, GT2 Timing Idler Pulley, Configurable_1 mm008"
  Placement = pos=(-1.69054,0,-1.28751) rot=(0,-1,0;1.55577rad)
  shape: bbox 1 x 1 x 1 mm, 2 faces (baked)
FEATURE [Part::Feature] Part__Feature330  label="Bearing Ball, GT2 Timing Idler Pulley, Configurable_1 mm009"
  Placement = pos=(-0.284984,9e-16,-2.1058) rot=(0,1,0;3.94201rad)
  shape: bbox 1 x 1 x 1 mm, 2 faces (baked)
FEATURE [Part::Feature] Part__Feature331  label="Bearing Ball, GT2 Timing Idler Pulley, Configurable_1 mm010"
  Placement = pos=(1.28751,9e-16,-1.69054) rot=(0,1,0;3.15661rad)
  shape: bbox 1 x 1 x 1 mm, 2 faces (baked)
FEATURE [Part::Feature] Part__Feature332  label="Bearing Ball, GT2 Timing Idler Pulley, Configurable_1 mm011"
  Placement = pos=(2.1058,9e-16,-0.284984) rot=(0,1,0;2.37122rad)
  shape: bbox 1 x 1 x 1 mm, 2 faces (baked)
FEATURE [Part::Feature] Part__Feature333  label="Bearing Ball, GT2 Timing Idler Pulley, Configurable_1 mm012"
  Placement = pos=(1.69054,9e-16,1.28751) rot=(0,1,0;1.58582rad)
  shape: bbox 1 x 1 x 1 mm, 2 faces (baked)
FEATURE [Part::Feature] Part__Feature334  label="Bearing Ball, GT2 Timing Idler Pulley, Configurable_1 mm013"
  Placement = pos=(0.284984,9e-16,2.1058) rot=(0,1,0;0.80042rad)
  shape: bbox 1 x 1 x 1 mm, 2 faces (baked)
FEATURE [Part::Feature] Part__Feature335  label="Bearing Ball, GT2 Timing Idler Pulley, Configurable_1 mm014"
  Placement = pos=(-1.28751,9e-16,1.69054) rot=(0,1,0;0.015022rad)
  shape: bbox 1 x 1 x 1 mm, 2 faces (baked)
FEATURE [Part::Feature] Part__Feature336  label="Bearing Ball, GT2 Timing Idler Pulley, Configurable_1 mm015"
  Placement = pos=(-2.1058,9e-16,0.284984) rot=(0,-1,0;0.770376rad)
  shape: bbox 1 x 1 x 1 mm, 2 faces (baked)
FEATURE [App::Part] Bearing_Subassy__GT2_Timing_Idler_Pulley__Configurable_3_mm_Bore__6_mm_OD001  label="Bearing Subassy, GT2 Timing Idler Pulley, Configurable_3 mm Bore, 6 mm OD001"
  Group = -> [Part__Feature325,Part__Feature326,Part__Feature327,Part__Feature328,Part__Feature329,Part__Feature330,Part__Feature331,Part__Feature332,Part__Feature333,Part__Feature334,Part__Feature335,Part__Feature336]
  Origin = -> Origin218
  Placement = pos=(-1e-15,-3.25,1.4e-15) rot=(0.886785,0,-0.462182;3.14159rad)
FEATURE [App::Part] GT2_Timing_Idler_Pulley__Configurable__16T_W6_B3_With_T  label="GT2 Timing Idler Pulley, Configurable, 16T W6 B3 With T"
  Group = -> [Part__Feature312,Bearing_Subassy__GT2_Timing_Idler_Pulley__Configurable_3_mm_Bore__6_mm_OD,Bearing_Subassy__GT2_Timing_Idler_Pulley__Configurable_3_mm_Bore__6_mm_OD001]
  Origin = -> Origin219
  Placement = pos=(125,115.1,-4.2) rot=(1,0,0;1.5708rad)
FEATURE [App::Part] Part007  label="A_Idler"
  Group = -> [A_Idler_Bottom_x1,A_Idler_Top_x1,GT2_Timing_Idler_Pulley__Configurable__16T_W6_B3_With_T]
  Origin = -> Origin026
  Placement = pos=(28,-223,132) rot=(0,0,1;0rad)
FEATURE [Part::Feature] Part__Feature337  label="Bearing Ball, GT2 Timing Idler Pulley, Configurable_1 mm016"
  Placement = pos=(-1.28751,1e-15,1.69054) rot=(0,1,0;0.015022rad)
  shape: bbox 1 x 1 x 1 mm, 2 faces (baked)
FEATURE [Part::Feature] Part__Feature338  label="Bearing Ball, GT2 Timing Idler Pulley, Configurable_1 mm017"
  Placement = pos=(1.28751,1e-15,-1.69054) rot=(0,1,0;3.15661rad)
  shape: bbox 1 x 1 x 1 mm, 2 faces (baked)
FEATURE [Part::Feature] Part__Feature339  label="Bearing Ball, GT2 Timing Idler Pulley, Configurable_1 mm018"
  Placement = pos=(-1.69054,0,-1.28751) rot=(0,-1,0;1.55577rad)
  shape: bbox 1 x 1 x 1 mm, 2 faces (baked)
FEATURE [Part::Feature] Part__Feature340  label="Bearing Outer Ring, GT2 Timing Idler Pulley, Configurable_3 mm Bore, 6 mm OD002"
  shape: bbox 6 x 2 x 6 mm, 10 faces (baked)
FEATURE [Part::Feature] Part__Feature341  label="Bearing Ball, GT2 Timing Idler Pulley, Configurable_1 mm019"
  Placement = pos=(-0.284984,1e-15,-2.1058) rot=(0,1,0;3.94201rad)
  shape: bbox 1 x 1 x 1 mm, 2 faces (baked)
FEATURE [Part::Feature] Part__Feature342  label="Bearing Ball, GT2 Timing Idler Pulley, Configurable_1 mm020"
  Placement = pos=(2.1058,1e-15,-0.284984) rot=(0,1,0;2.37122rad)
  shape: bbox 1 x 1 x 1 mm, 2 faces (baked)
FEATURE [Part::Feature] Part__Feature343  label="Bearing Ball, GT2 Timing Idler Pulley, Configurable_1 mm021"
  Placement = pos=(-0.284984,1e-15,-2.1058) rot=(0,1,0;3.94201rad)
  shape: bbox 1 x 1 x 1 mm, 2 faces (baked)
FEATURE [Part::Feature] Part__Feature344  label="Bearing Ball, GT2 Timing Idler Pulley, Configurable_1 mm022"
  Placement = pos=(0.284984,1e-15,2.1058) rot=(0,1,0;0.80042rad)
  shape: bbox 1 x 1 x 1 mm, 2 faces (baked)
FEATURE [Part::Feature] Part__Feature345  label="Bearing Seal, GT2 Timing Idler Pulley, Configurable_3 mm Bore, 6 mm OD004"
  Placement = pos=(0,0.75,0) rot=(0,0,1;0rad)
  shape: bbox 5.412 x 0.571 x 5.412 mm, 10 faces (baked)
FEATURE [Part::Feature] Part__Feature346  label="Bearing Seal, GT2 Timing Idler Pulley, Configurable_3 mm Bore, 6 mm OD005"
  Placement = pos=(0,0.75,0) rot=(0,0,1;0rad)
  shape: bbox 5.412 x 0.571 x 5.412 mm, 10 faces (baked)
FEATURE [Part::Feature] Part__Feature347  label="Bearing Ball, GT2 Timing Idler Pulley, Configurable_1 mm023"
  Placement = pos=(-1.28751,1e-15,1.69054) rot=(0,1,0;0.015022rad)
  shape: bbox 1 x 1 x 1 mm, 2 faces (baked)
FEATURE [Part::Feature] Part__Feature348  label="Bearing Ball, GT2 Timing Idler Pulley, Configurable_1 mm024"
  Placement = pos=(1.28751,1e-15,-1.69054) rot=(0,1,0;3.15661rad)
  shape: bbox 1 x 1 x 1 mm, 2 faces (baked)
FEATURE [Part::Feature] Part__Feature349  label="Bearing Ball, GT2 Timing Idler Pulley, Configurable_1 mm025"
  Placement = pos=(2.1058,1e-15,-0.284984) rot=(0,1,0;2.37122rad)
  shape: bbox 1 x 1 x 1 mm, 2 faces (baked)
FEATURE [Part::Feature] Part__Feature350  label="Bearing Inner Ring, GT2 Timing Idler Pulley, Configurable_3 mm Bore, 6 mm OD002"
  Placement = pos=(0,0,0) rot=(0,-1,0;1.53252rad)
  shape: bbox 3.829 x 2 x 3.829 mm, 12 faces (baked)
FEATURE [Part::Feature] Part__Feature351  label="Body, GT2 Timing Idler Pulley, Configurable_16T W6 B3 With T001"
  Placement = pos=(0,0,0) rot=(0,1,0;4.1025rad)
  shape: bbox 13 x 8.5 x 13 mm, 163 faces (baked)
FEATURE [Part::Feature] Part__Feature352  label="Bearing Outer Ring, GT2 Timing Idler Pulley, Configurable_3 mm Bore, 6 mm OD003"
  shape: bbox 6 x 2 x 6 mm, 10 faces (baked)
FEATURE [Part::Feature] Part__Feature353  label="Bearing Ball, GT2 Timing Idler Pulley, Configurable_1 mm026"
  Placement = pos=(-2.1058,1e-15,0.284984) rot=(0,-1,0;0.770376rad)
  shape: bbox 1 x 1 x 1 mm, 2 faces (baked)
FEATURE [Part::Feature] Part__Feature354  label="Bearing Ball, GT2 Timing Idler Pulley, Configurable_1 mm027"
  Placement = pos=(-1.69054,0,-1.28751) rot=(0,-1,0;1.55577rad)
  shape: bbox 1 x 1 x 1 mm, 2 faces (baked)
FEATURE [Part::Feature] Part__Feature355  label="Bearing Ball, GT2 Timing Idler Pulley, Configurable_1 mm028"
  Placement = pos=(-2.1058,1e-15,0.284984) rot=(0,-1,0;0.770376rad)
  shape: bbox 1 x 1 x 1 mm, 2 faces (baked)
FEATURE [Part::Feature] Part__Feature356  label="Bearing Seal, GT2 Timing Idler Pulley, Configurable_3 mm Bore, 6 mm OD006"
  Placement = pos=(0,-0.75,0) rot=(1,0,0;3.14159rad)
  shape: bbox 5.412 x 0.571 x 5.412 mm, 10 faces (baked)
FEATURE [Part::Feature] Part__Feature357  label="Bearing Ball, GT2 Timing Idler Pulley, Configurable_1 mm029"
  Placement = pos=(1.69054,1e-15,1.28751) rot=(0,1,0;1.58582rad)
  shape: bbox 1 x 1 x 1 mm, 2 faces (baked)
FEATURE [Part::Feature] Part__Feature358  label="Bearing Ball, GT2 Timing Idler Pulley, Configurable_1 mm030"
  Placement = pos=(1.69054,1e-15,1.28751) rot=(0,1,0;1.58582rad)
  shape: bbox 1 x 1 x 1 mm, 2 faces (baked)
FEATURE [Part::Feature] Part__Feature359  label="Bearing Seal, GT2 Timing Idler Pulley, Configurable_3 mm Bore, 6 mm OD007"
  Placement = pos=(0,-0.75,0) rot=(1,0,0;3.14159rad)
  shape: bbox 5.412 x 0.571 x 5.412 mm, 10 faces (baked)
FEATURE [Part::Feature] Part__Feature360  label="Bearing Inner Ring, GT2 Timing Idler Pulley, Configurable_3 mm Bore, 6 mm OD003"
  Placement = pos=(0,0,0) rot=(0,-1,0;1.53252rad)
  shape: bbox 3.829 x 2 x 3.829 mm, 12 faces (baked)
FEATURE [Part::Feature] Part__Feature361  label="Bearing Ball, GT2 Timing Idler Pulley, Configurable_1 mm031"
  Placement = pos=(0.284984,1e-15,2.1058) rot=(0,1,0;0.80042rad)
  shape: bbox 1 x 1 x 1 mm, 2 faces (baked)
FEATURE [App::Part] Bearing_Subassy__GT2_Timing_Idler_Pulley__Configurable_3_mm_Bore__6_mm_OD002  label="Bearing Subassy, GT2 Timing Idler Pulley, Configurable_3 mm Bore, 6 mm OD002"
  Group = -> [Part__Feature352,Part__Feature350,Part__Feature345,Part__Feature356,Part__Feature354,Part__Feature341,Part__Feature348,Part__Feature349,Part__Feature357,Part__Feature361,Part__Feature347,Part__Feature355]
  Origin = -> Origin222
  Placement = pos=(-1e-15,3.25,1.4e-15) rot=(0,1,0;0.960908rad)
FEATURE [App::Part] Bearing_Subassy__GT2_Timing_Idler_Pulley__Configurable_3_mm_Bore__6_mm_OD003  label="Bearing Subassy, GT2 Timing Idler Pulley, Configurable_3 mm Bore, 6 mm OD003"
  Group = -> [Part__Feature340,Part__Feature360,Part__Feature346,Part__Feature359,Part__Feature339,Part__Feature343,Part__Feature338,Part__Feature342,Part__Feature358,Part__Feature344,Part__Feature337,Part__Feature353]
  Origin = -> Origin220
  Placement = pos=(-1e-15,-3.25,1.4e-15) rot=(0.886785,0,-0.462182;3.14159rad)
FEATURE [App::Part] GT2_Timing_Idler_Pulley__Configurable__16T_W6_B3_With_T001  label="GT2 Timing Idler Pulley, Configurable, 16T W6 B3 With T001"
  Group = -> [Part__Feature351,Bearing_Subassy__GT2_Timing_Idler_Pulley__Configurable_3_mm_Bore__6_mm_OD002,Bearing_Subassy__GT2_Timing_Idler_Pulley__Configurable_3_mm_Bore__6_mm_OD003]
  Origin = -> Origin221
  Placement = pos=(-29,-274,-5) rot=(1,0,0;1.5708rad)
FEATURE [App::Part] Part017  label="B_Drive"
  Group = -> [B_Drive_Frame_Bottom_x1,B_Drive_Frame_Top_x1,_a__B_Drive_Tensioner_x1,Part__Feature301,GT2_Timing_Idler_Pulley__Configurable__16T_W6_B3_With_T001]
  Origin = -> Origin038
  Placement = pos=(-123.3,165.4,142) rot=(0,0,1;0rad)
FEATURE [App::Part] Part001  label="frame"
  Group = -> [Part005,Part007,Part008,Part013,Part014,Part017,Part019,Part038,Part053,Part050]
  Origin = -> Origin002
  Placement = pos=(0,-3.4,0) rot=(0,0,1;0rad)
FEATURE [App::Part] Part  label="main"
  Group = -> [Body,Part001,Part029,Part021]
  Origin = -> Origin
